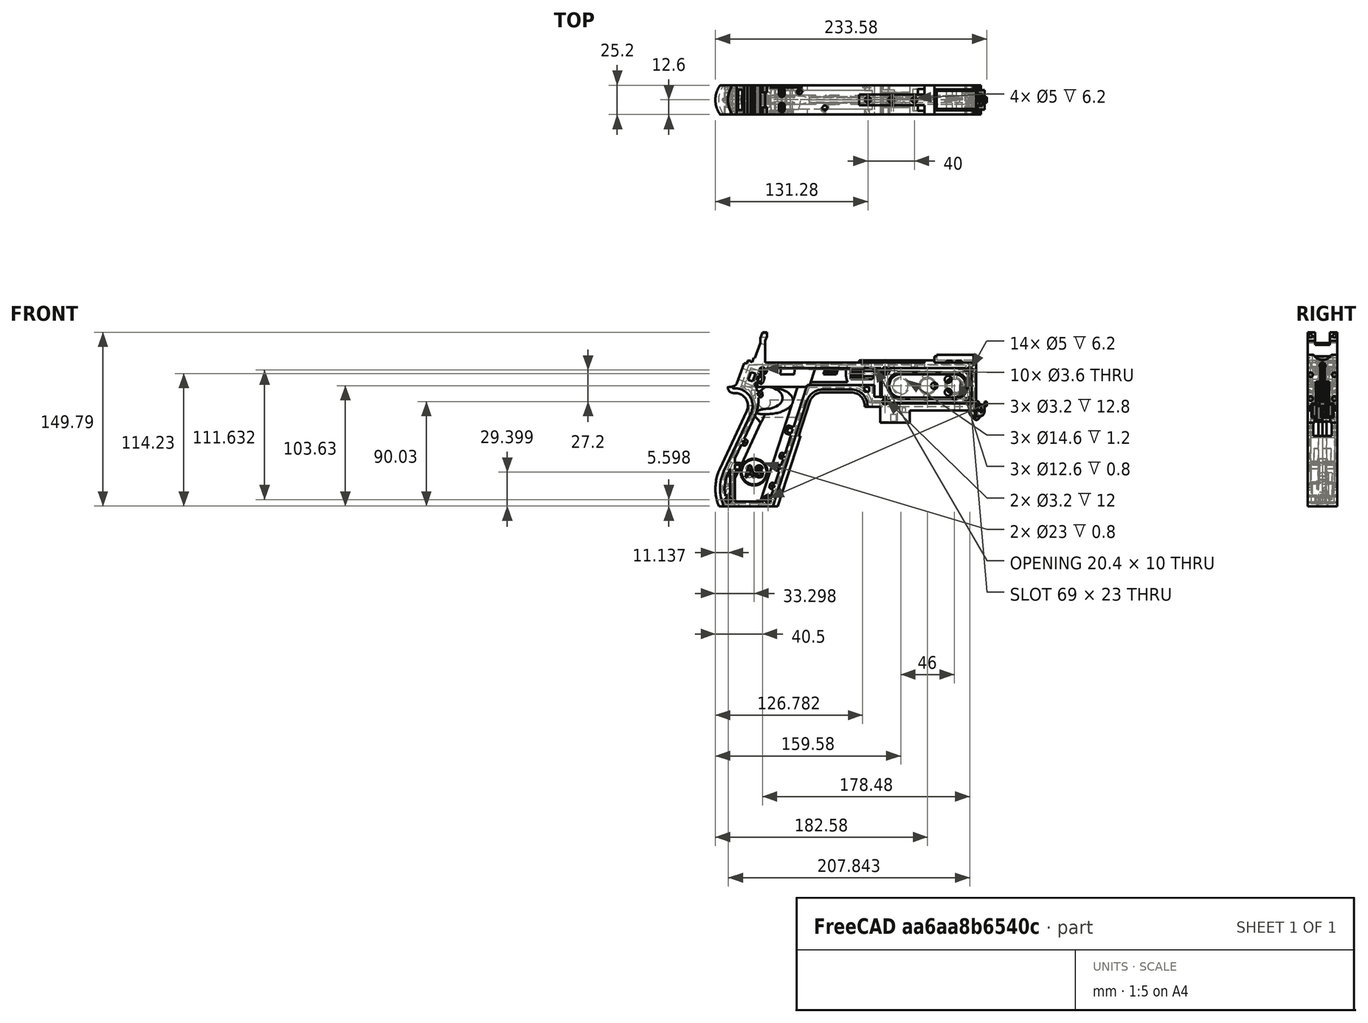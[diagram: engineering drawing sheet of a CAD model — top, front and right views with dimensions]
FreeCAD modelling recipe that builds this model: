
FCSTD DOCUMENT  (FreeCAD 1.0R39319 (Git))
Label: PICON-OF_ver_52
License: All rights reserved
LicenseURL: https://en.wikipedia.org/wiki/All_rights_reserved
objects: Sketcher::SketchObject×123, Part::Extrusion×63, Part::Cut×48, PartDesign::Pad×29, PartDesign::Pocket×20, PartDesign::Chamfer×15, PartDesign::Body×10, PartDesign::Fillet×6, Part::MultiFuse×5, Part::Part2DObjectPython×4, PartDesign::SubtractivePipe×4, PartDesign::SubtractiveLoft×4, PartDesign::Plane×3, PartDesign::SubShapeBinder×2, Part::Sweep×1, PartDesign::ShapeBinder×1, Mesh::Feature×1, PartDesign::Point×1, PartDesign::Groove×1
note: 621 computed .brp shape members not serialized (recipe doc carries the construction recipe); baked Part::Feature solids carry a one-line shape summary decoded from their .brp

FEATURE [Sketcher::SketchObject] Sketch  label="corpo principale"
  ArcFitTolerance = 1e-06
  AttacherType = Attacher::AttachEngine3D
  AttachmentSupport = -> [XZ_Plane]
  FullyConstrained = true
  MakeInternals = false
  MapMode = 5
  Placement = pos=(0,0,0) rot=(1,0,0;1.5708rad)
  sketch-geometry (65):
    g0: LineSegment StartX=0 StartY=0 StartZ=0 EndX=-57.2 EndY=0 EndZ=0
    g1: LineSegment StartX=-57.2 StartY=0 StartZ=0 EndX=-57.2 EndY=-10.4 EndZ=0
    g2: LineSegment StartX=-57.2 StartY=-10.4 StartZ=0 EndX=-82.8 EndY=-10.4 EndZ=0
    g3: LineSegment StartX=-82.8 StartY=-10.4 StartZ=0 EndX=-82.8 EndY=3.2 EndZ=0
    g4: LineSegment StartX=-82.8 StartY=3.2 StartZ=0 EndX=-93.6 EndY=3.2 EndZ=0
    g5: LineSegment StartX=-93.6 StartY=3.2 StartZ=0 EndX=-93.6 EndY=4 EndZ=0
    g6: LineSegment StartX=-107.6 StartY=18 StartZ=0 EndX=-132.428 EndY=18 EndZ=0
    g7: LineSegment StartX=-145.743 StartY=8.32624 StartZ=0 EndX=-175.232 EndY=-82.4316 EndZ=0
    g8: LineSegment StartX=-175.232 StartY=-82.4316 StartZ=0 EndX=-217.232 EndY=-82.4316 EndZ=0
    g9: LineSegment StartX=-217.232 StartY=-52.1862 StartZ=0 EndX=-193.988 EndY=-2.33927 EndZ=0
    g10: LineSegment StartX=-206.196 StartY=23.0857 StartZ=0 EndX=-199.861 EndY=40.4914 EndZ=0
    g11: LineSegment StartX=-199.861 StartY=40.4914 StartZ=0 EndX=-197.061 EndY=40.4914 EndZ=0
    g12: LineSegment StartX=-197.061 StartY=40.4914 StartZ=0 EndX=-197.061 EndY=42.8914 EndZ=0
    g13: LineSegment StartX=-197.061 StartY=42.8914 StartZ=0 EndX=-194.261 EndY=42.8914 EndZ=0
    g14: LineSegment StartX=-194.261 StartY=42.8914 StartZ=0 EndX=-194.535 EndY=42.1397 EndZ=0
    g15: LineSegment StartX=-194.535 StartY=42.1397 StartZ=0 EndX=-193.031 EndY=41.5924 EndZ=0
    g16: LineSegment StartX=-193.031 StartY=41.5924 StartZ=0 EndX=-191.663 EndY=45.3512 EndZ=0
    g17: LineSegment StartX=-191.663 StartY=45.3512 StartZ=0 EndX=-190.536 EndY=44.9408 EndZ=0
    g18: LineSegment StartX=-190.536 StartY=44.9408 StartZ=0 EndX=-185.747 EndY=58.0965 EndZ=0
    g19: LineSegment StartX=-185.747 StartY=58.0965 StartZ=0 EndX=-185.747 EndY=62.0965 EndZ=0
    g20: LineSegment StartX=-185.747 StartY=62.0965 StartZ=0 EndX=-183.832 EndY=67.3588 EndZ=0
    g21: LineSegment StartX=-183.832 StartY=67.3588 StartZ=0 EndX=-180.232 EndY=67.3588 EndZ=0
    g22: LineSegment StartX=-180.232 StartY=67.3588 StartZ=0 EndX=-180.232 EndY=63.7588 EndZ=0
    g23: LineSegment StartX=-180.232 StartY=63.7588 StartZ=0 EndX=-181.6 EndY=60 EndZ=0
    g24: LineSegment StartX=-181.6 StartY=60 StartZ=0 EndX=-181.6 EndY=41.2 EndZ=0
    g25: LineSegment StartX=-181.6 StartY=41.2 StartZ=0 EndX=-100.8 EndY=41.2 EndZ=0
    g26: LineSegment StartX=-36 StartY=43.2 StartZ=0 EndX=-36 EndY=41.2 EndZ=0
    g27: LineSegment StartX=0 StartY=48 StartZ=0 EndX=0 EndY=0 EndZ=0
    g28: LineSegment StartX=-209.901 StartY=19.85 StartZ=0 EndX=-209.901 EndY=20.1 EndZ=0
    g29: LineSegment StartX=-208.001 StartY=22 StartZ=0 EndX=-207.747 EndY=22 EndZ=0
    g30: LineSegment StartX=-207.583 StartY=19 StartZ=0 EndX=-209.051 EndY=19 EndZ=0
    g31: ArcOfCircle CenterX=-208.001 CenterY=20.1 CenterZ=0 NormalX=0 NormalY=0 NormalZ=1 AngleXU=0 Radius=1.9 StartAngle=1.5708 EndAngle=3.14159
    g32: GeomPoint [constr] X=-209.901 Y=22 Z=0
    g33: ArcOfCircle CenterX=-209.051 CenterY=19.85 CenterZ=0 NormalX=0 NormalY=0 NormalZ=1 AngleXU=0 Radius=0.85 StartAngle=3.14159 EndAngle=4.71239
    g34: GeomPoint [constr] X=-209.901 Y=19 Z=0
    g35: ArcOfCircle CenterX=-207.747 CenterY=23.65 CenterZ=0 NormalX=0 NormalY=0 NormalZ=1 AngleXU=0 Radius=1.65 StartAngle=4.71239 EndAngle=5.93412
    g36: GeomPoint [constr] X=-206.591 Y=22 Z=0
    g37: LineSegment StartX=-4 StartY=6 StartZ=0 EndX=-4 EndY=36.4 EndZ=0
    g38: LineSegment StartX=-4 StartY=36.4 StartZ=0 EndX=-185.2 EndY=36.4 EndZ=0
    g39: LineSegment StartX=-185.2 StartY=36.4 StartZ=0 EndX=-190.441 EndY=22 EndZ=0
    g40: LineSegment StartX=-214.575 StartY=-78.4316 StartZ=0 EndX=-178.142 EndY=-78.4316 EndZ=0
    g41: LineSegment StartX=-178.142 StartY=-78.4316 StartZ=0 EndX=-145.51 EndY=22 EndZ=0
    g42: LineSegment StartX=-145.51 StartY=22 StartZ=0 EndX=-87.91 EndY=22 EndZ=0
    g43: LineSegment StartX=-87.91 StartY=22 StartZ=0 EndX=-87.91 EndY=11.6 EndZ=0
    g44: LineSegment StartX=-87.91 StartY=11.6 StartZ=0 EndX=-80.11 EndY=11.6 EndZ=0
    g45: LineSegment StartX=-80.11 StartY=11.6 StartZ=0 EndX=-80.11 EndY=6 EndZ=0
    g46: LineSegment StartX=-80.11 StartY=6 StartZ=0 EndX=-4 EndY=6 EndZ=0
    g47: LineSegment StartX=-190.363 StartY=-4.02975 StartZ=0 EndX=-213.607 EndY=-53.8767 EndZ=0
    g48: ArcOfCircle CenterX=-132.428 CenterY=4 CenterZ=0 NormalX=0 NormalY=0 NormalZ=1 AngleXU=0 Radius=14 StartAngle=1.5708 EndAngle=2.82743
    g49: GeomPoint [constr] X=-142.6 Y=18 Z=0
    g50: ArcOfCircle CenterX=-107.6 CenterY=4 CenterZ=0 NormalX=0 NormalY=0 NormalZ=1 AngleXU=0 Radius=14 StartAngle=0 EndAngle=1.5708
    g51: GeomPoint [constr] X=-93.6 Y=18 Z=0
    g52: ArcOfCircle CenterX=-184.801 CenterY=-67.3089 CenterZ=0 NormalX=0 NormalY=0 NormalZ=1 AngleXU=0 Radius=35.7833 StartAngle=2.70526 EndAngle=3.57792
    g53: ArcOfCircle CenterX=-207.583 CenterY=4 CenterZ=0 NormalX=0 NormalY=0 NormalZ=1 AngleXU=0 Radius=15 StartAngle=5.84685 EndAngle=7.85398
    g54: LineSegment [constr] StartX=-213.607 StartY=-53.8767 StartZ=0 EndX=-217.232 EndY=-52.1862 EndZ=0
    g55: ArcOfCircle CenterX=-184.801 CenterY=-67.3089 CenterZ=0 NormalX=0 NormalY=0 NormalZ=1 AngleXU=0 Radius=31.7833 StartAngle=2.70526 EndAngle=3.49911
    g56: ArcOfCircle CenterX=-218.095 CenterY=8.90192 CenterZ=0 NormalX=0 NormalY=0 NormalZ=1 AngleXU=0 Radius=30.5989 StartAngle=5.84685 EndAngle=6.72553
    g57: LineSegment StartX=-44.6 StartY=43.2 StartZ=0 EndX=-36 EndY=43.2 EndZ=0
    g58: LineSegment StartX=-100.8 StartY=41.2 StartZ=0 EndX=-44.6 EndY=41.2 EndZ=0
    g59: LineSegment StartX=-44.6 StartY=41.2 StartZ=0 EndX=-44.6 EndY=43.2 EndZ=0
    g60: LineSegment StartX=-2.4 StartY=48 StartZ=0 EndX=0 EndY=48 EndZ=0
    g61: LineSegment StartX=-36 StartY=41.2 StartZ=0 EndX=-2.4 EndY=41.2 EndZ=0
    g62: LineSegment StartX=-2.4 StartY=41.2 StartZ=0 EndX=-2.4 EndY=48 EndZ=0
    g63: LineSegment [constr] StartX=-181.6 StartY=36.4 StartZ=0 EndX=-152.209 EndY=36.4 EndZ=0
    g64: LineSegment [constr] StartX=-181.6 StartY=36.4 StartZ=0 EndX=-130.41 EndY=36.4 EndZ=0
  constraints (183):
    c: Coincident(g-1,g0)
    c: PointOnObject(g0,g-1)
    c: Coincident(g0,g1)
    c: Vertical(g1)
    c: Coincident(g1,g2)
    c: Horizontal(g2)
    c: Coincident(g2,g3)
    c: Vertical(g3)
    c: Coincident(g3,g4)
    c: Coincident(g4,g5)
    c: Vertical(g5)
    c: Horizontal(g6)
    c: Coincident(g7,g8)
    c: Horizontal(g8)
    c: Coincident(g10,g11)
    c: Horizontal(g11)
    c: Coincident(g11,g12)
    c: Vertical(g12)
    c: Coincident(g12,g13)
    c: Horizontal(g13)
    c: Coincident(g13,g14)
    c: Coincident(g14,g15)
    c: Coincident(g15,g16)
    c: Coincident(g16,g17)
    c: Coincident(g17,g18)
    c: Coincident(g18,g19)
    c: Vertical(g19)
    c: Coincident(g19,g20)
    c: Coincident(g20,g21)
    c: Horizontal(g21)
    c: Coincident(g21,g22)
    c: Vertical(g22)
    c: Coincident(g22,g23)
    c: Coincident(g23,g24)
    c: Vertical(g24)
    c: Coincident(g24,g25)
    c: Horizontal(g25)
    c: Coincident(g57,g26)
    c: Vertical(g26)
    c: Coincident(g26,g61)
    c: PointOnObject(g60,g-2)
    c: Coincident(g60,g27)
    c: Coincident(g27,g0)
    c: DistanceY(g27,g27) = 48
    c: DistanceY(g1,g1) = 10.4
    c: DistanceX(g0,g0) = 57.2
    c: DistanceX(g2,g2) = 25.6
    c: Horizontal(g4)
    c: DistanceY(g3,g3) = 13.6
    c: DistanceX(g4,g4) = 10.8
    c: DistanceY(g5,g51) = 14.8
    c: DistanceX(g49,g51) = 49
    c: Distance(g7,g49) = 105.6
    c: DistanceX(g61,g60) = 36
    c: DistanceX(g25,g25) = 80.8
    c: DistanceY(g24,g24) = 18.8
    c: DistanceY(g22,g22) = 3.6
    c: Distance(g23) = 4
    c: Angle(g-1,g23) = 1.22173
    c: DistanceX(g21,g21) = 3.6
    c: Distance(g20) = 5.6
    c: Angle(g-1,g20) = 1.22173
    c: DistanceY(g19,g19) = 4
    c: Distance(g18) = 14
    c: Angle(g-1,g18) = 1.22173
    c: Distance(g17) = 1.2
    c: Distance(g16) = 4
    c: Angle(g16) = 1.22173
    c: Perpendicular(g18,g17)
    c: Distance(g15) = 1.6
    c: Perpendicular(g16,g15)
    c: Distance(g14) = 0.8
    c: DistanceX(g13,g13) = 2.8
    c: Perpendicular(g15,g14)
    c: DistanceY(g12,g12) = 2.4
    c: DistanceX(g11,g11) = 2.8
    c: Distance(g9) = 55
    c: Angle(g9,g-1) = 2.00713
    c: Horizontal(g29)
    c: Vertical(g28)
    c: Horizontal(g30)
    c: PointOnObject(g32,g29)
    c: PointOnObject(g32,g28)
    c: Tangent(g29,g31) = 1.5708
    c: Tangent(g28,g31) = 1.5708
    c: PointOnObject(g34,g28)
    c: PointOnObject(g34,g30)
    c: Tangent(g28,g33) = 1.5708
    c: Tangent(g30,g33) = 1.5708
    c: PointOnObject(g36,g29)
    c: PointOnObject(g36,g10)
    c: Tangent(g29,g35) = -1.5708
    c: Tangent(g10,g35) = -1.5708
    c: Angle(g-1,g10) = 1.22173
    c: Radius(g35) = 1.65
    c: Vertical(g37)
    c: Coincident(g37,g38)
    c: Horizontal(g38)
    c: Coincident(g38,g39)
    c: Horizontal(g40)
    c: Coincident(g40,g41)
    c: Coincident(g41,g42)
    c: Horizontal(g42)
    c: Coincident(g42,g43)
    c: Vertical(g43)
    c: Coincident(g43,g44)
    c: Horizontal(g44)
    c: Coincident(g44,g45)
    c: Vertical(g45)
    c: Coincident(g45,g46)
    c: Coincident(g46,g37)
    c: Horizontal(g46)
    c: DistanceY(g0,g37) = 6
    c: DistanceX(g37,g0) = 4
    c: DistanceY(g37,g25) = 4.8
    c: DistanceX(g38,g38) = 181.2
    c: DistanceX(g42,g42) = 57.6
    c: DistanceY(g49,g41) = 4
    c: DistanceX(g41,g49) = 2.91
    c: DistanceY(g43,g43) = 10.4
    c: DistanceX(g44,g44) = 7.8
    c: DistanceY(g7,g40) = 4
    c: Distance(g47) = 55
    c: Angle(g-1,g39) = 1.22173
    c: PointOnObject(g49,g7)
    c: PointOnObject(g49,g6)
    c: Tangent(g7,g48) = -1.5708
    c: Tangent(g6,g48) = -1.5708
    c: PointOnObject(g51,g5)
    c: PointOnObject(g51,g6)
    c: Tangent(g5,g50) = -1.5708
    c: Tangent(g6,g50) = -1.5708
    c: Radius(g50) = 14
    c: Radius(g48) = 14
    c: DistanceX(g8,g8) = 42
    c: Angle(g7,g-1) = 1.88496
    c: Parallel(g41,g7)
    c: Parallel(g47,g9)
    c: Coincident(g52,g8)
    c: Tangent(g52,g9) = 1.5708
    c: DistanceX(g9,g8) = 0
    c: Tangent(g53,g9) = -1.5708
    c: Tangent(g53,g30) = -1.5708
    c: Diameter(g53) = 30
    c: DistanceY(g53,g0) = -4
    c: Coincident(g54,g47)
    c: Distance(g54) = 4
    c: Coincident(g54,g9)
    c: Coincident(g55,g40)
    c: Tangent(g55,g47) = -1.5708
    c: Coincident(g52,g55)
    c: Coincident(g56,g39)
    c: Tangent(g56,g47) = 1.5708
    c: Horizontal(g57)
    c: DistanceX(g57,g57) = 8.6
    c: Coincident(g58,g25)
    c: Horizontal(g58)
    c: Coincident(g59,g58)
    c: Vertical(g59)
    c: DistanceY(g58,g57) = 2
    c: DistanceX(g58,g58) = 56.2
    c: Coincident(g59,g57)
    c: DistanceY(g41,g36) = 0
    c: DistanceY(g36,g39) = 0
    c: DistanceY(g28,g28) = 0.25
    c: DistanceX(g30,g36) = 2.46
    c: DistanceX(g28,g29) = 1.9
    c: Coincident(g62,g60)
    c: Horizontal(g60)
    c: DistanceX(g62,g27) = 2.4
    c: Coincident(g61,g62)
    c: DistanceY(g26,g26) = 2
    c: Vertical(g62)
    c: DistanceY(g61,g60) = 6.8
    c: Horizontal(g61)
    c: Distance(g63) = 29.391
    c: PointOnObject(g63,g38)
    c: PointOnObject(g63,g38)
    c: Distance(g64) = 51.19
    c: PointOnObject(g64,g38)
    c: PointOnObject(g64,g38)
    c: DistanceX(g24,g63) = 0
    c: DistanceX(g24,g64) = 0
FEATURE [Part::Extrusion] Extrude  label="Extrude corpo principale"
  Base = -> Sketch
  Dir = (0,-1,2e-16)
  DirMode = 2
  FaceMakerClass = Part::FaceMakerBullseye
  FaceMakerMode = 3
  LengthFwd = 25.2
  LengthRev = 12.6
  Solid = true
  Symmetric = true
FEATURE [Sketcher::SketchObject] Sketch002  label="scavo grilletto"
  ArcFitTolerance = 1e-06
  AttachmentSupport = -> [XZ_Plane]
  ExternalGeometry = -> [Sketch]
  FullyConstrained = true
  MakeInternals = false
  MapMode = 5
  Placement = pos=(0,0,0) rot=(1,0,0;1.5708rad)
  sketch-geometry (4):
    g0: LineSegment StartX=-89.51 StartY=22 StartZ=0 EndX=-152.71 EndY=22 EndZ=0
    g1: LineSegment StartX=-152.71 StartY=22 StartZ=0 EndX=-167.006 EndY=-22 EndZ=0
    g2: LineSegment StartX=-167.006 StartY=-22 StartZ=0 EndX=-89.51 EndY=-22 EndZ=0
    g3: LineSegment StartX=-89.51 StartY=-22 StartZ=0 EndX=-89.51 EndY=22 EndZ=0
  constraints (12):
    c: Horizontal(g0)
    c: Coincident(g0,g1)
    c: Coincident(g1,g2)
    c: Horizontal(g2)
    c: Coincident(g2,g3)
    c: Coincident(g3,g0)
    c: Vertical(g3)
    c: Angle(g1,g0) = 1.88496
    c: DistanceY(g3,g3) = 44
    c: DistanceX(g0,g0) = 63.2
    c: DistanceX(g0,g-3) = 1.6
    c: DistanceY(g-3,g0) = 0
FEATURE [Sketcher::SketchObject] Sketch004  label="traiettoria arrotondamento impugnatura anteriore"
  ArcFitTolerance = 1e-06
  AttachmentSupport = -> [XZ_Plane]
  ExternalGeometry = -> [Sketch]
  FullyConstrained = true
  MakeInternals = false
  MapMode = 5
  Placement = pos=(0,0,0) rot=(1,0,0;1.5708rad)
  sketch-geometry (13):
    g0: LineSegment StartX=-175.232 StartY=-82.4316 StartZ=0 EndX=-145.743 EndY=8.32624 EndZ=0
    g1: LineSegment StartX=-93.6 StartY=3.2 StartZ=0 EndX=-93.6 EndY=4 EndZ=0
    g2: LineSegment StartX=-132.428 StartY=18 StartZ=0 EndX=-107.6 EndY=18 EndZ=0
    g3: ArcOfCircle CenterX=-132.428 CenterY=4 CenterZ=0 NormalX=0 NormalY=0 NormalZ=1 AngleXU=0 Radius=14 StartAngle=1.5708 EndAngle=2.82743
    g4: ArcOfCircle CenterX=-107.6 CenterY=4 CenterZ=0 NormalX=0 NormalY=0 NormalZ=1 AngleXU=0 Radius=14 StartAngle=0 EndAngle=1.5708
    g5: LineSegment StartX=-175.232 StartY=-82.4316 StartZ=0 EndX=-217.232 EndY=-82.4316 EndZ=0
    g6: LineSegment StartX=-217.232 StartY=-52.1862 StartZ=0 EndX=-193.988 EndY=-2.33927 EndZ=0
    g7: LineSegment StartX=-209.051 StartY=19 StartZ=0 EndX=-207.583 EndY=19 EndZ=0
    g8: LineSegment StartX=-209.901 StartY=20.1 StartZ=0 EndX=-209.901 EndY=19.85 EndZ=0
    g9: ArcOfCircle CenterX=-184.801 CenterY=-67.3089 CenterZ=0 NormalX=0 NormalY=0 NormalZ=1 AngleXU=0 Radius=35.7833 StartAngle=2.70526 EndAngle=3.57792
    g10: ArcOfCircle CenterX=-207.583 CenterY=4 CenterZ=0 NormalX=0 NormalY=0 NormalZ=1 AngleXU=0 Radius=15 StartAngle=5.84685 EndAngle=7.85398
    g11: ArcOfCircle CenterX=-209.051 CenterY=19.85 CenterZ=0 NormalX=0 NormalY=0 NormalZ=1 AngleXU=0 Radius=0.85 StartAngle=3.14159 EndAngle=4.71239
    g12: ArcOfCircle CenterX=-208.001 CenterY=20.1 CenterZ=0 NormalX=0 NormalY=0 NormalZ=1 AngleXU=0 Radius=1.9 StartAngle=1.5708 EndAngle=3.14159
  constraints (26):
    c: Coincident(g0,g-3)
    c: Coincident(g0,g-6)
    c: Coincident(g1,g-8)
    c: Coincident(g1,g-7)
    c: Coincident(g2,g-5)
    c: Coincident(g2,g-4)
    c: Coincident(g3,g2)
    c: Tangent(g3,g0) = 1.5708
    c: Coincident(g4,g1)
    c: Tangent(g4,g2) = 1.5708
    c: Coincident(g5,g0)
    c: Coincident(g5,g-9)
    c: Coincident(g6,g-12)
    c: Coincident(g6,g-11)
    c: Coincident(g7,g-15)
    c: Coincident(g7,g-14)
    c: Coincident(g8,g-16)
    c: Coincident(g8,g-17)
    c: Tangent(g9,g6) = 1.5708
    c: Coincident(g9,g5)
    c: Coincident(g10,g7)
    c: Tangent(g10,g6) = -1.5708
    c: Tangent(g11,g7) = -1.5708
    c: Coincident(g11,g8)
    c: Tangent(g12,g8) = -1.5708
    c: Coincident(g12,g-17)
FEATURE [PartDesign::Plane] DatumPlane  label="Piano per disegno arrotondamento impugnatura"
  AttachmentSupport = -> [Sketch]
  Length = 73.6581
  MapMode = 7
  Placement = pos=(-145.743,1.8e-15,8.32624) rot=(0.154555,0.154555,0.97582;1.59527rad)
  ResizeMode = 0
  Width = 303.511
FEATURE [Sketcher::SketchObject] Sketch005  label="forma arrotondamento impugnatura anteriore"
  ArcFitTolerance = 1e-06
  AttachmentSupport = -> [DatumPlane]
  FullyConstrained = true
  MakeInternals = false
  MapMode = 5
  Placement = pos=(-145.743,1.8e-15,8.32624) rot=(0.154555,0.154555,0.97582;1.59527rad)
  sketch-geometry (5):
    g0: GeomPoint [constr] X=0 Y=-4 Z=0
    g1: GeomPoint [constr] X=-12.6 Y=7.1e-15 Z=0
    g2: GeomPoint [constr] X=12.6 Y=4.97e-14 Z=0
    g3: LineSegment StartX=-12.6 StartY=7.1e-15 StartZ=0 EndX=12.6 EndY=4.97e-14 EndZ=0
    g4: ArcOfCircle CenterX=-3.88e-14 CenterY=17.845 CenterZ=0 NormalX=0 NormalY=0 NormalZ=1 AngleXU=0 Radius=21.845 StartAngle=4.09759 EndAngle=5.32718
  constraints (11):
    c: DistanceY(g0,g-1) = 4
    c: DistanceX(g-1,g0) = 0
    c: DistanceX(g1,g-1) = 12.6
    c: DistanceX(g-1,g2) = 12.6
    c: DistanceY(g-1,g2) = 0
    c: DistanceY(g-1,g1) = 0
    c: Coincident(g3,g1)
    c: Coincident(g3,g2)
    c: Coincident(g4,g1)
    c: Coincident(g4,g2)
    c: PointOnObject(g0,g4)
FEATURE [Part::Sweep] Sweep  label="Sweep impugnatura"
  Frenet = true
  Sections = -> [Sketch005]
  Solid = true
  Spine = -> Sketch [Edge32,Edge33,Edge34,Edge35,Edge36,Edge37,Edge38,Edge39,Edge40,Edge41,Edge42,Edge43,Edge44]
  Transition = 1
FEATURE [Sketcher::SketchObject] Sketch008  label="buchi e pulizie varie"
  ArcFitTolerance = 1e-06
  AttachmentSupport = -> [XZ_Plane]
  ExternalGeometry = -> [Sketch]
  FullyConstrained = true
  MakeInternals = false
  MapMode = 5
  Placement = pos=(0,0,0) rot=(1,0,0;1.5708rad)
  sketch-geometry (26):
    g0: LineSegment StartX=-96.278 StartY=20.155 StartZ=0 EndX=-92.278 EndY=20.155 EndZ=0
    g1: LineSegment StartX=-92.278 StartY=20.155 StartZ=0 EndX=-92.278 EndY=16.155 EndZ=0
    g2: LineSegment StartX=-92.278 StartY=16.155 StartZ=0 EndX=-96.278 EndY=16.155 EndZ=0
    g3: LineSegment StartX=-96.278 StartY=16.155 StartZ=0 EndX=-96.278 EndY=20.155 EndZ=0
    g4: LineSegment StartX=-222.232 StartY=-82.4316 StartZ=0 EndX=-170.232 EndY=-82.4316 EndZ=0
    g5: LineSegment StartX=-170.232 StartY=-82.4316 StartZ=0 EndX=-170.232 EndY=-86.4316 EndZ=0
    g6: LineSegment StartX=-170.232 StartY=-86.4316 StartZ=0 EndX=-222.232 EndY=-86.4316 EndZ=0
    g7: LineSegment StartX=-222.232 StartY=-86.4316 StartZ=0 EndX=-222.232 EndY=-82.4316 EndZ=0
    g8: LineSegment StartX=-213.901 StartY=20.1 StartZ=0 EndX=-213.901 EndY=26 EndZ=0
    g9: LineSegment StartX=-213.901 StartY=26 StartZ=0 EndX=-206.196 EndY=26 EndZ=0
    g10: LineSegment StartX=-17.4 StartY=42.8 StartZ=0 EndX=-12.4 EndY=42.8 EndZ=0
    g11: LineSegment StartX=-12.4 StartY=42.8 StartZ=0 EndX=-12.4 EndY=41.2 EndZ=0
    g12: LineSegment StartX=-12.4 StartY=41.2 StartZ=0 EndX=-17.4 EndY=41.2 EndZ=0
    g13: LineSegment StartX=-17.4 StartY=41.2 StartZ=0 EndX=-17.4 EndY=42.8 EndZ=0
    g14: LineSegment StartX=-25.9 StartY=42.8 StartZ=0 EndX=-20.9 EndY=42.8 EndZ=0
    g15: LineSegment StartX=-20.9 StartY=42.8 StartZ=0 EndX=-20.9 EndY=41.2 EndZ=0
    g16: LineSegment StartX=-20.9 StartY=41.2 StartZ=0 EndX=-25.9 EndY=41.2 EndZ=0
    g17: LineSegment StartX=-25.9 StartY=41.2 StartZ=0 EndX=-25.9 EndY=42.8 EndZ=0
    g18: GeomPoint [constr] X=-206.196 Y=23.0857 Z=0
    g19: GeomPoint [constr] X=-213.901 Y=20.1 Z=0
    g20: BSplineCurve PolesCount=4 KnotsCount=2 Degree=3 IsPeriodic=0
    g21-g24: Circle [constr] x4 (B-spline internal-alignment scaffolding for g20; pole/knot coordinates omitted)
    g25: LineSegment StartX=-206.196 StartY=26 StartZ=0 EndX=-206.196 EndY=23.0857 EndZ=0
  constraints (73):
    c: Horizontal(g0)
    c: Coincident(g1,g0)
    c: Vertical(g1)
    c: Coincident(g2,g1)
    c: Horizontal(g2)
    c: Coincident(g3,g2)
    c: Coincident(g3,g0)
    c: Vertical(g3)
    c: DistanceX(g0,g-4) = 4.368
    c: DistanceY(g0,g-4) = 1.845
    c: DistanceY(g1,g1) = 4
    c: DistanceX(g2,g2) = 4
    c: Horizontal(g4)
    c: Coincident(g5,g4)
    c: Vertical(g5)
    c: Coincident(g6,g5)
    c: Horizontal(g6)
    c: Coincident(g7,g6)
    c: Coincident(g7,g4)
    c: Vertical(g7)
    c: DistanceY(g7,g7) = 4
    c: DistanceX(g4,g-5) = 5
    c: DistanceX(g-5,g4) = 5
    c: DistanceY(g4,g-5) = 0
    c: Coincident(g9,g8)
    c: Parallel(g9,g-6)
    c: DistanceX(g8,g-8) = 4
    c: Horizontal(g10)
    c: Coincident(g11,g10)
    c: Vertical(g11)
    c: Coincident(g12,g11)
    c: Horizontal(g12)
    c: Coincident(g13,g12)
    c: Coincident(g13,g10)
    c: Vertical(g13)
    c: Horizontal(g14)
    c: Coincident(g15,g14)
    c: Vertical(g15)
    c: Coincident(g16,g15)
    c: Horizontal(g16)
    c: Coincident(g17,g16)
    c: Coincident(g17,g14)
    c: Vertical(g17)
    c: DistanceY(g11,g10) = 1.6
    c: DistanceX(g10,g10) = 5
    c: DistanceY(g15,g14) = 1.6
    c: DistanceX(g14,g14) = 5
    c: DistanceX(g15,g12) = 3.5
    c: DistanceX(g11,g-9) = 10
    c: DistanceY(g-9,g11) = 0
    c: DistanceY(g-9,g15) = 0
    c: Perpendicular(g8,g9)
    c: DistanceY(g-7,g9) = 4
    c: DistanceY(g8,g-8) = 0
    c: InternalAlignment(g18,g20)
    c: InternalAlignment(g19,g20)
    c: InternalAlignment(g21,g20)
    c: Weight(g21) = 1
    c: InternalAlignment(g22,g20)
    c: Equal(g22,g21)
    c: InternalAlignment(g23,g20)
    c: Equal(g23,g21)
    c: InternalAlignment(g24,g20)
    c: Equal(g24,g21)
    c: Coincident(g18,g-12)
    c: Coincident(g19,g8)
    c: Coincident(g25,g9)
    c: Coincident(g25,g20)
    c: Vertical(g25)
    c: DistanceY(g20,g23) = 0
    c: DistanceY(g22,g18) = 2.26
    c: DistanceX(g22,g18) = 0.93
    c: DistanceX(g20,g23) = 2.9
FEATURE [Part::Extrusion] Extrude004  label="Extrude Buchi e pulizie varie"
  Base = -> Sketch008
  Dir = (0,-1,2e-16)
  DirMode = 2
  FaceMakerClass = Part::FaceMakerBullseye
  FaceMakerMode = 3
  LengthFwd = 25.2
  LengthRev = 0
  Solid = true
  Symmetric = true
FEATURE [Sketcher::SketchObject] Sketch009  label="rinforzi"
  ArcFitTolerance = 1e-06
  AttachmentSupport = -> [XZ_Plane]
  ExternalGeometry = -> [Sketch]
  FullyConstrained = true
  MakeInternals = false
  MapMode = 5
  Placement = pos=(0,0,0) rot=(1,0,0;1.5708rad)
  sketch-geometry (9):
    g0: LineSegment StartX=-87.91 StartY=22 StartZ=0 EndX=-87.91 EndY=36.4 EndZ=0
    g1: LineSegment StartX=-87.91 StartY=36.4 StartZ=0 EndX=-97.91 EndY=36.4 EndZ=0
    g2: LineSegment StartX=-97.91 StartY=36.4 StartZ=0 EndX=-97.91 EndY=22 EndZ=0
    g3: LineSegment StartX=-97.91 StartY=22 StartZ=0 EndX=-87.91 EndY=22 EndZ=0
    g4: LineSegment StartX=-149.713 StartY=9.06563 StartZ=0 EndX=-154.586 EndY=-5.93437 EndZ=0
    g5: LineSegment StartX=-154.586 StartY=-5.93437 StartZ=0 EndX=-191.863 EndY=-5.93437 EndZ=0
    g6: LineSegment StartX=-191.863 StartY=-5.93437 StartZ=0 EndX=-191.863 EndY=9.06563 EndZ=0
    g7: LineSegment StartX=-191.863 StartY=9.06563 StartZ=0 EndX=-149.713 EndY=9.06563 EndZ=0
    g8: LineSegment [constr] StartX=-145.51 StartY=22 StartZ=0 EndX=-149.713 EndY=9.06563 EndZ=0
  constraints (25):
    c: Vertical(g0)
    c: Coincident(g1,g0)
    c: Horizontal(g1)
    c: Coincident(g2,g1)
    c: Vertical(g2)
    c: Coincident(g3,g2)
    c: Coincident(g3,g0)
    c: Horizontal(g3)
    c: Coincident(g0,g-4)
    c: DistanceX(g3,g3) = 10
    c: DistanceY(g0,g-3) = 0
    c: Coincident(g5,g4)
    c: Horizontal(g5)
    c: Coincident(g6,g5)
    c: Vertical(g6)
    c: Coincident(g7,g6)
    c: Coincident(g7,g4)
    c: Horizontal(g7)
    c: Distance(g8) = 13.6
    c: Parallel(g-6,g8)
    c: Coincident(g-6,g8)
    c: Parallel(g4,g-6)
    c: DistanceY(g4,g4) = 15
    c: Coincident(g4,g8)
    c: DistanceX(g-5,g5) = -1.5
FEATURE [Part::Extrusion] Extrude001  label="Extrude scavo grilletto"
  Base = -> Sketch002
  Dir = (0,-1,2e-16)
  DirMode = 2
  FaceMakerClass = Part::FaceMakerBullseye
  FaceMakerMode = 3
  LengthFwd = 16
  LengthRev = 0
  Solid = true
  Symmetric = true
FEATURE [Part::Extrusion] Extrude005  label="Extrude Rinforzi"
  Base = -> Sketch009
  Dir = (0,-1,2e-16)
  DirMode = 2
  FaceMakerClass = Part::FaceMakerBullseye
  FaceMakerMode = 3
  LengthFwd = 2
  LengthRev = 0
  Placement = pos=(0,12.6,0) rot=(0,0,1;0rad)
  Solid = true
  Symmetric = false
FEATURE [PartDesign::ShapeBinder] CopyCut
  TraceSupport = false
FEATURE [PartDesign::Plane] DatumPlane001
  AttachmentSupport = -> [CopyCut]
  Length = 283.944
  MapMode = 5
  Placement = pos=(0,12.6,0) rot=(0,0.707107,0.707107;3.14159rad)
  ResizeMode = 0
  Width = 188.15
FEATURE [Sketcher::SketchObject] Sketch010  label="buco neopixel"
  ArcFitTolerance = 1e-06
  AttachmentSupport = -> [XZ_Plane]
  ExternalGeometry = -> [Sketch]
  FullyConstrained = true
  MakeInternals = false
  MapMode = 5
  Placement = pos=(0,0,0) rot=(1,0,0;1.5708rad)
  sketch-geometry (5):
    g0: LineSegment [constr] StartX=-199.861 StartY=40.4914 StartZ=0 EndX=-201.368 EndY=36.3521 EndZ=0
    g1: LineSegment StartX=-201.368 StartY=36.3521 StartZ=0 EndX=-204.932 EndY=26.5605 EndZ=0
    g2: LineSegment StartX=-201.368 StartY=36.3521 StartZ=0 EndX=-180.2 EndY=28.6477 EndZ=0
    g3: LineSegment StartX=-180.2 StartY=28.6477 StartZ=0 EndX=-183.764 EndY=18.8561 EndZ=0
    g4: LineSegment StartX=-183.764 StartY=18.8561 StartZ=0 EndX=-204.932 EndY=26.5605 EndZ=0
  constraints (14):
    c: Parallel(g0,g-3)
    c: Distance(g0) = 4.405
    c: Coincident(g0,g-3)
    c: Coincident(g2,g1)
    c: Coincident(g3,g2)
    c: Coincident(g4,g3)
    c: Coincident(g4,g1)
    c: Parallel(g1,g-3)
    c: Distance(g1) = 10.42
    c: Coincident(g1,g0)
    c: Parallel(g2,g4)
    c: Perpendicular(g1,g2)
    c: DistanceX(g-4,g2) = 5
    c: Parallel(g3,g1)
FEATURE [Part::Extrusion] Extrude006  label="Extrude buco neopixel"
  Base = -> Sketch010
  Dir = (0,-1,2e-16)
  DirMode = 2
  FaceMakerClass = Part::FaceMakerBullseye
  FaceMakerMode = 3
  LengthFwd = 17.2
  LengthRev = 0
  Solid = true
  Symmetric = true
FEATURE [Sketcher::SketchObject] Sketch011  label="fermo grilletto"
  ArcFitTolerance = 1e-06
  AttachmentSupport = -> [XZ_Plane]
  ExternalGeometry = -> [Sketch]
  FullyConstrained = true
  MakeInternals = false
  MapMode = 5
  Placement = pos=(0,0,0) rot=(1,0,0;1.5708rad)
  sketch-geometry (18):
    g0: LineSegment [constr] StartX=-145.51 StartY=22 StartZ=0 EndX=-157.347 EndY=-14.4293 EndZ=0
    g1: LineSegment [constr] StartX=-157.347 StartY=-14.4293 StartZ=0 EndX=-157.841 EndY=-15.951 EndZ=0
    g2: LineSegment StartX=-161.151 StartY=-13.1932 StartZ=0 EndX=-155.825 EndY=-14.9237 EndZ=0
    g3: LineSegment StartX=-163.167 StartY=-14.2205 StartZ=0 EndX=-164.403 EndY=-18.0247 EndZ=0
    g4: LineSegment StartX=-163.376 StartY=-20.0408 StartZ=0 EndX=-158.05 EndY=-21.7713 EndZ=0
    g5: LineSegment StartX=-158.05 StartY=-21.7713 StartZ=0 EndX=-155.825 EndY=-14.9237 EndZ=0
    g6: LineSegment StartX=-161.645 StartY=-14.7149 StartZ=0 EndX=-157.841 EndY=-15.951 EndZ=0
    g7: LineSegment StartX=-157.841 StartY=-15.951 StartZ=0 EndX=-159.077 EndY=-19.7552 EndZ=0
    g8: LineSegment StartX=-159.077 StartY=-19.7552 StartZ=0 EndX=-162.881 EndY=-18.5191 EndZ=0
    g9: LineSegment StartX=-162.881 StartY=-18.5191 StartZ=0 EndX=-161.645 EndY=-14.7149 EndZ=0
    g10: LineSegment [constr] StartX=-161.645 StartY=-14.7149 StartZ=0 EndX=-161.151 EndY=-13.1932 EndZ=0
    g11: LineSegment [constr] StartX=-159.077 StartY=-19.7552 StartZ=0 EndX=-157.555 EndY=-20.2496 EndZ=0
    g12: LineSegment [constr] StartX=-159.077 StartY=-19.7552 StartZ=0 EndX=-159.572 EndY=-21.2769 EndZ=0
    g13: LineSegment [constr] StartX=-161.645 StartY=-14.7149 StartZ=0 EndX=-163.167 EndY=-14.2205 EndZ=0
    g14: ArcOfCircle CenterX=-161.645 CenterY=-14.7149 CenterZ=0 NormalX=0 NormalY=0 NormalZ=1 AngleXU=0 Radius=1.6 StartAngle=1.25664 EndAngle=2.82743
    g15: GeomPoint [constr] X=-162.673 Y=-12.6988 Z=0
    g16: ArcOfCircle CenterX=-162.881 CenterY=-18.5191 CenterZ=0 NormalX=0 NormalY=0 NormalZ=1 AngleXU=0 Radius=1.6 StartAngle=2.82743 EndAngle=4.39823
    g17: GeomPoint [constr] X=-164.897 Y=-19.5464 Z=0
  constraints (48):
    c: Parallel(g0,g-3)
    c: Distance(g0) = 38.304
    c: Coincident(g0,g-3)
    c: Parallel(g1,g-3)
    c: Distance(g1) = 1.6
    c: Coincident(g1,g0)
    c: Coincident(g5,g4)
    c: Coincident(g5,g2)
    c: Coincident(g7,g6)
    c: Coincident(g8,g7)
    c: Coincident(g9,g8)
    c: Coincident(g9,g6)
    c: Parallel(g7,g-3)
    c: Parallel(g9,g7)
    c: Perpendicular(g6,g7)
    c: Parallel(g6,g8)
    c: Distance(g6) = 4
    c: Distance(g9) = 4
    c: Parallel(g5,g7)
    c: Parallel(g9,g3)
    c: Parallel(g2,g6)
    c: Parallel(g4,g8)
    c: Parallel(g13,g6)
    c: Parallel(g10,g9)
    c: Parallel(g11,g8)
    c: Parallel(g12,g7)
    c: Distance(g10) = 1.6
    c: Distance(g13) = 1.6
    c: Distance(g12) = 1.6
    c: Distance(g11) = 1.6
    c: Coincident(g10,g6)
    c: Coincident(g13,g6)
    c: Coincident(g12,g7)
    c: Coincident(g11,g7)
    c: Distance(g10,g15) = 1.6
    c: Distance(g15,g13) = 1.6
    c: Distance(g4,g12) = 1.6
    c: Distance(g4,g11) = 1.6
    c: PointOnObject(g15,g2)
    c: Tangent(g3,g14) = -1.5708
    c: Tangent(g2,g14) = 1.5708
    c: PointOnObject(g17,g4)
    c: PointOnObject(g17,g3)
    c: Tangent(g4,g16) = -1.5708
    c: Tangent(g3,g16) = -1.5708
    c: Equal(g16,g14)
    c: Coincident(g16,g8)
    c: Coincident(g6,g1)
FEATURE [Part::Extrusion] Extrude007  label="Extrude fermo grilletto"
  Base = -> Sketch011
  Dir = (0,-1,2e-16)
  DirMode = 2
  FaceMakerClass = Part::FaceMakerBullseye
  FaceMakerMode = 3
  LengthFwd = 25.2
  LengthRev = 0
  Solid = true
  Symmetric = true
FEATURE [Sketcher::SketchObject] Sketch012  label="buco oled"
  ArcFitTolerance = 1e-06
  AttachmentSupport = -> [XZ_Plane]
  ExternalGeometry = -> [Sketch]
  FullyConstrained = true
  MakeInternals = false
  MapMode = 5
  Placement = pos=(0,0,0) rot=(1,0,0;1.5708rad)
  sketch-geometry (4):
    g0: LineSegment StartX=-185.747 StartY=58.0965 StartZ=0 EndX=-180.232 EndY=56.0891 EndZ=0
    g1: LineSegment StartX=-185.747 StartY=58.0965 StartZ=0 EndX=-185.747 EndY=67.3588 EndZ=0
    g2: LineSegment StartX=-185.747 StartY=67.3588 StartZ=0 EndX=-180.232 EndY=67.3588 EndZ=0
    g3: LineSegment StartX=-180.232 StartY=67.3588 StartZ=0 EndX=-180.232 EndY=56.0891 EndZ=0
  constraints (10):
    c: Coincident(g1,g0)
    c: Coincident(g2,g1)
    c: Coincident(g3,g2)
    c: Coincident(g3,g0)
    c: Parallel(g1,g-5)
    c: Perpendicular(g-3,g0)
    c: Parallel(g2,g-6)
    c: Parallel(g3,g-4)
    c: Coincident(g0,g-5)
    c: Coincident(g2,g-6)
FEATURE [Part::Extrusion] Extrude008  label="Extrude buco oled"
  Base = -> Sketch012
  Dir = (0,-1,2e-16)
  DirMode = 2
  FaceMakerClass = Part::FaceMakerBullseye
  FaceMakerMode = 3
  LengthFwd = 12.8
  LengthRev = 0
  Solid = true
  Symmetric = true
FEATURE [Sketcher::SketchObject] Sketch013  label="buco pompa"
  ArcFitTolerance = 1e-06
  AttachmentSupport = -> [XZ_Plane]
  ExternalGeometry = -> [Sketch]
  FullyConstrained = true
  MakeInternals = false
  MapMode = 5
  Placement = pos=(0,0,0) rot=(1,0,0;1.5708rad)
  sketch-geometry (8):
    g0: LineSegment StartX=-82.8 StartY=-10.4 StartZ=0 EndX=-82.8 EndY=-9.6 EndZ=0
    g1: LineSegment StartX=-82.8 StartY=-9.6 StartZ=0 EndX=-67.9 EndY=-9.6 EndZ=0
    g2: LineSegment StartX=-67.9 StartY=-9.6 StartZ=0 EndX=-67.9 EndY=6 EndZ=0
    g3: LineSegment StartX=-67.9 StartY=6 StartZ=0 EndX=-65.9 EndY=6 EndZ=0
    g4: LineSegment StartX=-65.9 StartY=6 StartZ=0 EndX=-65.9 EndY=-1.7 EndZ=0
    g5: LineSegment StartX=-65.9 StartY=-1.7 StartZ=0 EndX=-57.2 EndY=-1.7 EndZ=0
    g6: LineSegment StartX=-57.2 StartY=-1.7 StartZ=0 EndX=-57.2 EndY=-10.4 EndZ=0
    g7: LineSegment StartX=-57.2 StartY=-10.4 StartZ=0 EndX=-82.8 EndY=-10.4 EndZ=0
  constraints (22):
    c: Vertical(g0)
    c: Coincident(g1,g0)
    c: Horizontal(g1)
    c: Coincident(g2,g1)
    c: Vertical(g2)
    c: Coincident(g3,g2)
    c: Horizontal(g3)
    c: Coincident(g4,g3)
    c: Vertical(g4)
    c: Coincident(g5,g4)
    c: Horizontal(g5)
    c: Coincident(g6,g5)
    c: Vertical(g6)
    c: Coincident(g7,g6)
    c: Coincident(g7,g0)
    c: DistanceY(g0,g0) = 0.8
    c: DistanceY(g6,g6) = 8.7
    c: DistanceX(g1,g1) = 14.9
    c: DistanceX(g3,g3) = 2
    c: Coincident(g0,g-4)
    c: DistanceY(g2,g-6) = 0
    c: Coincident(g6,g-5)
FEATURE [Part::Extrusion] Extrude009  label="Extrude buco pompa"
  Base = -> Sketch013
  Dir = (0,-1,2e-16)
  DirMode = 2
  FaceMakerClass = Part::FaceMakerBullseye
  FaceMakerMode = 3
  LengthFwd = 13.2
  LengthRev = 0
  Solid = true
  Symmetric = true
FEATURE [Sketcher::SketchObject] Sketch014  label="buco frontale"
  ArcFitTolerance = 1e-06
  AttachmentSupport = -> [XZ_Plane]
  ExternalGeometry = -> [Sketch]
  FullyConstrained = true
  MakeInternals = false
  MapMode = 5
  Placement = pos=(0,0,0) rot=(1,0,0;1.5708rad)
  sketch-geometry (10):
    g0: LineSegment StartX=0 StartY=0 StartZ=0 EndX=0 EndY=24.671 EndZ=0
    g1: LineSegment StartX=0 StartY=24.671 StartZ=0 EndX=-4 EndY=24.671 EndZ=0
    g2: LineSegment StartX=-4 StartY=24.671 StartZ=0 EndX=-4 EndY=16 EndZ=0
    g3: LineSegment StartX=-4 StartY=16 StartZ=0 EndX=-2.4 EndY=16 EndZ=0
    g4: LineSegment StartX=-2.4 StartY=16 StartZ=0 EndX=-2.4 EndY=10 EndZ=0
    g5: LineSegment StartX=-2.4 StartY=10 StartZ=0 EndX=-12 EndY=10 EndZ=0
    g6: LineSegment StartX=-12 StartY=10 StartZ=0 EndX=-12 EndY=6 EndZ=0
    g7: LineSegment StartX=-12 StartY=6 StartZ=0 EndX=-2.4 EndY=6 EndZ=0
    g8: LineSegment StartX=-2.4 StartY=6 StartZ=0 EndX=-2.4 EndY=0 EndZ=0
    g9: LineSegment StartX=-2.4 StartY=0 StartZ=0 EndX=0 EndY=0 EndZ=0
  constraints (29):
    c: Vertical(g0)
    c: Coincident(g1,g0)
    c: Horizontal(g1)
    c: Coincident(g2,g1)
    c: Vertical(g2)
    c: Coincident(g3,g2)
    c: Horizontal(g3)
    c: Coincident(g4,g3)
    c: Vertical(g4)
    c: Coincident(g5,g4)
    c: Horizontal(g5)
    c: Coincident(g6,g5)
    c: Vertical(g6)
    c: Coincident(g7,g6)
    c: Coincident(g8,g7)
    c: Vertical(g8)
    c: Coincident(g9,g8)
    c: Coincident(g9,g0)
    c: Horizontal(g9)
    c: DistanceY(g0,g0) = 24.671
    c: Horizontal(g7)
    c: DistanceY(g6,g6) = 4
    c: DistanceY(g4,g4) = 6
    c: DistanceX(g9,g9) = 2.4
    c: Coincident(g0,g-1)
    c: DistanceY(g-3,g7) = 0
    c: DistanceX(g8,g4) = 0
    c: DistanceX(g-3,g1) = 0
    c: DistanceX(g6,g-3) = 8
FEATURE [Part::Extrusion] Extrude010  label="Extrude buco frontale"
  Base = -> Sketch014
  Dir = (0,-1,2e-16)
  DirMode = 2
  FaceMakerClass = Part::FaceMakerBullseye
  FaceMakerMode = 3
  LengthFwd = 11.2
  LengthRev = 0
  Solid = true
  Symmetric = true
FEATURE [Sketcher::SketchObject] Sketch015  label="guida rail"
  ArcFitTolerance = 1e-06
  AttachmentSupport = -> [XZ_Plane]
  ExternalGeometry = -> [Sketch]
  FullyConstrained = true
  MakeInternals = false
  MapMode = 5
  Placement = pos=(0,0,0) rot=(1,0,0;1.5708rad)
  sketch-geometry (4):
    g0: LineSegment StartX=-100.8 StartY=43.2 StartZ=0 EndX=-44.6 EndY=43.2 EndZ=0
    g1: LineSegment StartX=-44.6 StartY=43.2 StartZ=0 EndX=-44.6 EndY=41.2 EndZ=0
    g2: LineSegment StartX=-44.6 StartY=41.2 StartZ=0 EndX=-100.8 EndY=41.2 EndZ=0
    g3: LineSegment StartX=-100.8 StartY=41.2 StartZ=0 EndX=-100.8 EndY=43.2 EndZ=0
  constraints (9):
    c: Horizontal(g0)
    c: Coincident(g1,g0)
    c: Coincident(g2,g1)
    c: Coincident(g3,g2)
    c: Coincident(g3,g0)
    c: Vertical(g3)
    c: Coincident(g2,g-3)
    c: Coincident(g1,g-3)
    c: Coincident(g0,g-4)
FEATURE [Part::Extrusion] Extrude011  label="Extrude guida rail"
  Base = -> Sketch015
  Dir = (0,-1,2e-16)
  DirMode = 2
  FaceMakerClass = Part::FaceMakerBullseye
  FaceMakerMode = 3
  LengthFwd = 9
  LengthRev = 0
  Solid = true
  Symmetric = true
FEATURE [Sketcher::SketchObject] Sketch016  label="guide per coperture laterali"
  ArcFitTolerance = 1e-06
  AttachmentSupport = -> [XZ_Plane]
  ExternalGeometry = -> [Sketch]
  FullyConstrained = true
  MakeInternals = false
  MapMode = 5
  Placement = pos=(0,0,0) rot=(1,0,0;1.5708rad)
  sketch-geometry (14):
    g0: Circle CenterX=-5.6 CenterY=7.6 CenterZ=0 NormalX=0 NormalY=0 NormalZ=1 AngleXU=0 Radius=1.6
    g1: Circle CenterX=-5.6 CenterY=7.6 CenterZ=0 NormalX=0 NormalY=0 NormalZ=1 AngleXU=0 Radius=4
    g2: Circle CenterX=-5.6 CenterY=34.8 CenterZ=0 NormalX=0 NormalY=0 NormalZ=1 AngleXU=0 Radius=1.6
    g3: Circle CenterX=-5.6 CenterY=34.8 CenterZ=0 NormalX=0 NormalY=0 NormalZ=1 AngleXU=0 Radius=4
    g4: Circle CenterX=-184.08 CenterY=34.8 CenterZ=0 NormalX=0 NormalY=0 NormalZ=1 AngleXU=0 Radius=1.6
    g5: Circle CenterX=-184.08 CenterY=34.8 CenterZ=0 NormalX=0 NormalY=0 NormalZ=1 AngleXU=0 Radius=4
    g6: Circle CenterX=-179.305 CenterY=-76.8316 CenterZ=0 NormalX=0 NormalY=0 NormalZ=1 AngleXU=0 Radius=1.6
    g7: Circle CenterX=-179.305 CenterY=-76.8316 CenterZ=0 NormalX=0 NormalY=0 NormalZ=1 AngleXU=0 Radius=4
    g8: Circle CenterX=-213.443 CenterY=-76.8316 CenterZ=0 NormalX=0 NormalY=0 NormalZ=1 AngleXU=0 Radius=1.6
    g9: Circle CenterX=-213.443 CenterY=-76.8316 CenterZ=0 NormalX=0 NormalY=0 NormalZ=1 AngleXU=0 Radius=4
    g10: Circle CenterX=-78.51 CenterY=7.6 CenterZ=0 NormalX=0 NormalY=0 NormalZ=1 AngleXU=0 Radius=1.6
    g11: Circle CenterX=-78.51 CenterY=7.6 CenterZ=0 NormalX=0 NormalY=0 NormalZ=1 AngleXU=0 Radius=4
    g12: Circle CenterX=-78.51 CenterY=34.8 CenterZ=0 NormalX=0 NormalY=0 NormalZ=1 AngleXU=0 Radius=1.6
    g13: Circle CenterX=-78.51 CenterY=34.8 CenterZ=0 NormalX=0 NormalY=0 NormalZ=1 AngleXU=0 Radius=4
  constraints (35):
    c: Diameter(g0) = 3.2
    c: Diameter(g1) = 8
    c: Coincident(g0,g1)
    c: Diameter(g2) = 3.2
    c: Diameter(g3) = 8
    c: Coincident(g3,g2)
    c: Tangent(g2,g-7)
    c: Diameter(g4) = 3.2
    c: Diameter(g5) = 8
    c: Coincident(g5,g4)
    c: Tangent(g4,g-7)
    c: Tangent(g4,g-8)
    c: Diameter(g6) = 3.2
    c: Diameter(g7) = 8
    c: Coincident(g7,g6)
    c: Tangent(g6,g-9)
    c: Tangent(g6,g-10)
    c: Diameter(g8) = 3.2
    c: Diameter(g9) = 8
    c: Coincident(g9,g8)
    c: Tangent(g8,g-10)
    c: Tangent(g8,g-11)
    c: Diameter(g10) = 3.2
    c: Diameter(g11) = 8
    c: Diameter(g12) = 3.2
    c: Diameter(g13) = 8
    c: Coincident(g12,g13)
    c: Coincident(g10,g11)
    c: Tangent(g12,g-7)
    c: DistanceX(g12,g10) = 0
    c: Tangent(g2,g-6)
    c: Tangent(g0,g-6)
    c: Tangent(g0,g-3)
    c: Tangent(g10,g-3)
    c: Tangent(g10,g-4)
FEATURE [Part::Extrusion] Extrude012  label="extrude guide per coperture laterali"
  Base = -> Sketch016
  Dir = (0,-1,2e-16)
  DirMode = 2
  FaceMakerClass = Part::FaceMakerBullseye
  FaceMakerMode = 3
  LengthFwd = 25.2
  LengthRev = 0
  Solid = true
  Symmetric = true
FEATURE [Sketcher::SketchObject] Sketch017  label="supporto CAM"
  ArcFitTolerance = 1e-06
  AttachmentSupport = -> [XZ_Plane]
  ExternalGeometry = -> [Sketch]
  FullyConstrained = true
  MakeInternals = false
  MapMode = 5
  Placement = pos=(0,0,0) rot=(1,0,0;1.5708rad)
  sketch-geometry (6):
    g0: LineSegment StartX=-2.4 StartY=48 StartZ=0 EndX=-2.4 EndY=41.2 EndZ=0
    g1: LineSegment StartX=-2.4 StartY=48 StartZ=0 EndX=-34 EndY=48 EndZ=0
    g2: LineSegment StartX=-34 StartY=48 StartZ=0 EndX=-34 EndY=46.72 EndZ=0
    g3: LineSegment StartX=-34 StartY=46.72 StartZ=0 EndX=-36 EndY=46.72 EndZ=0
    g4: LineSegment StartX=-36 StartY=46.72 StartZ=0 EndX=-36 EndY=41.2 EndZ=0
    g5: LineSegment StartX=-36 StartY=41.2 StartZ=0 EndX=-2.4 EndY=41.2 EndZ=0
  constraints (15):
    c: Coincident(g1,g0)
    c: Horizontal(g1)
    c: Coincident(g2,g1)
    c: Vertical(g2)
    c: Coincident(g3,g2)
    c: Horizontal(g3)
    c: Coincident(g4,g3)
    c: Coincident(g5,g4)
    c: DistanceX(g1,g0) = 31.6
    c: Coincident(g5,g0)
    c: Vertical(g4)
    c: DistanceY(g2,g1) = 1.28
    c: Coincident(g0,g-3)
    c: Coincident(g0,g-3)
    c: Coincident(g4,g-4)
FEATURE [Part::Extrusion] Extrude013  label="Extrude supporto CAM"
  Base = -> Sketch017
  Dir = (0,-1,2e-16)
  DirMode = 2
  FaceMakerClass = Part::FaceMakerBullseye
  FaceMakerMode = 3
  LengthFwd = 17.8
  LengthRev = 0
  Solid = true
  Symmetric = true
FEATURE [Sketcher::SketchObject] Sketch018  label="Scavo CAM"
  ArcFitTolerance = 1e-06
  AttachmentSupport = -> [YZ_Plane]
  ExternalGeometry = -> [Sketch]
  FullyConstrained = true
  MakeInternals = false
  MapMode = 5
  Placement = pos=(0,0,0) rot=(0.57735,0.57735,0.57735;2.0944rad)
  sketch-geometry (4):
    g0: LineSegment StartX=-7.73 StartY=48 StartZ=0 EndX=7.73 EndY=48 EndZ=0
    g1: LineSegment [constr] StartX=1.07e-14 StartY=48 StartZ=0 EndX=0 EndY=43.5155 EndZ=0
    g2: ArcOfCircle CenterX=9e-15 CenterY=52.42 CenterZ=0 NormalX=0 NormalY=0 NormalZ=1 AngleXU=0 Radius=8.90445 StartAngle=3.66102 EndAngle=5.76376
    g3: Circle [constr] CenterX=9e-15 CenterY=52.42 CenterZ=0 NormalX=0 NormalY=0 NormalZ=1 AngleXU=0 Radius=8.9
  constraints (13):
    c: Horizontal(g0)
    c: DistanceY(g-3,g0) = 0
    c: DistanceX(g0,g0) = 15.46
    c: DistanceX(g0,g-3) = 7.73
    c: DistanceX(g-3) = 0
    c: Coincident(g1,g-3)
    c: PointOnObject(g1,g-2)
    c: Coincident(g2,g0)
    c: Coincident(g2,g0)
    c: PointOnObject(g1,g2)
    c: Diameter(g3) = 17.8
    c: DistanceY(g1,g3) = 4.42
    c: Coincident(g2,g3)
FEATURE [Part::Extrusion] Extrude014  label="Extrude Scavo CAM"
  Base = -> Sketch018
  Dir = (1,0,0)
  DirMode = 2
  FaceMakerClass = Part::FaceMakerBullseye
  FaceMakerMode = 3
  LengthFwd = -34
  LengthRev = 0
  Solid = true
  Symmetric = false
FEATURE [Sketcher::SketchObject] Sketch019  label="scavo rumble"
  ArcFitTolerance = 1e-06
  AttachmentSupport = -> [XZ_Plane]
  ExternalGeometry = -> [Sketch]
  FullyConstrained = true
  MakeInternals = false
  MapMode = 5
  Placement = pos=(0,0,0) rot=(1,0,0;1.5708rad)
  sketch-geometry (6):
    g0: LineSegment StartX=-163.771 StartY=-21.9058 StartZ=0 EndX=-158.636 EndY=-23.5745 EndZ=0
    g1: LineSegment StartX=-158.636 StartY=-23.5745 StartZ=0 EndX=-165.743 EndY=-45.4488 EndZ=0
    g2: LineSegment StartX=-165.743 StartY=-45.4488 StartZ=0 EndX=-170.879 EndY=-43.7801 EndZ=0
    g3: LineSegment StartX=-170.879 StartY=-43.7801 StartZ=0 EndX=-163.771 EndY=-21.9058 EndZ=0
    g4: LineSegment [constr] StartX=-145.51 StartY=22 StartZ=0 EndX=-160.157 EndY=-23.0801 EndZ=0
    g5: LineSegment [constr] StartX=-158.636 StartY=-23.5745 StartZ=0 EndX=-160.157 EndY=-23.0801 EndZ=0
  constraints (17):
    c: Coincident(g1,g0)
    c: Coincident(g2,g1)
    c: Coincident(g3,g2)
    c: Coincident(g3,g0)
    c: Parallel(g3,g-3)
    c: Parallel(g3,g1)
    c: Perpendicular(g3,g0)
    c: Perpendicular(g2,g3)
    c: Distance(g2,g0) = 23
    c: Parallel(g4,g-3)
    c: Distance(g4) = 47.4
    c: Coincident(g4,g-3)
    c: Parallel(g5,g0)
    c: Distance(g5) = 1.6
    c: Coincident(g5,g0)
    c: Distance(g5,g0) = 3.8
    c: Coincident(g5,g4)
FEATURE [Part::Extrusion] Extrude015  label="scavo rumble001"
  Base = -> Sketch019
  Dir = (0,-1,2e-16)
  DirMode = 2
  FaceMakerClass = Part::FaceMakerBullseye
  FaceMakerMode = 3
  LengthFwd = 21
  LengthRev = 0
  Solid = true
  Symmetric = true
FEATURE [Sketcher::SketchObject] Sketch020  label="fermo rumble"
  ArcFitTolerance = 1e-06
  AttachmentSupport = -> [XZ_Plane]
  ExternalGeometry = -> [Sketch019,Sketch]
  FullyConstrained = true
  MakeInternals = false
  MapMode = 5
  Placement = pos=(0,0,0) rot=(1,0,0;1.5708rad)
  sketch-geometry (16):
    g0: LineSegment [constr] StartX=-165.905 StartY=-40.7697 StartZ=0 EndX=-167.265 EndY=-44.9544 EndZ=0
    g1: LineSegment [constr] StartX=-167.265 StartY=-44.9544 StartZ=0 EndX=-165.743 EndY=-45.4488 EndZ=0
    g2: LineSegment StartX=-167.318 StartY=-37.9976 StartZ=0 EndX=-165.225 EndY=-38.6774 EndZ=0
    g3: LineSegment StartX=-165.225 StartY=-38.6774 StartZ=0 EndX=-165.905 EndY=-40.7697 EndZ=0
    g4: LineSegment StartX=-165.905 StartY=-40.7697 StartZ=0 EndX=-167.997 EndY=-40.0899 EndZ=0
    g5: LineSegment StartX=-167.997 StartY=-40.0899 StartZ=0 EndX=-167.318 EndY=-37.9976 EndZ=0
    g6: LineSegment StartX=-166.823 StartY=-36.4759 StartZ=0 EndX=-163.399 EndY=-37.5883 EndZ=0
    g7: LineSegment StartX=-163.399 StartY=-37.5883 StartZ=0 EndX=-165.006 EndY=-42.5338 EndZ=0
    g8: LineSegment StartX=-165.006 StartY=-42.5338 StartZ=0 EndX=-168.43 EndY=-41.4214 EndZ=0
    g9: LineSegment StartX=-169.457 StartY=-39.4053 StartZ=0 EndX=-168.839 EndY=-37.5031 EndZ=0
    g10: LineSegment [constr] StartX=-168.839 StartY=-37.5031 StartZ=0 EndX=-168.345 EndY=-35.9815 EndZ=0
    g11: LineSegment [constr] StartX=-168.345 StartY=-35.9815 StartZ=0 EndX=-166.823 EndY=-36.4759 EndZ=0
    g12: ArcOfCircle CenterX=-167.936 CenterY=-39.8997 CenterZ=0 NormalX=0 NormalY=0 NormalZ=1 AngleXU=0 Radius=1.6 StartAngle=2.82743 EndAngle=4.39823
    g13: GeomPoint [constr] X=-169.952 Y=-40.9269 Z=0
    g14: ArcOfCircle CenterX=-167.318 CenterY=-37.9976 CenterZ=0 NormalX=0 NormalY=0 NormalZ=1 AngleXU=0 Radius=1.6 StartAngle=1.25664 EndAngle=2.82743
    g15: GeomPoint [constr] X=-168.345 Y=-35.9815 Z=0
  constraints (42):
    c: Parallel(g0,g-4)
    c: Distance(g0) = 4.4
    c: Coincident(g1,g0)
    c: Perpendicular(g0,g1)
    c: Distance(g1) = 1.6
    c: Coincident(g1,g-5)
    c: Coincident(g3,g2)
    c: Coincident(g4,g3)
    c: Coincident(g5,g4)
    c: Coincident(g5,g2)
    c: Parallel(g3,g-4)
    c: Parallel(g3,g5)
    c: Perpendicular(g2,g3)
    c: Parallel(g4,g2)
    c: Distance(g2) = 2.2
    c: Distance(g3) = 2.2
    c: Coincident(g7,g6)
    c: Coincident(g8,g7)
    c: Parallel(g7,g-4)
    c: Parallel(g7,g9)
    c: Perpendicular(g6,g7)
    c: Parallel(g6,g8)
    c: Distance(g6,g15) = 5.2
    c: Distance(g7) = 5.2
    c: Coincident(g11,g10)
    c: Parallel(g10,g9)
    c: Parallel(g11,g6)
    c: Distance(g10) = 1.6
    c: Distance(g11) = 1.6
    c: Coincident(g10,g15)
    c: Distance(g11,g2) = 1.6
    c: Distance(g2,g10) = 1.6
    c: PointOnObject(g13,g8)
    c: PointOnObject(g13,g9)
    c: Tangent(g8,g12) = 1.5708
    c: Tangent(g9,g12) = 1.5708
    c: PointOnObject(g15,g9)
    c: Tangent(g6,g14) = 1.5708
    c: Tangent(g9,g14) = 1.5708
    c: Equal(g12,g14)
    c: Coincident(g6,g11)
    c: Coincident(g3,g0)
FEATURE [Part::Extrusion] Extrude016  label="Extrude fermo rumble"
  Base = -> Sketch020
  Dir = (0,-1,2e-16)
  DirMode = 2
  FaceMakerClass = Part::FaceMakerBullseye
  FaceMakerMode = 3
  LengthFwd = 25.2
  LengthRev = 0
  Solid = true
  Symmetric = true
FEATURE [Sketcher::SketchObject] Sketch021  label="perno fermo rumble001"
  ArcFitTolerance = 1e-06
  AttachmentSupport = -> [XZ_Plane001]
  FullyConstrained = true
  MakeInternals = false
  MapMode = 5
  Placement = pos=(0,0,0) rot=(1,0,0;1.5708rad)
  sketch-geometry (16):
    g0: LineSegment StartX=0 StartY=0.45 StartZ=0 EndX=0 EndY=1.55 EndZ=0
    g1: LineSegment StartX=0.45 StartY=2 StartZ=0 EndX=1.55 EndY=2 EndZ=0
    g2: LineSegment StartX=2 StartY=1.55 StartZ=0 EndX=2 EndY=0.45 EndZ=0
    g3: LineSegment StartX=1.55 StartY=0 StartZ=0 EndX=0.45 EndY=0 EndZ=0
    g4: ArcOfCircle [constr] CenterX=0.45 CenterY=1.55 CenterZ=0 NormalX=0 NormalY=0 NormalZ=1 AngleXU=0 Radius=0.45 StartAngle=1.5708 EndAngle=3.14159
    g5: GeomPoint [constr] X=0 Y=2 Z=0
    g6: LineSegment StartX=0.45 StartY=2 StartZ=0 EndX=0 EndY=1.55 EndZ=0
    g7: ArcOfCircle [constr] CenterX=1.55 CenterY=1.55 CenterZ=0 NormalX=0 NormalY=0 NormalZ=1 AngleXU=0 Radius=0.45 StartAngle=0 EndAngle=1.5708
    g8: GeomPoint [constr] X=2 Y=2 Z=0
    g9: LineSegment StartX=2 StartY=1.55 StartZ=0 EndX=1.55 EndY=2 EndZ=0
    g10: ArcOfCircle [constr] CenterX=1.55 CenterY=0.45 CenterZ=0 NormalX=0 NormalY=0 NormalZ=1 AngleXU=0 Radius=0.45 StartAngle=4.71239 EndAngle=6.28319
    g11: GeomPoint [constr] X=2 Y=0 Z=0
    g12: LineSegment StartX=1.55 StartY=0 StartZ=0 EndX=2 EndY=0.45 EndZ=0
    g13: ArcOfCircle [constr] CenterX=0.45 CenterY=0.45 CenterZ=0 NormalX=0 NormalY=0 NormalZ=1 AngleXU=0 Radius=0.45 StartAngle=3.14159 EndAngle=4.71239
    g14: GeomPoint [constr] X=0 Y=0 Z=0
    g15: LineSegment StartX=0 StartY=0.45 StartZ=0 EndX=0.45 EndY=0 EndZ=0
  constraints (35):
    c: Coincident(g14,g-1)
    c: PointOnObject(g5,g-2)
    c: Horizontal(g1)
    c: Vertical(g2)
    c: Horizontal(g3)
    c: DistanceX(g5,g8) = 2
    c: DistanceY(g11,g8) = 2
    c: PointOnObject(g5,g0)
    c: PointOnObject(g5,g1)
    c: Tangent(g0,g4) = 1.5708
    c: Tangent(g1,g4) = 1.5708
    c: Coincident(g6,g0)
    c: Coincident(g6,g1)
    c: PointOnObject(g8,g2)
    c: PointOnObject(g8,g1)
    c: Tangent(g2,g7) = 1.5708
    c: Tangent(g1,g7) = 1.5708
    c: Coincident(g9,g2)
    c: Coincident(g9,g1)
    c: PointOnObject(g11,g2)
    c: PointOnObject(g11,g3)
    c: Tangent(g2,g10) = 1.5708
    c: Tangent(g3,g10) = 1.5708
    c: Coincident(g12,g2)
    c: Coincident(g12,g3)
    c: PointOnObject(g14,g0)
    c: PointOnObject(g14,g3)
    c: Tangent(g0,g13) = 1.5708
    c: Tangent(g3,g13) = 1.5708
    c: Coincident(g15,g0)
    c: Coincident(g15,g3)
    c: Equal(g6,g9)
    c: Equal(g9,g12)
    c: Equal(g12,g15)
    c: DistanceX(g14,g3) = 0.45
FEATURE [Sketcher::SketchObject] Sketch022  label="fori per M3x5(OD)x6(L)"
  ArcFitTolerance = 1e-06
  AttachmentSupport = -> [XZ_Plane]
  ExternalGeometry = -> [Sketch016]
  FullyConstrained = true
  MakeInternals = false
  MapMode = 5
  Placement = pos=(0,0,0) rot=(1,0,0;1.5708rad)
  sketch-geometry (7):
    g0: Circle CenterX=-5.6 CenterY=34.8 CenterZ=0 NormalX=0 NormalY=0 NormalZ=1 AngleXU=0 Radius=2.5
    g1: Circle CenterX=-5.6 CenterY=7.6 CenterZ=0 NormalX=0 NormalY=0 NormalZ=1 AngleXU=0 Radius=2.5
    g2: Circle CenterX=-78.51 CenterY=34.8 CenterZ=0 NormalX=0 NormalY=0 NormalZ=1 AngleXU=0 Radius=2.5
    g3: Circle CenterX=-78.51 CenterY=7.6 CenterZ=0 NormalX=0 NormalY=0 NormalZ=1 AngleXU=0 Radius=2.5
    g4: Circle CenterX=-184.08 CenterY=34.8 CenterZ=0 NormalX=0 NormalY=0 NormalZ=1 AngleXU=0 Radius=2.5
    g5: Circle CenterX=-179.305 CenterY=-76.8316 CenterZ=0 NormalX=0 NormalY=0 NormalZ=1 AngleXU=0 Radius=2.5
    g6: Circle CenterX=-213.443 CenterY=-76.8316 CenterZ=0 NormalX=0 NormalY=0 NormalZ=1 AngleXU=0 Radius=2.5
  constraints (14):
    c: Diameter(g0) = 5
    c: Diameter(g1) = 5
    c: Diameter(g2) = 5
    c: Diameter(g3) = 5
    c: Diameter(g4) = 5
    c: Diameter(g5) = 5
    c: Diameter(g6) = 5
    c: Coincident(g0,g-8)
    c: Coincident(g1,g-9)
    c: Coincident(g2,g-6)
    c: Coincident(g3,g-7)
    c: Coincident(g4,g-5)
    c: Coincident(g5,g-4)
    c: Coincident(g6,g-3)
FEATURE [Part::Extrusion] Extrude018  label="Extrude fori M3x5x6 - dx"
  Base = -> Sketch022
  Dir = (0,-1,2e-16)
  DirMode = 2
  FaceMakerClass = Part::FaceMakerBullseye
  FaceMakerMode = 3
  LengthFwd = 6.2
  LengthRev = 0
  Placement = pos=(0,-9.5,0) rot=(0,0,1;0rad)
  Solid = true
  Symmetric = true
FEATURE [Part::Extrusion] Extrude019  label="Extrude fori M3x5x6 - sx"
  Base = -> Sketch022
  Dir = (0,-1,2e-16)
  DirMode = 2
  FaceMakerClass = Part::FaceMakerBullseye
  FaceMakerMode = 3
  LengthFwd = 6.2
  LengthRev = 0
  Placement = pos=(0,9.5,0) rot=(0,0,1;0rad)
  Solid = true
  Symmetric = true
FEATURE [Sketcher::SketchObject] Sketch023  label="foro anteriore M3x5x6"
  ArcFitTolerance = 1e-06
  AttachmentSupport = -> [YZ_Plane]
  FullyConstrained = true
  MakeInternals = false
  MapMode = 5
  Placement = pos=(0,0,0) rot=(0.57735,0.57735,0.57735;2.0944rad)
  sketch-geometry (2):
    g0: LineSegment [constr] StartX=0 StartY=0 StartZ=0 EndX=0 EndY=38.6 EndZ=0
    g1: Circle CenterX=0 CenterY=38.6 CenterZ=0 NormalX=0 NormalY=0 NormalZ=1 AngleXU=0 Radius=2.5
  constraints (5):
    c: Coincident(g0,g-1)
    c: PointOnObject(g0,g-2)
    c: DistanceY(g0,g0) = 38.6
    c: Diameter(g1) = 5
    c: Coincident(g1,g0)
FEATURE [Part::Extrusion] Extrude020  label="Extrude foro anteriore M3x5x6"
  Base = -> Sketch023
  Dir = (1,0,0)
  DirMode = 2
  FaceMakerClass = Part::FaceMakerBullseye
  FaceMakerMode = 3
  LengthFwd = -6.2
  LengthRev = 0
  Solid = true
  Symmetric = false
FEATURE [Sketcher::SketchObject] Sketch024  label="fori per viti frontale"
  ArcFitTolerance = 1e-06
  AttachmentSupport = -> [YZ_Plane]
  FullyConstrained = true
  MakeInternals = false
  MapMode = 5
  Placement = pos=(0,0,0) rot=(0.57735,0.57735,0.57735;2.0944rad)
  sketch-geometry (9):
    g0: LineSegment [constr] StartX=-10.3 StartY=30.721 StartZ=0 EndX=10.3 EndY=30.721 EndZ=0
    g1: LineSegment [constr] StartX=10.3 StartY=30.721 StartZ=0 EndX=10.3 EndY=10.121 EndZ=0
    g2: LineSegment [constr] StartX=10.3 StartY=10.121 StartZ=0 EndX=-10.3 EndY=10.121 EndZ=0
    g3: LineSegment [constr] StartX=-10.3 StartY=10.121 StartZ=0 EndX=-10.3 EndY=30.721 EndZ=0
    g4: LineSegment [constr] StartX=0 StartY=0 StartZ=0 EndX=0 EndY=10.121 EndZ=0
    g5: Circle CenterX=-10.3 CenterY=30.721 CenterZ=0 NormalX=0 NormalY=0 NormalZ=1 AngleXU=0 Radius=2
    g6: Circle CenterX=10.3 CenterY=30.721 CenterZ=0 NormalX=0 NormalY=0 NormalZ=1 AngleXU=0 Radius=2
    g7: Circle CenterX=-10.3 CenterY=10.121 CenterZ=0 NormalX=0 NormalY=0 NormalZ=1 AngleXU=0 Radius=2
    g8: Circle CenterX=10.3 CenterY=10.121 CenterZ=0 NormalX=0 NormalY=0 NormalZ=1 AngleXU=0 Radius=2
  constraints (22):
    c: Horizontal(g0)
    c: Coincident(g1,g0)
    c: Vertical(g1)
    c: Coincident(g2,g1)
    c: Horizontal(g2)
    c: Coincident(g3,g2)
    c: Coincident(g3,g0)
    c: Vertical(g3)
    c: DistanceX(g0,g0) = 20.6
    c: DistanceY(g3,g3) = 20.6
    c: Coincident(g4,g-1)
    c: PointOnObject(g4,g-2)
    c: DistanceY(g4,g4) = 10.121
    c: Symmetric(g2,g2,g4)
    c: Diameter(g5) = 4
    c: Diameter(g6) = 4
    c: Diameter(g7) = 4
    c: Diameter(g8) = 4
    c: Coincident(g5,g0)
    c: Coincident(g6,g0)
    c: Coincident(g7,g2)
    c: Coincident(g8,g1)
FEATURE [Part::Extrusion] Extrude021  label="Extrude fori per viti frontale"
  Base = -> Sketch024
  Dir = (1,0,0)
  DirMode = 2
  FaceMakerClass = Part::FaceMakerBullseye
  FaceMakerMode = 3
  LengthFwd = -2.4
  LengthRev = 0
  Solid = true
  Symmetric = false
FEATURE [Sketcher::SketchObject] Sketch025  label="foro per filo CAM"
  ArcFitTolerance = 1e-06
  AttachmentSupport = -> [XZ_Plane]
  ExternalGeometry = -> [Sketch]
  FullyConstrained = true
  MakeInternals = false
  MapMode = 5
  Placement = pos=(0,0,0) rot=(1,0,0;1.5708rad)
  sketch-geometry (4):
    g0: LineSegment StartX=-44.6 StartY=41.2 StartZ=0 EndX=-44.6 EndY=36.4 EndZ=0
    g1: LineSegment StartX=-44.6 StartY=36.4 StartZ=0 EndX=-54.6 EndY=36.4 EndZ=0
    g2: LineSegment StartX=-54.6 StartY=36.4 StartZ=0 EndX=-50.4 EndY=41.2 EndZ=0
    g3: LineSegment StartX=-50.4 StartY=41.2 StartZ=0 EndX=-44.6 EndY=41.2 EndZ=0
  constraints (11):
    c: Vertical(g0)
    c: Coincident(g1,g0)
    c: Horizontal(g1)
    c: Coincident(g2,g1)
    c: Coincident(g3,g2)
    c: Coincident(g3,g0)
    c: Horizontal(g3)
    c: Coincident(g0,g-3)
    c: DistanceY(g0,g-4) = 0
    c: DistanceX(g3,g3) = 5.8
    c: DistanceX(g1,g1) = 10
FEATURE [Part::Extrusion] Extrude022  label="Extrude foro per filo CAM dx"
  Base = -> Sketch025
  Dir = (0,-1,2e-16)
  DirMode = 2
  FaceMakerClass = Part::FaceMakerBullseye
  FaceMakerMode = 3
  LengthFwd = 4.9
  LengthRev = 0
  Placement = pos=(0,6.95,0) rot=(0,0,1;0rad)
  Solid = true
  Symmetric = true
FEATURE [Part::Extrusion] Extrude023  label="Extrude foro per filo CAM sx"
  Base = -> Sketch025
  Dir = (0,-1,2e-16)
  DirMode = 2
  FaceMakerClass = Part::FaceMakerBullseye
  FaceMakerMode = 3
  LengthFwd = 4.9
  LengthRev = 0
  Placement = pos=(0,-6.95,0) rot=(0,0,1;0rad)
  Solid = true
  Symmetric = true
FEATURE [Sketcher::SketchObject] Sketch026  label="foro sotto anteriore M3x5x6"
  ArcFitTolerance = 1e-06
  AttachmentSupport = -> [XY_Plane]
  FullyConstrained = true
  MakeInternals = false
  MapMode = 5
  sketch-geometry (2):
    g0: LineSegment [constr] StartX=0 StartY=0 StartZ=0 EndX=-16.5 EndY=0 EndZ=0
    g1: Circle CenterX=-16.5 CenterY=0 CenterZ=0 NormalX=0 NormalY=0 NormalZ=1 AngleXU=0 Radius=2.5
  constraints (5):
    c: Distance(g0) = 16.5
    c: Coincident(g0,g-1)
    c: PointOnObject(g0,g-1)
    c: Diameter(g1) = 5
    c: Coincident(g0,g1)
FEATURE [Sketcher::SketchObject] Sketch027  label="foro sotto posteriore M3x5x6"
  ArcFitTolerance = 1e-06
  AttachmentSupport = -> [XY_Plane]
  ExternalGeometry = -> [Sketch]
  FullyConstrained = true
  MakeInternals = false
  MapMode = 5
  sketch-geometry (2):
    g0: LineSegment [constr] StartX=-82.8 StartY=2e-16 StartZ=0 EndX=-71.3 EndY=2e-16 EndZ=0
    g1: Circle CenterX=-71.3 CenterY=2e-16 CenterZ=0 NormalX=0 NormalY=0 NormalZ=1 AngleXU=0 Radius=2.5
  constraints (5):
    c: Distance(g0) = 11.5
    c: Coincident(g0,g-3)
    c: PointOnObject(g0,g-3)
    c: Diameter(g1) = 5
    c: Coincident(g1,g0)
FEATURE [Sketcher::SketchObject] Sketch029  label="fori sotto impugnatura"
  ArcFitTolerance = 1e-06
  AttachmentSupport = -> [XY_Plane]
  ExternalGeometry = -> [Sketch]
  FullyConstrained = true
  MakeInternals = false
  MapMode = 5
  sketch-geometry (15):
    g0: LineSegment [constr] StartX=-175.232 StartY=-1.83e-14 StartZ=0 EndX=-191.232 EndY=0 EndZ=0
    g1: Circle CenterX=-191.232 CenterY=0 CenterZ=0 NormalX=0 NormalY=0 NormalZ=1 AngleXU=0 Radius=3.95
    g2: LineSegment [constr] StartX=-175.232 StartY=-1.83e-14 StartZ=0 EndX=-204.275 EndY=0 EndZ=0
    g3: LineSegment StartX=-204.275 StartY=3.525 StartZ=0 EndX=-204.275 EndY=-3.525 EndZ=0
    g4: LineSegment StartX=-205.4 StartY=-4.65 StartZ=0 EndX=-206.65 EndY=-4.65 EndZ=0
    g5: LineSegment StartX=-207.775 StartY=-3.525 StartZ=0 EndX=-207.775 EndY=3.525 EndZ=0
    g6: LineSegment StartX=-206.65 StartY=4.65 StartZ=0 EndX=-205.4 EndY=4.65 EndZ=0
    g7: ArcOfCircle CenterX=-206.65 CenterY=3.525 CenterZ=0 NormalX=0 NormalY=0 NormalZ=1 AngleXU=0 Radius=1.125 StartAngle=1.5708 EndAngle=3.14159
    g8: GeomPoint [constr] X=-207.775 Y=4.65 Z=0
    g9: ArcOfCircle CenterX=-205.4 CenterY=3.525 CenterZ=0 NormalX=0 NormalY=0 NormalZ=1 AngleXU=0 Radius=1.125 StartAngle=0 EndAngle=1.5708
    g10: GeomPoint [constr] X=-204.275 Y=4.65 Z=0
    g11: ArcOfCircle CenterX=-205.4 CenterY=-3.525 CenterZ=0 NormalX=0 NormalY=0 NormalZ=1 AngleXU=0 Radius=1.125 StartAngle=4.71239 EndAngle=6.28319
    g12: GeomPoint [constr] X=-204.275 Y=-4.65 Z=0
    g13: ArcOfCircle CenterX=-206.65 CenterY=-3.525 CenterZ=0 NormalX=0 NormalY=0 NormalZ=1 AngleXU=0 Radius=1.125 StartAngle=3.14159 EndAngle=4.71239
    g14: GeomPoint [constr] X=-207.775 Y=-4.65 Z=0
  constraints (35):
    c: Distance(g0) = 16
    c: Coincident(g0,g-3)
    c: PointOnObject(g0,g-1)
    c: Diameter(g1) = 7.9
    c: Coincident(g1,g0)
    c: Coincident(g2,g0)
    c: PointOnObject(g2,g-1)
    c: Vertical(g3)
    c: Horizontal(g4)
    c: Vertical(g5)
    c: Horizontal(g6)
    c: DistanceY(g12,g10) = 9.3
    c: DistanceX(g8,g10) = 3.5
    c: Symmetric(g10,g12,g2)
    c: PointOnObject(g8,g5)
    c: PointOnObject(g8,g6)
    c: Tangent(g5,g7) = 1.5708
    c: Tangent(g6,g7) = 1.5708
    c: PointOnObject(g10,g3)
    c: PointOnObject(g10,g6)
    c: Tangent(g3,g9) = 1.5708
    c: Tangent(g6,g9) = 1.5708
    c: PointOnObject(g12,g3)
    c: PointOnObject(g12,g4)
    c: Tangent(g3,g11) = 1.5708
    c: Tangent(g4,g11) = 1.5708
    c: PointOnObject(g14,g4)
    c: PointOnObject(g14,g5)
    c: Tangent(g4,g13) = 1.5708
    c: Tangent(g5,g13) = 1.5708
    c: Equal(g7,g9)
    c: Equal(g9,g11)
    c: Equal(g11,g13)
    c: DistanceX(g6,g6) = 1.25
    c: DistanceX(g-5,g5) = 6.8
FEATURE [Sketcher::SketchObject] Sketch030  label="fori superiori per solenoide e oled"
  ArcFitTolerance = 1e-06
  AttachmentSupport = -> [XY_Plane]
  ExternalGeometry = -> [Sketch]
  FullyConstrained = true
  MakeInternals = false
  MapMode = 5
  sketch-geometry (33):
    g0: LineSegment [constr] StartX=-181.6 StartY=1.12e-14 StartZ=0 EndX=-169.91 EndY=0 EndZ=0
    g1: LineSegment [constr] StartX=-169.91 StartY=0 StartZ=0 EndX=-169.91 EndY=-2.6 EndZ=0
    g2: LineSegment [constr] StartX=-169.91 StartY=0 StartZ=0 EndX=-169.91 EndY=2.6 EndZ=0
    g3: LineSegment StartX=-169.91 StartY=4.975 StartZ=0 EndX=-169.91 EndY=8.225 EndZ=0
    g4: LineSegment StartX=-167.535 StartY=10.6 StartZ=0 EndX=-167.285 EndY=10.6 EndZ=0
    g5: LineSegment StartX=-164.91 StartY=8.225 StartZ=0 EndX=-164.91 EndY=4.975 EndZ=0
    g6: LineSegment StartX=-167.285 StartY=2.6 StartZ=0 EndX=-167.535 EndY=2.6 EndZ=0
    g7: LineSegment StartX=-169.91 StartY=-4.975 StartZ=0 EndX=-169.91 EndY=-8.225 EndZ=0
    g8: LineSegment StartX=-167.535 StartY=-10.6 StartZ=0 EndX=-167.285 EndY=-10.6 EndZ=0
    g9: LineSegment StartX=-164.91 StartY=-8.225 StartZ=0 EndX=-164.91 EndY=-4.975 EndZ=0
    g10: LineSegment StartX=-167.285 StartY=-2.6 StartZ=0 EndX=-167.535 EndY=-2.6 EndZ=0
    g11: ArcOfCircle CenterX=-167.535 CenterY=8.225 CenterZ=0 NormalX=0 NormalY=0 NormalZ=1 AngleXU=0 Radius=2.375 StartAngle=1.5708 EndAngle=3.14159
    g12: GeomPoint [constr] X=-169.91 Y=10.6 Z=0
    g13: ArcOfCircle CenterX=-167.285 CenterY=8.225 CenterZ=0 NormalX=0 NormalY=0 NormalZ=1 AngleXU=0 Radius=2.375 StartAngle=0 EndAngle=1.5708
    g14: GeomPoint [constr] X=-164.91 Y=10.6 Z=0
    g15: ArcOfCircle CenterX=-167.285 CenterY=4.975 CenterZ=0 NormalX=0 NormalY=0 NormalZ=1 AngleXU=0 Radius=2.375 StartAngle=4.71239 EndAngle=6.28319
    g16: GeomPoint [constr] X=-164.91 Y=2.6 Z=0
    g17: ArcOfCircle CenterX=-167.535 CenterY=4.975 CenterZ=0 NormalX=0 NormalY=0 NormalZ=1 AngleXU=0 Radius=2.375 StartAngle=3.14159 EndAngle=4.71239
    g18: GeomPoint [constr] X=-169.91 Y=2.6 Z=0
    g19: ArcOfCircle CenterX=-167.535 CenterY=-4.975 CenterZ=0 NormalX=0 NormalY=0 NormalZ=1 AngleXU=0 Radius=2.375 StartAngle=1.5708 EndAngle=3.14159
    g20: GeomPoint [constr] X=-169.91 Y=-2.6 Z=0
    g21: ArcOfCircle CenterX=-167.285 CenterY=-4.975 CenterZ=0 NormalX=0 NormalY=0 NormalZ=1 AngleXU=0 Radius=2.375 StartAngle=0 EndAngle=1.5708
    g22: GeomPoint [constr] X=-164.91 Y=-2.6 Z=0
    g23: ArcOfCircle CenterX=-167.285 CenterY=-8.225 CenterZ=0 NormalX=0 NormalY=0 NormalZ=1 AngleXU=0 Radius=2.375 StartAngle=4.71239 EndAngle=6.28319
    g24: GeomPoint [constr] X=-164.91 Y=-10.6 Z=0
    g25: ArcOfCircle CenterX=-167.535 CenterY=-8.225 CenterZ=0 NormalX=0 NormalY=0 NormalZ=1 AngleXU=0 Radius=2.375 StartAngle=3.14159 EndAngle=4.71239
    g26: GeomPoint [constr] X=-169.91 Y=-10.6 Z=0
    g27: LineSegment [constr] StartX=-181.6 StartY=1.12e-14 StartZ=0 EndX=-152.209 EndY=0 EndZ=0
    g28: LineSegment [constr] StartX=-181.6 StartY=1.12e-14 StartZ=0 EndX=-130.41 EndY=0 EndZ=0
    g29: LineSegment [constr] StartX=-152.209 StartY=0 StartZ=0 EndX=-152.209 EndY=6.95 EndZ=0
    g30: LineSegment [constr] StartX=-130.41 StartY=0 StartZ=0 EndX=-130.41 EndY=-6.95 EndZ=0
    g31: Circle CenterX=-152.209 CenterY=6.95 CenterZ=0 NormalX=0 NormalY=0 NormalZ=1 AngleXU=0 Radius=2.1
    g32: Circle CenterX=-130.41 CenterY=-6.95 CenterZ=0 NormalX=0 NormalY=0 NormalZ=1 AngleXU=0 Radius=2.1
  constraints (79):
    c: Distance(g0) = 11.69
    c: PointOnObject(g0,g-1)
    c: Coincident(g-4,g0)
    c: Distance(g1) = 2.6
    c: Coincident(g1,g0)
    c: Vertical(g1)
    c: Distance(g2) = 2.6
    c: Coincident(g2,g0)
    c: Vertical(g2)
    c: Distance(g18,g12) = 8
    c: Coincident(g18,g2)
    c: Vertical(g3)
    c: Distance(g14,g12) = 5
    c: Horizontal(g4)
    c: Distance(g16,g14) = 8
    c: Vertical(g5)
    c: Distance(g26,g20) = 8
    c: Coincident(g20,g1)
    c: Vertical(g7)
    c: Distance(g26,g24) = 5
    c: Horizontal(g8)
    c: Distance(g24,g22) = 8
    c: Vertical(g9)
    c: PointOnObject(g12,g3)
    c: PointOnObject(g12,g4)
    c: Tangent(g3,g11) = 1.5708
    c: Tangent(g4,g11) = 1.5708
    c: PointOnObject(g14,g5)
    c: PointOnObject(g14,g4)
    c: Tangent(g5,g13) = 1.5708
    c: Tangent(g4,g13) = 1.5708
    c: PointOnObject(g16,g5)
    c: PointOnObject(g16,g6)
    c: Tangent(g5,g15) = 1.5708
    c: Tangent(g6,g15) = 1.5708
    c: PointOnObject(g18,g3)
    c: PointOnObject(g18,g6)
    c: Tangent(g3,g17) = 1.5708
    c: Tangent(g6,g17) = 1.5708
    c: Equal(g11,g13)
    c: Equal(g13,g15)
    c: Equal(g15,g17)
    c: DistanceX(g4,g4) = 0.25
    c: PointOnObject(g20,g7)
    c: PointOnObject(g20,g10)
    c: Tangent(g7,g19) = -1.5708
    c: Tangent(g10,g19) = -1.5708
    c: PointOnObject(g22,g9)
    c: PointOnObject(g22,g10)
    c: Tangent(g9,g21) = -1.5708
    c: Tangent(g10,g21) = -1.5708
    c: PointOnObject(g24,g9)
    c: PointOnObject(g24,g8)
    c: Tangent(g9,g23) = -1.5708
    c: Tangent(g8,g23) = -1.5708
    c: PointOnObject(g26,g8)
    c: PointOnObject(g26,g7)
    c: Tangent(g8,g25) = -1.5708
    c: Tangent(g7,g25) = -1.5708
    c: Equal(g19,g21)
    c: Equal(g21,g23)
    c: Equal(g23,g25)
    c: DistanceX(g10,g10) = 0.25
    c: Distance(g27) = 29.391
    c: Coincident(g27,g0)
    c: PointOnObject(g27,g-1)
    c: Distance(g28) = 51.19
    c: Coincident(g28,g0)
    c: PointOnObject(g28,g-1)
    c: Distance(g29) = 6.95
    c: Coincident(g29,g27)
    c: Vertical(g29)
    c: Distance(g30) = 6.95
    c: Coincident(g30,g28)
    c: Vertical(g30)
    c: Diameter(g31) = 4.2
    c: Diameter(g32) = 4.2
    c: Coincident(g32,g30)
    c: Coincident(g31,g29)
FEATURE [Sketcher::SketchObject] Sketch031  label="fori inferiori switch pompa"
  ArcFitTolerance = 1e-06
  AttachmentSupport = -> [XY_Plane]
  ExternalGeometry = -> [Sketch]
  FullyConstrained = true
  MakeInternals = false
  MapMode = 5
  sketch-geometry (4):
    g0: LineSegment [constr] StartX=-57.2 StartY=1.9e-15 StartZ=0 EndX=-62.45 EndY=1.9e-15 EndZ=0
    g1: LineSegment [constr] StartX=-62.45 StartY=3.25 StartZ=0 EndX=-62.45 EndY=-3.25 EndZ=0
    g2: Circle CenterX=-62.45 CenterY=3.25 CenterZ=0 NormalX=0 NormalY=0 NormalZ=1 AngleXU=0 Radius=1.6
    g3: Circle CenterX=-62.45 CenterY=-3.25 CenterZ=0 NormalX=0 NormalY=0 NormalZ=1 AngleXU=0 Radius=1.6
  constraints (10):
    c: Distance(g0) = 5.25
    c: Coincident(g0,g-3)
    c: PointOnObject(g0,g-3)
    c: Vertical(g1)
    c: DistanceY(g1,g1) = 6.5
    c: Symmetric(g1,g1,g0)
    c: Diameter(g2) = 3.2
    c: Diameter(g3) = 3.2
    c: Coincident(g2,g1)
    c: Coincident(g3,g1)
FEATURE [Sketcher::SketchObject] Sketch032  label="spazio per PILA 18650"
  ArcFitTolerance = 1e-06
  AttachmentSupport = -> [XY_Plane]
  ExternalGeometry = -> [Sketch]
  FullyConstrained = true
  MakeInternals = false
  MapMode = 5
  sketch-geometry (2):
    g0: LineSegment [constr] StartX=-178.142 StartY=-1.74e-14 StartZ=0 EndX=-191.142 EndY=-1.83e-14 EndZ=0
    g1: Circle CenterX=-191.142 CenterY=-1.83e-14 CenterZ=0 NormalX=0 NormalY=0 NormalZ=1 AngleXU=0 Radius=10.5
  constraints (5):
    c: Distance(g0) = 13
    c: Coincident(g0,g-3)
    c: PointOnObject(g0,g-4)
    c: Diameter(g1) = 21
    c: Coincident(g1,g0)
FEATURE [Part::Extrusion] Extrude030  label="Extrude spazio per PILA 18650"
  Base = -> Sketch032
  Dir = (0,0,1)
  DirLink = -> Sketch [Edge45]
  DirMode = 2
  FaceMakerClass = Part::FaceMakerBullseye
  FaceMakerMode = 3
  LengthFwd = 76
  LengthRev = 0
  Placement = pos=(6,0,-72) rot=(0,0,1;0rad)
  Solid = true
  Symmetric = false
FEATURE [Sketcher::SketchObject] Sketch033  label="fermo per scheda micro"
  ArcFitTolerance = 1e-06
  AttachmentSupport = -> [XZ_Plane]
  ExternalGeometry = -> [Sketch]
  FullyConstrained = true
  MakeInternals = false
  MapMode = 5
  Placement = pos=(0,0,0) rot=(1,0,0;1.5708rad)
  sketch-geometry (12):
    g0: LineSegment StartX=-11.6 StartY=6 StartZ=0 EndX=-4 EndY=6 EndZ=0
    g1: LineSegment StartX=-4 StartY=6 StartZ=0 EndX=-4 EndY=36.4 EndZ=0
    g2: LineSegment StartX=-4 StartY=36.4 StartZ=0 EndX=-11.6 EndY=36.4 EndZ=0
    g3: LineSegment StartX=-11.6 StartY=36.4 StartZ=0 EndX=-11.6 EndY=6 EndZ=0
    g4: LineSegment StartX=-80.11 StartY=11.6 StartZ=0 EndX=-70.51 EndY=11.6 EndZ=0
    g5: LineSegment StartX=-70.51 StartY=11.6 StartZ=0 EndX=-70.51 EndY=6 EndZ=0
    g6: LineSegment StartX=-70.51 StartY=6 StartZ=0 EndX=-80.11 EndY=6 EndZ=0
    g7: LineSegment StartX=-80.11 StartY=6 StartZ=0 EndX=-80.11 EndY=11.6 EndZ=0
    g8: LineSegment StartX=-78.51 StartY=36.4 StartZ=0 EndX=-70.51 EndY=36.4 EndZ=0
    g9: LineSegment StartX=-70.51 StartY=36.4 StartZ=0 EndX=-70.51 EndY=30.8 EndZ=0
    g10: LineSegment StartX=-70.51 StartY=30.8 StartZ=0 EndX=-78.51 EndY=30.8 EndZ=0
    g11: LineSegment StartX=-78.51 StartY=30.8 StartZ=0 EndX=-78.51 EndY=36.4 EndZ=0
  constraints (33):
    c: Horizontal(g0)
    c: Coincident(g1,g0)
    c: Coincident(g2,g1)
    c: Horizontal(g2)
    c: Coincident(g3,g2)
    c: Coincident(g3,g0)
    c: Vertical(g3)
    c: DistanceX(g2,g2) = 7.6
    c: Coincident(g1,g-3)
    c: Coincident(g0,g-3)
    c: Horizontal(g4)
    c: Coincident(g5,g4)
    c: Vertical(g5)
    c: Coincident(g6,g5)
    c: Horizontal(g6)
    c: Coincident(g7,g6)
    c: Coincident(g7,g4)
    c: Vertical(g7)
    c: DistanceY(g5,g5) = 5.6
    c: DistanceX(g4,g4) = 9.6
    c: Coincident(g9,g8)
    c: Vertical(g9)
    c: Coincident(g10,g9)
    c: Horizontal(g10)
    c: Coincident(g11,g10)
    c: Coincident(g11,g8)
    c: Vertical(g11)
    c: DistanceY(g9,g9) = 5.6
    c: DistanceX(g10,g10) = 8
    c: Coincident(g4,g-4)
    c: DistanceX(g4,g10) = 1.6
    c: Horizontal(g8)
    c: DistanceY(g8,g1) = 0
FEATURE [Sketcher::SketchObject] Sketch034  label="buchi guida rail"
  ArcFitTolerance = 1e-06
  AttachmentSupport = -> [XY_Plane]
  ExternalGeometry = -> [Sketch]
  FullyConstrained = true
  MakeInternals = false
  MapMode = 5
  sketch-geometry (6):
    g0: LineSegment [constr] StartX=-100.8 StartY=9.1e-15 StartZ=0 EndX=-93.3 EndY=0 EndZ=0
    g1: LineSegment [constr] StartX=-93.3 StartY=0 StartZ=0 EndX=-73.3 EndY=0 EndZ=0
    g2: LineSegment [constr] StartX=-73.3 StartY=0 StartZ=0 EndX=-53.3 EndY=0 EndZ=0
    g3: Circle CenterX=-93.3 CenterY=0 CenterZ=0 NormalX=0 NormalY=0 NormalZ=1 AngleXU=0 Radius=2.5
    g4: Circle CenterX=-73.3 CenterY=0 CenterZ=0 NormalX=0 NormalY=0 NormalZ=1 AngleXU=0 Radius=2.5
    g5: Circle CenterX=-53.3 CenterY=0 CenterZ=0 NormalX=0 NormalY=0 NormalZ=1 AngleXU=0 Radius=2.5
  constraints (15):
    c: Distance(g0) = 7.5
    c: Coincident(g0,g-3)
    c: PointOnObject(g0,g-1)
    c: Distance(g1) = 20
    c: Coincident(g1,g0)
    c: PointOnObject(g1,g-1)
    c: Distance(g2) = 20
    c: Coincident(g2,g1)
    c: PointOnObject(g2,g-1)
    c: Diameter(g3) = 5
    c: Diameter(g4) = 5
    c: Diameter(g5) = 5
    c: Coincident(g3,g0)
    c: Coincident(g4,g1)
    c: Coincident(g5,g2)
FEATURE [Part::Extrusion] Extrude032  label="Extrude buchi guida rail"
  Base = -> Sketch034
  Dir = (0,0,1)
  DirMode = 2
  FaceMakerClass = Part::FaceMakerBullseye
  FaceMakerMode = 3
  LengthFwd = -6.2
  LengthRev = 0
  Placement = pos=(0,0,43.2) rot=(0,0,1;0rad)
  Solid = true
  Symmetric = false
FEATURE [Part::Extrusion] Extrude033  label="Extrude fori superiori per solenoide e oled001"
  Base = -> Sketch030
  Dir = (0,0,1)
  DirMode = 2
  FaceMakerClass = Part::FaceMakerBullseye
  FaceMakerMode = 3
  LengthFwd = -4.8
  LengthRev = 0
  Placement = pos=(0,0,41.2) rot=(0,0,1;0rad)
  Solid = true
  Symmetric = false
FEATURE [Part::Extrusion] Extrude034  label="Extrude fori sotto impugnatura001"
  Base = -> Sketch029
  Dir = (0,0,1)
  DirMode = 2
  FaceMakerClass = Part::FaceMakerBullseye
  FaceMakerMode = 3
  LengthFwd = 5
  LengthRev = 0
  Placement = pos=(0,0,-83) rot=(0,0,1;0rad)
  Solid = true
  Symmetric = false
FEATURE [Part::Extrusion] Extrude035  label="Extrude fori inferiori switch pompa001"
  Base = -> Sketch031
  Dir = (0,0,1)
  DirMode = 2
  FaceMakerClass = Part::FaceMakerBullseye
  FaceMakerMode = 3
  LengthFwd = 4
  LengthRev = 0
  Placement = pos=(0,0,-1.7) rot=(0,0,1;0rad)
  Solid = true
  Symmetric = false
FEATURE [Part::Extrusion] Extrude036  label="Extrude foro sotto posteriore M3x5x007"
  Base = -> Sketch027
  Dir = (0,0,1)
  DirMode = 2
  FaceMakerClass = Part::FaceMakerBullseye
  FaceMakerMode = 3
  LengthFwd = 6.2
  LengthRev = 0
  Placement = pos=(0,0,-9.6) rot=(0,0,1;0rad)
  Solid = true
  Symmetric = false
FEATURE [Part::Extrusion] Extrude037  label="Extrude foro sotto anteriore M3x5x007"
  Base = -> Sketch026
  Dir = (0,0,1)
  DirMode = 2
  FaceMakerClass = Part::FaceMakerBullseye
  FaceMakerMode = 3
  LengthFwd = 6.2
  LengthRev = 0
  Solid = true
  Symmetric = false
FEATURE [Sketcher::SketchObject] Sketch035  label="foro per fissaggio micro"
  ArcFitTolerance = 1e-06
  AttachmentSupport = -> [XZ_Plane]
  ExternalGeometry = -> [Sketch,Sketch033]
  FullyConstrained = true
  MakeInternals = false
  MapMode = 5
  Placement = pos=(0,0,0) rot=(1,0,0;1.5708rad)
  sketch-geometry (3):
    g0: Circle CenterX=-7.8 CenterY=21.2 CenterZ=0 NormalX=0 NormalY=0 NormalZ=1 AngleXU=0 Radius=1.6
    g1: GeomPoint [constr] X=-4 Y=21.2 Z=0
    g2: LineSegment [constr] StartX=-4 StartY=21.2 StartZ=0 EndX=-11.6 EndY=21.2 EndZ=0
  constraints (6):
    c: Diameter(g0) = 3.2
    c: Symmetric(g-3,g-3,g1)
    c: Coincident(g2,g1)
    c: Horizontal(g2)
    c: DistanceX(g-4,g2) = 0
    c: Symmetric(g2,g1,g0)
FEATURE [Part::Extrusion] Extrude038  label="Extrude foro per fissaggio micro"
  Base = -> Sketch035
  Dir = (0,-1,2e-16)
  DirMode = 2
  FaceMakerClass = Part::FaceMakerBullseye
  FaceMakerMode = 3
  LengthFwd = 3
  LengthRev = 0
  Placement = pos=(0,8.6,0) rot=(0,0,1;0rad)
  Solid = true
  Symmetric = false
FEATURE [Sketcher::SketchObject] Sketch036  label="supporto per alimentatore"
  ArcFitTolerance = 1e-06
  AttachmentSupport = -> [XZ_Plane]
  ExternalGeometry = -> [Sketch,Sketch016,Sketch022]
  FullyConstrained = true
  MakeInternals = false
  MapMode = 5
  Placement = pos=(0,0,0) rot=(1,0,0;1.5708rad)
  sketch-geometry (5):
    g0: LineSegment StartX=-211.843 StartY=-50.0944 StartZ=0 EndX=-211.843 EndY=-80.4316 EndZ=0
    g1: LineSegment StartX=-211.843 StartY=-50.0944 StartZ=0 EndX=-207.775 EndY=-41.3701 EndZ=0
    g2: LineSegment [constr] StartX=-209.443 StartY=-50.0944 StartZ=0 EndX=-209.443 EndY=-80.4316 EndZ=0
    g3: LineSegment StartX=-207.775 StartY=-41.3701 StartZ=0 EndX=-207.775 EndY=-80.4316 EndZ=0
    g4: LineSegment StartX=-211.843 StartY=-80.4316 StartZ=0 EndX=-207.775 EndY=-80.4316 EndZ=0
  constraints (15):
    c: Vertical(g0)
    c: Coincident(g1,g0)
    c: Vertical(g2)
    c: Tangent(g2,g-5)
    c: Coincident(g3,g1)
    c: Vertical(g3)
    c: DistanceY(g-3,g3) = -2
    c: Tangent(g1,g-8)
    c: DistanceY(g-3,g0) = -2
    c: Coincident(g4,g0)
    c: Coincident(g4,g3)
    c: Tangent(g0,g-6)
    c: DistanceY(g-3,g2) = -2
    c: DistanceY(g2,g0) = 0
    c: DistanceX(g-3,g3) = 6.8
FEATURE [Part::Extrusion] Extrude039  label="Extrude039 supporto alimentatore"
  Base = -> Sketch036
  Dir = (0,-1,2e-16)
  DirMode = 2
  FaceMakerClass = Part::FaceMakerBullseye
  FaceMakerMode = 3
  LengthFwd = 25.2
  LengthRev = 0
  Solid = true
  Symmetric = true
FEATURE [Sketcher::SketchObject] Sketch037  label="scavo per alimentatore"
  ArcFitTolerance = 1e-06
  AttachmentSupport = -> [XZ_Plane]
  ExternalGeometry = -> [Sketch036]
  FullyConstrained = true
  MakeInternals = false
  MapMode = 5
  Placement = pos=(0,0,0) rot=(1,0,0;1.5708rad)
  sketch-geometry (4):
    g0: LineSegment StartX=-209.575 StartY=-50.4316 StartZ=0 EndX=-209.575 EndY=-80.4316 EndZ=0
    g1: LineSegment StartX=-209.575 StartY=-50.4316 StartZ=0 EndX=-207.775 EndY=-50.4316 EndZ=0
    g2: LineSegment StartX=-207.775 StartY=-50.4316 StartZ=0 EndX=-207.775 EndY=-80.4316 EndZ=0
    g3: LineSegment StartX=-207.775 StartY=-80.4316 StartZ=0 EndX=-209.575 EndY=-80.4316 EndZ=0
  constraints (11):
    c: Vertical(g0)
    c: Coincident(g1,g0)
    c: Horizontal(g1)
    c: Coincident(g2,g1)
    c: Vertical(g2)
    c: Coincident(g3,g2)
    c: Coincident(g3,g0)
    c: Horizontal(g3)
    c: DistanceX(g1,g1) = 1.8
    c: Coincident(g2,g-3)
    c: DistanceY(g2,g2) = 30
FEATURE [Part::Extrusion] Extrude040  label="Extrude040 scavo alimentatore"
  Base = -> Sketch037
  Dir = (0,-1,2e-16)
  DirMode = 2
  FaceMakerClass = Part::FaceMakerBullseye
  FaceMakerMode = 3
  LengthFwd = 19.5
  LengthRev = 0
  Solid = true
  Symmetric = true
FEATURE [Part::Extrusion] Extrude031  label="Extrude fermo per scheda micro"
  Base = -> Sketch033
  Dir = (0,-1,2e-16)
  DirMode = 2
  FaceMakerClass = Part::FaceMakerBullseye
  FaceMakerMode = 3
  LengthFwd = 3
  LengthRev = 0
  Placement = pos=(0,8.6,0) rot=(0,0,1;0rad)
  Solid = true
  Symmetric = false
FEATURE [Sketcher::SketchObject] Sketch038  label="scavo driver solenoide"
  ArcFitTolerance = 1e-06
  AttachmentSupport = -> [XZ_Plane]
  ExternalGeometry = -> [Sketch,Sketch036]
  FullyConstrained = true
  MakeInternals = false
  MapMode = 5
  Placement = pos=(0,0,0) rot=(1,0,0;1.5708rad)
  sketch-geometry (7):
    g0: LineSegment StartX=-192.222 StartY=-8.0175 StartZ=0 EndX=-194.941 EndY=-6.74965 EndZ=0
    g1: LineSegment StartX=-194.941 StartY=-6.74965 StartZ=0 EndX=-212.269 EndY=-43.9083 EndZ=0
    g2: LineSegment StartX=-192.222 StartY=-8.0175 StartZ=0 EndX=-188.779 EndY=-9.62345 EndZ=0
    g3: LineSegment StartX=-188.779 StartY=-9.62345 StartZ=0 EndX=-205.357 EndY=-45.1761 EndZ=0
    g4: LineSegment StartX=-205.357 StartY=-45.1761 StartZ=0 EndX=-209.55 EndY=-45.1761 EndZ=0
    g5: LineSegment [constr] StartX=-212.269 StartY=-43.9083 StartZ=0 EndX=-209.55 EndY=-45.1761 EndZ=0
    g6: LineSegment StartX=-212.269 StartY=-43.9083 StartZ=0 EndX=-209.55 EndY=-45.1761 EndZ=0
  constraints (20):
    c: Coincident(g1,g0)
    c: Coincident(g3,g2)
    c: Coincident(g4,g3)
    c: Distance(g2) = 3.8
    c: Distance(g1) = 41
    c: Coincident(g5,g1)
    c: Distance(g5) = 3
    c: Perpendicular(g5,g-3)
    c: Parallel(g1,g-3)
    c: Perpendicular(g1,g0)
    c: Distance(g0) = 3
    c: Coincident(g6,g1)
    c: Parallel(g3,g-3)
    c: Perpendicular(g2,g3)
    c: Coincident(g2,g0)
    c: Perpendicular(g-4,g4)
    c: PointOnObject(g5,g-3)
    c: Distance(g-3,g5) = 9.6
    c: Coincident(g4,g5)
    c: Coincident(g6,g4)
FEATURE [Part::Extrusion] Extrude041  label="Extrude scavo driver solenoide"
  Base = -> Sketch038
  Dir = (0,-1,2e-16)
  DirMode = 2
  FaceMakerClass = Part::FaceMakerBullseye
  FaceMakerMode = 3
  LengthFwd = 20.6
  LengthRev = 0
  Solid = true
  Symmetric = true
FEATURE [Sketcher::SketchObject] Sketch039  label="scavo per cavo usb per micro"
  ArcFitTolerance = 1e-06
  AttachmentSupport = -> [XZ_Plane]
  ExternalGeometry = -> [Sketch,Sketch016]
  FullyConstrained = true
  MakeInternals = false
  MapMode = 5
  Placement = pos=(0,0,0) rot=(1,0,0;1.5708rad)
  sketch-geometry (4):
    g0: LineSegment StartX=-82.51 StartY=36.4 StartZ=0 EndX=-74.51 EndY=36.4 EndZ=0
    g1: LineSegment StartX=-74.51 StartY=36.4 StartZ=0 EndX=-74.51 EndY=30.8 EndZ=0
    g2: LineSegment StartX=-74.51 StartY=30.8 StartZ=0 EndX=-82.51 EndY=30.8 EndZ=0
    g3: LineSegment StartX=-82.51 StartY=30.8 StartZ=0 EndX=-82.51 EndY=36.4 EndZ=0
  constraints (11):
    c: Coincident(g1,g0)
    c: Vertical(g1)
    c: Coincident(g2,g1)
    c: Horizontal(g2)
    c: Coincident(g3,g2)
    c: Coincident(g3,g0)
    c: Vertical(g3)
    c: Tangent(g0,g-3)
    c: Tangent(g2,g-4)
    c: Tangent(g3,g-4)
    c: Tangent(g1,g-4)
FEATURE [Part::Extrusion] Extrude042  label="Extrude scavo per cavo usb per micro"
  Base = -> Sketch039
  Dir = (0,-1,2e-16)
  DirMode = 2
  FaceMakerClass = Part::FaceMakerBullseye
  FaceMakerMode = 3
  LengthFwd = 11.2
  LengthRev = 0
  Solid = true
  Symmetric = true
FEATURE [Sketcher::SketchObject] Sketch040  label="scavo saldature alimentatore connettore 5v"
  ArcFitTolerance = 1e-06
  AttachmentSupport = -> [XZ_Plane]
  ExternalGeometry = -> [Sketch037]
  FullyConstrained = true
  MakeInternals = false
  MapMode = 5
  Placement = pos=(0,0,0) rot=(1,0,0;1.5708rad)
  sketch-geometry (4):
    g0: LineSegment StartX=-211.175 StartY=-52.4316 StartZ=0 EndX=-211.175 EndY=-56.4316 EndZ=0
    g1: LineSegment StartX=-211.175 StartY=-52.4316 StartZ=0 EndX=-209.575 EndY=-52.4316 EndZ=0
    g2: LineSegment StartX=-209.575 StartY=-52.4316 StartZ=0 EndX=-209.575 EndY=-56.4316 EndZ=0
    g3: LineSegment StartX=-209.575 StartY=-56.4316 StartZ=0 EndX=-211.175 EndY=-56.4316 EndZ=0
  constraints (11):
    c: Vertical(g0)
    c: Coincident(g1,g0)
    c: Horizontal(g1)
    c: Coincident(g2,g1)
    c: Coincident(g3,g2)
    c: Coincident(g3,g0)
    c: Horizontal(g3)
    c: DistanceX(g1,g1) = 1.6
    c: DistanceY(g2,g2) = 4
    c: Tangent(g2,g-3)
    c: DistanceY(g1,g-3) = 2
FEATURE [Part::Extrusion] Extrude043  label="Extrude scavo saldature alimentatore connettore 5v"
  Base = -> Sketch040
  Dir = (0,-1,2e-16)
  DirMode = 2
  FaceMakerClass = Part::FaceMakerBullseye
  FaceMakerMode = 3
  LengthFwd = 8
  LengthRev = 0
  Solid = true
  Symmetric = true
FEATURE [Sketcher::SketchObject] Sketch041  label="scavo saldature alimentatore connettore 5v verticali"
  ArcFitTolerance = 1e-06
  AttachmentSupport = -> [XZ_Plane]
  ExternalGeometry = -> [Sketch037]
  FullyConstrained = true
  MakeInternals = false
  MapMode = 5
  Placement = pos=(0,0,0) rot=(1,0,0;1.5708rad)
  sketch-geometry (4):
    g0: LineSegment StartX=-211.175 StartY=-53.6316 StartZ=0 EndX=-209.575 EndY=-53.6316 EndZ=0
    g1: LineSegment StartX=-209.575 StartY=-53.6316 StartZ=0 EndX=-209.575 EndY=-76.6316 EndZ=0
    g2: LineSegment StartX=-209.575 StartY=-76.6316 StartZ=0 EndX=-211.175 EndY=-76.6316 EndZ=0
    g3: LineSegment StartX=-211.175 StartY=-76.6316 StartZ=0 EndX=-211.175 EndY=-53.6316 EndZ=0
  constraints (11):
    c: Horizontal(g0)
    c: Coincident(g1,g0)
    c: Coincident(g2,g1)
    c: Horizontal(g2)
    c: Coincident(g3,g2)
    c: Coincident(g3,g0)
    c: Vertical(g3)
    c: DistanceY(g3,g3) = 23
    c: DistanceX(g0,g0) = 1.6
    c: Tangent(g1,g-3)
    c: DistanceY(g0,g-3) = 3.2
FEATURE [Part::Extrusion] Extrude044  label="Extrude scavo saldature alimentatore connettore 5v verticali"
  Base = -> Sketch041
  Dir = (0,-1,2e-16)
  DirMode = 2
  FaceMakerClass = Part::FaceMakerBullseye
  FaceMakerMode = 3
  LengthFwd = 3.2
  LengthRev = 0
  Placement = pos=(0,8.3,0) rot=(0,0,1;0rad)
  Solid = true
  Symmetric = false
FEATURE [Sketcher::SketchObject] Sketch042  label="fermi per driver solenoide e alimentatore"
  ArcFitTolerance = 1e-06
  AttachmentSupport = -> [XZ_Plane]
  ExternalGeometry = -> [Sketch036,Sketch037,Sketch,Sketch038]
  FullyConstrained = true
  MakeInternals = false
  MapMode = 5
  Placement = pos=(0,0,0) rot=(1,0,0;1.5708rad)
  sketch-geometry (27):
    g0: LineSegment StartX=-200.506 StartY=-25.7811 StartZ=0 EndX=-201.436 EndY=-27.775 EndZ=0
    g1: LineSegment StartX=-201.436 StartY=-27.775 StartZ=0 EndX=-199.442 EndY=-28.7048 EndZ=0
    g2: LineSegment StartX=-199.442 StartY=-28.7048 StartZ=0 EndX=-198.512 EndY=-26.7109 EndZ=0
    g3: LineSegment StartX=-198.512 StartY=-26.7109 StartZ=0 EndX=-200.506 EndY=-25.7811 EndZ=0
    g4: LineSegment StartX=-201.28 StartY=-23.6549 StartZ=0 EndX=-203.562 EndY=-28.5489 EndZ=0
    g5: LineSegment StartX=-203.562 StartY=-28.5489 StartZ=0 EndX=-200.118 EndY=-30.1549 EndZ=0
    g6: LineSegment StartX=-197.992 StartY=-29.381 StartZ=0 EndX=-197.062 EndY=-27.3871 EndZ=0
    g7: LineSegment StartX=-197.836 StartY=-25.2608 StartZ=0 EndX=-201.28 EndY=-23.6549 EndZ=0
    g8: LineSegment [constr] StartX=-198.668 StartY=-30.8311 StartZ=0 EndX=-197.992 EndY=-29.381 EndZ=0
    g9: LineSegment [constr] StartX=-198.668 StartY=-30.8311 StartZ=0 EndX=-200.118 EndY=-30.1549 EndZ=0
    g10: ArcOfCircle CenterX=-198.512 CenterY=-26.7109 CenterZ=0 NormalX=0 NormalY=0 NormalZ=1 AngleXU=0 Radius=1.6 StartAngle=5.84685 EndAngle=7.41765
    g11: GeomPoint [constr] X=-196.386 Y=-25.937 Z=0
    g12: ArcOfCircle CenterX=-199.442 CenterY=-28.7048 CenterZ=0 NormalX=0 NormalY=0 NormalZ=1 AngleXU=0 Radius=1.6 StartAngle=4.27606 EndAngle=5.84685
    g13: GeomPoint [constr] X=-198.668 Y=-30.8311 Z=0
    g14: LineSegment StartX=-207.775 StartY=-46.8316 StartZ=0 EndX=-207.775 EndY=-50.8316 EndZ=0
    g15: LineSegment StartX=-207.775 StartY=-46.8316 StartZ=0 EndX=-203.775 EndY=-46.8316 EndZ=0
    g16: LineSegment StartX=-203.775 StartY=-46.8316 StartZ=0 EndX=-203.775 EndY=-50.8316 EndZ=0
    g17: LineSegment StartX=-207.775 StartY=-50.8316 StartZ=0 EndX=-203.775 EndY=-50.8316 EndZ=0
    g18: LineSegment StartX=-209.375 StartY=-52.4316 StartZ=0 EndX=-203.775 EndY=-52.4316 EndZ=0
    g19: LineSegment StartX=-202.175 StartY=-50.8316 StartZ=0 EndX=-202.175 EndY=-46.8316 EndZ=0
    g20: LineSegment StartX=-203.775 StartY=-45.2316 StartZ=0 EndX=-209.375 EndY=-45.2316 EndZ=0
    g21: LineSegment StartX=-209.375 StartY=-45.2316 StartZ=0 EndX=-209.375 EndY=-52.4316 EndZ=0
    g22: ArcOfCircle CenterX=-203.775 CenterY=-46.8316 CenterZ=0 NormalX=0 NormalY=0 NormalZ=1 AngleXU=0 Radius=1.6 StartAngle=1.8e-15 EndAngle=1.5708
    g23: GeomPoint [constr] X=-202.175 Y=-45.2316 Z=0
    g24: ArcOfCircle CenterX=-203.775 CenterY=-50.8316 CenterZ=0 NormalX=0 NormalY=0 NormalZ=1 AngleXU=0 Radius=1.6 StartAngle=4.71239 EndAngle=6.28319
    g25: GeomPoint [constr] X=-202.175 Y=-52.4316 Z=0
    g26: LineSegment [constr] StartX=-207.775 StartY=-50.4316 StartZ=0 EndX=-207.775 EndY=-50.8316 EndZ=0
  constraints (69):
    c: Coincident(g1,g0)
    c: Coincident(g2,g1)
    c: Coincident(g3,g2)
    c: Coincident(g3,g0)
    c: Parallel(g0,g2)
    c: Perpendicular(g3,g0)
    c: Perpendicular(g1,g0)
    c: Coincident(g5,g4)
    c: Coincident(g7,g4)
    c: Distance(g3) = 2.2
    c: Distance(g2) = 2.2
    c: Parallel(g6,g2)
    c: Parallel(g6,g4)
    c: Perpendicular(g5,g6)
    c: Perpendicular(g7,g6)
    c: Distance(g13,g11) = 5.4
    c: Distance(g5,g13) = 5.4
    c: Coincident(g9,g8)
    c: Distance(g8) = 1.6
    c: Distance(g9) = 1.6
    c: Perpendicular(g9,g8)
    c: Parallel(g8,g6)
    c: Coincident(g8,g13)
    c: Distance(g8,g1) = 1.6
    c: Distance(g9,g1) = 1.6
    c: Tangent(g0,g-5)
    c: Distance(g0,g-6) = 19.2
    c: PointOnObject(g11,g7)
    c: PointOnObject(g11,g6)
    c: Tangent(g7,g10) = -1.5708
    c: Tangent(g6,g10) = -1.5708
    c: PointOnObject(g13,g5)
    c: Tangent(g5,g12) = -1.5708
    c: Tangent(g6,g12) = -1.5708
    c: Equal(g10,g12)
    c: Coincident(g10,g2)
    c: Vertical(g14)
    c: Coincident(g15,g14)
    c: Horizontal(g15)
    c: Coincident(g16,g15)
    c: Vertical(g16)
    c: Coincident(g17,g14)
    c: Coincident(g17,g16)
    c: Horizontal(g17)
    c: Distance(g16) = 4
    c: Distance(g15) = 4
    c: Horizontal(g18)
    c: Vertical(g19)
    c: Horizontal(g20)
    c: Coincident(g21,g20)
    c: Coincident(g21,g18)
    c: Vertical(g21)
    c: Distance(g20,g23) = 7.2
    c: Distance(g25,g23) = 7.2
    c: DistanceY(g18,g14) = 1.6
    c: DistanceX(g18,g14) = 1.6
    c: PointOnObject(g23,g20)
    c: PointOnObject(g23,g19)
    c: Tangent(g20,g22) = -1.5708
    c: Tangent(g19,g22) = -1.5708
    c: PointOnObject(g25,g19)
    c: Tangent(g18,g24) = -1.5708
    c: Tangent(g19,g24) = -1.5708
    c: Equal(g22,g24)
    c: Coincident(g22,g15)
    c: Vertical(g26)
    c: Distance(g26) = 0.4
    c: Coincident(g26,g-4)
    c: Coincident(g14,g26)
FEATURE [Part::Extrusion] Extrude045  label="Extrude fermi per driver solenoide e alimentatore"
  Base = -> Sketch042
  Dir = (0,-1,2e-16)
  DirMode = 2
  FaceMakerClass = Part::FaceMakerBullseye
  FaceMakerMode = 3
  LengthFwd = 25.2
  LengthRev = 0
  Solid = true
  Symmetric = true
FEATURE [Sketcher::SketchObject] Sketch043  label="scavo pulizia fermo alimentatore"
  ArcFitTolerance = 1e-06
  AttachmentSupport = -> [XZ_Plane]
  ExternalGeometry = -> [Sketch042,Sketch036,Sketch037]
  FullyConstrained = true
  MakeInternals = false
  MapMode = 5
  Placement = pos=(0,0,0) rot=(1,0,0;1.5708rad)
  sketch-geometry (6):
    g0: LineSegment StartX=-209.375 StartY=-52.4316 StartZ=0 EndX=-209.375 EndY=-50.4316 EndZ=0
    g1: LineSegment StartX=-209.375 StartY=-50.4316 StartZ=0 EndX=-207.775 EndY=-50.4316 EndZ=0
    g2: LineSegment StartX=-207.775 StartY=-50.4316 StartZ=0 EndX=-207.775 EndY=-45.2316 EndZ=0
    g3: LineSegment StartX=-207.775 StartY=-45.2316 StartZ=0 EndX=-202.175 EndY=-45.2316 EndZ=0
    g4: LineSegment StartX=-202.175 StartY=-45.2316 StartZ=0 EndX=-202.175 EndY=-52.4316 EndZ=0
    g5: LineSegment StartX=-202.175 StartY=-52.4316 StartZ=0 EndX=-209.375 EndY=-52.4316 EndZ=0
  constraints (13):
    c: Vertical(g0)
    c: Coincident(g1,g0)
    c: Coincident(g2,g1)
    c: Coincident(g3,g2)
    c: Coincident(g4,g3)
    c: Coincident(g5,g4)
    c: Coincident(g5,g0)
    c: Horizontal(g5)
    c: Coincident(g0,g-6)
    c: Tangent(g1,g-8)
    c: Tangent(g2,g-4)
    c: Tangent(g3,g-7)
    c: Tangent(g4,g-3)
FEATURE [Part::Extrusion] Extrude046  label="Extrude scavo pulizia fermo alimentatore"
  Base = -> Sketch043
  Dir = (0,-1,2e-16)
  DirMode = 2
  FaceMakerClass = Part::FaceMakerBullseye
  FaceMakerMode = 3
  LengthFwd = 19.5
  LengthRev = 0
  Solid = true
  Symmetric = true
FEATURE [Sketcher::SketchObject] Sketch044  label="buchini per fissaggio oled"
  ArcFitTolerance = 1e-06
  AttachmentSupport = -> [YZ_Plane]
  ExternalGeometry = -> [Sketch]
  FullyConstrained = true
  MakeInternals = false
  MapMode = 5
  Placement = pos=(0,0,0) rot=(0.57735,0.57735,0.57735;2.0944rad)
  sketch-geometry (5):
    g0: LineSegment [constr] StartX=1.5e-14 StartY=67.3588 StartZ=0 EndX=0 EndY=64.3588 EndZ=0
    g1: LineSegment [constr] StartX=0 StartY=64.3588 StartZ=0 EndX=10.4 EndY=64.3588 EndZ=0
    g2: LineSegment [constr] StartX=0 StartY=64.3588 StartZ=0 EndX=-10.4 EndY=64.3588 EndZ=0
    g3: Circle CenterX=10.4 CenterY=64.3588 CenterZ=0 NormalX=0 NormalY=0 NormalZ=1 AngleXU=0 Radius=1.5
    g4: Circle CenterX=-10.4 CenterY=64.3588 CenterZ=0 NormalX=0 NormalY=0 NormalZ=1 AngleXU=0 Radius=1.5
  constraints (13):
    c: Distance(g0) = 3
    c: PointOnObject(g0,g-2)
    c: Coincident(g1,g0)
    c: Horizontal(g1)
    c: Coincident(g2,g0)
    c: Horizontal(g2)
    c: DistanceX(g1,g1) = 10.4
    c: Coincident(g3,g1)
    c: Diameter(g4) = 3
    c: Coincident(g4,g2)
    c: Coincident(g0,g-7)
    c: Equal(g1,g2)
    c: Equal(g4,g3)
FEATURE [Part::Extrusion] Extrude047  label="Extrude buchini per fissaggio oled"
  Base = -> Sketch044
  Dir = (1,0,0)
  DirMode = 2
  FaceMakerClass = Part::FaceMakerBullseye
  FaceMakerMode = 3
  LengthFwd = 10
  LengthRev = 0
  Placement = pos=(-186,0,0) rot=(0,0,1;0rad)
  Solid = true
  Symmetric = false
FEATURE [Sketcher::SketchObject] Sketch046  label="scavo 5x5 neopixel"
  ArcFitTolerance = 1e-06
  AttachmentSupport = -> [YZ_Plane002]
  FullyConstrained = true
  MakeInternals = false
  MapMode = 5
  Placement = pos=(0,0,0) rot=(0.57735,0.57735,0.57735;2.0944rad)
  sketch-geometry (4):
    g0: LineSegment StartX=-2.7 StartY=2.7 StartZ=0 EndX=2.7 EndY=2.7 EndZ=0
    g1: LineSegment StartX=2.7 StartY=2.7 StartZ=0 EndX=2.7 EndY=-2.7 EndZ=0
    g2: LineSegment StartX=2.7 StartY=-2.7 StartZ=0 EndX=-2.7 EndY=-2.7 EndZ=0
    g3: LineSegment StartX=-2.7 StartY=-2.7 StartZ=0 EndX=-2.7 EndY=2.7 EndZ=0
  constraints (11):
    c: Horizontal(g0)
    c: Coincident(g1,g0)
    c: Vertical(g1)
    c: Coincident(g2,g1)
    c: Horizontal(g2)
    c: Coincident(g3,g2)
    c: Coincident(g3,g0)
    c: Vertical(g3)
    c: DistanceX(g0,g0) = 5.4
    c: DistanceY(g1,g1) = 5.4
    c: Symmetric(g0,g1,g-1)
FEATURE [Sketcher::SketchObject] Sketch047  label="scavo 10x10 neopixel corpo"
  ArcFitTolerance = 1e-06
  AttachmentOffset = pos=(0,0,1) rot=(0,0,1;0rad)
  AttachmentSupport = -> [YZ_Plane002]
  FullyConstrained = true
  MakeInternals = false
  MapMode = 5
  Placement = pos=(1,0,0) rot=(0.57735,0.57735,0.57735;2.0944rad)
  sketch-geometry (4):
    g0: LineSegment StartX=-5 StartY=5.1 StartZ=0 EndX=5 EndY=5.1 EndZ=0
    g1: LineSegment StartX=5 StartY=5.1 StartZ=0 EndX=5 EndY=-5.1 EndZ=0
    g2: LineSegment StartX=5 StartY=-5.1 StartZ=0 EndX=-5 EndY=-5.1 EndZ=0
    g3: LineSegment StartX=-5 StartY=-5.1 StartZ=0 EndX=-5 EndY=5.1 EndZ=0
  constraints (11):
    c: Horizontal(g0)
    c: Coincident(g1,g0)
    c: Vertical(g1)
    c: Coincident(g2,g1)
    c: Horizontal(g2)
    c: Coincident(g3,g2)
    c: Coincident(g3,g0)
    c: Vertical(g3)
    c: DistanceX(g0,g0) = 10
    c: DistanceY(g1,g1) = 10.2
    c: Symmetric(g0,g2,g-1)
FEATURE [Sketcher::SketchObject] Sketch048  label="buco per perno blocco neopixel"
  ArcFitTolerance = 1e-06
  AttachmentSupport = -> [XZ_Plane002]
  FullyConstrained = true
  MakeInternals = false
  MapMode = 5
  Placement = pos=(0,0,0) rot=(1,0,0;1.5708rad)
  sketch-geometry (4):
    g0: LineSegment StartX=3 StartY=1.2 StartZ=0 EndX=3 EndY=-1.2 EndZ=0
    g1: LineSegment StartX=3 StartY=-1.2 StartZ=0 EndX=5.4 EndY=-1.2 EndZ=0
    g2: LineSegment StartX=5.4 StartY=-1.2 StartZ=0 EndX=5.4 EndY=1.2 EndZ=0
    g3: LineSegment StartX=5.4 StartY=1.2 StartZ=0 EndX=3 EndY=1.2 EndZ=0
  constraints (11):
    c: Coincident(g1,g0)
    c: Horizontal(g1)
    c: Coincident(g2,g1)
    c: Vertical(g2)
    c: Coincident(g3,g2)
    c: Coincident(g3,g0)
    c: Horizontal(g3)
    c: DistanceX(g1,g1) = 2.4
    c: DistanceY(g2,g2) = 2.4
    c: Symmetric(g0,g0,g-1)
    c: DistanceX(g-1,g0) = 3
FEATURE [Sketcher::SketchObject] Sketch045  label="blocco principale per neopixel"
  ArcFitTolerance = 1e-06
  AttachmentSupport = -> [XZ_Plane002]
  ExternalGeometry = -> [Sketch048]
  FullyConstrained = true
  MakeInternals = false
  MapMode = 5
  Placement = pos=(0,0,0) rot=(1,0,0;1.5708rad)
  sketch-geometry (6):
    g0: LineSegment StartX=0 StartY=5.1 StartZ=0 EndX=0 EndY=-5.1 EndZ=0
    g1: LineSegment StartX=0 StartY=-5.1 StartZ=0 EndX=3 EndY=-5.1 EndZ=0
    g2: LineSegment StartX=7 StartY=-1.1 StartZ=0 EndX=7 EndY=5.1 EndZ=0
    g3: LineSegment StartX=7 StartY=5.1 StartZ=0 EndX=0 EndY=5.1 EndZ=0
    g4: ArcOfCircle CenterX=3 CenterY=-1.1 CenterZ=0 NormalX=0 NormalY=0 NormalZ=1 AngleXU=0 Radius=4 StartAngle=4.71239 EndAngle=6.28319
    g5: GeomPoint [constr] X=7 Y=-5.1 Z=0
  constraints (15):
    c: Vertical(g0)
    c: Coincident(g1,g0)
    c: Horizontal(g1)
    c: Vertical(g2)
    c: Coincident(g3,g2)
    c: Coincident(g3,g0)
    c: Horizontal(g3)
    c: DistanceY(g0,g0) = 10.2
    c: Symmetric(g0,g0,g-1)
    c: DistanceX(g3,g3) = 7
    c: PointOnObject(g5,g2)
    c: PointOnObject(g5,g1)
    c: Tangent(g2,g4) = -1.5708
    c: Tangent(g1,g4) = -1.5708
    c: DistanceX(g-3,g1) = 0
FEATURE [Sketcher::SketchObject] Sketch049  label="rinforzi esterni per corpo neopoixel"
  ArcFitTolerance = 1e-06
  AttachmentSupport = -> [XZ_Plane002]
  ExternalGeometry = -> [Sketch045]
  FullyConstrained = true
  MakeInternals = false
  MapMode = 5
  Placement = pos=(0,0,0) rot=(1,0,0;1.5708rad)
  sketch-geometry (8):
    g0: LineSegment StartX=1 StartY=-4.1 StartZ=0 EndX=2 EndY=-4.1 EndZ=0
    g1: LineSegment StartX=2 StartY=-4.1 StartZ=0 EndX=2 EndY=-5.1 EndZ=0
    g2: LineSegment StartX=2 StartY=-5.1 StartZ=0 EndX=1 EndY=-5.1 EndZ=0
    g3: LineSegment StartX=1 StartY=-5.1 StartZ=0 EndX=1 EndY=-4.1 EndZ=0
    g4: LineSegment StartX=1 StartY=5.1 StartZ=0 EndX=2 EndY=5.1 EndZ=0
    g5: LineSegment StartX=2 StartY=5.1 StartZ=0 EndX=2 EndY=4.1 EndZ=0
    g6: LineSegment StartX=2 StartY=4.1 StartZ=0 EndX=1 EndY=4.1 EndZ=0
    g7: LineSegment StartX=1 StartY=4.1 StartZ=0 EndX=1 EndY=5.1 EndZ=0
  constraints (24):
    c: Horizontal(g0)
    c: Coincident(g1,g0)
    c: Vertical(g1)
    c: Coincident(g2,g1)
    c: Horizontal(g2)
    c: Coincident(g3,g2)
    c: Coincident(g3,g0)
    c: Vertical(g3)
    c: Horizontal(g4)
    c: Coincident(g5,g4)
    c: Vertical(g5)
    c: Coincident(g6,g5)
    c: Horizontal(g6)
    c: Coincident(g7,g6)
    c: Coincident(g7,g4)
    c: Vertical(g7)
    c: DistanceX(g4,g4) = 1
    c: DistanceY(g5,g5) = 1
    c: DistanceX(g0,g0) = 1
    c: DistanceY(g1,g1) = 1
    c: DistanceX(g-3,g4) = 1
    c: DistanceY(g-3,g4) = 0
    c: DistanceX(g-4,g2) = 1
    c: DistanceY(g2,g-4) = 0
FEATURE [Sketcher::SketchObject] Sketch052  label="scavo saldature driver solenoide"
  ArcFitTolerance = 1e-06
  AttachmentSupport = -> [XZ_Plane]
  ExternalGeometry = -> [Sketch038]
  FullyConstrained = true
  MakeInternals = false
  MapMode = 5
  Placement = pos=(0,0,0) rot=(1,0,0;1.5708rad)
  sketch-geometry (4):
    g0: LineSegment StartX=-195.304 StartY=-6.5806 StartZ=0 EndX=-196.994 EndY=-10.2058 EndZ=0
    g1: LineSegment StartX=-196.994 StartY=-10.2058 StartZ=0 EndX=-196.632 EndY=-10.3749 EndZ=0
    g2: LineSegment StartX=-196.632 StartY=-10.3749 StartZ=0 EndX=-194.941 EndY=-6.74965 EndZ=0
    g3: LineSegment StartX=-194.941 StartY=-6.74965 StartZ=0 EndX=-195.304 EndY=-6.5806 EndZ=0
  constraints (11):
    c: Coincident(g1,g0)
    c: Coincident(g2,g1)
    c: Coincident(g3,g2)
    c: Coincident(g3,g0)
    c: Parallel(g2,g0)
    c: Perpendicular(g2,g3)
    c: Perpendicular(g1,g2,g1) = 1.5708
    c: Parallel(g2,g-3)
    c: Distance(g2) = 4
    c: Distance(g3) = 0.4
    c: Coincident(g2,g-3)
FEATURE [Part::Extrusion] Extrude055  label="Extrude scavo saldature driver solenoide"
  Base = -> Sketch052
  Dir = (0,-1,2e-16)
  DirMode = 2
  FaceMakerClass = Part::FaceMakerBullseye
  FaceMakerMode = 3
  LengthFwd = 6
  LengthRev = 0
  Solid = true
  Symmetric = true
FEATURE [Sketcher::SketchObject] Sketch053  label="scavo saldature rumble"
  ArcFitTolerance = 1e-06
  AttachmentSupport = -> [XZ_Plane]
  ExternalGeometry = -> [Sketch019]
  FullyConstrained = true
  MakeInternals = false
  MapMode = 5
  Placement = pos=(0,0,0) rot=(1,0,0;1.5708rad)
  sketch-geometry (4):
    g0: LineSegment StartX=-164.507 StartY=-41.6446 StartZ=0 EndX=-165.743 EndY=-45.4488 EndZ=0
    g1: LineSegment StartX=-165.743 StartY=-45.4488 StartZ=0 EndX=-164.602 EndY=-45.8196 EndZ=0
    g2: LineSegment StartX=-164.602 StartY=-45.8196 StartZ=0 EndX=-163.366 EndY=-42.0154 EndZ=0
    g3: LineSegment StartX=-163.366 StartY=-42.0154 StartZ=0 EndX=-164.507 EndY=-41.6446 EndZ=0
  constraints (11):
    c: Coincident(g1,g0)
    c: Coincident(g2,g1)
    c: Coincident(g3,g2)
    c: Coincident(g3,g0)
    c: Parallel(g0,g2)
    c: Perpendicular(g3,g0)
    c: Perpendicular(g1,g0)
    c: Parallel(g0,g-3)
    c: Distance(g0) = 4
    c: Distance(g1) = 1.2
    c: Coincident(g0,g-3)
FEATURE [Part::Extrusion] Extrude056  label="Extrude scavo saldature rumble"
  Base = -> Sketch053
  Dir = (0,-1,2e-16)
  DirMode = 2
  FaceMakerClass = Part::FaceMakerBullseye
  FaceMakerMode = 3
  LengthFwd = 8.4
  LengthRev = 0
  Solid = true
  Symmetric = true
FEATURE [Sketcher::SketchObject] Sketch054  label="scavo saldature alimentatore connettore USB"
  ArcFitTolerance = 1e-06
  AttachmentSupport = -> [XZ_Plane]
  ExternalGeometry = -> [Sketch037]
  FullyConstrained = true
  MakeInternals = false
  MapMode = 5
  Placement = pos=(0,0,0) rot=(1,0,0;1.5708rad)
  sketch-geometry (4):
    g0: LineSegment StartX=-209.575 StartY=-80.4316 StartZ=0 EndX=-210.375 EndY=-80.4316 EndZ=0
    g1: LineSegment StartX=-210.375 StartY=-80.4316 StartZ=0 EndX=-210.375 EndY=-72.4316 EndZ=0
    g2: LineSegment StartX=-210.375 StartY=-72.4316 StartZ=0 EndX=-209.575 EndY=-72.4316 EndZ=0
    g3: LineSegment StartX=-209.575 StartY=-72.4316 StartZ=0 EndX=-209.575 EndY=-80.4316 EndZ=0
  constraints (11):
    c: Horizontal(g0)
    c: Coincident(g1,g0)
    c: Vertical(g1)
    c: Coincident(g2,g1)
    c: Horizontal(g2)
    c: Coincident(g3,g2)
    c: Coincident(g3,g0)
    c: Vertical(g3)
    c: DistanceX(g0,g0) = 0.8
    c: DistanceY(g3,g3) = 8
    c: Coincident(g0,g-4)
FEATURE [Part::Extrusion] Extrude057  label="Extrude scavo saldature alimentatore connettore USB"
  Base = -> Sketch054
  Dir = (0,-1,2e-16)
  DirMode = 2
  FaceMakerClass = Part::FaceMakerBullseye
  FaceMakerMode = 3
  LengthFwd = 11
  LengthRev = 0
  Solid = true
  Symmetric = true
FEATURE [Sketcher::SketchObject] Sketch055  label="buco interno per micro switch"
  ArcFitTolerance = 1e-06
  AttachmentSupport = -> [XZ_Plane]
  ExternalGeometry = -> [Sketch]
  FullyConstrained = true
  MakeInternals = false
  MapMode = 5
  Placement = pos=(0,0,0) rot=(1,0,0;1.5708rad)
  sketch-geometry (11):
    g0: LineSegment [constr] StartX=-194.483 StartY=34.2854 StartZ=0 EndX=-196.022 EndY=30.0568 EndZ=0
    g1: LineSegment [constr] StartX=-196.022 StartY=30.0568 StartZ=0 EndX=-197.561 EndY=25.8282 EndZ=0
    g2: LineSegment [constr] StartX=-196.022 StartY=30.0568 StartZ=0 EndX=-194.143 EndY=29.3727 EndZ=0
    g3: LineSegment [constr] StartX=-196.022 StartY=30.0568 StartZ=0 EndX=-197.902 EndY=30.7408 EndZ=0
    g4: LineSegment StartX=-196.362 StartY=34.9694 StartZ=0 EndX=-192.604 EndY=33.6014 EndZ=0
    g5: LineSegment StartX=-199.441 StartY=26.5122 StartZ=0 EndX=-195.682 EndY=25.1441 EndZ=0
    g6: LineSegment StartX=-192.604 StartY=33.6014 StartZ=0 EndX=-195.682 EndY=25.1441 EndZ=0
    g7: LineSegment StartX=-196.362 StartY=34.9694 StartZ=0 EndX=-199.441 EndY=26.5122 EndZ=0
    g8: GeomPoint [constr] X=-187.821 Y=29.2 Z=0
    g9: LineSegment [constr] StartX=-188.505 StartY=27.3206 StartZ=0 EndX=-196.022 EndY=30.0568 EndZ=0
    g10: LineSegment [constr] StartX=-187.821 StartY=29.2 StartZ=0 EndX=-188.505 EndY=27.3206 EndZ=0
  constraints (27):
    c: Coincident(g2,g0)
    c: Parallel(g0,g-3)
    c: Tangent(g1,g0) = -1.5708
    c: Perpendicular(g0,g2)
    c: Tangent(g2,g3)
    c: Distance(g0,g1) = 9
    c: Equal(g0,g1)
    c: Distance(g3,g2) = 4
    c: Equal(g2,g3)
    c: Parallel(g3,g4)
    c: Symmetric(g4,g4,g0)
    c: Parallel(g6,g1)
    c: Parallel(g7,g1)
    c: Symmetric(g6,g6,g2)
    c: Symmetric(g5,g5,g1)
    c: Symmetric(g7,g7,g3)
    c: Coincident(g7,g4)
    c: Coincident(g6,g4)
    c: Coincident(g5,g6)
    c: Symmetric(g-3,g-3,g8)
    c: Perpendicular(g-3,g9)
    c: Distance(g9) = 8
    c: Coincident(g3,g9)
    c: Coincident(g10,g8)
    c: Parallel(g10,g-3)
    c: Distance(g10) = 2
    c: Coincident(g10,g9)
FEATURE [Sketcher::SketchObject] Sketch056  label="buco esterno per micro switch"
  ArcFitTolerance = 1e-06
  AttachmentSupport = -> [XZ_Plane]
  ExternalGeometry = -> [Sketch055]
  FullyConstrained = true
  MakeInternals = false
  MapMode = 5
  Placement = pos=(0,0,0) rot=(1,0,0;1.5708rad)
  sketch-geometry (17):
    g0: GeomPoint [constr] X=-194.143 Y=29.3727 Z=0
    g1: GeomPoint [constr] X=-194.483 Y=34.2854 Z=0
    g2: GeomPoint [constr] X=-197.902 Y=30.7408 Z=0
    g3: GeomPoint [constr] X=-197.561 Y=25.8282 Z=0
    g4: GeomPoint [constr] X=-196.022 Y=30.0568 Z=0
    g5: LineSegment [constr] StartX=-194.483 StartY=34.2854 StartZ=0 EndX=-196.022 EndY=30.0568 EndZ=0
    g6: LineSegment [constr] StartX=-196.022 StartY=30.0568 StartZ=0 EndX=-197.561 EndY=25.8282 EndZ=0
    g7: LineSegment [constr] StartX=-197.902 StartY=30.7408 StartZ=0 EndX=-196.022 EndY=30.0568 EndZ=0
    g8: LineSegment [constr] StartX=-196.022 StartY=30.0568 StartZ=0 EndX=-194.143 EndY=29.3727 EndZ=0
    g9: LineSegment [constr] StartX=-195.338 StartY=31.9362 StartZ=0 EndX=-196.022 EndY=30.0568 EndZ=0
    g10: LineSegment [constr] StartX=-196.022 StartY=30.0568 StartZ=0 EndX=-196.706 EndY=28.1774 EndZ=0
    g11: LineSegment [constr] StartX=-196.022 StartY=30.0568 StartZ=0 EndX=-196.821 EndY=30.3475 EndZ=0
    g12: LineSegment [constr] StartX=-196.022 StartY=30.0568 StartZ=0 EndX=-195.223 EndY=29.7661 EndZ=0
    g13: LineSegment StartX=-194.539 StartY=31.6454 StartZ=0 EndX=-195.907 EndY=27.8867 EndZ=0
    g14: LineSegment StartX=-196.137 StartY=32.2269 StartZ=0 EndX=-197.505 EndY=28.4681 EndZ=0
    g15: LineSegment StartX=-196.137 StartY=32.2269 StartZ=0 EndX=-194.539 EndY=31.6454 EndZ=0
    g16: LineSegment StartX=-197.505 StartY=28.4681 StartZ=0 EndX=-195.907 EndY=27.8867 EndZ=0
  constraints (34):
    c: Symmetric(g-5,g-5,g1)
    c: Symmetric(g-5,g-6,g0)
    c: Symmetric(g-6,g-6,g3)
    c: Symmetric(g-5,g-6,g2)
    c: Coincident(g5,g1)
    c: Coincident(g5,g4)
    c: Coincident(g6,g4)
    c: Coincident(g6,g3)
    c: Equal(g5,g6)
    c: Coincident(g7,g2)
    c: Coincident(g7,g4)
    c: Coincident(g8,g4)
    c: Coincident(g8,g0)
    c: Equal(g7,g8)
    c: Coincident(g11,g9)
    c: Coincident(g12,g9)
    c: Tangent(g10,g9) = -1.5708
    c: Perpendicular(g11,g9)
    c: Parallel(g9,g-4)
    c: Equal(g9,g10)
    c: Parallel(g12,g11)
    c: Equal(g11,g12)
    c: Distance(g11,g12) = 1.7
    c: Distance(g9,g10) = 4
    c: Symmetric(g13,g13,g12)
    c: Parallel(g13,g9)
    c: Symmetric(g14,g14,g11)
    c: Symmetric(g15,g15,g9)
    c: Parallel(g15,g11)
    c: Symmetric(g16,g16,g10)
    c: Coincident(g16,g14)
    c: Coincident(g15,g14)
    c: Coincident(g13,g15)
    c: Coincident(g9,g4)
FEATURE [Sketcher::SketchObject] Sketch057  label="buco interno per SWITCH"
  ArcFitTolerance = 1e-06
  AttachmentSupport = -> [XZ_Plane]
  ExternalGeometry = -> [Sketch]
  FullyConstrained = true
  MakeInternals = false
  MapMode = 5
  Placement = pos=(0,0,0) rot=(1,0,0;1.5708rad)
  sketch-geometry (10):
    g0: GeomPoint [constr] X=-187.821 Y=29.2 Z=0
    g1: LineSegment [constr] StartX=-188.505 StartY=27.3206 StartZ=0 EndX=-193.203 EndY=29.0307 EndZ=0
    g2: LineSegment [constr] StartX=-190.809 StartY=35.6086 StartZ=0 EndX=-195.597 EndY=22.4529 EndZ=0
    g3: GeomPoint [constr] X=-193.203 Y=29.0307 Z=0
    g4: LineSegment [constr] StartX=-196.492 StartY=30.2278 StartZ=0 EndX=-189.914 EndY=27.8336 EndZ=0
    g5: LineSegment StartX=-194.098 StartY=36.8056 StartZ=0 EndX=-187.52 EndY=34.4115 EndZ=0
    g6: LineSegment StartX=-194.098 StartY=36.8056 StartZ=0 EndX=-198.886 EndY=23.6499 EndZ=0
    g7: LineSegment StartX=-187.52 StartY=34.4115 StartZ=0 EndX=-192.308 EndY=21.2558 EndZ=0
    g8: LineSegment StartX=-198.886 StartY=23.6499 StartZ=0 EndX=-192.308 EndY=21.2558 EndZ=0
    g9: LineSegment [constr] StartX=-187.821 StartY=29.2 StartZ=0 EndX=-188.505 EndY=27.3206 EndZ=0
  constraints (23):
    c: Symmetric(g-3,g-3,g0)
    c: Perpendicular(g1,g-3)
    c: Parallel(g2,g-3)
    c: Symmetric(g2,g2,g3)
    c: Perpendicular(g2,g4)
    c: Symmetric(g4,g4,g3)
    c: Distance(g2) = 14
    c: Distance(g4) = 7
    c: Distance(g1) = 5
    c: Parallel(g5,g4)
    c: Parallel(g7,g2)
    c: Symmetric(g5,g5,g2)
    c: Symmetric(g6,g6,g4)
    c: Symmetric(g7,g7,g4)
    c: Symmetric(g8,g8,g2)
    c: Coincident(g6,g5)
    c: Coincident(g7,g5)
    c: Coincident(g8,g7)
    c: Coincident(g3,g1)
    c: Coincident(g9,g0)
    c: Parallel(g9,g-3)
    c: Distance(g9) = 2
    c: Coincident(g1,g9)
FEATURE [Sketcher::SketchObject] Sketch058  label="buco esterno per SWITCH"
  ArcFitTolerance = 1e-06
  AttachmentSupport = -> [XZ_Plane]
  ExternalGeometry = -> [Sketch057]
  FullyConstrained = true
  MakeInternals = false
  MapMode = 5
  Placement = pos=(0,0,0) rot=(1,0,0;1.5708rad)
  sketch-geometry (12):
    g0: GeomPoint [constr] X=-190.809 Y=35.6086 Z=0
    g1: GeomPoint [constr] X=-196.492 Y=30.2278 Z=0
    g2: GeomPoint [constr] X=-189.914 Y=27.8336 Z=0
    g3: GeomPoint [constr] X=-195.597 Y=22.4529 Z=0
    g4: GeomPoint [constr] X=-193.203 Y=29.0307 Z=0
    g5: LineSegment [constr] StartX=-192.006 StartY=32.3196 StartZ=0 EndX=-194.4 EndY=25.7418 EndZ=0
    g6: GeomPoint [constr] X=-193.203 Y=29.0307 Z=0
    g7: LineSegment [constr] StartX=-195.082 StartY=29.7148 StartZ=0 EndX=-191.324 EndY=28.3467 EndZ=0
    g8: LineSegment StartX=-193.885 StartY=33.0037 StartZ=0 EndX=-190.127 EndY=31.6356 EndZ=0
    g9: LineSegment StartX=-190.127 StartY=31.6356 StartZ=0 EndX=-192.521 EndY=25.0578 EndZ=0
    g10: LineSegment StartX=-196.28 StartY=26.4258 StartZ=0 EndX=-192.521 EndY=25.0578 EndZ=0
    g11: LineSegment StartX=-193.885 StartY=33.0037 StartZ=0 EndX=-196.28 EndY=26.4258 EndZ=0
  constraints (21):
    c: Symmetric(g-6,g-6,g3)
    c: Symmetric(g-4,g-6,g2)
    c: Symmetric(g-5,g-4,g0)
    c: Symmetric(g-5,g-6,g1)
    c: Symmetric(g1,g2,g4)
    c: Parallel(g5,g-4)
    c: Symmetric(g5,g5,g6)
    c: Perpendicular(g7,g5)
    c: Symmetric(g7,g7,g6)
    c: Distance(g5) = 7
    c: Distance(g7) = 4
    c: Parallel(g8,g7)
    c: Parallel(g11,g5)
    c: Symmetric(g8,g8,g5)
    c: Symmetric(g9,g9,g7)
    c: Symmetric(g10,g10,g5)
    c: Symmetric(g11,g11,g7)
    c: Coincident(g11,g8)
    c: Coincident(g9,g8)
    c: Coincident(g9,g10)
    c: Coincident(g6,g4)
FEATURE [Part::Extrusion] Extrude060  label="Extrude buco interno per SWITCH destro"
  Base = -> Sketch057
  Dir = (0,-1,2e-16)
  DirMode = 2
  FaceMakerClass = Part::FaceMakerBullseye
  FaceMakerMode = 3
  LengthFwd = 13.2
  LengthRev = 0
  Placement = pos=(0,2.6,0) rot=(0,0,1;0rad)
  Solid = true
  Symmetric = false
FEATURE [Part::Extrusion] Extrude061  label="Extrude buco esterno per SWITCH destro"
  Base = -> Sketch058
  Dir = (0,-1,2e-16)
  DirMode = 2
  FaceMakerClass = Part::FaceMakerBullseye
  FaceMakerMode = 3
  LengthFwd = 2
  LengthRev = 0
  Placement = pos=(0,-10.6,0) rot=(0,0,1;0rad)
  Solid = true
  Symmetric = false
FEATURE [Sketcher::SketchObject] Sketch059  label="buco per spazio introduzione SWITCH"
  ArcFitTolerance = 1e-06
  AttachmentSupport = -> [XZ_Plane]
  ExternalGeometry = -> [Sketch057,Sketch010]
  FullyConstrained = true
  MakeInternals = false
  MapMode = 5
  Placement = pos=(0,0,0) rot=(1,0,0;1.5708rad)
  sketch-geometry (8):
    g0: LineSegment [constr] StartX=-201.368 StartY=36.3521 StartZ=0 EndX=-195.094 EndY=34.0687 EndZ=0
    g1: LineSegment [constr] StartX=-194.098 StartY=36.8056 StartZ=0 EndX=-195.094 EndY=34.0687 EndZ=0
    g2: LineSegment StartX=-198.658 StartY=24.2771 StartZ=0 EndX=-199.654 EndY=21.5401 EndZ=0
    g3: LineSegment StartX=-199.654 StartY=21.5401 StartZ=0 EndX=-181.196 EndY=14.822 EndZ=0
    g4: LineSegment StartX=-181.196 StartY=14.822 StartZ=0 EndX=-180.2 EndY=17.559 EndZ=0
    g5: LineSegment StartX=-180.2 StartY=17.559 StartZ=0 EndX=-198.658 EndY=24.2771 EndZ=0
    g6: LineSegment [constr] StartX=-204.932 StartY=26.5605 StartZ=0 EndX=-198.658 EndY=24.2771 EndZ=0
    g7: LineSegment [constr] StartX=-198.658 StartY=24.2771 StartZ=0 EndX=-199.654 EndY=21.5401 EndZ=0
  constraints (20):
    c: Parallel(g1,g-3)
    c: Parallel(g0,g-4)
    c: Coincident(g0,g-4)
    c: Coincident(g1,g-3)
    c: Coincident(g0,g1)
    c: Coincident(g3,g2)
    c: Coincident(g4,g3)
    c: Coincident(g5,g4)
    c: Coincident(g5,g2)
    c: Parallel(g5,g-5)
    c: Parallel(g3,g-5)
    c: Parallel(g4,g-6)
    c: DistanceX(g-6,g4) = 0
    c: Coincident(g6,g-5)
    c: Equal(g6,g0)
    c: Coincident(g7,g6)
    c: Equal(g7,g1)
    c: Tangent(g7,g-3)
    c: Coincident(g2,g6)
    c: Coincident(g2,g7)
FEATURE [Part::Extrusion] Extrude062  label="Extrude buco per spazio introduzione SWITCH"
  Base = -> Sketch059
  Dir = (0,-1,2e-16)
  DirMode = 2
  FaceMakerClass = Part::FaceMakerBullseye
  FaceMakerMode = 3
  LengthFwd = 13.2
  LengthRev = 0
  Solid = true
  Symmetric = true
FEATURE [Part::Extrusion] Extrude063  label="Extrude buco interno per SWITCH sinistro"
  Base = -> Sketch057
  Dir = (0,-1,2e-16)
  DirMode = 2
  FaceMakerClass = Part::FaceMakerBullseye
  FaceMakerMode = 3
  LengthFwd = 13.2
  LengthRev = 0
  Placement = pos=(0,10.6,0) rot=(0,0,1;0rad)
  Solid = true
  Symmetric = false
FEATURE [Part::Extrusion] Extrude064  label="Extrude buco esterno per SWITCH sinistro"
  Base = -> Sketch058
  Dir = (0,-1,2e-16)
  DirMode = 2
  FaceMakerClass = Part::FaceMakerBullseye
  FaceMakerMode = 3
  LengthFwd = 2
  LengthRev = 0
  Placement = pos=(0,12.6,0) rot=(0,0,1;0rad)
  Solid = true
  Symmetric = false
FEATURE [Sketcher::SketchObject] Sketch061  label="struttura esterna blocco switch"
  ArcFitTolerance = 1e-06
  AttachmentSupport = -> [XZ_Plane003]
  FullyConstrained = true
  MakeInternals = false
  MapMode = 5
  Placement = pos=(0,0,0) rot=(1,0,0;1.5708rad)
  sketch-geometry (5):
    g0: LineSegment StartX=-1 StartY=-5.1 StartZ=0 EndX=1 EndY=-5.1 EndZ=0
    g1: LineSegment StartX=1 StartY=-5.1 StartZ=0 EndX=1 EndY=5.1 EndZ=0
    g2: LineSegment StartX=1 StartY=5.1 StartZ=0 EndX=-1 EndY=5.1 EndZ=0
    g3: LineSegment StartX=-1 StartY=5.1 StartZ=0 EndX=-1 EndY=-5.1 EndZ=0
    g4: GeomPoint [constr] X=0 Y=0 Z=0
  constraints (12):
    c: Coincident(g0,g1)
    c: Coincident(g1,g2)
    c: Coincident(g2,g3)
    c: Coincident(g3,g0)
    c: Horizontal(g0)
    c: Horizontal(g2)
    c: Vertical(g1)
    c: Vertical(g3)
    c: Symmetric(g2,g0,g4)
    c: Distance(g1,g3) = 2
    c: Distance(g0,g2) = 10.2
    c: Coincident(g4,g-1)
FEATURE [Sketcher::SketchObject] Sketch062  label="struttura interna blocco switch"
  ArcFitTolerance = 1e-06
  AttachmentSupport = -> [XZ_Plane003]
  ExternalGeometry = -> [Sketch061]
  FullyConstrained = true
  MakeInternals = false
  MapMode = 5
  Placement = pos=(0,0,0) rot=(1,0,0;1.5708rad)
  sketch-geometry (5):
    g0: LineSegment StartX=-1 StartY=3.1 StartZ=0 EndX=-1 EndY=-3.1 EndZ=0
    g1: LineSegment StartX=-1 StartY=-3.1 StartZ=0 EndX=1 EndY=-3.1 EndZ=0
    g2: LineSegment StartX=1 StartY=-3.1 StartZ=0 EndX=1 EndY=3.1 EndZ=0
    g3: LineSegment StartX=1 StartY=3.1 StartZ=0 EndX=-1 EndY=3.1 EndZ=0
    g4: GeomPoint [constr] X=0 Y=0 Z=0
  constraints (12):
    c: Coincident(g0,g1)
    c: Coincident(g1,g2)
    c: Coincident(g2,g3)
    c: Coincident(g3,g0)
    c: Vertical(g0)
    c: Vertical(g2)
    c: Horizontal(g1)
    c: Horizontal(g3)
    c: Symmetric(g2,g0,g4)
    c: Coincident(g4,g-1)
    c: Distance(g0) = 6.2
    c: Equal(g3,g-3)
FEATURE [Sketcher::SketchObject] Sketch063  label="blocchi tra switch"
  ArcFitTolerance = 1e-06
  AttachmentSupport = -> [XZ_Plane003]
  ExternalGeometry = -> [Sketch061,Sketch062]
  FullyConstrained = true
  MakeInternals = false
  MapMode = 5
  Placement = pos=(0,0,0) rot=(1,0,0;1.5708rad)
  sketch-geometry (8):
    g0: LineSegment StartX=-3 StartY=5.1 StartZ=0 EndX=-1 EndY=5.1 EndZ=0
    g1: LineSegment StartX=-1 StartY=5.1 StartZ=0 EndX=-1 EndY=3.1 EndZ=0
    g2: LineSegment StartX=-1 StartY=3.1 StartZ=0 EndX=-3 EndY=3.1 EndZ=0
    g3: LineSegment StartX=-3 StartY=3.1 StartZ=0 EndX=-3 EndY=5.1 EndZ=0
    g4: LineSegment StartX=-3 StartY=-3.1 StartZ=0 EndX=-1 EndY=-3.1 EndZ=0
    g5: LineSegment StartX=-1 StartY=-3.1 StartZ=0 EndX=-1 EndY=-5.1 EndZ=0
    g6: LineSegment StartX=-1 StartY=-5.1 StartZ=0 EndX=-3 EndY=-5.1 EndZ=0
    g7: LineSegment StartX=-3 StartY=-5.1 StartZ=0 EndX=-3 EndY=-3.1 EndZ=0
  constraints (20):
    c: Horizontal(g0)
    c: Coincident(g1,g0)
    c: Coincident(g2,g1)
    c: Horizontal(g2)
    c: Coincident(g3,g2)
    c: Coincident(g3,g0)
    c: Vertical(g3)
    c: Horizontal(g4)
    c: Coincident(g5,g4)
    c: Coincident(g6,g5)
    c: Horizontal(g6)
    c: Coincident(g7,g6)
    c: Coincident(g7,g4)
    c: Vertical(g7)
    c: Coincident(g0,g-4)
    c: Coincident(g1,g-5)
    c: Coincident(g4,g-6)
    c: Coincident(g5,g-7)
    c: Distance(g0) = 2
    c: Distance(g4) = 2
FEATURE [Sketcher::SketchObject] Sketch066  label="piano per rampino"
  ArcFitTolerance = 1e-06
  AttachmentSupport = -> [XZ_Plane002]
  ExternalGeometry = -> [Sketch045]
  FullyConstrained = true
  MakeInternals = false
  MapMode = 5
  Placement = pos=(0,0,0) rot=(1,0,0;1.5708rad)
  sketch-geometry (4):
    g0: LineSegment StartX=5.4 StartY=5.1 StartZ=0 EndX=5.4 EndY=3.9 EndZ=0
    g1: LineSegment StartX=5.4 StartY=3.9 StartZ=0 EndX=7 EndY=3.9 EndZ=0
    g2: LineSegment StartX=7 StartY=3.9 StartZ=0 EndX=7 EndY=5.1 EndZ=0
    g3: LineSegment StartX=7 StartY=5.1 StartZ=0 EndX=5.4 EndY=5.1 EndZ=0
  constraints (11):
    c: Coincident(g0,g1)
    c: Coincident(g1,g2)
    c: Coincident(g2,g3)
    c: Coincident(g3,g0)
    c: Vertical(g0)
    c: Vertical(g2)
    c: Horizontal(g1)
    c: Horizontal(g3)
    c: Distance(g0,g2) = 1.6
    c: Distance(g1,g3) = 1.2
    c: Coincident(g2,g-3)
FEATURE [Sketcher::SketchObject] Sketch064  label="rampini_per_serraggio_struttura"
  ArcFitTolerance = 1e-06
  AttachmentSupport = -> [XZ_Plane002]
  ExternalGeometry = -> [Sketch066,Sketch045]
  FullyConstrained = true
  MakeInternals = false
  MapMode = 5
  Placement = pos=(0,0,0) rot=(1,0,0;1.5708rad)
  sketch-geometry (7):
    g0: LineSegment StartX=7 StartY=5.1 StartZ=0 EndX=7 EndY=3.9 EndZ=0
    g1: LineSegment StartX=7 StartY=3.9 StartZ=0 EndX=9 EndY=3.9 EndZ=0
    g2: LineSegment StartX=7 StartY=5.1 StartZ=0 EndX=7 EndY=5.1 EndZ=0
    g3: LineSegment StartX=7 StartY=5.1 StartZ=0 EndX=7 EndY=7.5 EndZ=0
    g4: LineSegment StartX=9 StartY=5.1 StartZ=0 EndX=9 EndY=3.9 EndZ=0
    g5: LineSegment StartX=7 StartY=7.5 StartZ=0 EndX=9 EndY=7.5 EndZ=0
    g6: LineSegment StartX=9 StartY=7.5 StartZ=0 EndX=9 EndY=5.1 EndZ=0
  constraints (20):
    c: Vertical(g0)
    c: Coincident(g1,g0)
    c: Horizontal(g1)
    c: Coincident(g2,g0)
    c: Horizontal(g2)
    c: Coincident(g3,g2)
    c: Vertical(g3)
    c: Coincident(g5,g3)
    c: Coincident(g4,g6)
    c: Coincident(g4,g1)
    c: Vertical(g4)
    c: Coincident(g0,g-3)
    c: DistanceY(g-4,g3) = 2.4
    c: DistanceX(g1,g1) = 2
    c: DistanceY(g2,g6) = 0
    c: DistanceX(g2,g2) = 0
    c: DistanceY(g0,g0) = 1.2
    c: Coincident(g5,g6)
    c: Horizontal(g5)
    c: Vertical(g6)
FEATURE [Sketcher::SketchObject] Sketch067  label="perno per blocco switch"
  ArcFitTolerance = 1e-06
  AttachmentSupport = -> [XZ_Plane]
  ExternalGeometry = -> [Sketch,Sketch010]
  FullyConstrained = true
  MakeInternals = false
  MapMode = 5
  Placement = pos=(0,0,0) rot=(1,0,0;1.5708rad)
  sketch-geometry (14):
    g0: LineSegment StartX=-191.073 StartY=24.9429 StartZ=0 EndX=-185.81 EndY=23.0276 EndZ=0
    g1: LineSegment StartX=-183.76 StartY=23.9839 StartZ=0 EndX=-182.392 EndY=27.7427 EndZ=0
    g2: LineSegment StartX=-183.348 StartY=29.7934 StartZ=0 EndX=-188.61 EndY=31.7087 EndZ=0
    g3: LineSegment StartX=-188.61 StartY=31.7087 StartZ=0 EndX=-191.073 EndY=24.9429 EndZ=0
    g4: GeomPoint [constr] X=-186.459 Y=27.0946 Z=0
    g5: LineSegment StartX=-189.022 StartY=25.8992 StartZ=0 EndX=-185.263 EndY=24.5311 EndZ=0
    g6: LineSegment StartX=-185.263 StartY=24.5311 StartZ=0 EndX=-183.895 EndY=28.2899 EndZ=0
    g7: LineSegment StartX=-183.895 StartY=28.2899 StartZ=0 EndX=-187.654 EndY=29.658 EndZ=0
    g8: LineSegment StartX=-187.654 StartY=29.658 StartZ=0 EndX=-189.022 EndY=25.8992 EndZ=0
    g9: GeomPoint [constr] X=-186.459 Y=27.0946 Z=0
    g10: ArcOfCircle CenterX=-185.263 CenterY=24.5311 CenterZ=0 NormalX=0 NormalY=0 NormalZ=1 AngleXU=0 Radius=1.6 StartAngle=4.36332 EndAngle=5.93412
    g11: GeomPoint [constr] X=-184.307 Y=22.4804 Z=0
    g12: ArcOfCircle CenterX=-183.895 CenterY=28.2899 CenterZ=0 NormalX=0 NormalY=0 NormalZ=1 AngleXU=0 Radius=1.6 StartAngle=5.93412 EndAngle=7.50492
    g13: GeomPoint [constr] X=-181.844 Y=29.2462 Z=0
  constraints (30):
    c: Coincident(g2,g3)
    c: Coincident(g3,g0)
    c: Symmetric(g13,g0,g4)
    c: Distance(g11,g3) = 7.2
    c: Distance(g0,g2) = 7.2
    c: Parallel(g3,g1)
    c: Parallel(g2,g0)
    c: Perpendicular(g2,g3)
    c: Coincident(g5,g6)
    c: Coincident(g6,g7)
    c: Coincident(g7,g8)
    c: Coincident(g8,g5)
    c: Symmetric(g7,g5,g9)
    c: Distance(g6,g8) = 4
    c: Distance(g5,g7) = 4
    c: Coincident(g9,g4)
    c: Parallel(g8,g6)
    c: Parallel(g7,g5)
    c: Perpendicular(g7,g8)
    c: Tangent(g8,g-3)
    c: Tangent(g2,g-4)
    c: PointOnObject(g11,g1)
    c: PointOnObject(g11,g0)
    c: Tangent(g1,g10) = -1.5708
    c: Tangent(g0,g10) = -1.5708
    c: PointOnObject(g13,g1)
    c: Tangent(g1,g12) = -1.5708
    c: Tangent(g2,g12) = -1.5708
    c: Equal(g10,g12)
    c: Coincident(g10,g5)
FEATURE [Part::Extrusion] Extrude072  label="Extrude perno per blocco switch"
  Base = -> Sketch067
  Dir = (0,-1,2e-16)
  DirMode = 2
  FaceMakerClass = Part::FaceMakerBullseye
  FaceMakerMode = 3
  LengthFwd = 25.2
  LengthRev = 0
  Solid = true
  Symmetric = true
FEATURE [Part::MultiFuse] Fusion
  Refine = true
  Shapes = -> [Extrude,Sweep,Extrude007,Extrude011,Extrude005,Extrude012,Extrude013,Extrude016,Extrude031,Extrude039,Extrude045,Extrude072]
FEATURE [Part::Cut] Cut
  Base = -> Fusion
  Refine = true
  Tool = -> Extrude001
FEATURE [Part::Cut] Cut001
  Base = -> Cut
  Refine = true
  Tool = -> Extrude004
FEATURE [Part::Cut] Cut002
  Base = -> Cut001
  Refine = true
  Tool = -> Extrude006
FEATURE [Part::Cut] Cut003
  Base = -> Cut002
  Refine = true
  Tool = -> Extrude008
FEATURE [Part::Cut] Cut004
  Base = -> Cut003
  Refine = true
  Tool = -> Extrude009
FEATURE [Part::Cut] Cut005
  Base = -> Cut004
  Refine = true
  Tool = -> Extrude010
FEATURE [Part::Cut] Cut006
  Base = -> Cut005
  Refine = true
  Tool = -> Extrude014
FEATURE [Part::Cut] Cut007
  Base = -> Cut006
  Refine = true
  Tool = -> Extrude015
FEATURE [Part::Cut] Cut008
  Base = -> Cut007
  Refine = true
  Tool = -> Extrude018
FEATURE [Part::Cut] Cut009
  Base = -> Cut008
  Refine = true
  Tool = -> Extrude019
FEATURE [Part::Cut] Cut010
  Base = -> Cut009
  Refine = true
  Tool = -> Extrude020
FEATURE [Part::Cut] Cut011
  Base = -> Cut010
  Refine = true
  Tool = -> Extrude021
FEATURE [Part::Cut] Cut012
  Base = -> Cut011
  Refine = true
  Tool = -> Extrude022
FEATURE [Part::Cut] Cut013
  Base = -> Cut012
  Refine = true
  Tool = -> Extrude023
FEATURE [Part::Cut] Cut014
  Base = -> Cut013
  Refine = true
  Tool = -> Extrude032
FEATURE [Part::Cut] Cut015
  Base = -> Cut014
  Refine = true
  Tool = -> Extrude033
FEATURE [Part::Cut] Cut016
  Base = -> Cut015
  Refine = true
  Tool = -> Extrude034
FEATURE [Part::Cut] Cut017
  Base = -> Cut016
  Refine = true
  Tool = -> Extrude035
FEATURE [Part::Cut] Cut018
  Base = -> Cut017
  Refine = true
  Tool = -> Extrude036
FEATURE [Part::Cut] Cut019
  Base = -> Cut018
  Refine = true
  Tool = -> Extrude037
FEATURE [Part::Cut] Cut020
  Base = -> Cut019
  Refine = true
  Tool = -> Extrude030
FEATURE [Part::Cut] Cut022
  Base = -> Cut020
  Refine = true
  Tool = -> Extrude038
FEATURE [Part::Cut] Cut023
  Base = -> Cut022
  Refine = true
  Tool = -> Extrude041
FEATURE [Part::Cut] Cut024
  Base = -> Cut023
  Refine = true
  Tool = -> Extrude040
FEATURE [Part::Cut] Cut025
  Base = -> Cut024
  Refine = true
  Tool = -> Extrude042
FEATURE [Part::Cut] Cut026
  Base = -> Cut025
  Refine = true
  Tool = -> Extrude043
FEATURE [Part::Cut] Cut027
  Base = -> Cut026
  Refine = true
  Tool = -> Extrude044
FEATURE [Part::Cut] Cut028
  Base = -> Cut027
  Refine = true
  Tool = -> Extrude046
FEATURE [Part::Cut] Cut029
  Base = -> Cut028
  Refine = true
  Tool = -> Extrude047
FEATURE [Part::Cut] Cut033
  Base = -> Cut029
  Refine = true
  Tool = -> Extrude055
FEATURE [Part::Cut] Cut034
  Base = -> Cut033
  Refine = true
  Tool = -> Extrude056
FEATURE [Part::Cut] Cut035
  Base = -> Cut034
  Refine = true
  Tool = -> Extrude057
FEATURE [Part::Cut] Cut037
  Base = -> Cut035
  Refine = true
  Tool = -> Extrude060
FEATURE [Part::Cut] Cut038
  Base = -> Cut037
  Refine = true
  Tool = -> Extrude061
FEATURE [Part::Cut] Cut039
  Base = -> Cut038
  Refine = true
  Tool = -> Extrude063
FEATURE [Part::Cut] Cut040
  Base = -> Cut039
  Refine = true
  Tool = -> Extrude064
FEATURE [Part::Cut] Cut041
  Base = -> Cut040
  Refine = true
  Tool = -> Extrude062
FEATURE [Sketcher::SketchObject] Sketch068  label="base con smusso sopra neopixel"
  ArcFitTolerance = 1e-06
  AttachmentSupport = -> [YZ_Plane002]
  FullyConstrained = true
  MakeInternals = false
  MapMode = 5
  Placement = pos=(0,0,0) rot=(0.57735,0.57735,0.57735;2.0944rad)
  sketch-geometry (5):
    g0: LineSegment StartX=-9.5 StartY=-6.1 StartZ=0 EndX=9.5 EndY=-6.1 EndZ=0
    g1: LineSegment StartX=9.5 StartY=-6.1 StartZ=0 EndX=9.5 EndY=6.1 EndZ=0
    g2: LineSegment StartX=9.5 StartY=6.1 StartZ=0 EndX=-9.5 EndY=6.1 EndZ=0
    g3: LineSegment StartX=-9.5 StartY=6.1 StartZ=0 EndX=-9.5 EndY=-6.1 EndZ=0
    g4: GeomPoint [constr] X=0 Y=0 Z=0
  constraints (12):
    c: Coincident(g0,g1)
    c: Coincident(g1,g2)
    c: Coincident(g2,g3)
    c: Coincident(g3,g0)
    c: Horizontal(g0)
    c: Horizontal(g2)
    c: Vertical(g1)
    c: Vertical(g3)
    c: Symmetric(g2,g0,g4)
    c: Distance(g1,g3) = 19
    c: Distance(g0,g2) = 12.2
    c: Coincident(g4,g-1)
FEATURE [Sketcher::SketchObject] Sketch069  label="cilindro minore"
  ArcFitTolerance = 1e-06
  AttachmentSupport = -> [XZ_Plane004]
  FullyConstrained = true
  MakeInternals = false
  MapMode = 5
  Placement = pos=(0,0,0) rot=(1,0,0;1.5708rad)
  sketch-geometry (1):
    g0: Circle CenterX=0 CenterY=0 CenterZ=0 NormalX=0 NormalY=0 NormalZ=1 AngleXU=0 Radius=5.8
  constraints (2):
    c: Diameter(g0) = 11.6
    c: Coincident(g0,g-1)
FEATURE [Sketcher::SketchObject] Sketch070  label="cilindro maggiore"
  ArcFitTolerance = 1e-06
  AttachmentSupport = -> [XZ_Plane004]
  ExternalGeometry = -> [Sketch069]
  FullyConstrained = true
  MakeInternals = false
  MapMode = 5
  Placement = pos=(0,0,0) rot=(1,0,0;1.5708rad)
  sketch-geometry (1):
    g0: Circle CenterX=0 CenterY=0 CenterZ=0 NormalX=0 NormalY=0 NormalZ=1 AngleXU=0 Radius=6.5
  constraints (2):
    c: Coincident(g0,g-1)
    c: Diameter(g0) = 13
FEATURE [Sketcher::SketchObject] Sketch071  label="buco interno"
  ArcFitTolerance = 1e-06
  AttachmentSupport = -> [XZ_Plane004]
  ExternalGeometry = -> [Sketch069]
  FullyConstrained = true
  MakeInternals = false
  MapMode = 5
  Placement = pos=(0,0,0) rot=(1,0,0;1.5708rad)
  sketch-geometry (1):
    g0: Circle CenterX=0 CenterY=0 CenterZ=0 NormalX=0 NormalY=0 NormalZ=1 AngleXU=0 Radius=5
  constraints (2):
    c: Coincident(g0,g-1)
    c: Diameter(g0) = 10
FEATURE [PartDesign::Pad] Pad
  Direction = (0,-1,2e-16)
  Length = 1.2
  Length2 = 10
  Placement = pos=(0,0,0) rot=(1,0,0;1.5708rad)
  Profile = -> Sketch070
  ReferenceAxis = -> Sketch070 [N_Axis]
  Refine = true
  Suppressed = false
  Type = 0
FEATURE [PartDesign::Pad] Pad001
  BaseFeature = -> Pad
  Direction = (0,-1,2e-16)
  Length = 5.6
  Length2 = 10
  Placement = pos=(0,0,0) rot=(1,0,0;1.5708rad)
  Profile = -> Sketch069
  ReferenceAxis = -> Sketch069 [N_Axis]
  Refine = true
  Suppressed = false
  Type = 0
FEATURE [PartDesign::Pocket] Pocket
  BaseFeature = -> Pad001
  Direction = (0,1,-2e-16)
  Length = 7
  Length2 = 5
  Midplane = true
  Placement = pos=(0,0,0) rot=(1,0,0;1.5708rad)
  Profile = -> Sketch071
  ReferenceAxis = -> Sketch071 [N_Axis]
  Refine = true
  Suppressed = false
  Type = 0
FEATURE [PartDesign::Fillet] Fillet
  Base = -> Pocket [Face7]
  BaseFeature = -> Pocket
  Placement = pos=(0,0,0) rot=(1,0,0;1.5708rad)
  Radius = 1
  Refine = true
  SupportTransform = false
  Suppressed = false
  UseAllEdges = false
FEATURE [PartDesign::Body] Body004  label="pulsanti lato sinistro"
  AllowCompound = false
  Group = -> [Sketch069,Sketch070,Sketch071,Pad,Pad001,Pocket,Fillet]
  Origin = -> Origin004
  Tip = -> Fillet
FEATURE [Sketcher::SketchObject] Sketch072  label="buco per saldature e diodo driver solenoide"
  ArcFitTolerance = 1e-06
  AttachmentSupport = -> [XZ_Plane]
  ExternalGeometry = -> [Sketch038]
  FullyConstrained = true
  MakeInternals = false
  MapMode = 5
  Placement = pos=(0,0,0) rot=(1,0,0;1.5708rad)
  sketch-geometry (4):
    g0: LineSegment StartX=-212.269 StartY=-43.9083 StartZ=0 EndX=-207.197 EndY=-33.0326 EndZ=0
    g1: LineSegment StartX=-207.197 StartY=-33.0326 StartZ=0 EndX=-207.56 EndY=-32.8635 EndZ=0
    g2: LineSegment StartX=-207.56 StartY=-32.8635 StartZ=0 EndX=-212.631 EndY=-43.7392 EndZ=0
    g3: LineSegment StartX=-212.631 StartY=-43.7392 StartZ=0 EndX=-212.269 EndY=-43.9083 EndZ=0
  constraints (11):
    c: Coincident(g1,g0)
    c: Coincident(g2,g1)
    c: Coincident(g3,g2)
    c: Coincident(g3,g0)
    c: Parallel(g-3,g0)
    c: Parallel(g0,g2)
    c: Perpendicular(g0,g3)
    c: Perpendicular(g1,g0)
    c: Distance(g3) = 0.4
    c: Distance(g2) = 12
    c: Coincident(g0,g-3)
FEATURE [Part::Extrusion] Extrude074  label="Extrude buco per saldature e diodo driver solenoide"
  Base = -> Sketch072
  Dir = (0,-1,2e-16)
  DirMode = 2
  FaceMakerClass = Part::FaceMakerBullseye
  FaceMakerMode = 3
  LengthFwd = 14.6
  LengthRev = 0
  Solid = true
  Symmetric = true
FEATURE [Part::Cut] Cut042
  Base = -> Cut041
  Refine = true
  Tool = -> Extrude074
FEATURE [Sketcher::SketchObject] Sketch073  label="fori slargati blocco solenoide"
  ArcFitTolerance = 1e-06
  AttachmentSupport = -> [XY_Plane]
  ExternalGeometry = -> [Sketch030]
  FullyConstrained = true
  MakeInternals = false
  MapMode = 5
  sketch-geometry (2):
    g0: Circle CenterX=-152.209 CenterY=6.95 CenterZ=0 NormalX=0 NormalY=0 NormalZ=1 AngleXU=0 Radius=3.7
    g1: Circle CenterX=-130.41 CenterY=-6.95 CenterZ=0 NormalX=0 NormalY=0 NormalZ=1 AngleXU=0 Radius=3.7
  constraints (4):
    c: Diameter(g0) = 7.4
    c: Coincident(g0,g-3)
    c: Diameter(g1) = 7.4
    c: Coincident(g1,g-4)
FEATURE [Part::Extrusion] Extrude075  label="Extrude fori slargati blocco solenoide"
  Base = -> Sketch073
  Dir = (0,0,1)
  DirMode = 2
  FaceMakerClass = Part::FaceMakerBullseye
  FaceMakerMode = 3
  LengthFwd = 1.5
  LengthRev = 0
  Placement = pos=(0,0,36.4) rot=(0,0,1;0rad)
  Solid = true
  Symmetric = false
FEATURE [Part::Cut] Cut043
  Base = -> Cut042
  Refine = true
  Tool = -> Extrude075
FEATURE [Sketcher::SketchObject] Sketch074  label="lato sx pistola"
  ArcFitTolerance = 1e-06
  AttachmentSupport = -> [XZ_Plane]
  ExternalGeometry = -> [Sketch016,Sketch,Sketch058]
  FullyConstrained = true
  MakeInternals = false
  MapMode = 5
  Placement = pos=(0,0,0) rot=(1,0,0;1.5708rad)
  sketch-geometry (37):
    g0: LineSegment StartX=-82.8 StartY=3.2 StartZ=0 EndX=0 EndY=3.2 EndZ=0
    g1: LineSegment StartX=-82.8 StartY=3.2 StartZ=0 EndX=-82.8 EndY=6.2 EndZ=0
    g2: LineSegment [constr] StartX=-107.6 StartY=18 StartZ=0 EndX=-107.6 EndY=20 EndZ=0
    g3: LineSegment [constr] StartX=-132.428 StartY=18 StartZ=0 EndX=-132.428 EndY=20 EndZ=0
    g4: LineSegment StartX=-132.428 StartY=20 StartZ=0 EndX=-107.6 EndY=20 EndZ=0
    g5: ArcOfCircle CenterX=-107.6 CenterY=4 CenterZ=0 NormalX=0 NormalY=0 NormalZ=1 AngleXU=0 Radius=16 StartAngle=0.137937 EndAngle=1.5708
    g6: LineSegment StartX=-82.8 StartY=6.2 StartZ=0 EndX=-91.752 EndY=6.2 EndZ=0
    g7: LineSegment [constr] StartX=-145.743 StartY=8.32624 StartZ=0 EndX=-147.645 EndY=8.94427 EndZ=0
    g8: ArcOfCircle CenterX=-132.428 CenterY=4 CenterZ=0 NormalX=0 NormalY=0 NormalZ=1 AngleXU=0 Radius=16 StartAngle=1.5708 EndAngle=2.82743
    g9: LineSegment StartX=-215.932 StartY=-80.4316 StartZ=0 EndX=-176.685 EndY=-80.4316 EndZ=0
    g10: LineSegment StartX=-147.645 StartY=8.94427 StartZ=0 EndX=-176.685 EndY=-80.4316 EndZ=0
    g11: LineSegment [constr] StartX=-193.988 StartY=-2.33927 StartZ=0 EndX=-192.176 EndY=-3.18451 EndZ=0
    g12: LineSegment [constr] StartX=-217.232 StartY=-52.1862 StartZ=0 EndX=-215.42 EndY=-53.0314 EndZ=0
    g13: LineSegment StartX=-192.176 StartY=-3.18451 StartZ=0 EndX=-215.42 EndY=-53.0314 EndZ=0
    g14: ArcOfCircle CenterX=-184.801 CenterY=-67.3089 CenterZ=0 NormalX=0 NormalY=0 NormalZ=1 AngleXU=0 Radius=33.7833 StartAngle=2.70526 EndAngle=3.54053
    g15: ArcOfCircle CenterX=-207.583 CenterY=4 CenterZ=0 NormalX=0 NormalY=0 NormalZ=1 AngleXU=0 Radius=17 StartAngle=5.84685 EndAngle=7.56663
    g16: LineSegment StartX=-202.765 StartY=20.303 StartZ=0 EndX=-195.887 EndY=39.2 EndZ=0
    g17: LineSegment [constr] StartX=-193.885 StartY=33.0037 StartZ=0 EndX=-197.644 EndY=34.3718 EndZ=0
    g18: LineSegment StartX=-195.887 StartY=39.2 StartZ=0 EndX=0 EndY=39.2 EndZ=0
    g19: LineSegment StartX=0 StartY=3.2 StartZ=0 EndX=0 EndY=39.2 EndZ=0
    g20: LineSegment StartX=-189.939 StartY=31.5672 StartZ=0 EndX=-192.333 EndY=24.9893 EndZ=0
    g21: LineSegment StartX=-196.467 StartY=26.4942 StartZ=0 EndX=-194.073 EndY=33.0721 EndZ=0
    g22: Circle CenterX=-213.443 CenterY=-76.8316 CenterZ=0 NormalX=0 NormalY=0 NormalZ=1 AngleXU=0 Radius=1.8
    g23: Circle CenterX=-179.305 CenterY=-76.8316 CenterZ=0 NormalX=0 NormalY=0 NormalZ=1 AngleXU=0 Radius=1.8
    g24: Circle CenterX=-184.08 CenterY=34.8 CenterZ=0 NormalX=0 NormalY=0 NormalZ=1 AngleXU=0 Radius=1.8
    g25: Circle CenterX=-78.51 CenterY=34.8 CenterZ=0 NormalX=0 NormalY=0 NormalZ=1 AngleXU=0 Radius=1.8
    g26: Circle CenterX=-78.51 CenterY=7.6 CenterZ=0 NormalX=0 NormalY=0 NormalZ=1 AngleXU=0 Radius=1.8
    g27: Circle CenterX=-5.6 CenterY=34.8 CenterZ=0 NormalX=0 NormalY=0 NormalZ=1 AngleXU=0 Radius=1.8
    g28: Circle CenterX=-5.6 CenterY=7.6 CenterZ=0 NormalX=0 NormalY=0 NormalZ=1 AngleXU=0 Radius=1.8
    g29: LineSegment StartX=-190.127 StartY=31.6356 StartZ=0 EndX=-189.939 EndY=31.5672 EndZ=0
    g30: LineSegment StartX=-194.073 StartY=33.0721 StartZ=0 EndX=-193.885 EndY=33.0037 EndZ=0
    g31: LineSegment StartX=-193.885 StartY=33.0037 StartZ=0 EndX=-190.127 EndY=31.6356 EndZ=0
    g32: LineSegment StartX=-196.467 StartY=26.4942 StartZ=0 EndX=-192.333 EndY=24.9893 EndZ=0
    g33: Circle CenterX=-19 CenterY=21.2 CenterZ=0 NormalX=0 NormalY=0 NormalZ=1 AngleXU=0 Radius=6.3
    g34: Circle CenterX=-42 CenterY=21.2 CenterZ=0 NormalX=0 NormalY=0 NormalZ=1 AngleXU=0 Radius=6.3
    g35: Circle CenterX=-65 CenterY=21.2 CenterZ=0 NormalX=0 NormalY=0 NormalZ=1 AngleXU=0 Radius=6.3
    g36: LineSegment [constr] StartX=-4 StartY=21.2 StartZ=0 EndX=-65 EndY=21.2 EndZ=0
  constraints (96):
    c: Coincident(g0,g-41)
    c: Horizontal(g0)
    c: PointOnObject(g0,g-39)
    c: Coincident(g1,g0)
    c: Vertical(g1)
    c: DistanceY(g1,g1) = 3
    c: Coincident(g2,g-17)
    c: Vertical(g2)
    c: Coincident(g3,g-16)
    c: Vertical(g3)
    c: DistanceY(g2,g2) = 2
    c: DistanceY(g3,g3) = 2
    c: Coincident(g4,g3)
    c: Coincident(g4,g2)
    c: Coincident(g5,g-17)
    c: Coincident(g5,g2)
    c: Coincident(g6,g1)
    c: Horizontal(g6)
    c: Coincident(g6,g5)
    c: Coincident(g7,g-15)
    c: Coincident(g8,g7)
    c: Coincident(g8,g3)
    c: Coincident(g8,g-15)
    c: Horizontal(g9)
    c: DistanceY(g-13,g9) = 2
    c: Coincident(g10,g7)
    c: Parallel(g10,g-14)
    c: Coincident(g9,g10)
    c: Distance(g11) = 2
    c: Coincident(g11,g-11)
    c: Perpendicular(g-11,g11)
    c: Distance(g12) = 2
    c: Coincident(g12,g-12)
    c: Perpendicular(g-11,g12)
    c: Coincident(g13,g11)
    c: Coincident(g13,g12)
    c: Coincident(g14,g-32)
    c: Coincident(g14,g12)
    c: Coincident(g14,g9)
    c: Coincident(g15,g-10)
    c: Coincident(g15,g11)
    c: Parallel(g16,g-22)
    c: Distance(g17) = 4
    c: PointOnObject(g17,g16)
    c: Coincident(g15,g16)
    c: Horizontal(g18)
    c: Coincident(g18,g16)
    c: Coincident(g19,g0)
    c: PointOnObject(g19,g-39)
    c: DistanceY(g19,g-36) = 2
    c: Coincident(g18,g19)
    c: Diameter(g22) = 3.6
    c: Coincident(g22,g-9)
    c: Diameter(g23) = 3.6
    c: Coincident(g23,g-8)
    c: Diameter(g24) = 3.6
    c: Diameter(g25) = 3.6
    c: Diameter(g26) = 3.6
    c: Diameter(g27) = 3.6
    c: Diameter(g28) = 3.6
    c: Coincident(g27,g-4)
    c: Coincident(g28,g-3)
    c: Coincident(g25,g-6)
    c: Coincident(g26,g-5)
    c: Coincident(g24,g-7)
    c: Parallel(g20,g-21)
    c: Equal(g20,g-21)
    c: Parallel(g21,g-19)
    c: Equal(g21,g-19)
    c: Distance(g29) = 0.2
    c: Distance(g30) = 0.2
    c: Parallel(g29,g-20)
    c: Parallel(g31,g-20)
    c: Equal(g31,g-20)
    c: Coincident(g30,g31)
    c: Coincident(g31,g29)
    c: Coincident(g29,g-21)
    c: Parallel(g30,g31)
    c: Coincident(g17,g30)
    c: Coincident(g20,g29)
    c: Coincident(g21,g30)
    c: Perpendicular(g16,g17)
    c: Coincident(g32,g21)
    c: Coincident(g32,g20)
    c: Perpendicular(g10,g7)
    c: Diameter(g33) = 12.6
    c: Diameter(g34) = 12.6
    c: Diameter(g35) = 12.6
    c: Horizontal(g36)
    c: PointOnObject(g33,g36)
    c: PointOnObject(g34,g36)
    c: DistanceX(g34,g33) = 23
    c: DistanceX(g35,g34) = 23
    c: DistanceX(g33,g36) = 15
    c: Symmetric(g-24,g-24,g36)
    c: Coincident(g36,g35)
FEATURE [Sketcher::SketchObject] Sketch075  label="lato dx pistola"
  ArcFitTolerance = 1e-06
  AttachmentSupport = -> [XZ_Plane]
  ExternalGeometry = -> [Sketch016,Sketch,Sketch058,Sketch074]
  FullyConstrained = true
  MakeInternals = false
  MapMode = 5
  Placement = pos=(0,0,0) rot=(1,0,0;1.5708rad)
  sketch-geometry (61):
    g0: LineSegment StartX=-82.8 StartY=3.2 StartZ=0 EndX=0 EndY=3.2 EndZ=0
    g1: LineSegment StartX=-82.8 StartY=3.2 StartZ=0 EndX=-82.8 EndY=6.2 EndZ=0
    g2: LineSegment [constr] StartX=-107.6 StartY=18 StartZ=0 EndX=-107.6 EndY=20 EndZ=0
    g3: LineSegment [constr] StartX=-132.428 StartY=18 StartZ=0 EndX=-132.428 EndY=20 EndZ=0
    g4: LineSegment StartX=-132.428 StartY=20 StartZ=0 EndX=-107.6 EndY=20 EndZ=0
    g5: ArcOfCircle CenterX=-107.6 CenterY=4 CenterZ=0 NormalX=0 NormalY=0 NormalZ=1 AngleXU=0 Radius=16 StartAngle=0.137937 EndAngle=1.5708
    g6: LineSegment StartX=-82.8 StartY=6.2 StartZ=0 EndX=-91.752 EndY=6.2 EndZ=0
    g7: LineSegment [constr] StartX=-145.743 StartY=8.32624 StartZ=0 EndX=-147.645 EndY=8.94427 EndZ=0
    g8: ArcOfCircle CenterX=-132.428 CenterY=4 CenterZ=0 NormalX=0 NormalY=0 NormalZ=1 AngleXU=0 Radius=16 StartAngle=1.5708 EndAngle=2.82743
    g9: LineSegment StartX=-215.932 StartY=-80.4316 StartZ=0 EndX=-176.685 EndY=-80.4316 EndZ=0
    g10: LineSegment StartX=-147.645 StartY=8.94427 StartZ=0 EndX=-176.685 EndY=-80.4316 EndZ=0
    g11: LineSegment [constr] StartX=-193.988 StartY=-2.33927 StartZ=0 EndX=-192.176 EndY=-3.18451 EndZ=0
    g12: LineSegment [constr] StartX=-217.232 StartY=-52.1862 StartZ=0 EndX=-215.42 EndY=-53.0314 EndZ=0
    g13: LineSegment StartX=-192.176 StartY=-3.18451 StartZ=0 EndX=-215.42 EndY=-53.0314 EndZ=0
    g14: ArcOfCircle CenterX=-184.801 CenterY=-67.3089 CenterZ=0 NormalX=0 NormalY=0 NormalZ=1 AngleXU=0 Radius=33.7833 StartAngle=2.70526 EndAngle=3.54053
    g15: ArcOfCircle CenterX=-207.583 CenterY=4 CenterZ=0 NormalX=0 NormalY=0 NormalZ=1 AngleXU=0 Radius=17 StartAngle=5.84685 EndAngle=7.56663
    g16: LineSegment StartX=-202.765 StartY=20.303 StartZ=0 EndX=-195.887 EndY=39.2 EndZ=0
    g17: LineSegment [constr] StartX=-193.885 StartY=33.0037 StartZ=0 EndX=-197.644 EndY=34.3718 EndZ=0
    g18: LineSegment StartX=-195.887 StartY=39.2 StartZ=0 EndX=0 EndY=39.2 EndZ=0
    g19: LineSegment StartX=0 StartY=3.2 StartZ=0 EndX=0 EndY=39.2 EndZ=0
    g20: LineSegment StartX=-189.939 StartY=31.5672 StartZ=0 EndX=-192.333 EndY=24.9893 EndZ=0
    g21: LineSegment StartX=-196.467 StartY=26.4942 StartZ=0 EndX=-194.073 EndY=33.0721 EndZ=0
    g22: Circle CenterX=-213.443 CenterY=-76.8316 CenterZ=0 NormalX=0 NormalY=0 NormalZ=1 AngleXU=0 Radius=1.8
    g23: Circle CenterX=-179.305 CenterY=-76.8316 CenterZ=0 NormalX=0 NormalY=0 NormalZ=1 AngleXU=0 Radius=1.8
    g24: Circle CenterX=-184.08 CenterY=34.8 CenterZ=0 NormalX=0 NormalY=0 NormalZ=1 AngleXU=0 Radius=1.8
    g25: Circle CenterX=-78.51 CenterY=34.8 CenterZ=0 NormalX=0 NormalY=0 NormalZ=1 AngleXU=0 Radius=1.8
    g26: Circle CenterX=-78.51 CenterY=7.6 CenterZ=0 NormalX=0 NormalY=0 NormalZ=1 AngleXU=0 Radius=1.8
    g27: Circle CenterX=-5.6 CenterY=34.8 CenterZ=0 NormalX=0 NormalY=0 NormalZ=1 AngleXU=0 Radius=1.8
    g28: Circle CenterX=-5.6 CenterY=7.6 CenterZ=0 NormalX=0 NormalY=0 NormalZ=1 AngleXU=0 Radius=1.8
    g29: LineSegment StartX=-190.127 StartY=31.6356 StartZ=0 EndX=-189.939 EndY=31.5672 EndZ=0
    g30: LineSegment StartX=-194.073 StartY=33.0721 StartZ=0 EndX=-193.885 EndY=33.0037 EndZ=0
    g31: LineSegment StartX=-193.885 StartY=33.0037 StartZ=0 EndX=-190.127 EndY=31.6356 EndZ=0
    g32: LineSegment StartX=-196.467 StartY=26.4942 StartZ=0 EndX=-192.333 EndY=24.9893 EndZ=0
    g33: LineSegment [constr] StartX=-4 StartY=21.2 StartZ=0 EndX=-87.91 EndY=21.2 EndZ=0
    g34: GeomPoint [constr] X=-4 Y=21.2 Z=0
    g35: LineSegment [constr] StartX=-15.2 StartY=33.7 StartZ=0 EndX=-15.2 EndY=8.7 EndZ=0
    g36: LineSegment [constr] StartX=-15.2 StartY=33.7 StartZ=0 EndX=-56.2 EndY=33.7 EndZ=0
    g37: LineSegment [constr] StartX=-15.2 StartY=8.7 StartZ=0 EndX=-56.2 EndY=8.7 EndZ=0
    g38: LineSegment [constr] StartX=-56.2 StartY=33.7 StartZ=0 EndX=-56.2 EndY=8.7 EndZ=0
    g39: Circle CenterX=-18.6 CenterY=30.3 CenterZ=0 NormalX=0 NormalY=0 NormalZ=1 AngleXU=0 Radius=3.4
    g40: Circle CenterX=-18.6 CenterY=12.1 CenterZ=0 NormalX=0 NormalY=0 NormalZ=1 AngleXU=0 Radius=3.4
    g41: Circle CenterX=-43.2 CenterY=30.3 CenterZ=0 NormalX=0 NormalY=0 NormalZ=1 AngleXU=0 Radius=3.4
    g42: Circle CenterX=-43.2 CenterY=12.1 CenterZ=0 NormalX=0 NormalY=0 NormalZ=1 AngleXU=0 Radius=3.4
    g43: LineSegment [constr] StartX=-4 StartY=21.2 StartZ=0 EndX=-15.2 EndY=21.2 EndZ=0
    g44: LineSegment [constr] StartX=-15.2 StartY=21.2 StartZ=0 EndX=-36.2 EndY=21.2 EndZ=0
    g45: LineSegment [constr] StartX=-41.5 StartY=16.2 StartZ=0 EndX=-30.9 EndY=16.2 EndZ=0
    g46: LineSegment [constr] StartX=-30.9 StartY=16.2 StartZ=0 EndX=-30.9 EndY=26.2 EndZ=0
    g47: LineSegment [constr] StartX=-30.9 StartY=26.2 StartZ=0 EndX=-41.5 EndY=26.2 EndZ=0
    g48: LineSegment [constr] StartX=-41.5 StartY=26.2 StartZ=0 EndX=-41.5 EndY=16.2 EndZ=0
    g49: GeomPoint [constr] X=-36.2 Y=21.2 Z=0
    g50: Circle CenterX=-36.2 CenterY=21.2 CenterZ=0 NormalX=0 NormalY=0 NormalZ=1 AngleXU=0 Radius=2.8
    g51: LineSegment [constr] StartX=-24.2 StartY=26.7 StartZ=0 EndX=-24.2 EndY=15.7 EndZ=0
    g52: Circle CenterX=-24.2 CenterY=26.7 CenterZ=0 NormalX=0 NormalY=0 NormalZ=1 AngleXU=0 Radius=3
    g53: Circle CenterX=-24.2 CenterY=15.7 CenterZ=0 NormalX=0 NormalY=0 NormalZ=1 AngleXU=0 Radius=3
    g54: GeomPoint X=-18.6 Y=30.3 Z=0
    g55: GeomPoint X=-18.6 Y=12.1 Z=0
    g56: GeomPoint X=-43.2 Y=12.1 Z=0
    g57: GeomPoint X=-43.2 Y=30.3 Z=0
    g58: Circle CenterX=-65 CenterY=21.2 CenterZ=0 NormalX=0 NormalY=0 NormalZ=1 AngleXU=0 Radius=1.5
    g59: Circle CenterX=-42 CenterY=21.2 CenterZ=0 NormalX=0 NormalY=0 NormalZ=1 AngleXU=0 Radius=1.5
    g60: Circle CenterX=-19 CenterY=21.2 CenterZ=0 NormalX=0 NormalY=0 NormalZ=1 AngleXU=0 Radius=1.5
  constraints (149):
    c: Coincident(g0,g-41)
    c: Horizontal(g0)
    c: PointOnObject(g0,g-39)
    c: Coincident(g1,g0)
    c: Vertical(g1)
    c: DistanceY(g1,g1) = 3
    c: Coincident(g2,g-17)
    c: Vertical(g2)
    c: Coincident(g3,g-16)
    c: Vertical(g3)
    c: DistanceY(g2,g2) = 2
    c: DistanceY(g3,g3) = 2
    c: Coincident(g4,g3)
    c: Coincident(g4,g2)
    c: Coincident(g5,g-17)
    c: Coincident(g5,g2)
    c: Coincident(g6,g1)
    c: Horizontal(g6)
    c: Coincident(g6,g5)
    c: Coincident(g7,g-15)
    c: Coincident(g8,g7)
    c: Coincident(g8,g3)
    c: Coincident(g8,g-15)
    c: Horizontal(g9)
    c: DistanceY(g-13,g9) = 2
    c: Coincident(g10,g7)
    c: Parallel(g10,g-14)
    c: Coincident(g9,g10)
    c: Distance(g11) = 2
    c: Coincident(g11,g-11)
    c: Perpendicular(g-11,g11)
    c: Distance(g12) = 2
    c: Coincident(g12,g-12)
    c: Perpendicular(g-11,g12)
    c: Coincident(g13,g11)
    c: Coincident(g13,g12)
    c: Coincident(g14,g-32)
    c: Coincident(g14,g12)
    c: Coincident(g14,g9)
    c: Coincident(g15,g-10)
    c: Coincident(g15,g11)
    c: Parallel(g16,g-22)
    c: Distance(g17) = 4
    c: PointOnObject(g17,g16)
    c: Coincident(g15,g16)
    c: Horizontal(g18)
    c: Coincident(g18,g16)
    c: Coincident(g19,g0)
    c: PointOnObject(g19,g-39)
    c: DistanceY(g19,g-36) = 2
    c: Coincident(g18,g19)
    c: Diameter(g22) = 3.6
    c: Coincident(g22,g-9)
    c: Diameter(g23) = 3.6
    c: Coincident(g23,g-8)
    c: Diameter(g24) = 3.6
    c: Diameter(g25) = 3.6
    c: Diameter(g26) = 3.6
    c: Diameter(g27) = 3.6
    c: Diameter(g28) = 3.6
    c: Coincident(g27,g-4)
    c: Coincident(g28,g-3)
    c: Coincident(g25,g-6)
    c: Coincident(g26,g-5)
    c: Coincident(g24,g-7)
    c: Parallel(g20,g-21)
    c: Equal(g20,g-21)
    c: Parallel(g21,g-19)
    c: Equal(g21,g-19)
    c: Distance(g29) = 0.2
    c: Distance(g30) = 0.2
    c: Parallel(g29,g-20)
    c: Parallel(g31,g-20)
    c: Equal(g31,g-20)
    c: Coincident(g30,g31)
    c: Coincident(g31,g29)
    c: Coincident(g29,g-21)
    c: Parallel(g30,g31)
    c: Coincident(g17,g30)
    c: Coincident(g20,g29)
    c: Coincident(g21,g30)
    c: Perpendicular(g16,g17)
    c: Coincident(g32,g21)
    c: Coincident(g32,g20)
    c: Perpendicular(g10,g7)
    c: Horizontal(g33)
    c: Symmetric(g-24,g-24,g33)
    c: PointOnObject(g33,g-28)
    c: Symmetric(g-24,g-24,g34)
    c: DistanceY(g35,g35) = 25
    c: Symmetric(g35,g35,g33)
    c: Distance(g36) = 41
    c: Coincident(g36,g35)
    c: Horizontal(g36)
    c: Coincident(g37,g35)
    c: Horizontal(g37)
    c: Coincident(g38,g36)
    c: Vertical(g38)
    c: Coincident(g37,g38)
    c: Diameter(g39) = 6.8
    c: Diameter(g40) = 6.8
    c: Tangent(g39,g36)
    c: Tangent(g40,g37)
    c: Tangent(g39,g35)
    c: Tangent(g40,g35)
    c: Diameter(g41) = 6.8
    c: Diameter(g42) = 6.8
    c: Tangent(g41,g36)
    c: Tangent(g42,g37)
    c: DistanceX(g41,g39) = 24.6
    c: DistanceX(g42,g40) = 24.6
    c: Distance(g43) = 11.2
    c: Coincident(g43,g33)
    c: PointOnObject(g43,g33)
    c: PointOnObject(g43,g35)
    c: Distance(g44) = 21
    c: Coincident(g44,g43)
    c: PointOnObject(g44,g33)
    c: Coincident(g45,g46)
    c: Coincident(g46,g47)
    c: Coincident(g47,g48)
    c: Coincident(g48,g45)
    c: Horizontal(g45)
    c: Horizontal(g47)
    c: Vertical(g46)
    c: Vertical(g48)
    c: Symmetric(g47,g45,g49)
    c: Distance(g46,g48) = 10.6
    c: Distance(g45,g47) = 10
    c: Coincident(g49,g44)
    c: Diameter(g50) = 5.6
    c: Coincident(g50,g44)
    c: Distance(g51) = 11
    c: Symmetric(g51,g51,g33)
    c: DistanceX(g51,g43) = 9
    c: Diameter(g52) = 6
    c: Coincident(g52,g51)
    c: Diameter(g53) = 6
    c: Coincident(g53,g51)
    c: Coincident(g40,g55)
    c: Coincident(g39,g54)
    c: Coincident(g41,g57)
    c: Coincident(g42,g56)
    c: Diameter(g58) = 3
    c: Diameter(g59) = 3
    c: Diameter(g60) = 3
    c: Coincident(g58,g-44)
    c: Coincident(g59,g-46)
    c: Coincident(g60,g-45)
FEATURE [Sketcher::SketchObject] Sketch078
  ArcFitTolerance = 1e-06
  AttachmentSupport = -> [XZ_Plane005]
  FullyConstrained = true
  MakeInternals = false
  MapMode = 5
  Placement = pos=(0,0,0) rot=(1,0,0;1.5708rad)
  sketch-geometry (5):
    g0: LineSegment [constr] StartX=0 StartY=5.5 StartZ=0 EndX=0 EndY=-5.5 EndZ=0
    g1: ArcOfCircle CenterX=0 CenterY=5.5 CenterZ=0 NormalX=0 NormalY=0 NormalZ=1 AngleXU=0 Radius=2.7 StartAngle=0 EndAngle=3.14159
    g2: ArcOfCircle CenterX=0 CenterY=-5.5 CenterZ=0 NormalX=0 NormalY=0 NormalZ=1 AngleXU=0 Radius=2.7 StartAngle=3.1416 EndAngle=6.28318
    g3: LineSegment StartX=-2.7 StartY=5.5 StartZ=0 EndX=-2.7 EndY=-5.50001 EndZ=0
    g4: LineSegment StartX=2.7 StartY=5.5 StartZ=0 EndX=2.7 EndY=-5.50001 EndZ=0
  constraints (13):
    c: Distance(g0) = 11
    c: Vertical(g0)
    c: Symmetric(g0,g0,g-1)
    c: Radius(g1) = 2.7
    c: Coincident(g1,g0)
    c: Radius(g2) = 2.7
    c: Coincident(g2,g0)
    c: Vertical(g3)
    c: Vertical(g4)
    c: Coincident(g2,g4)
    c: Coincident(g2,g3)
    c: Tangent(g3,g1) = -1.5708
    c: Tangent(g4,g1) = 1.5708
FEATURE [PartDesign::Pad] Pad002
  Direction = (0,-1,2e-16)
  Length = 0.8
  Length2 = 10
  Placement = pos=(0,0,0) rot=(1,0,0;1.5708rad)
  Profile = -> Sketch078
  ReferenceAxis = -> Sketch078 [N_Axis]
  Refine = true
  Suppressed = false
  Type = 0
FEATURE [Sketcher::SketchObject] Sketch079
  ArcFitTolerance = 1e-06
  AttachmentSupport = -> [XZ_Plane005]
  ExternalGeometry = -> [Sketch078]
  FullyConstrained = true
  MakeInternals = false
  MapMode = 5
  Placement = pos=(0,0,0) rot=(1,0,0;1.5708rad)
  sketch-geometry (2):
    g0: Circle CenterX=-1e-16 CenterY=5.5 CenterZ=0 NormalX=0 NormalY=0 NormalZ=1 AngleXU=0 Radius=2.7
    g1: Circle CenterX=0 CenterY=-5.5 CenterZ=0 NormalX=0 NormalY=0 NormalZ=1 AngleXU=0 Radius=2.7
  constraints (4):
    c: Coincident(g0,g-3)
    c: PointOnObject(g-3,g0)
    c: Coincident(g1,g-4)
    c: Equal(g1,g-4)
FEATURE [PartDesign::Pad] Pad003
  BaseFeature = -> Pad002
  Direction = (0,-1,2e-16)
  Length = 5
  Length2 = 10
  Placement = pos=(0,0,0) rot=(1,0,0;1.5708rad)
  Profile = -> Sketch079
  ReferenceAxis = -> Sketch079 [N_Axis]
  Refine = true
  Suppressed = false
  Type = 0
FEATURE [PartDesign::Fillet] Fillet001
  Base = -> Pad003 [Edge16,Edge14]
  BaseFeature = -> Pad003
  Placement = pos=(0,0,0) rot=(1,0,0;1.5708rad)
  Radius = 0.4
  Refine = true
  SupportTransform = false
  Suppressed = false
  UseAllEdges = false
FEATURE [PartDesign::Body] Body005  label="pulsanti lato destro"
  AllowCompound = false
  Group = -> [Sketch078,Pad002,Sketch079,Pad003,Fillet001]
  Origin = -> Origin005
  Tip = -> Fillet001
FEATURE [PartDesign::SubShapeBinder] Binder
  BindCopyOnChange = 0
  BindMode = 0
  ClaimChildren = false
  Context = -> Body006 [Binder.]
  Fuse = false
  MakeFace = true
  OffsetFill = false
  OffsetIntersection = false
  OffsetJoinType = 0
  OffsetOpenResult = false
  PartialLoad = false
  Refine = true
  Relative = true
  Support = -> [Body[Sketch074.]]
  _Version = 2
FEATURE [PartDesign::SubShapeBinder] Binder001
  BindCopyOnChange = 0
  BindMode = 0
  ClaimChildren = false
  Context = -> Body007 [Binder001.]
  Fuse = false
  MakeFace = true
  OffsetFill = false
  OffsetIntersection = false
  OffsetJoinType = 0
  OffsetOpenResult = false
  PartialLoad = false
  Refine = true
  Relative = true
  Support = -> [Body[Sketch075.]]
  _Version = 2
FEATURE [Mesh::Feature] logo_per_PCB_definitivo_positivo
  Placement = pos=(-191,17,-66) rot=(0,1,1;0rad)
FEATURE [Sketcher::SketchObject] Sketch114  label="Sketch114 - base lato DX"
  ArcFitTolerance = 1e-06
  AttachmentSupport = -> [Binder001]
  ExternalGeometry = -> [Binder001]
  FullyConstrained = true
  MakeInternals = false
  MapMode = 5
  Placement = pos=(0,1e-15,0) rot=(0,0.707107,0.707107;3.14159rad)
  sketch-geometry (30):
    g0: Circle CenterX=5.6 CenterY=34.8 CenterZ=0 NormalX=0 NormalY=0 NormalZ=1 AngleXU=0 Radius=1.8
    g1: Circle CenterX=5.6 CenterY=7.6 CenterZ=0 NormalX=0 NormalY=0 NormalZ=1 AngleXU=0 Radius=1.8
    g2: Circle CenterX=24.2 CenterY=26.7 CenterZ=0 NormalX=0 NormalY=0 NormalZ=1 AngleXU=0 Radius=3
    g3: Circle CenterX=24.2 CenterY=15.7 CenterZ=0 NormalX=0 NormalY=0 NormalZ=1 AngleXU=0 Radius=3
    g4: Circle CenterX=36.2 CenterY=21.2 CenterZ=0 NormalX=0 NormalY=0 NormalZ=1 AngleXU=0 Radius=2.8
    g5: Circle CenterX=78.51 CenterY=34.8 CenterZ=0 NormalX=0 NormalY=0 NormalZ=1 AngleXU=0 Radius=1.8
    g6: Circle CenterX=78.51 CenterY=7.6 CenterZ=0 NormalX=0 NormalY=0 NormalZ=1 AngleXU=0 Radius=1.8
    g7: Circle CenterX=184.08 CenterY=34.8 CenterZ=0 NormalX=0 NormalY=0 NormalZ=1 AngleXU=0 Radius=1.8
    g8: Circle CenterX=213.443 CenterY=-76.8316 CenterZ=0 NormalX=0 NormalY=0 NormalZ=1 AngleXU=0 Radius=1.8
    g9: Circle CenterX=179.305 CenterY=-76.8316 CenterZ=0 NormalX=0 NormalY=0 NormalZ=1 AngleXU=0 Radius=1.8
    g10: ArcOfCircle [constr] CenterX=132.428 CenterY=4 CenterZ=0 NormalX=0 NormalY=0 NormalZ=1 AngleXU=0 Radius=16 StartAngle=0.314159 EndAngle=1.5708
    g11: ArcOfCircle CenterX=107.6 CenterY=4 CenterZ=0 NormalX=0 NormalY=0 NormalZ=1 AngleXU=0 Radius=16 StartAngle=1.5708 EndAngle=3.00366
    g12: ArcOfCircle CenterX=207.583 CenterY=4 CenterZ=0 NormalX=0 NormalY=0 NormalZ=1 AngleXU=0 Radius=17 StartAngle=1.85815 EndAngle=3.57792
    g13: ArcOfCircle CenterX=184.801 CenterY=-67.3089 CenterZ=0 NormalX=0 NormalY=0 NormalZ=1 AngleXU=0 Radius=33.7833 StartAngle=5.88425 EndAngle=6.71952
    g14: LineSegment StartX=0 StartY=39.2 StartZ=0 EndX=0 EndY=3.2 EndZ=0
    g15: LineSegment StartX=0 StartY=3.2 StartZ=0 EndX=82.8 EndY=3.2 EndZ=0
    g16: LineSegment StartX=82.8 StartY=3.2 StartZ=0 EndX=82.8 EndY=6.2 EndZ=0
    g17: LineSegment StartX=82.8 StartY=6.2 StartZ=0 EndX=91.752 EndY=6.2 EndZ=0
    g18: LineSegment StartX=107.6 StartY=20 StartZ=0 EndX=132.428 EndY=20 EndZ=0
    g19: LineSegment StartX=147.645 StartY=8.94427 StartZ=0 EndX=176.685 EndY=-80.4316 EndZ=0
    g20: LineSegment StartX=176.685 StartY=-80.4316 StartZ=0 EndX=215.932 EndY=-80.4316 EndZ=0
    g21: LineSegment StartX=215.42 StartY=-53.0314 StartZ=0 EndX=192.176 EndY=-3.18451 EndZ=0
    g22: LineSegment StartX=202.765 StartY=20.303 StartZ=0 EndX=195.887 EndY=39.2 EndZ=0
    g23: LineSegment StartX=195.887 StartY=39.2 StartZ=0 EndX=0 EndY=39.2 EndZ=0
    g24: LineSegment StartX=196.467 StartY=26.4942 StartZ=0 EndX=194.073 EndY=33.0721 EndZ=0
    g25: LineSegment StartX=194.073 StartY=33.0721 StartZ=0 EndX=189.939 EndY=31.5672 EndZ=0
    g26: LineSegment StartX=189.939 StartY=31.5672 StartZ=0 EndX=192.333 EndY=24.9893 EndZ=0
    g27: LineSegment StartX=192.333 StartY=24.9893 StartZ=0 EndX=196.467 EndY=26.4942 EndZ=0
    g28: LineSegment StartX=132.428 StartY=20 StartZ=0 EndX=144.053 EndY=20 EndZ=0
    g29: LineSegment StartX=144.053 StartY=20 StartZ=0 EndX=147.645 EndY=8.94427 EndZ=0
  constraints (65):
    c: Equal(g0,g-25)
    c: Equal(g2,g-29)
    c: Equal(g3,g-30)
    c: Equal(g4,g-28)
    c: Equal(g1,g-26)
    c: Coincident(g0,g-25)
    c: Coincident(g1,g-26)
    c: Coincident(g2,g-29)
    c: Coincident(g3,g-30)
    c: Coincident(g4,g-28)
    c: Equal(g5,g-23)
    c: Equal(g6,g-24)
    c: Coincident(g5,g-23)
    c: Coincident(g6,g-24)
    c: Equal(g7,g-20)
    c: Coincident(g7,g-20)
    c: Equal(g9,g-22)
    c: Coincident(g9,g-22)
    c: Equal(g8,g-21)
    c: Coincident(g8,g-21)
    c: Equal(g13,g-12)
    c: Equal(g12,g-14)
    c: Equal(g10,g-9)
    c: Equal(g11,g-7)
    c: Coincident(g14,g-27)
    c: Coincident(g14,g-27)
    c: Coincident(g15,g14)
    c: Coincident(g15,g-5)
    c: Coincident(g16,g15)
    c: Coincident(g16,g-6)
    c: Coincident(g17,g16)
    c: Coincident(g17,g-7)
    c: Coincident(g11,g17)
    c: Coincident(g11,g-8)
    c: Coincident(g18,g11)
    c: Coincident(g18,g-9)
    c: Coincident(g10,g18)
    c: Coincident(g10,g-10)
    c: Coincident(g19,g10)
    c: Coincident(g19,g-11)
    c: Coincident(g20,g19)
    c: Coincident(g20,g-12)
    c: Coincident(g13,g20)
    c: Coincident(g13,g-13)
    c: Coincident(g21,g13)
    c: Coincident(g21,g-14)
    c: Coincident(g12,g21)
    c: Coincident(g12,g-15)
    c: Coincident(g22,g12)
    c: Coincident(g22,g-15)
    c: Coincident(g23,g22)
    c: Coincident(g23,g14)
    c: Coincident(g24,g-18)
    c: Coincident(g24,g-16)
    c: Coincident(g25,g24)
    c: Coincident(g25,g-19)
    c: Coincident(g26,g25)
    c: Coincident(g26,g-19)
    c: Coincident(g27,g26)
    c: Coincident(g27,g24)
    c: Coincident(g29,g10)
    c: Coincident(g28,g10)
    c: Coincident(g29,g28)
    c: Parallel(g28,g18)
    c: Parallel(g29,g19)
FEATURE [PartDesign::Pad] Pad011
  Direction = (0,1,-2e-16)
  Length = 2
  Length2 = 10
  Profile = -> Sketch114
  ReferenceAxis = -> Sketch114 [N_Axis]
  Refine = true
  Reversed = true
  Suppressed = false
  Type = 0
FEATURE [Sketcher::SketchObject] Sketch115
  ArcFitTolerance = 1e-06
  AttachmentSupport = -> [Pad011]
  ExternalGeometry = -> [Binder001]
  FullyConstrained = true
  MakeInternals = false
  MapMode = 5
  Placement = pos=(0,1.7e-15,0) rot=(0,0.707107,0.707107;3.14159rad)
  sketch-geometry (4):
    g0: ArcOfCircle CenterX=24.2 CenterY=26.7 CenterZ=0 NormalX=0 NormalY=0 NormalZ=1 AngleXU=0 Radius=3 StartAngle=4.48384e-08 EndAngle=3.14159
    g1: ArcOfCircle CenterX=24.2 CenterY=15.7 CenterZ=0 NormalX=0 NormalY=0 NormalZ=1 AngleXU=0 Radius=3 StartAngle=3.14159 EndAngle=6.28318
    g2: LineSegment StartX=21.2 StartY=26.7 StartZ=0 EndX=21.2 EndY=15.7 EndZ=0
    g3: LineSegment StartX=27.2 StartY=26.7 StartZ=0 EndX=27.2 EndY=15.7 EndZ=0
  constraints (12):
    c: Equal(g1,g-4)
    c: Equal(g0,g-3)
    c: Coincident(g0,g-3)
    c: Coincident(g1,g-4)
    c: Vertical(g2)
    c: Vertical(g3)
    c: Tangent(g3,g-3)
    c: Tangent(g2,g-3)
    c: Coincident(g0,g2)
    c: Coincident(g0,g3)
    c: Coincident(g1,g2)
    c: Coincident(g3,g1)
FEATURE [Sketcher::SketchObject] Sketch117  label="Sketch117 - fori per inserto M3 x 3 x 4.5"
  ArcFitTolerance = 1e-06
  AttachmentSupport = -> [Pad011]
  ExternalGeometry = -> [Binder001]
  FullyConstrained = true
  MakeInternals = false
  MapMode = 5
  Placement = pos=(0,1.7e-15,0) rot=(0,0.707107,0.707107;3.14159rad)
  sketch-geometry (4):
    g0: Circle CenterX=43.2 CenterY=30.3 CenterZ=0 NormalX=0 NormalY=0 NormalZ=1 AngleXU=0 Radius=2.25
    g1: Circle CenterX=43.2 CenterY=12.1 CenterZ=0 NormalX=0 NormalY=0 NormalZ=1 AngleXU=0 Radius=2.25
    g2: Circle CenterX=18.6 CenterY=30.3 CenterZ=0 NormalX=0 NormalY=0 NormalZ=1 AngleXU=0 Radius=2.25
    g3: Circle CenterX=18.6 CenterY=12.1 CenterZ=0 NormalX=0 NormalY=0 NormalZ=1 AngleXU=0 Radius=2.25
  constraints (8):
    c: Diameter(g0) = 4.5
    c: Diameter(g1) = 4.5
    c: Diameter(g2) = 4.5
    c: Diameter(g3) = 4.5
    c: Coincident(g2,g-3)
    c: Coincident(g3,g-6)
    c: Coincident(g0,g-4)
    c: Coincident(g1,g-5)
FEATURE [Sketcher::SketchObject] Sketch118
  ArcFitTolerance = 1e-06
  AttachmentSupport = -> [Pad011]
  ExternalGeometry = -> [Binder001]
  FullyConstrained = true
  MakeInternals = false
  MapMode = 5
  Placement = pos=(0,-2,0) rot=(1,0,0;1.5708rad)
  sketch-geometry (12):
    g0: Circle CenterX=-78.51 CenterY=34.8 CenterZ=0 NormalX=0 NormalY=0 NormalZ=1 AngleXU=0 Radius=1.8
    g1: Circle CenterX=-78.51 CenterY=7.6 CenterZ=0 NormalX=0 NormalY=0 NormalZ=1 AngleXU=0 Radius=1.8
    g2: Circle CenterX=-5.6 CenterY=34.8 CenterZ=0 NormalX=0 NormalY=0 NormalZ=1 AngleXU=0 Radius=1.8
    g3: Circle CenterX=-5.6 CenterY=7.6 CenterZ=0 NormalX=0 NormalY=0 NormalZ=1 AngleXU=0 Radius=1.8
    g4: LineSegment StartX=0 StartY=39.2 StartZ=0 EndX=0 EndY=3.2 EndZ=0
    g5: LineSegment StartX=0 StartY=3.2 StartZ=0 EndX=-82.8 EndY=3.2 EndZ=0
    g6: LineSegment StartX=-82.8 StartY=3.2 StartZ=0 EndX=-82.8 EndY=39.2 EndZ=0
    g7: LineSegment StartX=-82.8 StartY=39.2 StartZ=0 EndX=0 EndY=39.2 EndZ=0
    g8: ArcOfCircle CenterX=-65 CenterY=21.2 CenterZ=0 NormalX=0 NormalY=0 NormalZ=1 AngleXU=0 Radius=10 StartAngle=1.5708 EndAngle=4.71239
    g9: ArcOfCircle CenterX=-19 CenterY=21.2 CenterZ=0 NormalX=0 NormalY=0 NormalZ=1 AngleXU=0 Radius=10 StartAngle=4.71239 EndAngle=7.85398
    g10: LineSegment StartX=-65 StartY=31.2 StartZ=0 EndX=-19 EndY=31.2 EndZ=0
    g11: LineSegment StartX=-65 StartY=11.2 StartZ=0 EndX=-19 EndY=11.2 EndZ=0
  constraints (25):
    c: Equal(g2,g-5)
    c: Equal(g3,g-7)
    c: Equal(g1,g-6)
    c: Equal(g0,g-4)
    c: Coincident(g0,g-4)
    c: Coincident(g1,g-6)
    c: Coincident(g3,g-7)
    c: Coincident(g2,g-5)
    c: Coincident(g4,g-8)
    c: Coincident(g4,g-9)
    c: Coincident(g5,g4)
    c: Coincident(g5,g-10)
    c: Coincident(g6,g5)
    c: PointOnObject(g6,g-3)
    c: Vertical(g6)
    c: Coincident(g7,g6)
    c: Coincident(g7,g4)
    c: Tangent(g8,g10) = 1.5708
    c: Tangent(g8,g11) = -1.5708
    c: Tangent(g9,g10) = 1.5708
    c: Tangent(g9,g11) = -1.5708
    c: Equal(g8,g9)
    c: Radius(g8) = 10
    c: Coincident(g8,g-11)
    c: Coincident(g9,g-12)
FEATURE [Sketcher::SketchObject] Sketch120
  ArcFitTolerance = 1e-06
  AttachmentSupport = -> [Pad011]
  ExternalGeometry = -> [Binder001]
  FullyConstrained = true
  MakeInternals = false
  MapMode = 5
  Placement = pos=(0,-2,0) rot=(1,0,0;1.5708rad)
  sketch-geometry (4):
    g0: LineSegment StartX=-137.815 StartY=39.2 StartZ=0 EndX=-142.655 EndY=24.303 EndZ=0
    g1: LineSegment StartX=-137.815 StartY=39.2 StartZ=0 EndX=-110.815 EndY=39.2 EndZ=0
    g2: LineSegment StartX=-142.655 StartY=24.303 StartZ=0 EndX=-110.815 EndY=24.303 EndZ=0
    g3: ArcOfCircle CenterX=-92.2534 CenterY=31.7515 CenterZ=0 NormalX=0 NormalY=0 NormalZ=1 AngleXU=0 Radius=20 StartAngle=2.75997 EndAngle=3.52321
  constraints (12):
    c: PointOnObject(g0,g-3)
    c: Coincident(g1,g0)
    c: PointOnObject(g1,g-3)
    c: Coincident(g2,g0)
    c: Horizontal(g2)
    c: Tangent(g0,g-4)
    c: Vertical(g2,g1)
    c: DistanceX(g1,g1) = 27
    c: DistanceY(g-6,g0) = 4
    c: Radius(g3) = 20
    c: Coincident(g3,g1)
    c: Coincident(g3,g2)
FEATURE [Sketcher::SketchObject] Sketch121
  ArcFitTolerance = 1e-06
  AttachmentSupport = -> [Pad011]
  ExternalGeometry = -> [Binder001]
  FullyConstrained = true
  MakeInternals = false
  MapMode = 5
  Placement = pos=(0,-2,0) rot=(1,0,0;1.5708rad)
  sketch-geometry (15):
    g0: LineSegment StartX=-137.815 StartY=39.2 StartZ=0 EndX=-143.955 EndY=20.303 EndZ=0
    g1: LineSegment StartX=-143.955 StartY=20.303 StartZ=0 EndX=-190.141 EndY=20.303 EndZ=0
    g2: LineSegment StartX=-190.141 StartY=20.303 StartZ=0 EndX=-186.139 EndY=31.3 EndZ=0
    g3: LineSegment StartX=-178.754 StartY=39.2 StartZ=0 EndX=-180.791 EndY=33.6029 EndZ=0
    g4: ArcOfCircle CenterX=-184.08 CenterY=34.8 CenterZ=0 NormalX=0 NormalY=0 NormalZ=1 AngleXU=0 Radius=3.5 StartAngle=4.71239 EndAngle=5.93412
    g5: LineSegment StartX=-184.08 StartY=31.3 StartZ=0 EndX=-186.139 EndY=31.3 EndZ=0
    g6: LineSegment StartX=-137.815 StartY=39.2 StartZ=0 EndX=-156.815 EndY=39.2 EndZ=0
    g7: LineSegment StartX=-168.815 StartY=39.2 StartZ=0 EndX=-178.754 EndY=39.2 EndZ=0
    g8: LineSegment StartX=-157.815 StartY=39.2 StartZ=0 EndX=-167.815 EndY=39.2 EndZ=0
    g9: LineSegment StartX=-168.815 StartY=31.2 StartZ=0 EndX=-156.815 EndY=31.2 EndZ=0
    g10: LineSegment StartX=-167.436 StartY=36.2 StartZ=0 EndX=-157.436 EndY=36.2 EndZ=0
    g11: ArcOfCircle CenterX=-176.411 CenterY=35.2 CenterZ=0 NormalX=0 NormalY=0 NormalZ=1 AngleXU=0 Radius=20 StartAngle=6.08183 EndAngle=6.48454
    g12: ArcOfCircle CenterX=-188.411 CenterY=35.2 CenterZ=0 NormalX=0 NormalY=0 NormalZ=1 AngleXU=0 Radius=20 StartAngle=6.08183 EndAngle=6.48454
    g13: ArcOfCircle CenterX=-177.411 CenterY=35.2 CenterZ=0 NormalX=0 NormalY=0 NormalZ=1 AngleXU=0 Radius=20 StartAngle=0.0500209 EndAngle=0.201358
    g14: ArcOfCircle CenterX=-187.411 CenterY=35.2 CenterZ=0 NormalX=0 NormalY=0 NormalZ=1 AngleXU=0 Radius=20 StartAngle=0.0500209 EndAngle=0.201358
  constraints (46):
    c: PointOnObject(g0,g-3)
    c: Tangent(g0,g-5)
    c: Coincident(g1,g0)
    c: Horizontal(g1)
    c: Coincident(g2,g1)
    c: PointOnObject(g3,g-3)
    c: Parallel(g3,g-6)
    c: Parallel(g2,g-6)
    c: Radius(g4) = 3.5
    c: Coincident(g4,g-7)
    c: Tangent(g3,g4) = 1.5708
    c: Horizontal(g5)
    c: Tangent(g5,g4) = 1.5708
    c: DistanceX(g-8,g5) = 3.8
    c: Coincident(g2,g5)
    c: Coincident(g6,g0)
    c: PointOnObject(g6,g-3)
    c: DistanceX(g6,g6) = 19
    c: PointOnObject(g7,g-3)
    c: DistanceX(g7,g6) = 12
    c: Coincident(g7,g3)
    c: PointOnObject(g8,g-3)
    c: PointOnObject(g8,g-3)
    c: DistanceX(g8,g8) = 10
    c: DistanceX(g8,g6) = 1
    c: Horizontal(g9)
    c: Vertical(g7,g9)
    c: Vertical(g6,g9)
    c: DistanceY(g9,g7) = 8
    c: Horizontal(g10)
    c: Equal(g8,g10)
    c: DistanceY(g10,g8) = 3
    c: Radius(g11) = 20
    c: Coincident(g11,g6)
    c: Coincident(g11,g9)
    c: Radius(g12) = 20
    c: Coincident(g12,g7)
    c: Coincident(g12,g9)
    c: Equal(g13,g11)
    c: Coincident(g13,g8)
    c: Coincident(g13,g10)
    c: Horizontal(g13,g11)
    c: Equal(g14,g12)
    c: Coincident(g14,g8)
    c: Coincident(g14,g10)
    c: Horizontal(g1,g-6)
FEATURE [Sketcher::SketchObject] Sketch122
  ArcFitTolerance = 1e-06
  AttachmentSupport = -> [Pad011]
  ExternalGeometry = -> [Binder001]
  FullyConstrained = true
  MakeInternals = false
  MapMode = 5
  Placement = pos=(0,-2,0) rot=(1,0,0;1.5708rad)
  sketch-geometry (8):
    g0: LineSegment StartX=-202.765 StartY=20.303 StartZ=0 EndX=-143.955 EndY=20.303 EndZ=0
    g1: ArcOfCircle CenterX=-184.801 CenterY=-67.3089 CenterZ=0 NormalX=0 NormalY=0 NormalZ=1 AngleXU=0 Radius=33.7833 StartAngle=2.70526 EndAngle=3.54053
    g2: LineSegment StartX=-176.685 StartY=-80.4316 StartZ=0 EndX=-215.932 EndY=-80.4316 EndZ=0
    g3: LineSegment StartX=-215.42 StartY=-53.0315 StartZ=0 EndX=-192.176 EndY=-3.18454 EndZ=0
    g4: ArcOfCircle CenterX=-207.583 CenterY=4 CenterZ=0 NormalX=0 NormalY=0 NormalZ=1 AngleXU=0 Radius=17 StartAngle=5.84685 EndAngle=7.56663
    g5: Circle CenterX=-213.443 CenterY=-76.8316 CenterZ=0 NormalX=0 NormalY=0 NormalZ=1 AngleXU=0 Radius=3
    g6: Circle CenterX=-179.305 CenterY=-76.8316 CenterZ=0 NormalX=0 NormalY=0 NormalZ=1 AngleXU=0 Radius=3
    g7: LineSegment StartX=-143.955 StartY=20.303 StartZ=0 EndX=-176.685 EndY=-80.4316 EndZ=0
  constraints (18):
    c: Coincident(g0,g-6)
    c: Coincident(g1,g-7)
    c: Coincident(g1,g-8)
    c: Coincident(g2,g1)
    c: Tangent(g3,g-5)
    c: Coincident(g4,g-6)
    c: Coincident(g4,g0)
    c: Coincident(g3,g4)
    c: Coincident(g1,g3)
    c: Diameter(g5) = 6
    c: Diameter(g6) = 6
    c: Coincident(g5,g-9)
    c: Coincident(g6,g-10)
    c: Horizontal(g0)
    c: Horizontal(g2)
    c: Coincident(g7,g0)
    c: Coincident(g7,g2)
    c: Tangent(g7,g-4)
FEATURE [Sketcher::SketchObject] Sketch123
  ArcFitTolerance = 1e-06
  AttachmentSupport = -> [Pad011]
  ExternalGeometry = -> [Binder001]
  FullyConstrained = true
  MakeInternals = false
  MapMode = 5
  Placement = pos=(0,-2,0) rot=(1,0,0;1.5708rad)
  sketch-geometry (4):
    g0: LineSegment StartX=-108 StartY=36.8 StartZ=0 EndX=-90 EndY=36.8 EndZ=0
    g1: LineSegment StartX=-108 StartY=36.8 StartZ=0 EndX=-108 EndY=26.8 EndZ=0
    g2: LineSegment StartX=-108 StartY=26.8 StartZ=0 EndX=-90 EndY=26.8 EndZ=0
    g3: ArcOfCircle CenterX=-94 CenterY=31.8 CenterZ=0 NormalX=0 NormalY=0 NormalZ=1 AngleXU=0 Radius=6.40312 StartAngle=5.38713 EndAngle=7.17924
  constraints (13):
    c: Horizontal(g0)
    c: Coincident(g1,g0)
    c: Vertical(g1)
    c: Coincident(g2,g1)
    c: Horizontal(g2)
    c: DistanceX(g0,g0) = 18
    c: DistanceY(g1,g1) = 10
    c: Equal(g0,g2)
    c: DistanceX(g0,g-3) = 90
    c: DistanceY(g0,g-3) = 2.4
    c: Coincident(g3,g0)
    c: Coincident(g3,g2)
    c: DistanceX(g3,g0) = 4
FEATURE [PartDesign::Chamfer] Chamfer014
  Angle = 45
  Base = -> Pad011 [Edge80,Edge4,Edge7]
  BaseFeature = -> Pad011
  ChamferType = 0
  FlipDirection = false
  Refine = true
  Size = 1.9
  Size2 = 1
  SupportTransform = false
  Suppressed = false
  UseAllEdges = false
FEATURE [PartDesign::Pocket] Pocket006
  BaseFeature = -> Chamfer014
  Direction = (0,-1,2e-16)
  Length = 1.2
  Length2 = 5
  Profile = -> Sketch115
  ReferenceAxis = -> Sketch115 [N_Axis]
  Refine = true
  Suppressed = false
  Type = 0
FEATURE [Sketcher::SketchObject] Sketch116  label="Sketch116 - pieno per inserto M3 x 3 x 4,5"
  ArcFitTolerance = 1e-06
  AttachmentSupport = -> [Pocket006]
  ExternalGeometry = -> [Binder001]
  FullyConstrained = true
  MakeInternals = false
  MapMode = 5
  Placement = pos=(0,1.7e-15,0) rot=(0,0.707107,0.707107;3.14159rad)
  sketch-geometry (4):
    g0: Circle CenterX=43.2 CenterY=30.3 CenterZ=0 NormalX=0 NormalY=0 NormalZ=1 AngleXU=0 Radius=3.4
    g1: Circle CenterX=43.2 CenterY=12.1 CenterZ=0 NormalX=0 NormalY=0 NormalZ=1 AngleXU=0 Radius=3.4
    g2: Circle CenterX=18.6 CenterY=30.3 CenterZ=0 NormalX=0 NormalY=0 NormalZ=1 AngleXU=0 Radius=3.4
    g3: Circle CenterX=18.6 CenterY=12.1 CenterZ=0 NormalX=0 NormalY=0 NormalZ=1 AngleXU=0 Radius=3.4
  constraints (8):
    c: Diameter(g0) = 6.8
    c: Diameter(g1) = 6.8
    c: Diameter(g2) = 6.8
    c: Diameter(g3) = 6.8
    c: Coincident(g2,g-3)
    c: Coincident(g0,g-4)
    c: Coincident(g3,g-6)
    c: Coincident(g1,g-5)
FEATURE [PartDesign::Pad] Pad012
  BaseFeature = -> Pocket006
  Direction = (0,1,-2e-16)
  Length = 2.4
  Length2 = 10
  Profile = -> Sketch116
  ReferenceAxis = -> Sketch116 [N_Axis]
  Refine = true
  Suppressed = false
  Type = 0
FEATURE [PartDesign::Pocket] Pocket007
  BaseFeature = -> Pad012
  Direction = (0,-1,2e-16)
  Length = 0.6
  Length2 = 2.4
  Profile = -> Sketch117
  ReferenceAxis = -> Sketch117 [N_Axis]
  Refine = true
  Suppressed = false
  Type = 4
FEATURE [PartDesign::Pad] Pad013
  BaseFeature = -> Pocket007
  Direction = (0,-1,2e-16)
  Length = 1.6
  Length2 = 10
  Profile = -> Sketch118
  ReferenceAxis = -> Sketch118 [N_Axis]
  Refine = true
  Suppressed = false
  Type = 0
FEATURE [Sketcher::SketchObject] Sketch119
  ArcFitTolerance = 1e-06
  AttachmentSupport = -> [Pad013]
  ExternalGeometry = -> [Binder001]
  FullyConstrained = true
  MakeInternals = false
  MapMode = 5
  Placement = pos=(0,-3.6,0) rot=(1,0,0;1.5708rad)
  sketch-geometry (21):
    g0: LineSegment [constr] StartX=-82.8 StartY=3.2 StartZ=0 EndX=-82.8 EndY=39.2 EndZ=0
    g1: ArcOfCircle CenterX=-78.51 CenterY=34.8 CenterZ=0 NormalX=0 NormalY=0 NormalZ=1 AngleXU=0 Radius=3.5 StartAngle=4.71239 EndAngle=6.28319
    g2: ArcOfCircle CenterX=-78.51 CenterY=7.6 CenterZ=0 NormalX=0 NormalY=0 NormalZ=1 AngleXU=0 Radius=3.5 StartAngle=0 EndAngle=1.5708
    g3: ArcOfCircle CenterX=-5.6 CenterY=34.8 CenterZ=0 NormalX=0 NormalY=0 NormalZ=1 AngleXU=0 Radius=3.5 StartAngle=3.14159 EndAngle=4.71239
    g4: ArcOfCircle CenterX=-5.6 CenterY=7.6 CenterZ=0 NormalX=0 NormalY=0 NormalZ=1 AngleXU=0 Radius=3.5 StartAngle=1.5708 EndAngle=3.14159
    g5: LineSegment StartX=0 StartY=39.2 StartZ=0 EndX=0 EndY=31.3 EndZ=0
    g6: LineSegment StartX=0 StartY=39.2 StartZ=0 EndX=-9.1 EndY=39.2 EndZ=0
    g7: LineSegment StartX=0 StartY=3.2 StartZ=0 EndX=0 EndY=11.1 EndZ=0
    g8: LineSegment StartX=0 StartY=3.2 StartZ=0 EndX=-9.1 EndY=3.2 EndZ=0
    g9: LineSegment StartX=-82.8 StartY=3.2 StartZ=0 EndX=-75.01 EndY=3.2 EndZ=0
    g10: LineSegment StartX=-82.8 StartY=3.2 StartZ=0 EndX=-82.8 EndY=11.1 EndZ=0
    g11: LineSegment StartX=-82.8 StartY=39.2 StartZ=0 EndX=-82.8 EndY=31.3 EndZ=0
    g12: LineSegment StartX=-82.8 StartY=39.2 StartZ=0 EndX=-75.01 EndY=39.2 EndZ=0
    g13: LineSegment StartX=-82.8 StartY=31.3 StartZ=0 EndX=-78.51 EndY=31.3 EndZ=0
    g14: LineSegment StartX=-75.01 StartY=39.2 StartZ=0 EndX=-75.01 EndY=34.8 EndZ=0
    g15: LineSegment StartX=-82.8 StartY=11.1 StartZ=0 EndX=-78.51 EndY=11.1 EndZ=0
    g16: LineSegment StartX=-75.01 StartY=3.2 StartZ=0 EndX=-75.01 EndY=7.6 EndZ=0
    g17: LineSegment StartX=-9.1 StartY=39.2 StartZ=0 EndX=-9.1 EndY=34.8 EndZ=0
    g18: LineSegment StartX=0 StartY=31.3 StartZ=0 EndX=-5.6 EndY=31.3 EndZ=0
    g19: LineSegment StartX=0 StartY=11.1 StartZ=0 EndX=-5.6 EndY=11.1 EndZ=0
    g20: LineSegment StartX=-9.1 StartY=3.2 StartZ=0 EndX=-9.1 EndY=7.6 EndZ=0
  constraints (51):
    c: Coincident(g0,g-10)
    c: PointOnObject(g0,g-8)
    c: Vertical(g0)
    c: Coincident(g1,g-3)
    c: Coincident(g2,g-4)
    c: Coincident(g3,g-5)
    c: Coincident(g4,g-6)
    c: Radius(g4) = 3.5
    c: Radius(g3) = 3.5
    c: Radius(g1) = 3.5
    c: Radius(g2) = 3.5
    c: Coincident(g5,g-9)
    c: PointOnObject(g5,g-9)
    c: Coincident(g6,g5)
    c: PointOnObject(g6,g-8)
    c: Coincident(g7,g-9)
    c: PointOnObject(g7,g-9)
    c: Coincident(g8,g7)
    c: PointOnObject(g8,g-7)
    c: Coincident(g9,g0)
    c: PointOnObject(g9,g-7)
    c: Coincident(g10,g0)
    c: PointOnObject(g10,g0)
    c: Coincident(g11,g0)
    c: PointOnObject(g11,g0)
    c: Coincident(g12,g0)
    c: PointOnObject(g12,g-8)
    c: Coincident(g13,g11)
    c: Horizontal(g13)
    c: Coincident(g14,g12)
    c: Vertical(g14)
    c: Coincident(g15,g10)
    c: Horizontal(g15)
    c: Coincident(g16,g9)
    c: Vertical(g16)
    c: Coincident(g17,g6)
    c: Vertical(g17)
    c: Coincident(g18,g5)
    c: Horizontal(g18)
    c: Coincident(g19,g7)
    c: Horizontal(g19)
    c: Coincident(g20,g8)
    c: Vertical(g20)
    c: Tangent(g20,g4) = 1.5708
    c: Tangent(g4,g19) = -1.5708
    c: Tangent(g18,g3) = 1.5708
    c: Tangent(g3,g17) = -1.5708
    c: Tangent(g13,g1) = -1.5708
    c: Tangent(g1,g14) = 1.5708
    c: Tangent(g16,g2) = -1.5708
    c: Tangent(g2,g15) = 1.5708
FEATURE [PartDesign::Pocket] Pocket008
  BaseFeature = -> Pad013
  Direction = (0,1,-2e-16)
  Length = 1.6
  Length2 = 5
  Profile = -> Sketch119
  ReferenceAxis = -> Sketch119 [N_Axis]
  Refine = true
  Suppressed = false
  Type = 0
FEATURE [PartDesign::Pad] Pad017
  BaseFeature = -> Pocket008
  Direction = (0,-1,2e-16)
  Length = 1.6
  Length2 = 10
  Profile = -> Sketch123
  ReferenceAxis = -> Sketch123 [N_Axis]
  Refine = true
  Suppressed = false
  Type = 0
FEATURE [Sketcher::SketchObject] Sketch125
  ArcFitTolerance = 1e-06
  AttachmentSupport = -> [Pad017]
  ExternalGeometry = -> [Pad017]
  FullyConstrained = true
  MakeInternals = false
  MapMode = 5
  Placement = pos=(0,-3.6,8e-16) rot=(1,0,0;1.5708rad)
  sketch-geometry (20):
    g0: LineSegment StartX=-108 StartY=35.8 StartZ=0 EndX=-108 EndY=35 EndZ=0
    g1: LineSegment StartX=-108 StartY=35 StartZ=0 EndX=-97 EndY=35 EndZ=0
    g2: LineSegment StartX=-97 StartY=35 StartZ=0 EndX=-97 EndY=35.8 EndZ=0
    g3: LineSegment StartX=-97 StartY=35.8 StartZ=0 EndX=-108 EndY=35.8 EndZ=0
    g4: LineSegment StartX=-108 StartY=28.6 StartZ=0 EndX=-108 EndY=27.8 EndZ=0
    g5: LineSegment StartX=-108 StartY=27.8 StartZ=0 EndX=-97 EndY=27.8 EndZ=0
    g6: LineSegment StartX=-97 StartY=27.8 StartZ=0 EndX=-97 EndY=28.6 EndZ=0
    g7: LineSegment StartX=-97 StartY=28.6 StartZ=0 EndX=-108 EndY=28.6 EndZ=0
    g8: LineSegment StartX=-108 StartY=30.4 StartZ=0 EndX=-108 EndY=29.6 EndZ=0
    g9: LineSegment StartX=-108 StartY=29.6 StartZ=0 EndX=-97 EndY=29.6 EndZ=0
    g10: LineSegment StartX=-97 StartY=29.6 StartZ=0 EndX=-97 EndY=30.4 EndZ=0
    g11: LineSegment StartX=-97 StartY=30.4 StartZ=0 EndX=-108 EndY=30.4 EndZ=0
    g12: LineSegment StartX=-108 StartY=32.2 StartZ=0 EndX=-108 EndY=31.4 EndZ=0
    g13: LineSegment StartX=-108 StartY=31.4 StartZ=0 EndX=-97 EndY=31.4 EndZ=0
    g14: LineSegment StartX=-97 StartY=31.4 StartZ=0 EndX=-97 EndY=32.2 EndZ=0
    g15: LineSegment StartX=-97 StartY=32.2 StartZ=0 EndX=-108 EndY=32.2 EndZ=0
    g16: LineSegment StartX=-108 StartY=34 StartZ=0 EndX=-108 EndY=33.2 EndZ=0
    g17: LineSegment StartX=-108 StartY=33.2 StartZ=0 EndX=-97 EndY=33.2 EndZ=0
    g18: LineSegment StartX=-97 StartY=33.2 StartZ=0 EndX=-97 EndY=34 EndZ=0
    g19: LineSegment StartX=-97 StartY=34 StartZ=0 EndX=-108 EndY=34 EndZ=0
  constraints (55):
    c: Coincident(g1,g0)
    c: Horizontal(g1)
    c: Coincident(g2,g1)
    c: Vertical(g2)
    c: Coincident(g3,g2)
    c: Horizontal(g3)
    c: Coincident(g3,g0)
    c: DistanceX(g1,g1) = 11
    c: DistanceY(g2,g2) = 0.8
    c: Coincident(g5,g4)
    c: Horizontal(g5)
    c: Coincident(g6,g5)
    c: Vertical(g6)
    c: Coincident(g7,g6)
    c: Horizontal(g7)
    c: Coincident(g7,g4)
    c: Coincident(g9,g8)
    c: Horizontal(g9)
    c: Coincident(g10,g9)
    c: Vertical(g10)
    c: Coincident(g11,g10)
    c: Horizontal(g11)
    c: Coincident(g11,g8)
    c: Coincident(g13,g12)
    c: Horizontal(g13)
    c: Coincident(g14,g13)
    c: Vertical(g14)
    c: Coincident(g15,g14)
    c: Horizontal(g15)
    c: Coincident(g15,g12)
    c: Coincident(g17,g16)
    c: Horizontal(g17)
    c: Coincident(g18,g17)
    c: Vertical(g18)
    c: Coincident(g19,g18)
    c: Horizontal(g19)
    c: Coincident(g19,g16)
    c: Equal(g3,g19)
    c: Equal(g3,g15)
    c: Equal(g3,g11)
    c: Equal(g3,g7)
    c: Equal(g2,g18)
    c: Equal(g2,g14)
    c: Equal(g2,g10)
    c: Equal(g2,g6)
    c: DistanceY(g-4,g4) = 1
    c: DistanceY(g4,g8) = 1
    c: DistanceY(g8,g12) = 1
    c: DistanceY(g12,g16) = 1
    c: DistanceY(g16,g0) = 1
    c: Tangent(g0,g-5)
    c: Tangent(g16,g-5)
    c: Tangent(g12,g-5)
    c: Tangent(g8,g-5)
    c: Tangent(g4,g-5)
FEATURE [PartDesign::Chamfer] Chamfer009
  Angle = 45
  Base = -> Pad017 [Edge151,Edge154]
  BaseFeature = -> Pad017
  ChamferType = 1
  FlipDirection = false
  Refine = true
  Size = 1.5
  Size2 = 2.8
  SupportTransform = false
  Suppressed = false
  UseAllEdges = false
FEATURE [PartDesign::Pocket] Pocket009
  BaseFeature = -> Chamfer009
  Direction = (0,1,-2e-16)
  Length = 1
  Length2 = 5
  Profile = -> Sketch125
  ReferenceAxis = -> Sketch125 [N_Axis]
  Refine = true
  Suppressed = false
  Type = 0
FEATURE [PartDesign::Pad] Pad014
  BaseFeature = -> Pocket009
  Direction = (0,-1,2e-16)
  Length = 0.8
  Length2 = 10
  Profile = -> Sketch120
  ReferenceAxis = -> Sketch120 [N_Axis]
  Refine = true
  Suppressed = false
  Type = 0
FEATURE [Sketcher::SketchObject] Sketch124
  ArcFitTolerance = 1e-06
  AttachmentSupport = -> [Pad014]
  ExternalGeometry = -> [Binder001]
  FullyConstrained = true
  MakeInternals = false
  MapMode = 5
  Placement = pos=(0,-2.8,6e-16) rot=(1,0,0;1.5708rad)
  sketch-geometry (4):
    g0: LineSegment StartX=-129 StartY=39.2 StartZ=0 EndX=-131.599 EndY=31.2 EndZ=0
    g1: LineSegment StartX=-118 StartY=39.2 StartZ=0 EndX=-120.599 EndY=31.2 EndZ=0
    g2: LineSegment StartX=-129 StartY=39.2 StartZ=0 EndX=-118 EndY=39.2 EndZ=0
    g3: LineSegment StartX=-120.599 StartY=31.2 StartZ=0 EndX=-131.599 EndY=31.2 EndZ=0
  constraints (12):
    c: PointOnObject(g0,g-3)
    c: PointOnObject(g1,g-3)
    c: Parallel(g-4,g0)
    c: Parallel(g-4,g1)
    c: Coincident(g2,g0)
    c: Coincident(g2,g1)
    c: DistanceX(g2,g2) = 11
    c: DistanceY(g1,g1) = 8
    c: Coincident(g3,g1)
    c: Horizontal(g3)
    c: Coincident(g3,g0)
    c: DistanceX(g1,g-3) = 118
FEATURE [PartDesign::Pad] Pad018
  BaseFeature = -> Pad014
  Direction = (0,-1,2e-16)
  Length = 1.2
  Length2 = 10
  Profile = -> Sketch124
  ReferenceAxis = -> Sketch124 [N_Axis]
  Refine = true
  Suppressed = false
  Type = 0
FEATURE [Sketcher::SketchObject] Sketch126
  ArcFitTolerance = 1e-06
  AttachmentSupport = -> [Pad018]
  ExternalGeometry = -> [Pad018]
  FullyConstrained = true
  MakeInternals = false
  MapMode = 5
  Placement = pos=(0,-4,0) rot=(1,0,0;1.5708rad)
  sketch-geometry (8):
    g0: LineSegment StartX=-129.877 StartY=36.5 StartZ=0 EndX=-130.137 EndY=35.7 EndZ=0
    g1: LineSegment StartX=-130.69 StartY=34 StartZ=0 EndX=-130.95 EndY=33.2 EndZ=0
    g2: LineSegment StartX=-129.877 StartY=36.5 StartZ=0 EndX=-118.877 EndY=36.5 EndZ=0
    g3: LineSegment StartX=-130.137 StartY=35.7 StartZ=0 EndX=-119.137 EndY=35.7 EndZ=0
    g4: LineSegment StartX=-130.69 StartY=34 StartZ=0 EndX=-119.69 EndY=34 EndZ=0
    g5: LineSegment StartX=-130.95 StartY=33.2 StartZ=0 EndX=-119.95 EndY=33.2 EndZ=0
    g6: LineSegment StartX=-118.877 StartY=36.5 StartZ=0 EndX=-119.137 EndY=35.7 EndZ=0
    g7: LineSegment StartX=-119.69 StartY=34 StartZ=0 EndX=-119.95 EndY=33.2 EndZ=0
  constraints (20):
    c: Coincident(g2,g0)
    c: Horizontal(g2)
    c: Coincident(g3,g0)
    c: Horizontal(g3)
    c: Coincident(g4,g1)
    c: Horizontal(g4)
    c: Coincident(g5,g1)
    c: Horizontal(g5)
    c: Coincident(g6,g2)
    c: Coincident(g6,g3)
    c: Coincident(g7,g4)
    c: Coincident(g7,g5)
    c: Tangent(g0,g-4)
    c: Tangent(g6,g-5)
    c: Tangent(g1,g-4)
    c: Tangent(g7,g-5)
    c: DistanceY(g3,g2) = 0.8
    c: DistanceY(g5,g4) = 0.8
    c: DistanceY(g-6,g1) = 2
    c: DistanceY(g-6,g0) = 4.5
FEATURE [PartDesign::Chamfer] Chamfer008
  Angle = 45
  Base = -> Pad018 [Edge257]
  BaseFeature = -> Pad018
  ChamferType = 1
  FlipDirection = false
  Refine = true
  Size = 1
  Size2 = 6
  SupportTransform = false
  Suppressed = false
  UseAllEdges = false
FEATURE [PartDesign::Pocket] Pocket010
  BaseFeature = -> Chamfer008
  Direction = (0,1,-2e-16)
  Length = 1
  Length2 = 5
  Profile = -> Sketch126
  ReferenceAxis = -> Sketch126 [N_Axis]
  Refine = true
  Suppressed = false
  Type = 0
FEATURE [PartDesign::Pad] Pad015
  BaseFeature = -> Pocket010
  Direction = (0,-1,2e-16)
  Length = 2
  Length2 = 10
  Profile = -> Sketch121
  ReferenceAxis = -> Sketch121 [N_Axis]
  Refine = true
  Suppressed = false
  Type = 0
FEATURE [PartDesign::Pad] Pad016
  BaseFeature = -> Pad015
  Direction = (0,-1,2e-16)
  Length = 1.6
  Length2 = 10
  Profile = -> Sketch122
  ReferenceAxis = -> Sketch122 [N_Axis]
  Refine = true
  Suppressed = false
  Type = 0
FEATURE [Sketcher::SketchObject] Sketch129
  ArcFitTolerance = 1e-06
  AttachmentSupport = -> [Pad016]
  ExternalGeometry = -> [Binder001]
  FullyConstrained = true
  MakeInternals = false
  MapMode = 5
  Placement = pos=(0,-3.6,0) rot=(1,0,0;1.5708rad)
  sketch-geometry (12):
    g0: LineSegment [constr] StartX=-192.176 StartY=-3.18451 StartZ=0 EndX=-181.223 EndY=20.303 EndZ=0
    g1: LineSegment [constr] StartX=-202.765 StartY=20.303 StartZ=0 EndX=-181.223 EndY=20.303 EndZ=0
    g2: LineSegment StartX=-202.765 StartY=20.303 StartZ=0 EndX=-181.223 EndY=20.303 EndZ=0
    g3: LineSegment StartX=-192.176 StartY=-3.18451 StartZ=0 EndX=-196.804 EndY=-13.1107 EndZ=0
    g4: ArcOfCircle CenterX=-207.583 CenterY=4 CenterZ=0 NormalX=0 NormalY=0 NormalZ=1 AngleXU=0 Radius=17 StartAngle=5.84685 EndAngle=7.56663
    g5: ArcOfEllipse CenterX=-181.223 CenterY=8.55923 CenterZ=0 NormalX=0 NormalY=0 NormalZ=1 MajorRadius=23.4779 MinorRadius=11.7437 AngleXU=2e-16 StartAngle=4.71239 EndAngle=7.85398
    g6: LineSegment [constr] StartX=-157.745 StartY=8.55923 StartZ=0 EndX=-204.701 EndY=8.55923 EndZ=0
    g7: LineSegment [constr] StartX=-181.223 StartY=20.303 StartZ=0 EndX=-181.223 EndY=-3.18451 EndZ=0
    g8: GeomPoint [constr] X=-160.894 Y=8.55923 Z=0
    g9: GeomPoint [constr] X=-201.553 Y=8.55923 Z=0
    g10: ArcOfCircle CenterX=-181.223 CenterY=-20.3763 CenterZ=0 NormalX=0 NormalY=0 NormalZ=1 AngleXU=0 Radius=17.1918 StartAngle=1.57079 EndAngle=2.70526
    g11: GeomPoint [constr] X=-181.223 Y=-3.18451 Z=0
  constraints (23):
    c: Coincident(g0,g-5)
    c: Coincident(g1,g-6)
    c: Horizontal(g1)
    c: Coincident(g1,g0)
    c: Parallel(g0,g-4)
    c: Coincident(g2,g1)
    c: Coincident(g2,g0)
    c: Coincident(g3,g0)
    c: Equal(g4,g-5)
    c: Coincident(g4,g1)
    c: Coincident(g4,g0)
    c: InternalAlignment(g6-g9 -> g5) x4
    c: Vertical(g5,g0)
    c: Horizontal(g6)
    c: Coincident(g5,g0)
    c: DistanceX(g6,g-3) = 10.1
    c: Tangent(g10,g3) = -1.5708
    c: PointOnObject(g11,g10)
    c: Tangent(g5,g10,g11) = 1.5708
    c: Coincident(g10,g5)
    c: Coincident(g11,g7)
    c: Parallel(g3,g-4)
    c: Horizontal(g5,g0)
FEATURE [Sketcher::SketchObject] Sketch130
  ArcFitTolerance = 1e-06
  AttachmentOffset = pos=(0,0,-1.6) rot=(0,0,1;0rad)
  AttachmentSupport = -> [Pad016]
  ExternalGeometry = -> [Binder001]
  FullyConstrained = true
  MakeInternals = false
  MapMode = 5
  Placement = pos=(0,-2,-4e-16) rot=(1,0,0;1.5708rad)
  sketch-geometry (12):
    g0: LineSegment [constr] StartX=-192.176 StartY=-3.18451 StartZ=0 EndX=-181.223 EndY=20.303 EndZ=0
    g1: LineSegment [constr] StartX=-202.765 StartY=20.303 StartZ=0 EndX=-181.223 EndY=20.303 EndZ=0
    g2: LineSegment StartX=-202.765 StartY=20.303 StartZ=0 EndX=-181.223 EndY=20.303 EndZ=0
    g3: LineSegment StartX=-192.176 StartY=-3.18451 StartZ=0 EndX=-193.827 EndY=-6.72678 EndZ=0
    g4: ArcOfCircle CenterX=-207.583 CenterY=4 CenterZ=0 NormalX=0 NormalY=0 NormalZ=1 AngleXU=0 Radius=17 StartAngle=5.84685 EndAngle=7.56663
    g5: ArcOfEllipse CenterX=-181.223 CenterY=10.803 CenterZ=0 NormalX=0 NormalY=0 NormalZ=1 MajorRadius=14.4779 MinorRadius=9.5 AngleXU=0 StartAngle=4.71239 EndAngle=7.85398
    g6: LineSegment [constr] StartX=-166.745 StartY=10.803 StartZ=0 EndX=-195.701 EndY=10.803 EndZ=0
    g7: LineSegment [constr] StartX=-181.223 StartY=20.303 StartZ=0 EndX=-181.223 EndY=1.30297 EndZ=0
    g8: GeomPoint [constr] X=-170.298 Y=10.803 Z=0
    g9: GeomPoint [constr] X=-192.148 Y=10.803 Z=0
    g10: ArcOfCircle CenterX=-181.223 CenterY=-12.6042 CenterZ=0 NormalX=0 NormalY=0 NormalZ=1 AngleXU=0 Radius=13.9072 StartAngle=1.5708 EndAngle=2.70526
    g11: GeomPoint [constr] X=-181.223 Y=1.30297 Z=0
  constraints (23):
    c: Coincident(g0,g-5)
    c: Coincident(g1,g-6)
    c: Horizontal(g1)
    c: Coincident(g1,g0)
    c: Parallel(g0,g-4)
    c: Coincident(g2,g1)
    c: Coincident(g2,g0)
    c: Coincident(g3,g0)
    c: Equal(g4,g-5)
    c: Coincident(g4,g1)
    c: Coincident(g4,g0)
    c: InternalAlignment(g6-g9 -> g5) x4
    c: Vertical(g5,g0)
    c: Horizontal(g6)
    c: Coincident(g5,g0)
    c: DistanceX(g6,g-3) = 19.1
    c: Tangent(g10,g3) = -1.5708
    c: PointOnObject(g11,g10)
    c: Tangent(g5,g10,g11) = 1.5708
    c: Coincident(g10,g5)
    c: Coincident(g11,g7)
    c: Parallel(g3,g-4)
    c: DistanceY(g5,g0) = 19
FEATURE [Part::Part2DObjectPython] Clone2D001  label="Sketch130 (2D)"  # Draft 2D object (typed FeaturePython)
  Fuse = false
  Objects = -> [Sketch130]
  Placement = pos=(0,-2,-4e-16) rot=(1,0,0;1.5708rad)
  Scale = (1,1,1)
FEATURE [Sketcher::SketchObject] Sketch131
  ArcFitTolerance = 1e-06
  AttachmentOffset = pos=(0,0,-3.5) rot=(0,0,1;0rad)
  AttachmentSupport = -> [Pad016]
  ExternalGeometry = -> [Binder001]
  FullyConstrained = true
  MakeInternals = false
  MapMode = 5
  Placement = pos=(0,-0.1,-8e-16) rot=(1,0,0;1.5708rad)
  sketch-geometry (1):
    g0: GeomPoint X=-197.47 Y=8.55923 Z=0
  constraints (1):
    c: Symmetric(g-6,g-4,g0)
FEATURE [Sketcher::SketchObject] Sketch132
  ArcFitTolerance = 1e-06
  AttachmentSupport = -> [Pad016]
  ExternalGeometry = -> [Binder001]
  FullyConstrained = true
  MakeInternals = false
  MapMode = 5
  Placement = pos=(0,-3.6,0) rot=(1,0,0;1.5708rad)
  sketch-geometry (3):
    g0: LineSegment [constr] StartX=-215.42 StartY=-53.0314 StartZ=0 EndX=-167.782 EndY=-53.0314 EndZ=0
    g1: Circle CenterX=-191.282 CenterY=-53.0314 CenterZ=0 NormalX=0 NormalY=0 NormalZ=1 AngleXU=0 Radius=11.5
    g2: Circle CenterX=-191.282 CenterY=-53.0314 CenterZ=0 NormalX=0 NormalY=0 NormalZ=1 AngleXU=0 Radius=10.7
  constraints (8):
    c: Coincident(g0,g-3)
    c: PointOnObject(g0,g-4)
    c: Horizontal(g0)
    c: Diameter(g1) = 23
    c: PointOnObject(g1,g0)
    c: DistanceX(g1,g0) = 23.5
    c: Diameter(g2) = 21.4
    c: Coincident(g2,g1)
FEATURE [Part::Part2DObjectPython] ShapeString  # Draft 2D object (typed FeaturePython)
  FontFile = <path>
  Fuse = false
  Justification = 6
  JustificationReference = 0
  KeepLeftMargin = false
  MakeFace = true
  ObliqueAngle = 0
  Placement = pos=(-199,-3.6,-57.5) rot=(1,0,0;1.5708rad)
  ScaleToSize = true
  Size = 10
  String = AS
  Tracking = 0
FEATURE [Sketcher::SketchObject] Sketch133
  ArcFitTolerance = 1e-06
  AttachmentSupport = -> [Binder]
  ExternalGeometry = -> [Binder]
  FullyConstrained = true
  MakeInternals = false
  MapMode = 5
  Placement = pos=(0,9e-16,0) rot=(0,0.707107,0.707107;3.14159rad)
  sketch-geometry (30):
    g0: LineSegment StartX=0 StartY=39.2 StartZ=0 EndX=0 EndY=3.2 EndZ=0
    g1: LineSegment StartX=0 StartY=3.2 StartZ=0 EndX=82.8 EndY=3.2 EndZ=0
    g2: LineSegment StartX=82.8 StartY=3.2 StartZ=0 EndX=82.8 EndY=6.2 EndZ=0
    g3: LineSegment StartX=82.8 StartY=6.2 StartZ=0 EndX=91.752 EndY=6.2 EndZ=0
    g4: LineSegment StartX=0 StartY=39.2 StartZ=0 EndX=195.887 EndY=39.2 EndZ=0
    g5: LineSegment StartX=195.887 StartY=39.2 StartZ=0 EndX=202.765 EndY=20.303 EndZ=0
    g6: LineSegment StartX=192.333 StartY=24.9893 StartZ=0 EndX=196.467 EndY=26.4942 EndZ=0
    g7: LineSegment StartX=196.467 StartY=26.4942 StartZ=0 EndX=194.073 EndY=33.0721 EndZ=0
    g8: LineSegment StartX=194.073 StartY=33.0721 StartZ=0 EndX=189.939 EndY=31.5672 EndZ=0
    g9: LineSegment StartX=189.939 StartY=31.5672 StartZ=0 EndX=192.333 EndY=24.9893 EndZ=0
    g10: ArcOfCircle CenterX=107.6 CenterY=4 CenterZ=0 NormalX=0 NormalY=0 NormalZ=1 AngleXU=0 Radius=16 StartAngle=1.5708 EndAngle=3.00366
    g11: LineSegment StartX=107.6 StartY=20 StartZ=0 EndX=132.428 EndY=20 EndZ=0
    g12: ArcOfCircle [constr] CenterX=132.428 CenterY=4 CenterZ=0 NormalX=0 NormalY=0 NormalZ=1 AngleXU=0 Radius=16 StartAngle=0.314159 EndAngle=1.5708
    g13: LineSegment StartX=147.645 StartY=8.94427 StartZ=0 EndX=176.685 EndY=-80.4316 EndZ=0
    g14: LineSegment StartX=176.685 StartY=-80.4316 StartZ=0 EndX=215.932 EndY=-80.4316 EndZ=0
    g15: ArcOfCircle CenterX=207.583 CenterY=4 CenterZ=0 NormalX=0 NormalY=0 NormalZ=1 AngleXU=0 Radius=17 StartAngle=1.85815 EndAngle=3.57792
    g16: ArcOfCircle CenterX=184.801 CenterY=-67.3089 CenterZ=0 NormalX=0 NormalY=0 NormalZ=1 AngleXU=0 Radius=33.7833 StartAngle=5.88425 EndAngle=6.71952
    g17: LineSegment StartX=192.176 StartY=-3.18451 StartZ=0 EndX=215.42 EndY=-53.0314 EndZ=0
    g18: Circle CenterX=5.6 CenterY=34.8 CenterZ=0 NormalX=0 NormalY=0 NormalZ=1 AngleXU=0 Radius=1.8
    g19: Circle CenterX=5.6 CenterY=7.6 CenterZ=0 NormalX=0 NormalY=0 NormalZ=1 AngleXU=0 Radius=1.8
    g20: Circle CenterX=78.51 CenterY=34.8 CenterZ=0 NormalX=0 NormalY=0 NormalZ=1 AngleXU=0 Radius=1.8
    g21: Circle CenterX=78.51 CenterY=7.6 CenterZ=0 NormalX=0 NormalY=0 NormalZ=1 AngleXU=0 Radius=1.8
    g22: Circle CenterX=184.08 CenterY=34.8 CenterZ=0 NormalX=0 NormalY=0 NormalZ=1 AngleXU=0 Radius=1.8
    g23: Circle CenterX=179.305 CenterY=-76.8316 CenterZ=0 NormalX=0 NormalY=0 NormalZ=1 AngleXU=0 Radius=1.8
    g24: Circle CenterX=213.443 CenterY=-76.8316 CenterZ=0 NormalX=0 NormalY=0 NormalZ=1 AngleXU=0 Radius=1.8
    g25: Circle CenterX=19 CenterY=21.2 CenterZ=0 NormalX=0 NormalY=0 NormalZ=1 AngleXU=0 Radius=6.3
    g26: Circle CenterX=42 CenterY=21.2 CenterZ=0 NormalX=0 NormalY=0 NormalZ=1 AngleXU=0 Radius=6.3
    g27: Circle CenterX=65 CenterY=21.2 CenterZ=0 NormalX=0 NormalY=0 NormalZ=1 AngleXU=0 Radius=6.3
    g28: LineSegment StartX=132.428 StartY=20 StartZ=0 EndX=144.053 EndY=20 EndZ=0
    g29: LineSegment StartX=147.645 StartY=8.94427 StartZ=0 EndX=144.053 EndY=20 EndZ=0
  constraints (65):
    c: Coincident(g0,g-4)
    c: Coincident(g0,g-5)
    c: Coincident(g1,g0)
    c: Coincident(g1,g-6)
    c: Coincident(g2,g1)
    c: Coincident(g2,g-7)
    c: Coincident(g3,g2)
    c: Coincident(g3,g-8)
    c: Coincident(g4,g0)
    c: Coincident(g4,g-16)
    c: Coincident(g5,g4)
    c: Coincident(g5,g-16)
    c: Coincident(g6,g-20)
    c: Coincident(g6,g-21)
    c: Coincident(g7,g6)
    c: Coincident(g7,g-23)
    c: Coincident(g8,g7)
    c: Coincident(g8,g-22)
    c: Coincident(g9,g8)
    c: Coincident(g9,g6)
    c: Equal(g10,g-8)
    c: Coincident(g10,g3)
    c: Coincident(g10,g-9)
    c: Coincident(g11,g10)
    c: Coincident(g11,g-10)
    c: Equal(g12,g-10)
    c: Coincident(g12,g11)
    c: Coincident(g12,g-11)
    c: Coincident(g13,g12)
    c: Coincident(g13,g-12)
    c: Coincident(g14,g13)
    c: Coincident(g14,g-13)
    c: Equal(g15,g-15)
    c: Coincident(g15,g5)
    c: Coincident(g15,g-15)
    c: Equal(g16,g-13)
    c: Coincident(g16,g14)
    c: Coincident(g16,g-14)
    c: Coincident(g17,g15)
    c: Coincident(g17,g16)
    c: Equal(g18,g-28)
    c: Equal(g19,g-29)
    c: Equal(g20,g-26)
    c: Equal(g21,g-27)
    c: Equal(g22,g-17)
    c: Equal(g24,g-25)
    c: Equal(g23,g-24)
    c: Coincident(g23,g-24)
    c: Coincident(g24,g-25)
    c: Coincident(g22,g-17)
    c: Coincident(g20,g-26)
    c: Coincident(g21,g-27)
    c: Coincident(g18,g-28)
    c: Coincident(g19,g-29)
    c: Equal(g25,g-30)
    c: Equal(g26,g-31)
    c: Equal(g27,g-32)
    c: Coincident(g25,g-30)
    c: Coincident(g26,g-31)
    c: Coincident(g27,g-32)
    c: Parallel(g28,g11)
    c: Parallel(g29,g13)
    c: Coincident(g28,g11)
    c: Coincident(g29,g12)
    c: Coincident(g29,g28)
FEATURE [PartDesign::Pad] Pad019
  Direction = (0,1,-2e-16)
  Length = 2
  Length2 = 10
  Profile = -> Sketch133
  ReferenceAxis = -> Sketch133 [N_Axis]
  Refine = true
  Suppressed = false
  Type = 0
FEATURE [Sketcher::SketchObject] Sketch091  label="Sketch091 - forma anteriore"
  ArcFitTolerance = 1e-06
  AttachmentSupport = -> [Pad019]
  ExternalGeometry = -> [Binder]
  FullyConstrained = true
  MakeInternals = false
  MapMode = 5
  Placement = pos=(0,2,0) rot=(0,0.707107,0.707107;3.14159rad)
  sketch-geometry (12):
    g0: Circle CenterX=5.6 CenterY=34.8 CenterZ=0 NormalX=0 NormalY=0 NormalZ=1 AngleXU=0 Radius=1.8
    g1: Circle CenterX=5.6 CenterY=7.6 CenterZ=0 NormalX=0 NormalY=0 NormalZ=1 AngleXU=0 Radius=1.8
    g2: Circle CenterX=78.51 CenterY=34.8 CenterZ=0 NormalX=0 NormalY=0 NormalZ=1 AngleXU=0 Radius=1.8
    g3: Circle CenterX=78.51 CenterY=7.6 CenterZ=0 NormalX=0 NormalY=0 NormalZ=1 AngleXU=0 Radius=1.8
    g4: LineSegment StartX=0 StartY=39.2 StartZ=0 EndX=0 EndY=3.2 EndZ=0
    g5: LineSegment StartX=0 StartY=3.2 StartZ=0 EndX=82.8 EndY=3.2 EndZ=0
    g6: LineSegment StartX=82.8 StartY=3.2 StartZ=0 EndX=82.8 EndY=39.2 EndZ=0
    g7: LineSegment StartX=82.8 StartY=39.2 StartZ=0 EndX=0 EndY=39.2 EndZ=0
    g8: ArcOfCircle CenterX=19 CenterY=21.2 CenterZ=0 NormalX=0 NormalY=0 NormalZ=1 AngleXU=0 Radius=10 StartAngle=1.5708 EndAngle=4.71239
    g9: ArcOfCircle CenterX=65 CenterY=21.2 CenterZ=0 NormalX=0 NormalY=0 NormalZ=1 AngleXU=0 Radius=10 StartAngle=4.71239 EndAngle=7.85398
    g10: LineSegment StartX=19 StartY=31.2 StartZ=0 EndX=65 EndY=31.2 EndZ=0
    g11: LineSegment StartX=19 StartY=11.2 StartZ=0 EndX=65 EndY=11.2 EndZ=0
  constraints (25):
    c: Equal(g2,g-7)
    c: Equal(g3,g-8)
    c: Equal(g1,g-13)
    c: Equal(g0,g-12)
    c: Coincident(g0,g-12)
    c: Coincident(g1,g-13)
    c: Coincident(g3,g-8)
    c: Coincident(g2,g-7)
    c: Coincident(g4,g-4)
    c: Coincident(g4,g-5)
    c: Coincident(g5,g4)
    c: Coincident(g5,g-6)
    c: Coincident(g6,g5)
    c: PointOnObject(g6,g-3)
    c: Vertical(g6)
    c: Coincident(g7,g6)
    c: Coincident(g7,g4)
    c: Tangent(g8,g10) = 1.5708
    c: Tangent(g8,g11) = -1.5708
    c: Tangent(g9,g10) = 1.5708
    c: Tangent(g9,g11) = -1.5708
    c: Equal(g8,g9)
    c: Radius(g8) = 10
    c: Coincident(g8,g-11)
    c: Coincident(g9,g-9)
FEATURE [Sketcher::SketchObject] Sketch093  label="Sketch093 - scavi interni pulsanti"
  ArcFitTolerance = 1e-06
  AttachmentSupport = -> [Pad019]
  ExternalGeometry = -> [Binder]
  FullyConstrained = true
  MakeInternals = false
  MapMode = 5
  Placement = pos=(0,1.8e-15,0) rot=(1,0,0;1.5708rad)
  sketch-geometry (3):
    g0: Circle CenterX=-65 CenterY=21.2 CenterZ=0 NormalX=0 NormalY=0 NormalZ=1 AngleXU=0 Radius=7.3
    g1: Circle CenterX=-42 CenterY=21.2 CenterZ=0 NormalX=0 NormalY=0 NormalZ=1 AngleXU=0 Radius=7.3
    g2: Circle CenterX=-19 CenterY=21.2 CenterZ=0 NormalX=0 NormalY=0 NormalZ=1 AngleXU=0 Radius=7.3
  constraints (6):
    c: Coincident(g0,g-3)
    c: Coincident(g1,g-4)
    c: Coincident(g2,g-5)
    c: Diameter(g0) = 14.6
    c: Diameter(g1) = 14.6
    c: Diameter(g2) = 14.6
FEATURE [Sketcher::SketchObject] Sketch094  label="Sketch094 - forma centrale"
  ArcFitTolerance = 1e-06
  AttachmentSupport = -> [Pad019]
  ExternalGeometry = -> [Binder]
  FullyConstrained = true
  MakeInternals = false
  MapMode = 5
  Placement = pos=(0,2,0) rot=(0,0.707107,0.707107;3.14159rad)
  sketch-geometry (4):
    g0: LineSegment StartX=137.815 StartY=39.2 StartZ=0 EndX=142.655 EndY=24.303 EndZ=0
    g1: LineSegment StartX=110.815 StartY=24.303 StartZ=0 EndX=142.655 EndY=24.303 EndZ=0
    g2: LineSegment StartX=137.815 StartY=39.2 StartZ=0 EndX=110.815 EndY=39.2 EndZ=0
    g3: ArcOfCircle CenterX=92.2534 CenterY=31.7515 CenterZ=0 NormalX=0 NormalY=0 NormalZ=1 AngleXU=0 Radius=20 StartAngle=5.90156 EndAngle=6.66481
  constraints (12):
    c: PointOnObject(g0,g-3)
    c: Tangent(g0,g-5)
    c: Horizontal(g1)
    c: Coincident(g1,g0)
    c: Coincident(g2,g0)
    c: PointOnObject(g2,g-3)
    c: DistanceX(g2,g2) = 27
    c: Vertical(g1,g2)
    c: Coincident(g3,g2)
    c: Radius(g3) = 20
    c: Coincident(g3,g1)
    c: DistanceY(g-6,g0) = 4
FEATURE [Sketcher::SketchObject] Sketch095  label="Sketch095 - forma posteriore"
  ArcFitTolerance = 1e-06
  AttachmentSupport = -> [Pad019]
  ExternalGeometry = -> [Binder]
  FullyConstrained = true
  MakeInternals = false
  MapMode = 5
  Placement = pos=(0,2,0) rot=(0,0.707107,0.707107;3.14159rad)
  sketch-geometry (15):
    g0: LineSegment StartX=137.815 StartY=39.2 StartZ=0 EndX=143.955 EndY=20.303 EndZ=0
    g1: LineSegment StartX=143.955 StartY=20.303 StartZ=0 EndX=190.141 EndY=20.303 EndZ=0
    g2: ArcOfCircle CenterX=184.08 CenterY=34.8 CenterZ=0 NormalX=0 NormalY=0 NormalZ=1 AngleXU=0 Radius=3.5 StartAngle=3.49066 EndAngle=4.71239
    g3: LineSegment StartX=180.791 StartY=33.6029 StartZ=0 EndX=178.754 EndY=39.2 EndZ=0
    g4: LineSegment StartX=184.08 StartY=31.3 StartZ=0 EndX=186.139 EndY=31.3 EndZ=0
    g5: LineSegment StartX=190.141 StartY=20.303 StartZ=0 EndX=186.139 EndY=31.3 EndZ=0
    g6: LineSegment StartX=137.815 StartY=39.2 StartZ=0 EndX=156.815 EndY=39.2 EndZ=0
    g7: LineSegment StartX=178.754 StartY=39.2 StartZ=0 EndX=168.815 EndY=39.2 EndZ=0
    g8: LineSegment StartX=156.815 StartY=31.2 StartZ=0 EndX=168.815 EndY=31.2 EndZ=0
    g9: ArcOfCircle CenterX=176.411 CenterY=35.2 CenterZ=0 NormalX=0 NormalY=0 NormalZ=1 AngleXU=0 Radius=20 StartAngle=2.94023 EndAngle=3.34295
    g10: ArcOfCircle CenterX=188.411 CenterY=35.2 CenterZ=0 NormalX=0 NormalY=0 NormalZ=1 AngleXU=0 Radius=20 StartAngle=2.94023 EndAngle=3.34295
    g11: LineSegment StartX=157.815 StartY=39.2 StartZ=0 EndX=167.815 EndY=39.2 EndZ=0
    g12: LineSegment StartX=157.436 StartY=36.2 StartZ=0 EndX=167.436 EndY=36.2 EndZ=0
    g13: ArcOfCircle CenterX=177.411 CenterY=35.2 CenterZ=0 NormalX=0 NormalY=0 NormalZ=1 AngleXU=0 Radius=20 StartAngle=2.94023 EndAngle=3.09157
    g14: ArcOfCircle CenterX=187.411 CenterY=35.2 CenterZ=0 NormalX=0 NormalY=0 NormalZ=1 AngleXU=0 Radius=20 StartAngle=2.94023 EndAngle=3.09157
  constraints (46):
    c: PointOnObject(g0,g-3)
    c: Tangent(g0,g-6)
    c: Coincident(g1,g0)
    c: Horizontal(g1)
    c: Radius(g2) = 3.5
    c: Coincident(g2,g-5)
    c: PointOnObject(g3,g-3)
    c: Parallel(g3,g-4)
    c: Tangent(g3,g2) = 1.5708
    c: Horizontal(g4)
    c: Tangent(g4,g2) = -1.5708
    c: Coincident(g5,g1)
    c: Parallel(g5,g-4)
    c: Coincident(g5,g4)
    c: DistanceX(g4,g-8) = 3.8
    c: Coincident(g6,g0)
    c: PointOnObject(g6,g-3)
    c: Coincident(g7,g3)
    c: PointOnObject(g7,g-3)
    c: Horizontal(g8)
    c: DistanceX(g6,g7) = 12
    c: Vertical(g8,g6)
    c: Vertical(g7,g8)
    c: DistanceY(g8,g6) = 8
    c: Coincident(g9,g8)
    c: Coincident(g9,g6)
    c: Coincident(g10,g7)
    c: Coincident(g10,g8)
    c: Radius(g9) = 20
    c: Radius(g10) = 20
    c: PointOnObject(g11,g-3)
    c: PointOnObject(g11,g-3)
    c: DistanceX(g11,g11) = 10
    c: DistanceX(g6,g11) = 1
    c: Horizontal(g12)
    c: Equal(g12,g11)
    c: DistanceY(g12,g11) = 3
    c: Coincident(g13,g11)
    c: Coincident(g13,g12)
    c: Radius(g13) = 20
    c: Coincident(g14,g11)
    c: Coincident(g14,g12)
    c: Radius(g14) = 20
    c: DistanceX(g0,g6) = 19
    c: Horizontal(g9,g13)
    c: Horizontal(g0,g-4)
FEATURE [Sketcher::SketchObject] Sketch096  label="Sketch096 - forma impugnatura"
  ArcFitTolerance = 1e-06
  AttachmentSupport = -> [Pad019]
  ExternalGeometry = -> [Binder]
  FullyConstrained = true
  MakeInternals = false
  MapMode = 5
  Placement = pos=(0,2,0) rot=(0,0.707107,0.707107;3.14159rad)
  sketch-geometry (8):
    g0: LineSegment StartX=176.685 StartY=-80.4316 StartZ=0 EndX=143.955 EndY=20.303 EndZ=0
    g1: LineSegment StartX=176.685 StartY=-80.4316 StartZ=0 EndX=215.932 EndY=-80.4316 EndZ=0
    g2: Circle CenterX=179.305 CenterY=-76.8316 CenterZ=0 NormalX=0 NormalY=0 NormalZ=1 AngleXU=0 Radius=3
    g3: Circle CenterX=213.443 CenterY=-76.8316 CenterZ=0 NormalX=0 NormalY=0 NormalZ=1 AngleXU=0 Radius=3
    g4: LineSegment StartX=143.955 StartY=20.303 StartZ=0 EndX=202.765 EndY=20.303 EndZ=0
    g5: LineSegment StartX=215.42 StartY=-53.0314 StartZ=0 EndX=192.176 EndY=-3.18451 EndZ=0
    g6: ArcOfCircle CenterX=184.801 CenterY=-67.3089 CenterZ=0 NormalX=0 NormalY=0 NormalZ=1 AngleXU=0 Radius=33.7833 StartAngle=5.88425 EndAngle=6.71952
    g7: ArcOfCircle CenterX=207.583 CenterY=4 CenterZ=0 NormalX=0 NormalY=0 NormalZ=1 AngleXU=0 Radius=17 StartAngle=1.85815 EndAngle=3.57792
  constraints (19):
    c: Coincident(g0,g-4)
    c: PointOnObject(g0,g-3)
    c: Horizontal(g0,g-7)
    c: Coincident(g1,g0)
    c: Coincident(g1,g-5)
    c: Diameter(g2) = 6
    c: Diameter(g3) = 6
    c: Coincident(g2,g-9)
    c: Coincident(g3,g-10)
    c: Coincident(g4,g0)
    c: Coincident(g5,g-6)
    c: Coincident(g6,g1)
    c: Coincident(g6,g5)
    c: Equal(g-5,g6)
    c: Coincident(g5,g-7)
    c: Coincident(g4,g-7)
    c: Tangent(g7,g-7)
    c: Coincident(g7,g4)
    c: Coincident(g7,g5)
FEATURE [Sketcher::SketchObject] Sketch097
  ArcFitTolerance = 1e-06
  AttachmentSupport = -> [Pad019]
  ExternalGeometry = -> [Binder]
  FullyConstrained = true
  MakeInternals = false
  MapMode = 5
  Placement = pos=(0,2,0) rot=(0,0.707107,0.707107;3.14159rad)
  sketch-geometry (4):
    g0: LineSegment StartX=90 StartY=36.8 StartZ=0 EndX=108 EndY=36.8 EndZ=0
    g1: LineSegment StartX=108 StartY=36.8 StartZ=0 EndX=108 EndY=26.8 EndZ=0
    g2: LineSegment StartX=108 StartY=26.8 StartZ=0 EndX=90 EndY=26.8 EndZ=0
    g3: ArcOfCircle CenterX=94 CenterY=31.8 CenterZ=0 NormalX=0 NormalY=0 NormalZ=1 AngleXU=0 Radius=6.40312 StartAngle=2.24554 EndAngle=4.03765
  constraints (13):
    c: Horizontal(g0)
    c: Coincident(g1,g0)
    c: Vertical(g1)
    c: DistanceX(g0,g0) = 18
    c: DistanceY(g1,g1) = 10
    c: Coincident(g2,g1)
    c: Horizontal(g2)
    c: Equal(g2,g0)
    c: DistanceY(g0,g-3) = 2.4
    c: Coincident(g3,g0)
    c: Coincident(g3,g2)
    c: DistanceX(g2,g3) = 4
    c: DistanceX(g-3,g0) = 90
FEATURE [PartDesign::Chamfer] Chamfer015
  Angle = 45
  Base = -> Pad019 [Edge19,Edge22,Edge79]
  BaseFeature = -> Pad019
  ChamferType = 0
  FlipDirection = false
  Refine = true
  Size = 1.9
  Size2 = 1
  SupportTransform = false
  Suppressed = false
  UseAllEdges = false
FEATURE [PartDesign::Pocket] Pocket002
  BaseFeature = -> Chamfer015
  Direction = (0,1,-2e-16)
  Length = 1.2
  Length2 = 5
  Profile = -> Sketch093
  ReferenceAxis = -> Sketch093 [N_Axis]
  Refine = true
  Suppressed = false
  Type = 0
FEATURE [PartDesign::Pad] Pad005
  BaseFeature = -> Pocket002
  Direction = (0,1,-2e-16)
  Length = 1.6
  Length2 = 10
  Profile = -> Sketch091
  ReferenceAxis = -> Sketch091 [N_Axis]
  Refine = true
  Suppressed = false
  Type = 0
FEATURE [Sketcher::SketchObject] Sketch092  label="Sketch092 - scavi per viti anteriori"
  ArcFitTolerance = 1e-06
  AttachmentSupport = -> [Pad005]
  ExternalGeometry = -> [Binder]
  FullyConstrained = true
  MakeInternals = false
  MapMode = 5
  Placement = pos=(0,3.6,0) rot=(0,0.707107,0.707107;3.14159rad)
  sketch-geometry (20):
    g0: ArcOfCircle CenterX=5.6 CenterY=7.6 CenterZ=0 NormalX=0 NormalY=0 NormalZ=1 AngleXU=0 Radius=3.5 StartAngle=0 EndAngle=1.5708
    g1: ArcOfCircle CenterX=5.6 CenterY=34.8 CenterZ=0 NormalX=0 NormalY=0 NormalZ=1 AngleXU=0 Radius=3.5 StartAngle=4.71239 EndAngle=6.28319
    g2: ArcOfCircle CenterX=78.51 CenterY=34.8 CenterZ=0 NormalX=0 NormalY=0 NormalZ=1 AngleXU=0 Radius=3.5 StartAngle=3.14159 EndAngle=4.71239
    g3: ArcOfCircle CenterX=78.51 CenterY=7.6 CenterZ=0 NormalX=0 NormalY=0 NormalZ=1 AngleXU=0 Radius=3.5 StartAngle=1.5708 EndAngle=3.14159
    g4: LineSegment StartX=0 StartY=3.2 StartZ=0 EndX=0 EndY=11.1 EndZ=0
    g5: LineSegment StartX=0 StartY=11.1 StartZ=0 EndX=5.6 EndY=11.1 EndZ=0
    g6: LineSegment StartX=0 StartY=3.2 StartZ=0 EndX=9.1 EndY=3.2 EndZ=0
    g7: LineSegment StartX=9.1 StartY=3.2 StartZ=0 EndX=9.1 EndY=7.6 EndZ=0
    g8: LineSegment StartX=0 StartY=39.2 StartZ=0 EndX=0 EndY=31.3 EndZ=0
    g9: LineSegment StartX=0 StartY=31.3 StartZ=0 EndX=5.6 EndY=31.3 EndZ=0
    g10: LineSegment StartX=0 StartY=39.2 StartZ=0 EndX=9.1 EndY=39.2 EndZ=0
    g11: LineSegment StartX=9.1 StartY=39.2 StartZ=0 EndX=9.1 EndY=34.8 EndZ=0
    g12: LineSegment StartX=82.8 StartY=39.2 StartZ=0 EndX=75.01 EndY=39.2 EndZ=0
    g13: LineSegment StartX=82.8 StartY=39.2 StartZ=0 EndX=82.8 EndY=31.3 EndZ=0
    g14: LineSegment StartX=82.8 StartY=31.3 StartZ=0 EndX=78.51 EndY=31.3 EndZ=0
    g15: LineSegment StartX=82.8 StartY=3.2 StartZ=0 EndX=75.01 EndY=3.2 EndZ=0
    g16: LineSegment StartX=75.01 StartY=3.2 StartZ=0 EndX=75.01 EndY=7.6 EndZ=0
    g17: LineSegment StartX=82.8 StartY=3.2 StartZ=0 EndX=82.8 EndY=11.1 EndZ=0
    g18: LineSegment StartX=82.8 StartY=11.1 StartZ=0 EndX=78.51 EndY=11.1 EndZ=0
    g19: LineSegment StartX=75.01 StartY=39.2 StartZ=0 EndX=75.01 EndY=34.8 EndZ=0
  constraints (48):
    c: Radius(g0) = 3.5
    c: Coincident(g0,g-10)
    c: Radius(g1) = 3.5
    c: Coincident(g1,g-9)
    c: Radius(g2) = 3.5
    c: Coincident(g2,g-8)
    c: Radius(g3) = 3.5
    c: Coincident(g3,g-7)
    c: Coincident(g4,g-5)
    c: PointOnObject(g4,g-4)
    c: Coincident(g5,g4)
    c: Horizontal(g5)
    c: Coincident(g6,g4)
    c: PointOnObject(g6,g-5)
    c: Coincident(g7,g6)
    c: Vertical(g7)
    c: Coincident(g8,g-4)
    c: PointOnObject(g8,g-4)
    c: Coincident(g9,g8)
    c: Horizontal(g9)
    c: Coincident(g10,g8)
    c: PointOnObject(g10,g-3)
    c: Coincident(g11,g10)
    c: Vertical(g11)
    c: PointOnObject(g12,g-3)
    c: PointOnObject(g12,g-3)
    c: Coincident(g13,g12)
    c: Vertical(g13)
    c: Coincident(g14,g13)
    c: Horizontal(g14)
    c: Coincident(g15,g-6)
    c: PointOnObject(g15,g-5)
    c: Coincident(g16,g15)
    c: Vertical(g16)
    c: Coincident(g17,g15)
    c: Coincident(g18,g17)
    c: Horizontal(g18)
    c: Tangent(g3,g18) = -1.5708
    c: Tangent(g16,g3) = 1.5708
    c: Coincident(g19,g12)
    c: Vertical(g19)
    c: Tangent(g2,g19) = -1.5708
    c: Tangent(g2,g14) = 1.5708
    c: Tangent(g0,g7) = -1.5708
    c: Tangent(g0,g5) = 1.5708
    c: Tangent(g9,g1) = -1.5708
    c: Tangent(g1,g11) = 1.5708
    c: Tangent(g17,g13)
FEATURE [PartDesign::Pocket] Pocket001
  BaseFeature = -> Pad005
  Direction = (0,-1,2e-16)
  Length = 1.6
  Length2 = 5
  Profile = -> Sketch092
  ReferenceAxis = -> Sketch092 [N_Axis]
  Refine = true
  Suppressed = false
  Type = 0
FEATURE [PartDesign::Pad] Pad006
  BaseFeature = -> Pocket001
  Direction = (0,1,-2e-16)
  Length = 0.8
  Length2 = 10
  Profile = -> Sketch094
  ReferenceAxis = -> Sketch094 [N_Axis]
  Refine = true
  Suppressed = false
  Type = 0
FEATURE [PartDesign::Pad] Pad007
  BaseFeature = -> Pad006
  Direction = (0,1,-2e-16)
  Length = 2
  Length2 = 10
  Profile = -> Sketch095
  ReferenceAxis = -> Sketch095 [N_Axis]
  Refine = true
  Suppressed = false
  Type = 0
FEATURE [PartDesign::Pad] Pad008  label="Pad008 - forma impugnatura"
  BaseFeature = -> Pad007
  Direction = (0,1,-2e-16)
  Length = 1.6
  Length2 = 10
  Profile = -> Sketch096
  ReferenceAxis = -> Sketch096 [N_Axis]
  Refine = true
  Suppressed = false
  Type = 0
FEATURE [PartDesign::Pad] Pad009
  BaseFeature = -> Pad008
  Direction = (0,1,-2e-16)
  Length = 1.6
  Length2 = 10
  Profile = -> Sketch097
  ReferenceAxis = -> Sketch097 [N_Axis]
  Refine = true
  Suppressed = false
  Type = 0
FEATURE [Sketcher::SketchObject] Sketch098
  ArcFitTolerance = 1e-06
  AttachmentSupport = -> [Pad006]
  ExternalGeometry = -> [Binder]
  FullyConstrained = true
  MakeInternals = false
  MapMode = 5
  Placement = pos=(0,2.8,-7e-16) rot=(0,0.707107,0.707107;3.14159rad)
  sketch-geometry (4):
    g0: LineSegment StartX=118 StartY=39.2 StartZ=0 EndX=129 EndY=39.2 EndZ=0
    g1: LineSegment StartX=120.599 StartY=31.2 StartZ=0 EndX=131.599 EndY=31.2 EndZ=0
    g2: LineSegment StartX=129 StartY=39.2 StartZ=0 EndX=131.599 EndY=31.2 EndZ=0
    g3: LineSegment StartX=118 StartY=39.2 StartZ=0 EndX=120.599 EndY=31.2 EndZ=0
  constraints (12):
    c: PointOnObject(g0,g-3)
    c: PointOnObject(g0,g-3)
    c: DistanceX(g0,g0) = 11
    c: Horizontal(g1)
    c: Equal(g1,g0)
    c: Coincident(g2,g0)
    c: Coincident(g3,g0)
    c: Parallel(g-4,g2)
    c: Coincident(g1,g2)
    c: Coincident(g1,g3)
    c: DistanceY(g1,g0) = 8
    c: DistanceX(g-3,g0) = 118
FEATURE [Sketcher::SketchObject] Sketch099
  ArcFitTolerance = 1e-06
  AttachmentSupport = -> [Pad008]
  ExternalGeometry = -> [Binder]
  FullyConstrained = true
  MakeInternals = false
  MapMode = 5
  Placement = pos=(0,3.6,0) rot=(0,0.707107,0.707107;3.14159rad)
  sketch-geometry (13):
    g0: LineSegment StartX=192.176 StartY=-3.18451 StartZ=0 EndX=196.804 EndY=-13.1108 EndZ=0
    g1: LineSegment [constr] StartX=202.765 StartY=20.303 StartZ=0 EndX=181.223 EndY=20.303 EndZ=0
    g2: LineSegment [constr] StartX=181.223 StartY=20.303 StartZ=0 EndX=181.223 EndY=-3.18451 EndZ=0
    g3: ArcOfCircle CenterX=181.223 CenterY=-20.3764 CenterZ=0 NormalX=0 NormalY=0 NormalZ=1 AngleXU=0 Radius=17.1918 StartAngle=0.436332 EndAngle=1.57079
    g4: ArcOfEllipse CenterX=181.223 CenterY=8.55923 CenterZ=0 NormalX=0 NormalY=0 NormalZ=1 MajorRadius=23.4779 MinorRadius=11.7437 AngleXU=0 StartAngle=1.5708 EndAngle=4.71239
    g5: LineSegment [constr] StartX=204.701 StartY=8.55923 StartZ=0 EndX=157.745 EndY=8.55923 EndZ=0
    g6: LineSegment [constr] StartX=181.223 StartY=20.303 StartZ=0 EndX=181.223 EndY=-3.18451 EndZ=0
    g7: GeomPoint [constr] X=201.553 Y=8.55923 Z=0
    g8: GeomPoint [constr] X=160.894 Y=8.55923 Z=0
    g9: GeomPoint [constr] X=181.223 Y=-3.18451 Z=0
    g10: LineSegment StartX=181.223 StartY=20.303 StartZ=0 EndX=202.765 EndY=20.303 EndZ=0
    g11: ArcOfCircle CenterX=207.583 CenterY=4 CenterZ=0 NormalX=0 NormalY=0 NormalZ=1 AngleXU=0 Radius=17 StartAngle=1.85815 EndAngle=3.57792
    g12: LineSegment [constr] StartX=172.411 StartY=39.2 StartZ=0 EndX=192.176 EndY=-3.18451 EndZ=0
  constraints (27):
    c: Coincident(g1,g-7)
    c: Horizontal(g1)
    c: Coincident(g2,g1)
    c: Vertical(g2)
    c: Horizontal(g2,g0)
    c: Coincident(g3,g0)
    c: Coincident(g3,g2)
    c: InternalAlignment(g5-g8 -> g4) x4
    c: Horizontal(g5)
    c: PointOnObject(g4,g2)
    c: Coincident(g4,g1)
    c: DistanceX(g-3,g5) = 10.1
    c: Coincident(g4,g2)
    c: Tangent(g3,g-5)
    c: PointOnObject(g9,g4)
    c: PointOnObject(g9,g3)
    c: Tangent(g4,g3,g9) = 1.5708
    c: Coincident(g10,g1)
    c: Coincident(g10,g1)
    c: Equal(g11,g-4)
    c: Coincident(g11,g1)
    c: Coincident(g11,g0)
    c: PointOnObject(g12,g-6)
    c: PointOnObject(g1,g12)
    c: Tangent(g12,g-5) = -1.5708
    c: Tangent(g0,g-5) = -1.5708
    c: Horizontal(g9,g12)
FEATURE [Sketcher::SketchObject] Sketch106  label="Sketch106 - smusso impuniatura interno"
  ArcFitTolerance = 1e-06
  AttachmentSupport = -> [Pad008]
  ExternalGeometry = -> [Pad008]
  FullyConstrained = true
  MakeInternals = false
  MapMode = 5
  Placement = pos=(0,-1.586e-13,-80.4316) rot=(1,0,0;3.14159rad)
  sketch-geometry (9):
    g0: LineSegment StartX=-176.685 StartY=-3.6 StartZ=0 EndX=-176.685 EndY=3.277e-13 EndZ=0
    g1: LineSegment [constr] StartX=-176.685 StartY=-7.37e-14 StartZ=0 EndX=-176.685 EndY=3.279e-13 EndZ=0
    g2: LineSegment [constr] StartX=-186.685 StartY=-3.6 StartZ=0 EndX=-186.685 EndY=3.277e-13 EndZ=0
    g3: ArcOfEllipse CenterX=-186.685 CenterY=3.279e-13 CenterZ=0 NormalX=0 NormalY=0 NormalZ=1 MajorRadius=10 MinorRadius=3.6 AngleXU=-3.14159 StartAngle=1.5708 EndAngle=3.14159
    g4: LineSegment [constr] StartX=-196.685 StartY=-5.9e-15 StartZ=0 EndX=-176.685 EndY=-5.9e-15 EndZ=0
    g5: LineSegment [constr] StartX=-186.685 StartY=-3.6 StartZ=0 EndX=-186.685 EndY=3.6 EndZ=0
    g6: GeomPoint [constr] X=-196.015 Y=-1.19e-14 Z=0
    g7: GeomPoint [constr] X=-177.356 Y=-4.9e-15 Z=0
    g8: LineSegment StartX=-176.685 StartY=-3.6 StartZ=0 EndX=-186.685 EndY=-3.6 EndZ=0
  constraints (15):
    c: PointOnObject(g2,g-3)
    c: Coincident(g1,g-5)
    c: DistanceY(g1,g1) = 0
    c: Coincident(g0,g1)
    c: DistanceX(g2,g-5) = 10
    c: Vertical(g2)
    c: Horizontal(g2,g0)
    c: InternalAlignment(g4-g7 -> g3) x4
    c: Coincident(g3,g2)
    c: Horizontal(g4)
    c: Coincident(g3,g0)
    c: Tangent(g0,g-5) = 1.5708
    c: Coincident(g3,g2)
    c: Coincident(g8,g0)
    c: Coincident(g8,g2)
FEATURE [Sketcher::SketchObject] Sketch107  label="Sketch107 - smusso impugnatura esterno"
  ArcFitTolerance = 1e-06
  AttachmentSupport = -> [Pad008]
  ExternalGeometry = -> [Pad008]
  FullyConstrained = true
  MakeInternals = false
  MapMode = 5
  Placement = pos=(0,-1.586e-13,-80.4316) rot=(1,0,0;3.14159rad)
  sketch-geometry (9):
    g0: LineSegment [constr] StartX=-215.932 StartY=-1.416e-13 StartZ=0 EndX=-215.932 EndY=-4.13e-14 EndZ=0
    g1: LineSegment StartX=-215.932 StartY=-3.6 StartZ=0 EndX=-215.932 EndY=-4.13e-14 EndZ=0
    g2: LineSegment StartX=-215.932 StartY=-3.6 StartZ=0 EndX=-205.932 EndY=-3.6 EndZ=0
    g3: LineSegment [constr] StartX=-205.932 StartY=-3.6 StartZ=0 EndX=-205.932 EndY=-4.13e-14 EndZ=0
    g4: ArcOfEllipse CenterX=-205.932 CenterY=-4.13e-14 CenterZ=0 NormalX=0 NormalY=0 NormalZ=1 MajorRadius=10 MinorRadius=3.6 AngleXU=-3.14159 StartAngle=-2.66e-14 EndAngle=1.5708
    g5: LineSegment [constr] StartX=-215.932 StartY=-1.416e-13 StartZ=0 EndX=-195.932 EndY=-1.416e-13 EndZ=0
    g6: LineSegment [constr] StartX=-205.932 StartY=-3.6 StartZ=0 EndX=-205.932 EndY=3.6 EndZ=0
    g7: GeomPoint [constr] X=-215.262 Y=-1.309e-13 Z=0
    g8: GeomPoint [constr] X=-196.602 Y=-1.551e-13 Z=0
  constraints (16):
    c: Coincident(g0,g-6)
    c: PointOnObject(g0,g-6)
    c: DistanceY(g0,g0) = 0
    c: Coincident(g1,g-6)
    c: Coincident(g1,g0)
    c: Tangent(g2,g-3)
    c: DistanceX(g2,g2) = 10
    c: Coincident(g3,g2)
    c: Vertical(g3)
    c: Horizontal(g3,g0)
    c: InternalAlignment(g5-g8 -> g4) x4
    c: Coincident(g4,g3)
    c: Horizontal(g5)
    c: Coincident(g4,g0)
    c: Coincident(g4,g2)
    c: PointOnObject(g2,g1)
FEATURE [Sketcher::SketchObject] Sketch108
  ArcFitTolerance = 1e-06
  AttachmentOffset = pos=(0,0,-1.6) rot=(0,0,1;0rad)
  AttachmentSupport = -> [Pad008]
  ExternalGeometry = -> [Binder]
  FullyConstrained = true
  MakeInternals = false
  MapMode = 5
  Placement = pos=(0,2,4e-16) rot=(0,0.707107,0.707107;3.14159rad)
  sketch-geometry (14):
    g0: LineSegment StartX=192.176 StartY=-3.18451 StartZ=0 EndX=193.827 EndY=-6.72678 EndZ=0
    g1: LineSegment [constr] StartX=202.765 StartY=20.303 StartZ=0 EndX=181.223 EndY=20.303 EndZ=0
    g2: LineSegment [constr] StartX=181.223 StartY=20.303 StartZ=0 EndX=181.223 EndY=1.30297 EndZ=0
    g3: ArcOfCircle CenterX=181.223 CenterY=-12.6042 CenterZ=0 NormalX=0 NormalY=0 NormalZ=1 AngleXU=0 Radius=13.9072 StartAngle=0.436332 EndAngle=1.5708
    g4: ArcOfEllipse CenterX=181.223 CenterY=10.803 CenterZ=0 NormalX=0 NormalY=0 NormalZ=1 MajorRadius=14.4779 MinorRadius=9.5 AngleXU=0 StartAngle=1.5708 EndAngle=4.71239
    g5: LineSegment [constr] StartX=195.701 StartY=10.803 StartZ=0 EndX=166.745 EndY=10.803 EndZ=0
    g6: LineSegment [constr] StartX=181.223 StartY=20.303 StartZ=0 EndX=181.223 EndY=1.30297 EndZ=0
    g7: GeomPoint [constr] X=192.148 Y=10.803 Z=0
    g8: GeomPoint [constr] X=170.298 Y=10.803 Z=0
    g9: LineSegment StartX=181.223 StartY=20.303 StartZ=0 EndX=202.765 EndY=20.303 EndZ=0
    g10: ArcOfCircle CenterX=207.583 CenterY=4 CenterZ=0 NormalX=0 NormalY=0 NormalZ=1 AngleXU=0 Radius=17 StartAngle=1.85815 EndAngle=3.57792
    g11: LineSegment [constr] StartX=172.411 StartY=39.2 StartZ=0 EndX=192.176 EndY=-3.18451 EndZ=0
    g12: GeomPoint [constr] X=181.223 Y=1.30297 Z=0
    g13: GeomPoint [constr] X=181.223 Y=1.30297 Z=0
  constraints (28):
    c: Coincident(g1,g-7)
    c: Horizontal(g1)
    c: Coincident(g2,g1)
    c: Vertical(g2)
    c: Coincident(g3,g2)
    c: InternalAlignment(g5-g8 -> g4) x4
    c: Horizontal(g5)
    c: PointOnObject(g4,g2)
    c: Coincident(g4,g1)
    c: DistanceX(g-3,g5) = 19.1
    c: Coincident(g4,g2)
    c: Coincident(g9,g1)
    c: Coincident(g9,g1)
    c: Coincident(g10,g1)
    c: Coincident(g10,g0)
    c: PointOnObject(g11,g-6)
    c: PointOnObject(g1,g11)
    c: DistanceY(g2,g1) = 19
    c: Coincident(g10,g-4)
    c: PointOnObject(g12,g4)
    c: PointOnObject(g12,g3)
    c: Tangent(g11,g-5) = -1.5708
    c: Tangent(g0,g-5) = -1.5708
    c: Tangent(g3,g0) = 1.5708
    c: PointOnObject(g13,g4)
    c: PointOnObject(g13,g3)
    c: Tangent(g4,g3,g13) = 1.5708
    c: Horizontal(g11,g0)
FEATURE [Part::Part2DObjectPython] Clone2D  label="Sketch108 (2D)"  # Draft 2D object (typed FeaturePython)
  Fuse = false
  Objects = -> [Sketch108]
  Placement = pos=(0,2,4e-16) rot=(0,0.707107,0.707107;3.14159rad)
  Scale = (1,1,1)
FEATURE [Sketcher::SketchObject] Sketch109
  ArcFitTolerance = 1e-06
  AttachmentOffset = pos=(0,0,-3.5) rot=(0,0,1;0rad)
  AttachmentSupport = -> [Pad008]
  ExternalGeometry = -> [Binder]
  FullyConstrained = true
  MakeInternals = false
  MapMode = 5
  Placement = pos=(0,0.1,8e-16) rot=(0,0.707107,0.707107;3.14159rad)
  sketch-geometry (1):
    g0: GeomPoint X=197.47 Y=8.55923 Z=0
  constraints (1):
    c: Symmetric(g-7,g-5,g0)
FEATURE [PartDesign::Chamfer] Chamfer005
  Angle = 45
  Base = -> Pad009 [Edge215,Edge212]
  BaseFeature = -> Pad009
  ChamferType = 1
  FlipDirection = false
  Refine = true
  Size = 1.5
  Size2 = 2.8
  SupportTransform = false
  Suppressed = false
  UseAllEdges = false
FEATURE [Sketcher::SketchObject] Sketch111
  ArcFitTolerance = 1e-06
  AttachmentSupport = -> [Pad009]
  ExternalGeometry = -> [Pad009]
  FullyConstrained = true
  MakeInternals = false
  MapMode = 5
  Placement = pos=(0,3.6,-8e-16) rot=(0,0.707107,0.707107;3.14159rad)
  sketch-geometry (21):
    g0: LineSegment [constr] StartX=97 StartY=36.8 StartZ=0 EndX=97 EndY=26.8 EndZ=0
    g1: LineSegment StartX=97 StartY=28.6 StartZ=0 EndX=97 EndY=27.8 EndZ=0
    g2: LineSegment StartX=97 StartY=27.8 StartZ=0 EndX=108 EndY=27.8 EndZ=0
    g3: LineSegment StartX=108 StartY=27.8 StartZ=0 EndX=108 EndY=28.6 EndZ=0
    g4: LineSegment StartX=108 StartY=28.6 StartZ=0 EndX=97 EndY=28.6 EndZ=0
    g5: LineSegment StartX=97 StartY=35.8 StartZ=0 EndX=97 EndY=35 EndZ=0
    g6: LineSegment StartX=97 StartY=35 StartZ=0 EndX=108 EndY=35 EndZ=0
    g7: LineSegment StartX=108 StartY=35 StartZ=0 EndX=108 EndY=35.8 EndZ=0
    g8: LineSegment StartX=108 StartY=35.8 StartZ=0 EndX=97 EndY=35.8 EndZ=0
    g9: LineSegment StartX=97 StartY=30.4 StartZ=0 EndX=97 EndY=29.6 EndZ=0
    g10: LineSegment StartX=97 StartY=29.6 StartZ=0 EndX=108 EndY=29.6 EndZ=0
    g11: LineSegment StartX=108 StartY=29.6 StartZ=0 EndX=108 EndY=30.4 EndZ=0
    g12: LineSegment StartX=108 StartY=30.4 StartZ=0 EndX=97 EndY=30.4 EndZ=0
    g13: LineSegment StartX=97 StartY=34 StartZ=0 EndX=97 EndY=33.2 EndZ=0
    g14: LineSegment StartX=97 StartY=33.2 StartZ=0 EndX=108 EndY=33.2 EndZ=0
    g15: LineSegment StartX=108 StartY=33.2 StartZ=0 EndX=108 EndY=34 EndZ=0
    g16: LineSegment StartX=108 StartY=34 StartZ=0 EndX=97 EndY=34 EndZ=0
    g17: LineSegment StartX=97 StartY=32.2 StartZ=0 EndX=97 EndY=31.4 EndZ=0
    g18: LineSegment StartX=97 StartY=31.4 StartZ=0 EndX=108 EndY=31.4 EndZ=0
    g19: LineSegment StartX=108 StartY=31.4 StartZ=0 EndX=108 EndY=32.2 EndZ=0
    g20: LineSegment StartX=108 StartY=32.2 StartZ=0 EndX=97 EndY=32.2 EndZ=0
  constraints (54):
    c: Vertical(g0)
    c: PointOnObject(g0,g-3)
    c: PointOnObject(g0,g-4)
    c: DistanceX(g0,g-5) = 11
    c: Coincident(g1,g2)
    c: Coincident(g2,g3)
    c: Coincident(g3,g4)
    c: Coincident(g4,g1)
    c: Horizontal(g2)
    c: Horizontal(g4)
    c: Tangent(g1,g0)
    c: Tangent(g3,g-5)
    c: DistanceY(g2,g3) = 0.8
    c: Coincident(g5,g6)
    c: Coincident(g6,g7)
    c: Coincident(g7,g8)
    c: Coincident(g8,g5)
    c: Horizontal(g6)
    c: Horizontal(g8)
    c: DistanceY(g6,g7) = 0.8
    c: Coincident(g9,g10)
    c: Coincident(g10,g11)
    c: Coincident(g11,g12)
    c: Coincident(g12,g9)
    c: Horizontal(g10)
    c: Horizontal(g12)
    c: DistanceY(g10,g11) = 0.8
    c: Tangent(g5,g0)
    c: Tangent(g7,g-5)
    c: Tangent(g9,g0)
    c: Tangent(g11,g-5)
    c: Coincident(g13,g14)
    c: Coincident(g14,g15)
    c: Coincident(g15,g16)
    c: Coincident(g16,g13)
    c: Horizontal(g14)
    c: Horizontal(g16)
    c: DistanceY(g14,g15) = 0.8
    c: Tangent(g13,g0)
    c: Tangent(g15,g-5)
    c: Coincident(g17,g18)
    c: Coincident(g18,g19)
    c: Coincident(g19,g20)
    c: Coincident(g20,g17)
    c: Horizontal(g18)
    c: Horizontal(g20)
    c: DistanceY(g18,g19) = 0.8
    c: Tangent(g17,g0)
    c: Tangent(g19,g-5)
    c: DistanceY(g1,g9) = 1
    c: DistanceY(g9,g17) = 1
    c: DistanceY(g17,g13) = 1
    c: DistanceY(g13,g5) = 1
    c: DistanceY(g0,g1) = 1
FEATURE [PartDesign::Pocket] Pocket004
  BaseFeature = -> Chamfer005
  Direction = (0,-1,2e-16)
  Length = 1
  Length2 = 5
  Profile = -> Sketch111
  ReferenceAxis = -> Sketch111 [N_Axis]
  Refine = true
  Suppressed = false
  Type = 0
FEATURE [PartDesign::Pad] Pad010
  BaseFeature = -> Pocket004
  Direction = (0,1,-2e-16)
  Length = 1.2
  Length2 = 10
  Profile = -> Sketch098
  ReferenceAxis = -> Sketch098 [N_Axis]
  Refine = true
  Suppressed = false
  Type = 0
FEATURE [PartDesign::Chamfer] Chamfer006
  Angle = 45
  Base = -> Pad010 [Edge291]
  BaseFeature = -> Pad010
  ChamferType = 1
  FlipDirection = false
  Refine = true
  Size = 1
  Size2 = 6
  SupportTransform = false
  Suppressed = false
  UseAllEdges = false
FEATURE [Sketcher::SketchObject] Sketch110
  ArcFitTolerance = 1e-06
  AttachmentSupport = -> [Pad010]
  ExternalGeometry = -> [Sketch098]
  FullyConstrained = true
  MakeInternals = false
  MapMode = 5
  Placement = pos=(0,4,-9e-16) rot=(0,0.707107,0.707107;3.14159rad)
  sketch-geometry (8):
    g0: LineSegment StartX=119.69 StartY=34 StartZ=0 EndX=130.69 EndY=34 EndZ=0
    g1: LineSegment StartX=119.95 StartY=33.2 StartZ=0 EndX=130.95 EndY=33.2 EndZ=0
    g2: LineSegment StartX=119.137 StartY=35.7 StartZ=0 EndX=130.137 EndY=35.7 EndZ=0
    g3: LineSegment StartX=118.877 StartY=36.5 StartZ=0 EndX=129.877 EndY=36.5 EndZ=0
    g4: LineSegment StartX=118.877 StartY=36.5 StartZ=0 EndX=119.137 EndY=35.7 EndZ=0
    g5: LineSegment StartX=129.877 StartY=36.5 StartZ=0 EndX=130.137 EndY=35.7 EndZ=0
    g6: LineSegment StartX=119.69 StartY=34 StartZ=0 EndX=119.95 EndY=33.2 EndZ=0
    g7: LineSegment StartX=130.69 StartY=34 StartZ=0 EndX=130.95 EndY=33.2 EndZ=0
  constraints (24):
    c: Horizontal(g0)
    c: Horizontal(g1)
    c: Horizontal(g2)
    c: Horizontal(g3)
    c: Equal(g1,g-5)
    c: Equal(g0,g-5)
    c: Equal(g2,g-5)
    c: Equal(g3,g-5)
    c: PointOnObject(g0,g-3)
    c: PointOnObject(g1,g-3)
    c: PointOnObject(g2,g-3)
    c: PointOnObject(g3,g-3)
    c: Coincident(g4,g3)
    c: Coincident(g4,g2)
    c: Coincident(g5,g3)
    c: Coincident(g5,g2)
    c: Coincident(g6,g0)
    c: Coincident(g6,g1)
    c: Coincident(g7,g0)
    c: Coincident(g7,g1)
    c: DistanceY(g1,g0) = 0.8
    c: DistanceY(g2,g3) = 0.8
    c: DistanceY(g-5,g1) = 2
    c: DistanceY(g-5,g2) = 4.5
FEATURE [PartDesign::Pocket] Pocket003
  BaseFeature = -> Chamfer006
  Direction = (0,-1,2e-16)
  Length = 1
  Length2 = 5
  Profile = -> Sketch110
  ReferenceAxis = -> Sketch110 [N_Axis]
  Refine = true
  Suppressed = false
  Type = 0
FEATURE [PartDesign::SubtractivePipe] SubtractivePipe
  AuxilleryCurvelinear = true
  AuxillerySpineTangent = false
  BaseFeature = -> Pocket003
  Binormal = (0,0,0)
  Mode = 0
  Profile = -> Sketch106
  Refine = true
  Spine = -> Pad008 [Edge215]
  SpineTangent = false
  Suppressed = false
  Transformation = 0
  Transition = 0
FEATURE [PartDesign::SubtractivePipe] SubtractivePipe001
  AuxilleryCurvelinear = true
  AuxillerySpineTangent = false
  BaseFeature = -> SubtractivePipe
  Binormal = (0,0,0)
  Mode = 0
  Profile = -> Sketch107
  Refine = true
  Spine = -> Pad008 [Edge213,Edge216,Edge210]
  SpineTangent = false
  Suppressed = false
  Transformation = 0
  Transition = 0
FEATURE [PartDesign::SubtractiveLoft] SubtractiveLoft
  BaseFeature = -> SubtractivePipe001
  Closed = false
  Profile = -> Sketch099
  Refine = true
  Ruled = false
  Sections = -> [Sketch108]
  Suppressed = false
FEATURE [PartDesign::SubtractiveLoft] SubtractiveLoft001
  BaseFeature = -> SubtractiveLoft
  Closed = false
  Profile = -> Clone2D
  Refine = true
  Ruled = false
  Sections = -> [Sketch109]
  Suppressed = false
FEATURE [Sketcher::SketchObject] Sketch112
  ArcFitTolerance = 1e-06
  AttachmentSupport = -> [Pad008]
  ExternalGeometry = -> [Binder]
  FullyConstrained = true
  MakeInternals = false
  MapMode = 5
  Placement = pos=(0,3.6,0) rot=(0,0.707107,0.707107;3.14159rad)
  sketch-geometry (4):
    g0: LineSegment [constr] StartX=167.782 StartY=-53.0314 StartZ=0 EndX=215.42 EndY=-53.0314 EndZ=0
    g1: GeomPoint [constr] X=191.282 Y=-53.0314 Z=0
    g2: Circle CenterX=191.282 CenterY=-53.0314 CenterZ=0 NormalX=0 NormalY=0 NormalZ=1 AngleXU=0 Radius=11.5
    g3: Circle CenterX=191.282 CenterY=-53.0314 CenterZ=0 NormalX=0 NormalY=0 NormalZ=1 AngleXU=0 Radius=10.7
  constraints (9):
    c: Horizontal(g0)
    c: PointOnObject(g0,g-3)
    c: Diameter(g2) = 23
    c: Coincident(g2,g1)
    c: Diameter(g3) = 21.4
    c: Coincident(g3,g1)
    c: DistanceX(g0,g1) = 23.5
    c: PointOnObject(g1,g0)
    c: Coincident(g0,g-4)
FEATURE [PartDesign::Chamfer] Chamfer016
  Angle = 45
  Base = -> SubtractiveLoft001 [Edge118,Edge117,Edge119,Edge120,Edge109]
  BaseFeature = -> SubtractiveLoft001
  ChamferType = 0
  FlipDirection = false
  Refine = true
  Size = 1.5
  Size2 = 1
  SupportTransform = false
  Suppressed = false
  UseAllEdges = false
FEATURE [PartDesign::Chamfer] Chamfer017
  Angle = 45
  Base = -> Chamfer016 [Edge15]
  BaseFeature = -> Chamfer016
  ChamferType = 0
  FlipDirection = false
  Refine = true
  Size = 1.6
  Size2 = 1
  SupportTransform = false
  Suppressed = false
  UseAllEdges = false
FEATURE [PartDesign::Chamfer] Chamfer018
  Angle = 45
  Base = -> Chamfer017 [Edge10]
  BaseFeature = -> Chamfer017
  ChamferType = 0
  FlipDirection = false
  Refine = true
  Size = 3.5
  Size2 = 1
  SupportTransform = false
  Suppressed = false
  UseAllEdges = false
FEATURE [PartDesign::Chamfer] Chamfer019
  Angle = 45
  Base = -> Chamfer018 [Edge94]
  BaseFeature = -> Chamfer018
  ChamferType = 0
  FlipDirection = false
  Refine = true
  Size = 1.9
  Size2 = 1
  SupportTransform = false
  Suppressed = false
  UseAllEdges = false
FEATURE [PartDesign::Fillet] Fillet009
  Base = -> Chamfer019 [Edge83]
  BaseFeature = -> Chamfer019
  Radius = 1.1
  Refine = true
  SupportTransform = false
  Suppressed = false
  UseAllEdges = false
FEATURE [PartDesign::Fillet] Fillet010
  Base = -> Fillet009 [Edge76]
  BaseFeature = -> Fillet009
  Radius = 1.9
  Refine = true
  SupportTransform = false
  Suppressed = false
  UseAllEdges = false
FEATURE [PartDesign::Pocket] Pocket005
  BaseFeature = -> Fillet010
  Direction = (0,-1,2e-16)
  Length = 0.8
  Length2 = 5
  Profile = -> Sketch112
  ReferenceAxis = -> Sketch112 [N_Axis]
  Refine = true
  Suppressed = false
  Type = 0
FEATURE [Part::Part2DObjectPython] ShapeString001  # Draft 2D object (typed FeaturePython)
  FontFile = <path>
  Fuse = false
  Justification = 6
  JustificationReference = 0
  KeepLeftMargin = false
  MakeFace = true
  ObliqueAngle = 0
  Placement = pos=(-183.5,3.6,-57.5) rot=(0,0.707107,0.707107;3.14159rad)
  ScaleToSize = true
  Size = 10
  String = AS
  Tracking = 0
FEATURE [PartDesign::Pocket] Pocket013
  BaseFeature = -> Pocket005
  Direction = (-1e-16,-1,2e-16)
  Length = 1
  Length2 = 5
  Profile = -> ShapeString001
  ReferenceAxis = -> ShapeString001 [N_Axis]
  Refine = true
  Suppressed = false
  Type = 0
FEATURE [PartDesign::Pad] Pad020
  Direction = (0,-1,2e-16)
  Length = 25.2
  Length2 = 10
  Midplane = true
  Placement = pos=(0,0,0) rot=(1,0,0;1.5708rad)
  Profile = -> Sketch021
  ReferenceAxis = -> Sketch021 [N_Axis]
  Refine = true
  Suppressed = false
  Type = 0
FEATURE [PartDesign::Body] Body001  label="perno fermo rumble e driver solenoide"
  AllowCompound = false
  Group = -> [Sketch021,Pad020]
  Origin = -> Origin001
  Tip = -> Pad020
FEATURE [PartDesign::Pad] Pad021
  Direction = (0,-1,2e-16)
  Length = 16.8
  Length2 = 10
  Midplane = true
  Placement = pos=(0,0,0) rot=(1,0,0;1.5708rad)
  Profile = -> Sketch061
  ReferenceAxis = -> Sketch061 [N_Axis]
  Refine = true
  Suppressed = false
  Type = 0
FEATURE [PartDesign::Pocket] Pocket014
  BaseFeature = -> Pad021
  Direction = (0,1,-2e-16)
  Length = 12.8
  Length2 = 5
  Midplane = true
  Placement = pos=(0,0,0) rot=(1,0,0;1.5708rad)
  Profile = -> Sketch062
  ReferenceAxis = -> Sketch062 [N_Axis]
  Refine = true
  Suppressed = false
  Type = 0
FEATURE [PartDesign::Pad] Pad022
  BaseFeature = -> Pocket014
  Direction = (0,-1,2e-16)
  Length = 7.6
  Length2 = 10
  Midplane = true
  Placement = pos=(0,0,0) rot=(1,0,0;1.5708rad)
  Profile = -> Sketch063
  ReferenceAxis = -> Sketch063 [N_Axis]
  Refine = true
  Suppressed = false
  Type = 0
FEATURE [PartDesign::Body] Body003  label="blocco switch"
  AllowCompound = false
  Group = -> [Sketch061,Sketch062,Sketch063,Pad021,Pocket014,Pad022]
  Origin = -> Origin003
  Tip = -> Pad022
FEATURE [PartDesign::Pad] Pad024
  Direction = (0,-1,2e-16)
  Length = 17
  Length2 = 10
  Midplane = true
  Placement = pos=(0,0,0) rot=(1,0,0;1.5708rad)
  Profile = -> Sketch045
  ReferenceAxis = -> Sketch045 [N_Axis]
  Refine = true
  Suppressed = false
  Type = 0
FEATURE [PartDesign::Pocket] Pocket015
  BaseFeature = -> Pad024
  Direction = (-1,0,0)
  Length = 8
  Length2 = 5
  Placement = pos=(0,0,0) rot=(1,0,0;1.5708rad)
  Profile = -> Sketch047
  ReferenceAxis = -> Sketch047 [N_Axis]
  Refine = true
  Reversed = true
  Suppressed = false
  Type = 0
FEATURE [PartDesign::Pocket] Pocket016
  BaseFeature = -> Pocket015
  Direction = (-1,0,0)
  Length = 1
  Length2 = 5
  Placement = pos=(0,0,0) rot=(1,0,0;1.5708rad)
  Profile = -> Sketch046
  ReferenceAxis = -> Sketch046 [N_Axis]
  Refine = true
  Reversed = true
  Suppressed = false
  Type = 0
FEATURE [PartDesign::Pocket] Pocket017
  BaseFeature = -> Pocket016
  Direction = (0,1,-2e-16)
  Length = 17
  Length2 = 5
  Midplane = true
  Placement = pos=(0,0,0) rot=(1,0,0;1.5708rad)
  Profile = -> Sketch048
  ReferenceAxis = -> Sketch048 [N_Axis]
  Refine = true
  Suppressed = false
  Type = 0
FEATURE [PartDesign::Pad] Pad025
  BaseFeature = -> Pocket017
  Direction = (0,-1,2e-16)
  Length = 17
  Length2 = 10
  Midplane = true
  Placement = pos=(0,0,0) rot=(1,0,0;1.5708rad)
  Profile = -> Sketch049
  ReferenceAxis = -> Sketch049 [N_Axis]
  Refine = true
  Suppressed = false
  Type = 0
FEATURE [PartDesign::Pad] Pad026
  BaseFeature = -> Pad025
  Direction = (0,-1,2e-16)
  Length = 17
  Length2 = 10
  Midplane = true
  Placement = pos=(0,0,0) rot=(1,0,0;1.5708rad)
  Profile = -> Sketch066
  ReferenceAxis = -> Sketch066 [N_Axis]
  Refine = true
  Suppressed = false
  Type = 0
FEATURE [PartDesign::Pad] Pad027
  BaseFeature = -> Pad026
  Direction = (0,-1,2e-16)
  Length = 5
  Length2 = 10
  Midplane = true
  Placement = pos=(0,0,0) rot=(1,0,0;1.5708rad)
  Profile = -> Sketch064
  ReferenceAxis = -> Sketch064 [N_Axis]
  Refine = true
  Suppressed = false
  Type = 0
FEATURE [PartDesign::Pad] Pad028
  BaseFeature = -> Pad027
  Direction = (1,0,0)
  Length = 1
  Length2 = 10
  Placement = pos=(0,0,0) rot=(1,0,0;1.5708rad)
  Profile = -> Sketch068
  ReferenceAxis = -> Sketch068 [N_Axis]
  Refine = true
  Reversed = true
  Suppressed = false
  Type = 0
FEATURE [PartDesign::Chamfer] Chamfer020
  Angle = 45
  Base = -> Pad028 [Edge73,Edge75,Edge78,Edge77]
  BaseFeature = -> Pad028
  ChamferType = 0
  FlipDirection = false
  Placement = pos=(0,0,0) rot=(1,0,0;1.5708rad)
  Refine = true
  Size = 0.5
  Size2 = 1
  SupportTransform = false
  Suppressed = false
  UseAllEdges = false
FEATURE [PartDesign::Body] Body002  label="supporto per neopixel"
  AllowCompound = false
  Group = -> [Sketch045,Sketch047,Sketch046,Sketch048,Sketch049,Sketch066,Sketch064,Sketch068,Pad024,Pocket015,Pocket016,Pocket017,Pad025,Pad026,Pad027,Pad028,Chamfer020]
  Origin = -> Origin002
  Tip = -> Chamfer020
FEATURE [Sketcher::SketchObject] Sketch134  label="perno fermo rumble002"
  ArcFitTolerance = 1e-06
  AttachmentSupport = -> [XZ_Plane008]
  FullyConstrained = true
  MakeInternals = false
  MapMode = 5
  Placement = pos=(0,0,0) rot=(1,0,0;1.5708rad)
  sketch-geometry (16):
    g0: LineSegment StartX=0 StartY=0.45 StartZ=0 EndX=0 EndY=1.55 EndZ=0
    g1: LineSegment StartX=0.45 StartY=2 StartZ=0 EndX=1.55 EndY=2 EndZ=0
    g2: LineSegment StartX=2 StartY=1.55 StartZ=0 EndX=2 EndY=0.45 EndZ=0
    g3: LineSegment StartX=1.55 StartY=0 StartZ=0 EndX=0.45 EndY=0 EndZ=0
    g4: ArcOfCircle [constr] CenterX=0.45 CenterY=1.55 CenterZ=0 NormalX=0 NormalY=0 NormalZ=1 AngleXU=0 Radius=0.45 StartAngle=1.5708 EndAngle=3.14159
    g5: GeomPoint [constr] X=0 Y=2 Z=0
    g6: LineSegment StartX=0.45 StartY=2 StartZ=0 EndX=0 EndY=1.55 EndZ=0
    g7: ArcOfCircle [constr] CenterX=1.55 CenterY=1.55 CenterZ=0 NormalX=0 NormalY=0 NormalZ=1 AngleXU=0 Radius=0.45 StartAngle=0 EndAngle=1.5708
    g8: GeomPoint [constr] X=2 Y=2 Z=0
    g9: LineSegment StartX=2 StartY=1.55 StartZ=0 EndX=1.55 EndY=2 EndZ=0
    g10: ArcOfCircle [constr] CenterX=1.55 CenterY=0.45 CenterZ=0 NormalX=0 NormalY=0 NormalZ=1 AngleXU=0 Radius=0.45 StartAngle=4.71239 EndAngle=6.28319
    g11: GeomPoint [constr] X=2 Y=0 Z=0
    g12: LineSegment StartX=1.55 StartY=0 StartZ=0 EndX=2 EndY=0.45 EndZ=0
    g13: ArcOfCircle [constr] CenterX=0.45 CenterY=0.45 CenterZ=0 NormalX=0 NormalY=0 NormalZ=1 AngleXU=0 Radius=0.45 StartAngle=3.14159 EndAngle=4.71239
    g14: GeomPoint [constr] X=0 Y=0 Z=0
    g15: LineSegment StartX=0 StartY=0.45 StartZ=0 EndX=0.45 EndY=0 EndZ=0
  constraints (35):
    c: Coincident(g14,g-1)
    c: PointOnObject(g5,g-2)
    c: Horizontal(g1)
    c: Vertical(g2)
    c: Horizontal(g3)
    c: DistanceX(g5,g8) = 2
    c: DistanceY(g11,g8) = 2
    c: PointOnObject(g5,g0)
    c: PointOnObject(g5,g1)
    c: Tangent(g0,g4) = 1.5708
    c: Tangent(g1,g4) = 1.5708
    c: Coincident(g6,g0)
    c: Coincident(g6,g1)
    c: PointOnObject(g8,g2)
    c: PointOnObject(g8,g1)
    c: Tangent(g2,g7) = 1.5708
    c: Tangent(g1,g7) = 1.5708
    c: Coincident(g9,g2)
    c: Coincident(g9,g1)
    c: PointOnObject(g11,g2)
    c: PointOnObject(g11,g3)
    c: Tangent(g2,g10) = 1.5708
    c: Tangent(g3,g10) = 1.5708
    c: Coincident(g12,g2)
    c: Coincident(g12,g3)
    c: PointOnObject(g14,g0)
    c: PointOnObject(g14,g3)
    c: Tangent(g0,g13) = 1.5708
    c: Tangent(g3,g13) = 1.5708
    c: Coincident(g15,g0)
    c: Coincident(g15,g3)
    c: Equal(g6,g9)
    c: Equal(g9,g12)
    c: Equal(g12,g15)
    c: DistanceX(g14,g3) = 0.45
FEATURE [PartDesign::Pad] Pad029
  Direction = (0,-1,2e-16)
  Length = 17
  Length2 = 10
  Midplane = true
  Placement = pos=(0,0,0) rot=(1,0,0;1.5708rad)
  Profile = -> Sketch134
  ReferenceAxis = -> Sketch134 [N_Axis]
  Refine = true
  Suppressed = false
  Type = 0
FEATURE [PartDesign::Body] Body008  label="perno fermo neopixel"
  AllowCompound = false
  Group = -> [Sketch134,Pad029]
  Origin = -> Origin008
  Tip = -> Pad029
FEATURE [Sketcher::SketchObject] Sketch135  label="perno fermo rumble003"
  ArcFitTolerance = 1e-06
  AttachmentSupport = -> [XZ_Plane009]
  FullyConstrained = true
  MakeInternals = false
  MapMode = 5
  Placement = pos=(0,0,0) rot=(1,0,0;1.5708rad)
  sketch-geometry (16):
    g0: LineSegment StartX=4.69e-14 StartY=0.8 StartZ=0 EndX=-3.04e-14 EndY=3.1 EndZ=0
    g1: LineSegment StartX=0.8 StartY=3.9 StartZ=0 EndX=3.1 EndY=3.9 EndZ=0
    g2: LineSegment StartX=3.9 StartY=3.1 StartZ=0 EndX=3.9 EndY=0.8 EndZ=0
    g3: LineSegment StartX=3.1 StartY=0 StartZ=0 EndX=0.8 EndY=0 EndZ=0
    g4: ArcOfCircle [constr] CenterX=0.8 CenterY=3.1 CenterZ=0 NormalX=0 NormalY=0 NormalZ=1 AngleXU=0 Radius=0.8 StartAngle=1.5708 EndAngle=3.14159
    g5: GeomPoint [constr] X=0 Y=3.9 Z=0
    g6: LineSegment StartX=0.8 StartY=3.9 StartZ=0 EndX=-3.04e-14 EndY=3.1 EndZ=0
    g7: ArcOfCircle [constr] CenterX=3.1 CenterY=3.1 CenterZ=0 NormalX=0 NormalY=0 NormalZ=1 AngleXU=0 Radius=0.8 StartAngle=-2.4e-14 EndAngle=1.5708
    g8: GeomPoint [constr] X=3.9 Y=3.9 Z=0
    g9: LineSegment StartX=3.9 StartY=3.1 StartZ=0 EndX=3.1 EndY=3.9 EndZ=0
    g10: ArcOfCircle [constr] CenterX=3.1 CenterY=0.8 CenterZ=0 NormalX=0 NormalY=0 NormalZ=1 AngleXU=0 Radius=0.8 StartAngle=4.71239 EndAngle=6.28319
    g11: GeomPoint [constr] X=3.9 Y=0 Z=0
    g12: LineSegment StartX=3.1 StartY=0 StartZ=0 EndX=3.9 EndY=0.8 EndZ=0
    g13: ArcOfCircle [constr] CenterX=0.8 CenterY=0.8 CenterZ=0 NormalX=0 NormalY=0 NormalZ=1 AngleXU=0 Radius=0.8 StartAngle=3.14159 EndAngle=4.71239
    g14: GeomPoint [constr] X=0 Y=0 Z=0
    g15: LineSegment StartX=4.69e-14 StartY=0.8 StartZ=0 EndX=0.8 EndY=0 EndZ=0
  constraints (35):
    c: Coincident(g14,g-1)
    c: PointOnObject(g5,g-2)
    c: Horizontal(g1)
    c: Vertical(g2)
    c: Horizontal(g3)
    c: DistanceX(g5,g8) = 3.9
    c: DistanceY(g11,g8) = 3.9
    c: PointOnObject(g5,g0)
    c: PointOnObject(g5,g1)
    c: Tangent(g0,g4) = 1.5708
    c: Tangent(g1,g4) = 1.5708
    c: Coincident(g6,g0)
    c: Coincident(g6,g1)
    c: PointOnObject(g8,g2)
    c: PointOnObject(g8,g1)
    c: Tangent(g2,g7) = 1.5708
    c: Tangent(g1,g7) = 1.5708
    c: Coincident(g9,g2)
    c: Coincident(g9,g1)
    c: PointOnObject(g11,g2)
    c: PointOnObject(g11,g3)
    c: Tangent(g2,g10) = 1.5708
    c: Tangent(g3,g10) = 1.5708
    c: Coincident(g12,g2)
    c: Coincident(g12,g3)
    c: PointOnObject(g14,g0)
    c: PointOnObject(g14,g3)
    c: Tangent(g0,g13) = 1.5708
    c: Tangent(g3,g13) = 1.5708
    c: Coincident(g15,g0)
    c: Coincident(g15,g3)
    c: Equal(g6,g9)
    c: Equal(g9,g12)
    c: Equal(g12,g15)
    c: DistanceX(g14,g3) = 0.8
FEATURE [PartDesign::Pad] Pad030
  Direction = (0,-1,2e-16)
  Length = 25.2
  Length2 = 10
  Midplane = true
  Placement = pos=(0,0,0) rot=(1,0,0;1.5708rad)
  Profile = -> Sketch135
  ReferenceAxis = -> Sketch135 [N_Axis]
  Refine = true
  Suppressed = false
  Type = 0
FEATURE [PartDesign::Body] Body009  label="perno fermo switch - caricabatterie - grilletto"
  AllowCompound = false
  Group = -> [Sketch135,Pad030]
  Origin = -> Origin009
  Tip = -> Pad030
FEATURE [Sketcher::SketchObject] Sketch136  label="scavo_rele"
  ArcFitTolerance = 1e-06
  AttachmentSupport = -> [XZ_Plane]
  ExternalGeometry = -> [Sketch]
  FullyConstrained = true
  MakeInternals = false
  MapMode = 5
  Placement = pos=(0,0,0) rot=(1,0,0;1.5708rad)
  sketch-geometry (7):
    g0: LineSegment [constr] StartX=-173.013 StartY=-62.644 StartZ=0 EndX=-176.535 EndY=-73.4861 EndZ=0
    g1: LineSegment [constr] StartX=-173.013 StartY=-62.644 StartZ=0 EndX=-170.35 EndY=-63.5093 EndZ=0
    g2: LineSegment [constr] StartX=-173.013 StartY=-62.644 StartZ=0 EndX=-176.627 EndY=-61.4698 EndZ=0
    g3: LineSegment StartX=-176.627 StartY=-61.4698 StartZ=0 EndX=-170.35 EndY=-63.5093 EndZ=0
    g4: LineSegment StartX=-176.627 StartY=-61.4698 StartZ=0 EndX=-180.149 EndY=-72.3118 EndZ=0
    g5: LineSegment StartX=-170.35 StartY=-63.5093 StartZ=0 EndX=-173.872 EndY=-74.3513 EndZ=0
    g6: LineSegment StartX=-180.149 StartY=-72.3118 StartZ=0 EndX=-173.872 EndY=-74.3513 EndZ=0
  constraints (19):
    c: Tangent(g0,g-3)
    c: Distance(g0,g-3) = 89
    c: Distance(g0,g0) = 11.4
    c: Coincident(g1,g0)
    c: Coincident(g2,g0)
    c: Distance(g2) = 3.8
    c: Distance(g1) = 2.8
    c: Perpendicular(g0,g1)
    c: Perpendicular(g0,g2)
    c: Coincident(g3,g2)
    c: Coincident(g3,g1)
    c: Equal(g4,g0)
    c: Equal(g5,g0)
    c: Parallel(g4,g0)
    c: Parallel(g5,g0)
    c: Coincident(g4,g2)
    c: Coincident(g5,g1)
    c: Coincident(g6,g4)
    c: Coincident(g6,g5)
FEATURE [Part::Extrusion] Extrude076  label="Extrude076 - scavo_rele"
  Base = -> Sketch136
  Dir = (0,-1,2e-16)
  DirMode = 2
  FaceMakerClass = Part::FaceMakerBullseye
  FaceMakerMode = 3
  LengthFwd = 17.8
  LengthRev = 0
  Solid = true
  Symmetric = true
FEATURE [Sketcher::SketchObject] Sketch137  label="scavo_nuovo_driver"
  ArcFitTolerance = 1e-06
  AttachmentSupport = -> [XZ_Plane]
  ExternalGeometry = -> [Sketch]
  FullyConstrained = true
  MakeInternals = false
  MapMode = 5
  Placement = pos=(0,0,0) rot=(1,0,0;1.5708rad)
  sketch-geometry (7):
    g0: LineSegment [constr] StartX=-167.759 StartY=-46.4761 StartZ=0 EndX=-172.58 EndY=-61.3126 EndZ=0
    g1: LineSegment [constr] StartX=-167.759 StartY=-46.4761 StartZ=0 EndX=-165.477 EndY=-47.2177 EndZ=0
    g2: LineSegment [constr] StartX=-167.759 StartY=-46.4761 StartZ=0 EndX=-171.373 EndY=-45.3018 EndZ=0
    g3: LineSegment StartX=-171.373 StartY=-45.3018 StartZ=0 EndX=-165.477 EndY=-47.2177 EndZ=0
    g4: LineSegment StartX=-171.373 StartY=-45.3018 StartZ=0 EndX=-176.194 EndY=-60.1383 EndZ=0
    g5: LineSegment StartX=-165.477 StartY=-47.2177 StartZ=0 EndX=-170.297 EndY=-62.0542 EndZ=0
    g6: LineSegment StartX=-176.194 StartY=-60.1383 StartZ=0 EndX=-170.297 EndY=-62.0542 EndZ=0
  constraints (19):
    c: Distance(g0,g-3) = 72
    c: Distance(g0) = 15.6
    c: Tangent(g0,g-3)
    c: Coincident(g1,g0)
    c: Coincident(g2,g0)
    c: Distance(g1) = 2.4
    c: Distance(g2) = 3.8
    c: Perpendicular(g0,g1)
    c: Perpendicular(g0,g2)
    c: Coincident(g3,g2)
    c: Coincident(g3,g1)
    c: Equal(g4,g0)
    c: Equal(g5,g0)
    c: Parallel(g4,g0)
    c: Parallel(g5,g0)
    c: Coincident(g4,g2)
    c: Coincident(g5,g1)
    c: Coincident(g6,g4)
    c: Coincident(g6,g5)
FEATURE [Part::Extrusion] Extrude077  label="Extrude077 - scavo_nuovo_driver"
  Base = -> Sketch137
  Dir = (0,-1,2e-16)
  DirMode = 2
  FaceMakerClass = Part::FaceMakerBullseye
  FaceMakerMode = 3
  LengthFwd = 20.8
  LengthRev = 0
  Solid = true
  Symmetric = true
FEATURE [Sketcher::SketchObject] Sketch138  label="scavo_nuovo_driver_alto"
  ArcFitTolerance = 1e-06
  AttachmentSupport = -> [XZ_Plane]
  ExternalGeometry = -> [Sketch]
  FullyConstrained = true
  MakeInternals = false
  MapMode = 5
  Placement = pos=(0,0,0) rot=(1,0,0;1.5708rad)
  sketch-geometry (7):
    g0: LineSegment [constr] StartX=-188.796 StartY=17.7274 StartZ=0 EndX=-187.75 EndY=4.97025 EndZ=0
    g1: LineSegment StartX=-187.75 StartY=4.97025 StartZ=0 EndX=-189.743 EndY=4.8067 EndZ=0
    g2: LineSegment StartX=-187.75 StartY=4.97025 StartZ=0 EndX=-182.766 EndY=5.37913 EndZ=0
    g3: LineSegment StartX=-190.79 StartY=17.5638 StartZ=0 EndX=-189.743 EndY=4.8067 EndZ=0
    g4: LineSegment StartX=-183.813 StartY=18.1363 StartZ=0 EndX=-182.766 EndY=5.37913 EndZ=0
    g5: LineSegment StartX=-190.79 StartY=17.5638 StartZ=0 EndX=-188.796 EndY=17.7274 EndZ=0
    g6: LineSegment StartX=-188.796 StartY=17.7274 StartZ=0 EndX=-183.813 EndY=18.1363 EndZ=0
  constraints (20):
    c: Distance(g0) = 12.8
    c: DistanceY(g-3,g0) = 9
    c: PointOnObject(g0,g-4)
    c: PointOnObject(g0,g-4)
    c: Coincident(g1,g0)
    c: Coincident(g2,g0)
    c: Distance(g1) = 2
    c: Distance(g2) = 5
    c: Perpendicular(g0,g1)
    c: Perpendicular(g0,g2)
    c: Equal(g3,g0)
    c: Parallel(g3,g0)
    c: Coincident(g3,g1)
    c: Equal(g4,g0)
    c: Parallel(g4,g0)
    c: Coincident(g4,g2)
    c: Coincident(g5,g3)
    c: Coincident(g5,g0)
    c: Coincident(g6,g0)
    c: Coincident(g6,g4)
FEATURE [Part::Extrusion] Extrude078  label="Extrude078 - scavo_nuovo_driver_alto"
  Base = -> Sketch138
  Dir = (0,-1,2e-16)
  DirMode = 2
  FaceMakerClass = Part::FaceMakerBullseye
  FaceMakerMode = 3
  LengthFwd = 16.6
  LengthRev = 0
  Solid = true
  Symmetric = true
FEATURE [Sketcher::SketchObject] Sketch139  label="fermi_nuovo_driver_alto"
  ArcFitTolerance = 1e-06
  AttachmentSupport = -> [XZ_Plane]
  ExternalGeometry = -> [Sketch138,Sketch]
  FullyConstrained = true
  MakeInternals = false
  MapMode = 5
  Placement = pos=(0,0,0) rot=(1,0,0;1.5708rad)
  sketch-geometry (17):
    g0: LineSegment [constr] StartX=-188.314 StartY=16.4295 StartZ=0 EndX=-187.885 EndY=13.7638 EndZ=0
    g1: LineSegment [constr] StartX=-187.885 StartY=13.7638 StartZ=0 EndX=-187.456 EndY=11.0981 EndZ=0
    g2: LineSegment StartX=-187.885 StartY=13.7638 StartZ=0 EndX=-187.71 EndY=12.6778 EndZ=0
    g3: LineSegment StartX=-187.885 StartY=13.7638 StartZ=0 EndX=-188.06 EndY=14.8499 EndZ=0
    g4: LineSegment StartX=-187.71 StartY=12.6778 StartZ=0 EndX=-185.538 EndY=13.0274 EndZ=0
    g5: LineSegment StartX=-188.06 StartY=14.8499 StartZ=0 EndX=-185.888 EndY=15.1994 EndZ=0
    g6: LineSegment StartX=-185.888 StartY=15.1994 StartZ=0 EndX=-185.538 EndY=13.0274 EndZ=0
    g7: LineSegment StartX=-187.456 StartY=11.0981 StartZ=0 EndX=-189.035 EndY=10.8439 EndZ=0
    g8: LineSegment StartX=-188.314 StartY=16.4295 StartZ=0 EndX=-189.893 EndY=16.1753 EndZ=0
    g9: LineSegment StartX=-189.893 StartY=16.1753 StartZ=0 EndX=-189.035 EndY=10.8439 EndZ=0
    g10: LineSegment StartX=-187.456 StartY=11.0981 StartZ=0 EndX=-185.284 EndY=11.4477 EndZ=0
    g11: LineSegment StartX=-188.314 StartY=16.4295 StartZ=0 EndX=-186.142 EndY=16.7791 EndZ=0
    g12: LineSegment StartX=-184.308 StartY=15.4537 StartZ=0 EndX=-183.958 EndY=13.2816 EndZ=0
    g13: ArcOfCircle CenterX=-185.888 CenterY=15.1994 CenterZ=0 NormalX=0 NormalY=0 NormalZ=1 AngleXU=0 Radius=1.6 StartAngle=0.15957 EndAngle=1.73037
    g14: GeomPoint [constr] X=-184.562 Y=17.0333 Z=0
    g15: ArcOfCircle CenterX=-185.538 CenterY=13.0274 CenterZ=0 NormalX=0 NormalY=0 NormalZ=1 AngleXU=0 Radius=1.6 StartAngle=4.87196 EndAngle=6.44276
    g16: GeomPoint [constr] X=-183.704 Y=11.7019 Z=0
  constraints (43):
    c: Tangent(g1,g0) = -1.5708
    c: Distance(g0) = 2.7
    c: Equal(g1,g0)
    c: Tangent(g1,g-5)
    c: Coincident(g2,g0)
    c: Coincident(g3,g0)
    c: Distance(g2) = 1.1
    c: Equal(g3,g2)
    c: PointOnObject(g3,g2)
    c: Coincident(g4,g2)
    c: Coincident(g5,g3)
    c: Distance(g4) = 2.2
    c: Equal(g4,g5)
    c: Perpendicular(g1,g4)
    c: Perpendicular(g0,g5)
    c: Coincident(g6,g5)
    c: Coincident(g6,g4)
    c: Coincident(g7,g1)
    c: Coincident(g8,g0)
    c: Distance(g7) = 1.6
    c: Equal(g7,g8)
    c: Perpendicular(g1,g7)
    c: Perpendicular(g8,g0)
    c: Coincident(g9,g8)
    c: Coincident(g9,g7)
    c: Coincident(g10,g1)
    c: Coincident(g11,g0)
    c: Distance(g10,g16) = 3.8
    c: Perpendicular(g1,g10)
    c: Perpendicular(g1,g11)
    c: DistanceY(g0,g-4) = 3.8
    c: PointOnObject(g14,g12)
    c: PointOnObject(g14,g11)
    c: Tangent(g12,g13) = 1.5708
    c: Tangent(g11,g13) = 1.5708
    c: PointOnObject(g16,g12)
    c: PointOnObject(g16,g10)
    c: Tangent(g12,g15) = 1.5708
    c: Tangent(g10,g15) = -1.5708
    c: Equal(g13,g15)
    c: Coincident(g13,g5)
    c: Parallel(g2,g0)
    c: PointOnObject(g0,g-5)
FEATURE [Part::Extrusion] Extrude079  label="Extrude079 - fermi_nuovo_driver_alto"
  Base = -> Sketch139
  Dir = (0,-1,2e-16)
  DirMode = 2
  FaceMakerClass = Part::FaceMakerBullseye
  FaceMakerMode = 3
  LengthFwd = 25.2
  LengthRev = 0
  Solid = true
  Symmetric = true
FEATURE [Sketcher::SketchObject] Sketch140  label="scavo_diodo_nuovo_driver_alto"
  ArcFitTolerance = 1e-06
  AttachmentSupport = -> [XZ_Plane]
  ExternalGeometry = -> [Sketch138]
  FullyConstrained = true
  MakeInternals = false
  MapMode = 5
  Placement = pos=(0,0,0) rot=(1,0,0;1.5708rad)
  sketch-geometry (4):
    g0: LineSegment StartX=-190.79 StartY=17.5638 StartZ=0 EndX=-189.743 EndY=4.8067 EndZ=0
    g1: LineSegment StartX=-193.78 StartY=17.3185 StartZ=0 EndX=-192.733 EndY=4.56137 EndZ=0
    g2: LineSegment StartX=-190.79 StartY=17.5638 StartZ=0 EndX=-193.78 EndY=17.3185 EndZ=0
    g3: LineSegment StartX=-192.733 StartY=4.56137 StartZ=0 EndX=-189.743 EndY=4.8067 EndZ=0
  constraints (11):
    c: Equal(g0,g-3)
    c: Parallel(g0,g-3)
    c: Equal(g1,g-3)
    c: Parallel(g1,g-3)
    c: Coincident(g2,g0)
    c: Distance(g2) = 3
    c: Perpendicular(g0,g2)
    c: Coincident(g1,g2)
    c: Coincident(g3,g1)
    c: Coincident(g3,g0)
    c: Coincident(g0,g-3)
FEATURE [Part::Extrusion] Extrude080  label="Extrude080 - scavo_diodo_nuovo_driver_alto"
  Base = -> Sketch140
  Dir = (0,-1,2e-16)
  DirMode = 2
  FaceMakerClass = Part::FaceMakerBullseye
  FaceMakerMode = 3
  LengthFwd = 4
  LengthRev = 0
  Placement = pos=(0,7.8,0) rot=(0,0,1;0rad)
  Solid = true
  Symmetric = false
FEATURE [Part::MultiFuse] Fusion001
  Refine = true
  Shapes = -> [Cut043,Extrude079]
FEATURE [Part::Cut] Cut044
  Base = -> Fusion001
  Refine = true
  Tool = -> Extrude078
FEATURE [Part::Cut] Cut045
  Base = -> Cut044
  Refine = true
  Tool = -> Extrude080
FEATURE [Sketcher::SketchObject] Sketch141  label="fermi_nuovo_driver"
  ArcFitTolerance = 1e-06
  AttachmentSupport = -> [XZ_Plane]
  ExternalGeometry = -> [Sketch,Sketch137]
  FullyConstrained = true
  MakeInternals = false
  MapMode = 5
  Placement = pos=(0,0,0) rot=(1,0,0;1.5708rad)
  sketch-geometry (16):
    g0: LineSegment [constr] StartX=-165.477 StartY=-47.2177 StartZ=0 EndX=-167.759 EndY=-46.4761 EndZ=0
    g1: LineSegment [constr] StartX=-167.759 StartY=-46.4761 StartZ=0 EndX=-168.006 EndY=-47.2369 EndZ=0
    g2: LineSegment [constr] StartX=-168.006 StartY=-47.2369 StartZ=0 EndX=-169.675 EndY=-52.3726 EndZ=0
    g3: LineSegment StartX=-169.675 StartY=-52.3726 StartZ=0 EndX=-171.767 EndY=-51.6928 EndZ=0
    g4: LineSegment StartX=-172.795 StartY=-49.6767 StartZ=0 EndX=-172.115 EndY=-47.5843 EndZ=0
    g5: LineSegment StartX=-170.099 StartY=-46.5571 StartZ=0 EndX=-166.485 EndY=-47.7313 EndZ=0
    g6: LineSegment StartX=-166.485 StartY=-47.7313 StartZ=0 EndX=-168.153 EndY=-52.867 EndZ=0
    g7: LineSegment StartX=-169.675 StartY=-52.3726 StartZ=0 EndX=-168.153 EndY=-52.867 EndZ=0
    g8: LineSegment StartX=-170.593 StartY=-48.0788 StartZ=0 EndX=-171.273 EndY=-50.1711 EndZ=0
    g9: LineSegment StartX=-171.273 StartY=-50.1711 StartZ=0 EndX=-169.181 EndY=-50.8509 EndZ=0
    g10: LineSegment StartX=-169.181 StartY=-50.8509 StartZ=0 EndX=-168.501 EndY=-48.7586 EndZ=0
    g11: LineSegment StartX=-168.501 StartY=-48.7586 StartZ=0 EndX=-170.593 EndY=-48.0788 EndZ=0
    g12: ArcOfCircle CenterX=-170.593 CenterY=-48.0788 CenterZ=0 NormalX=0 NormalY=0 NormalZ=1 AngleXU=0 Radius=1.6 StartAngle=1.25664 EndAngle=2.82743
    g13: GeomPoint [constr] X=-171.62 Y=-46.0626 Z=0
    g14: ArcOfCircle CenterX=-171.273 CenterY=-50.1711 CenterZ=0 NormalX=0 NormalY=0 NormalZ=1 AngleXU=0 Radius=1.6 StartAngle=2.82743 EndAngle=4.39823
    g15: GeomPoint [constr] X=-173.289 Y=-51.1984 Z=0
  constraints (41):
    c: Coincident(g0,g-4)
    c: PointOnObject(g0,g-3)
    c: Parallel(g0,g-4)
    c: Coincident(g1,g0)
    c: Parallel(g1,g-3)
    c: Distance(g1) = 0.8
    c: Coincident(g2,g1)
    c: Distance(g2) = 5.4
    c: Coincident(g3,g2)
    c: Parallel(g2,g-3)
    c: Distance(g15,g13) = 5.4
    c: Perpendicular(g3,g2)
    c: Parallel(g4,g2)
    c: Distance(g5,g13) = 5.4
    c: Distance(g3,g15) = 3.8
    c: Perpendicular(g4,g5)
    c: Coincident(g6,g5)
    c: Distance(g6) = 5.4
    c: Parallel(g6,g4)
    c: Coincident(g7,g2)
    c: Coincident(g7,g6)
    c: Coincident(g8,g9)
    c: Coincident(g9,g10)
    c: Coincident(g10,g11)
    c: Coincident(g11,g8)
    c: Distance(g8,g10) = 2.2
    c: Distance(g9,g11) = 2.2
    c: Perpendicular(g11,g8)
    c: Equal(g8,g10)
    c: Equal(g11,g9)
    c: Tangent(g10,g2)
    c: Distance(g10,g1) = 1.6
    c: PointOnObject(g13,g4)
    c: PointOnObject(g13,g5)
    c: Tangent(g4,g12) = 1.5708
    c: Tangent(g5,g12) = 1.5708
    c: PointOnObject(g15,g4)
    c: Tangent(g4,g14) = 1.5708
    c: Tangent(g3,g14) = 1.5708
    c: Equal(g14,g12)
    c: Coincident(g12,g8)
FEATURE [Part::Extrusion] Extrude081  label="Extrude081 - fermi_nuovo_driver"
  Base = -> Sketch141
  Dir = (0,-1,2e-16)
  DirMode = 2
  FaceMakerClass = Part::FaceMakerBullseye
  FaceMakerMode = 3
  LengthFwd = 25.2
  LengthRev = 0
  Solid = true
  Symmetric = true
FEATURE [Part::MultiFuse] Fusion002
  Refine = true
  Shapes = -> [Cut045,Extrude081]
FEATURE [Part::Cut] Cut046
  Base = -> Fusion002
  Refine = true
  Tool = -> Extrude077
FEATURE [Sketcher::SketchObject] Sketch142  label="fermi_rele"
  ArcFitTolerance = 1e-06
  AttachmentSupport = -> [XZ_Plane]
  ExternalGeometry = -> [Sketch,Sketch136]
  FullyConstrained = true
  MakeInternals = false
  MapMode = 5
  Placement = pos=(0,0,0) rot=(1,0,0;1.5708rad)
  sketch-geometry (15):
    g0: LineSegment StartX=-177.245 StartY=-63.3719 StartZ=0 EndX=-177.924 EndY=-65.4642 EndZ=0
    g1: LineSegment StartX=-175.228 StartY=-62.3446 StartZ=0 EndX=-171.614 EndY=-63.5189 EndZ=0
    g2: LineSegment StartX=-171.614 StartY=-63.5189 StartZ=0 EndX=-173.283 EndY=-68.6546 EndZ=0
    g3: LineSegment StartX=-176.897 StartY=-67.4803 StartZ=0 EndX=-173.283 EndY=-68.6546 EndZ=0
    g4: LineSegment StartX=-175.723 StartY=-63.8663 StartZ=0 EndX=-173.631 EndY=-64.5461 EndZ=0
    g5: LineSegment StartX=-175.723 StartY=-63.8663 StartZ=0 EndX=-176.403 EndY=-65.9586 EndZ=0
    g6: LineSegment StartX=-173.631 StartY=-64.5461 StartZ=0 EndX=-174.31 EndY=-66.6385 EndZ=0
    g7: LineSegment StartX=-176.403 StartY=-65.9586 StartZ=0 EndX=-174.31 EndY=-66.6385 EndZ=0
    g8: LineSegment [constr] StartX=-173.631 StartY=-64.5461 StartZ=0 EndX=-173.136 EndY=-63.0245 EndZ=0
    g9: LineSegment [constr] StartX=-173.631 StartY=-64.5461 StartZ=0 EndX=-172.109 EndY=-65.0406 EndZ=0
    g10: LineSegment [constr] StartX=-170.35 StartY=-63.5093 StartZ=0 EndX=-173.013 EndY=-62.644 EndZ=0
    g11: ArcOfCircle CenterX=-175.723 CenterY=-63.8663 CenterZ=0 NormalX=0 NormalY=0 NormalZ=1 AngleXU=0 Radius=1.6 StartAngle=1.25664 EndAngle=2.82743
    g12: GeomPoint [constr] X=-176.75 Y=-61.8502 Z=0
    g13: ArcOfCircle CenterX=-176.403 CenterY=-65.9586 CenterZ=0 NormalX=0 NormalY=0 NormalZ=1 AngleXU=0 Radius=1.6 StartAngle=2.82743 EndAngle=4.39823
    g14: GeomPoint [constr] X=-178.419 Y=-66.9859 Z=0
  constraints (39):
    c: Distance(g14,g12) = 5.4
    c: Distance(g1,g12) = 5.4
    c: Perpendicular(g1,g0)
    c: Coincident(g2,g1)
    c: Parallel(g2,g0)
    c: Coincident(g3,g2)
    c: Parallel(g2,g-3)
    c: Coincident(g5,g4)
    c: Distance(g5) = 2.2
    c: Distance(g4) = 2.2
    c: Perpendicular(g4,g5)
    c: Coincident(g6,g4)
    c: Equal(g6,g5)
    c: Parallel(g6,g5)
    c: Coincident(g7,g5)
    c: Coincident(g7,g6)
    c: Coincident(g8,g4)
    c: Coincident(g9,g4)
    c: Distance(g8) = 1.6
    c: Distance(g9) = 1.6
    c: Parallel(g8,g6)
    c: Parallel(g9,g4)
    c: PointOnObject(g8,g1)
    c: PointOnObject(g9,g2)
    c: Coincident(g10,g-4)
    c: Parallel(g10,g-4)
    c: PointOnObject(g10,g-3)
    c: Tangent(g6,g-3) = 1.5708
    c: Distance(g4,g10) = 2
    c: PointOnObject(g12,g1)
    c: Tangent(g1,g11) = 1.5708
    c: Tangent(g0,g11) = -1.5708
    c: PointOnObject(g14,g3)
    c: PointOnObject(g14,g0)
    c: Tangent(g3,g13) = -1.5708
    c: Tangent(g0,g13) = -1.5708
    c: Equal(g11,g13)
    c: Coincident(g11,g4)
    c: Parallel(g3,g1)
FEATURE [Part::Extrusion] Extrude082  label="Extrude082 - fermi_rele"
  Base = -> Sketch142
  Dir = (0,-1,2e-16)
  DirMode = 2
  FaceMakerClass = Part::FaceMakerBullseye
  FaceMakerMode = 3
  LengthFwd = 25.2
  LengthRev = 0
  Solid = true
  Symmetric = true
FEATURE [Part::MultiFuse] Fusion003
  Refine = true
  Shapes = -> [Cut046,Extrude082]
FEATURE [Part::Cut] Cut047
  Base = -> Fusion003
  Refine = true
  Tool = -> Extrude076
FEATURE [Sketcher::SketchObject] Sketch143  label="foro_passaggio_cavi_led_batteria"
  ArcFitTolerance = 1e-06
  AttachmentSupport = -> [XZ_Plane]
  ExternalGeometry = -> [Sketch,Sketch042,Sketch036]
  FullyConstrained = true
  MakeInternals = false
  MapMode = 5
  Placement = pos=(0,0,0) rot=(1,0,0;1.5708rad)
  sketch-geometry (4):
    g0: LineSegment StartX=-207.775 StartY=-41.3701 StartZ=0 EndX=-213.607 EndY=-53.8767 EndZ=0
    g1: LineSegment StartX=-213.607 StartY=-53.8767 StartZ=0 EndX=-211.843 EndY=-59.5559 EndZ=0
    g2: LineSegment StartX=-207.775 StartY=-41.3701 StartZ=0 EndX=-207.775 EndY=-50.8316 EndZ=0
    g3: LineSegment StartX=-207.775 StartY=-50.8316 StartZ=0 EndX=-211.843 EndY=-59.5559 EndZ=0
  constraints (9):
    c: Coincident(g0,g-3)
    c: PointOnObject(g1,g-6)
    c: Coincident(g1,g0)
    c: Coincident(g2,g0)
    c: Coincident(g2,g-7)
    c: Coincident(g3,g2)
    c: Parallel(g3,g0)
    c: Coincident(g3,g1)
    c: Coincident(g0,g-5)
FEATURE [Part::Extrusion] Extrude083  label="Extrude083 - foro_passaggio_cavi_led_batteria"
  Base = -> Sketch143
  Dir = (0,-1,2e-16)
  DirMode = 2
  FaceMakerClass = Part::FaceMakerBullseye
  FaceMakerMode = 3
  LengthFwd = 6
  LengthRev = 0
  Solid = true
  Symmetric = true
FEATURE [Part::Cut] Cut048
  Base = -> Cut047
  Refine = true
  Tool = -> Extrude083
FEATURE [Sketcher::SketchObject] Sketch144  label="foro_areazione_alimentatore"
  ArcFitTolerance = 1e-06
  AttachmentSupport = -> [XZ_Plane]
  ExternalGeometry = -> [Sketch036]
  FullyConstrained = true
  MakeInternals = false
  MapMode = 5
  Placement = pos=(0,0,0) rot=(1,0,0;1.5708rad)
  sketch-geometry (4):
    g0: LineSegment StartX=-211.843 StartY=-60.3701 StartZ=0 EndX=-207.775 EndY=-60.3701 EndZ=0
    g1: LineSegment StartX=-207.775 StartY=-60.3701 StartZ=0 EndX=-207.775 EndY=-70.3701 EndZ=0
    g2: LineSegment StartX=-211.843 StartY=-60.3701 StartZ=0 EndX=-211.843 EndY=-70.3701 EndZ=0
    g3: LineSegment StartX=-207.775 StartY=-70.3701 StartZ=0 EndX=-211.843 EndY=-70.3701 EndZ=0
  constraints (11):
    c: Horizontal(g0)
    c: Distance(g1) = 10
    c: Coincident(g1,g0)
    c: Tangent(g1,g-3)
    c: PointOnObject(g0,g-4)
    c: Coincident(g2,g0)
    c: PointOnObject(g2,g-4)
    c: Coincident(g3,g1)
    c: Horizontal(g3)
    c: Coincident(g3,g2)
    c: DistanceY(g0,g-3) = 19
FEATURE [Part::Extrusion] Extrude084  label="Extrude084 - foro_areazione_alimentatore"
  Base = -> Sketch144
  Dir = (0,-1,2e-16)
  DirMode = 2
  FaceMakerClass = Part::FaceMakerBullseye
  FaceMakerMode = 3
  LengthFwd = 10
  LengthRev = 0
  Solid = true
  Symmetric = true
FEATURE [Part::Cut] Cut049
  Base = -> Cut048
  Refine = true
  Tool = -> Extrude084
FEATURE [Sketcher::SketchObject] Sketch145  label="foro_per_condesatore"
  ArcFitTolerance = 1e-06
  AttachmentSupport = -> [XZ_Plane]
  ExternalGeometry = -> [Sketch,Sketch139]
  FullyConstrained = true
  MakeInternals = false
  MapMode = 5
  Placement = pos=(0,0,0) rot=(1,0,0;1.5708rad)
  sketch-geometry (1):
    g0: Circle CenterX=-182.345 CenterY=7.02342 CenterZ=0 NormalX=0 NormalY=0 NormalZ=1 AngleXU=0 Radius=5.2
  constraints (3):
    c: Diameter(g0) = 10.4
    c: Tangent(g0,g-3)
    c: Tangent(g0,g-4)
FEATURE [Part::Extrusion] Extrude085  label="Extrude085 - foro_per_condesatore"
  Base = -> Sketch145
  Dir = (0,-1,2e-16)
  DirMode = 2
  FaceMakerClass = Part::FaceMakerBullseye
  FaceMakerMode = 3
  LengthFwd = 25.2
  LengthRev = 0
  Solid = true
  Symmetric = true
FEATURE [Part::Cut] Cut050
  Base = -> Cut049
  Refine = true
  Tool = -> Extrude085
FEATURE [Sketcher::SketchObject] Sketch146  label="scavo_pulsante_6x6_per_led_batteria"
  ArcFitTolerance = 1e-06
  AttachmentSupport = -> [XZ_Plane]
  ExternalGeometry = -> [Sketch016]
  FullyConstrained = true
  MakeInternals = false
  MapMode = 5
  Placement = pos=(0,0,0) rot=(1,0,0;1.5708rad)
  sketch-geometry (5):
    g0: LineSegment StartX=-216.643 StartY=-65.8316 StartZ=0 EndX=-216.643 EndY=-72.8316 EndZ=0
    g1: LineSegment StartX=-216.643 StartY=-72.8316 StartZ=0 EndX=-210.243 EndY=-72.8316 EndZ=0
    g2: LineSegment StartX=-210.243 StartY=-72.8316 StartZ=0 EndX=-210.243 EndY=-65.8316 EndZ=0
    g3: LineSegment StartX=-210.243 StartY=-65.8316 StartZ=0 EndX=-216.643 EndY=-65.8316 EndZ=0
    g4: GeomPoint [constr] X=-213.443 Y=-69.3316 Z=0
  constraints (13):
    c: Coincident(g0,g1)
    c: Coincident(g1,g2)
    c: Coincident(g2,g3)
    c: Coincident(g3,g0)
    c: Vertical(g0)
    c: Vertical(g2)
    c: Horizontal(g1)
    c: Horizontal(g3)
    c: Distance(g0,g2) = 6.4
    c: Distance(g1,g3) = 7
    c: Tangent(g1,g-3)
    c: Symmetric(g0,g2,g4)
    c: Vertical(g-3,g4)
FEATURE [Part::Extrusion] Extrude086  label="Extrude086 - scavo_pulsante_6x6_per_led_batteria"
  Base = -> Sketch146
  Dir = (0,-1,2e-16)
  DirMode = 2
  FaceMakerClass = Part::FaceMakerBullseye
  FaceMakerMode = 3
  LengthFwd = 4
  LengthRev = 0
  Placement = pos=(0,12.6,0) rot=(0,0,1;0rad)
  Solid = true
  Symmetric = false
FEATURE [Sketcher::SketchObject] Sketch147  label="scavo_led_stato_batteria"
  ArcFitTolerance = 1e-06
  AttachmentSupport = -> [XZ_Plane]
  ExternalGeometry = -> [Sketch016]
  FullyConstrained = true
  MakeInternals = false
  MapMode = 5
  Placement = pos=(0,0,0) rot=(1,0,0;1.5708rad)
  sketch-geometry (5):
    g0: LineSegment StartX=-215.843 StartY=-56.2316 StartZ=0 EndX=-215.843 EndY=-65.4316 EndZ=0
    g1: LineSegment StartX=-215.843 StartY=-65.4316 StartZ=0 EndX=-211.043 EndY=-65.4316 EndZ=0
    g2: LineSegment StartX=-211.043 StartY=-65.4316 StartZ=0 EndX=-211.043 EndY=-56.2316 EndZ=0
    g3: LineSegment StartX=-211.043 StartY=-56.2316 StartZ=0 EndX=-215.843 EndY=-56.2316 EndZ=0
    g4: GeomPoint [constr] X=-213.443 Y=-60.8316 Z=0
  constraints (13):
    c: Coincident(g0,g1)
    c: Coincident(g1,g2)
    c: Coincident(g2,g3)
    c: Coincident(g3,g0)
    c: Distance(g0,g2) = 4.8
    c: Distance(g1,g3) = 9.2
    c: Equal(g0,g2)
    c: Equal(g1,g3)
    c: Perpendicular(g3,g0)
    c: DistanceY(g-3,g0) = 11.4
    c: Vertical(g2)
    c: Symmetric(g0,g2,g4)
    c: Vertical(g4,g-3)
FEATURE [Part::Extrusion] Extrude087  label="Extrude087 - scavo_led_stato_batteria"
  Base = -> Sketch147
  Dir = (0,-1,2e-16)
  DirMode = 2
  FaceMakerClass = Part::FaceMakerBullseye
  FaceMakerMode = 3
  LengthFwd = 2.2
  LengthRev = 0
  Placement = pos=(0,12.6,0) rot=(0,0,1;0rad)
  Solid = true
  Symmetric = false
FEATURE [Sketcher::SketchObject] Sketch148
  ArcFitTolerance = 1e-06
  AttachmentSupport = -> [Pad016]
  ExternalGeometry = -> [Pad016]
  FullyConstrained = true
  MakeInternals = false
  MapMode = 5
  Placement = pos=(0,0,-80.4316) rot=(1,0,0;3.14159rad)
  sketch-geometry (8):
    g0: LineSegment StartX=-176.685 StartY=3.6 StartZ=0 EndX=-186.685 EndY=3.6 EndZ=0
    g1: LineSegment StartX=-176.685 StartY=3.6 StartZ=0 EndX=-176.685 EndY=-9e-16 EndZ=0
    g2: LineSegment [constr] StartX=-186.685 StartY=3.6 StartZ=0 EndX=-186.685 EndY=-9e-16 EndZ=0
    g3: ArcOfEllipse CenterX=-186.685 CenterY=-1e-15 CenterZ=0 NormalX=0 NormalY=0 NormalZ=1 MajorRadius=10 MinorRadius=3.6 AngleXU=0 StartAngle=0 EndAngle=1.5708
    g4: LineSegment [constr] StartX=-176.685 StartY=-1e-15 StartZ=0 EndX=-196.685 EndY=-1e-15 EndZ=0
    g5: LineSegment [constr] StartX=-186.685 StartY=3.6 StartZ=0 EndX=-186.685 EndY=-3.6 EndZ=0
    g6: GeomPoint [constr] X=-177.356 Y=-1e-15 Z=0
    g7: GeomPoint [constr] X=-196.015 Y=-1e-15 Z=0
  constraints (13):
    c: Distance(g0) = 10
    c: Coincident(g0,g-5)
    c: PointOnObject(g0,g-3)
    c: Coincident(g1,g0)
    c: Coincident(g1,g-5)
    c: Coincident(g2,g0)
    c: Vertical(g2)
    c: PointOnObject(g2,g-4)
    c: InternalAlignment(g4-g7 -> g3) x4
    c: Coincident(g3,g2)
    c: Coincident(g3,g0)
    c: Coincident(g3,g1)
    c: Horizontal(g4)
FEATURE [PartDesign::SubtractivePipe] SubtractivePipe004
  AuxilleryCurvelinear = true
  AuxillerySpineTangent = false
  BaseFeature = -> Pad016
  Binormal = (0,0,0)
  Mode = 0
  Profile = -> Sketch148
  Refine = true
  Spine = -> Pad016 [Edge254]
  SpineTangent = false
  Suppressed = false
  Transformation = 0
  Transition = 0
FEATURE [Sketcher::SketchObject] Sketch149
  ArcFitTolerance = 1e-06
  AttachmentSupport = -> [Pad016]
  ExternalGeometry = -> [Pad016]
  FullyConstrained = true
  MakeInternals = false
  MapMode = 5
  Placement = pos=(0,0,-80.4316) rot=(1,0,0;3.14159rad)
  sketch-geometry (8):
    g0: LineSegment StartX=-215.932 StartY=3.6 StartZ=0 EndX=-205.932 EndY=3.6 EndZ=0
    g1: LineSegment StartX=-215.932 StartY=3.6 StartZ=0 EndX=-215.932 EndY=-4e-16 EndZ=0
    g2: LineSegment [constr] StartX=-205.932 StartY=3.6 StartZ=0 EndX=-205.932 EndY=-9e-16 EndZ=0
    g3: ArcOfEllipse CenterX=-205.932 CenterY=-1e-15 CenterZ=0 NormalX=0 NormalY=0 NormalZ=1 MajorRadius=10 MinorRadius=3.6 AngleXU=-3.14159 StartAngle=4.71239 EndAngle=6.28319
    g4: LineSegment [constr] StartX=-215.932 StartY=-1e-15 StartZ=0 EndX=-195.932 EndY=-1e-15 EndZ=0
    g5: LineSegment [constr] StartX=-205.932 StartY=-3.6 StartZ=0 EndX=-205.932 EndY=3.6 EndZ=0
    g6: GeomPoint [constr] X=-215.262 Y=-1.1e-15 Z=0
    g7: GeomPoint [constr] X=-196.602 Y=-9e-16 Z=0
  constraints (13):
    c: Distance(g0) = 10
    c: Coincident(g0,g-5)
    c: PointOnObject(g0,g-5)
    c: Coincident(g1,g0)
    c: Coincident(g1,g-4)
    c: Coincident(g2,g0)
    c: Vertical(g2)
    c: PointOnObject(g2,g-3)
    c: InternalAlignment(g4-g7 -> g3) x4
    c: Coincident(g3,g2)
    c: Coincident(g3,g0)
    c: Coincident(g3,g1)
    c: Horizontal(g4)
FEATURE [PartDesign::SubtractivePipe] SubtractivePipe005
  AuxilleryCurvelinear = true
  AuxillerySpineTangent = false
  BaseFeature = -> SubtractivePipe004
  Binormal = (0,0,0)
  Mode = 0
  Profile = -> Sketch149
  Refine = true
  Spine = -> Pad016 [Edge256,Edge251,Edge252]
  SpineTangent = false
  Suppressed = false
  Transformation = 0
  Transition = 0
FEATURE [PartDesign::SubtractiveLoft] SubtractiveLoft002
  BaseFeature = -> SubtractivePipe005
  Closed = false
  Profile = -> Sketch129
  Refine = true
  Ruled = false
  Sections = -> [Sketch130]
  Suppressed = false
FEATURE [PartDesign::SubtractiveLoft] SubtractiveLoft003
  BaseFeature = -> SubtractiveLoft002
  Closed = false
  Profile = -> Clone2D001
  Refine = true
  Ruled = false
  Sections = -> [Sketch131]
  Suppressed = false
FEATURE [PartDesign::Chamfer] Chamfer010
  Angle = 45
  Base = -> SubtractiveLoft003 [Edge203,Edge204,Edge202,Edge201,Edge195]
  BaseFeature = -> SubtractiveLoft003
  ChamferType = 0
  FlipDirection = false
  Refine = true
  Size = 1.5
  Size2 = 1
  SupportTransform = false
  Suppressed = false
  UseAllEdges = false
FEATURE [PartDesign::Chamfer] Chamfer011
  Angle = 45
  Base = -> Chamfer010 [Edge15]
  BaseFeature = -> Chamfer010
  ChamferType = 0
  FlipDirection = false
  Refine = true
  Size = 1.6
  Size2 = 1
  SupportTransform = false
  Suppressed = false
  UseAllEdges = false
FEATURE [PartDesign::Chamfer] Chamfer012
  Angle = 45
  Base = -> Chamfer011 [Edge10]
  BaseFeature = -> Chamfer011
  ChamferType = 0
  FlipDirection = false
  Refine = true
  Size = 3.5
  Size2 = 1
  SupportTransform = false
  Suppressed = false
  UseAllEdges = false
FEATURE [PartDesign::Chamfer] Chamfer013
  Angle = 45
  Base = -> Chamfer012 [Edge94]
  BaseFeature = -> Chamfer012
  ChamferType = 0
  FlipDirection = false
  Refine = true
  Size = 1.9
  Size2 = 1
  SupportTransform = false
  Suppressed = false
  UseAllEdges = false
FEATURE [PartDesign::Fillet] Fillet007
  Base = -> Chamfer013 [Edge83]
  BaseFeature = -> Chamfer013
  Radius = 1.1
  Refine = true
  SupportTransform = false
  Suppressed = false
  UseAllEdges = false
FEATURE [PartDesign::Fillet] Fillet008
  Base = -> Fillet007 [Edge75]
  BaseFeature = -> Fillet007
  Radius = 1.9
  Refine = true
  SupportTransform = false
  Suppressed = false
  UseAllEdges = false
FEATURE [PartDesign::Pocket] Pocket011
  BaseFeature = -> Fillet008
  Direction = (0,1,-2e-16)
  Length = 0.8
  Length2 = 5
  Profile = -> Sketch132
  ReferenceAxis = -> Sketch132 [N_Axis]
  Refine = true
  Suppressed = false
  Type = 0
FEATURE [PartDesign::Pocket] Pocket012
  BaseFeature = -> Pocket011
  Direction = (0,1,0)
  Length = 1
  Length2 = 5
  Profile = -> ShapeString
  ReferenceAxis = -> ShapeString [N_Axis]
  Refine = true
  Suppressed = false
  Type = 0
FEATURE [PartDesign::Body] Body007  label="lato DX"
  AllowCompound = false
  Group = -> [Binder001,Sketch114,Pad011,Chamfer014,Sketch115,Pocket006,Sketch116,Pad012,Sketch117,Pocket007,Sketch118,Pad013,Sketch119,Pocket008,Pad017,Chamfer009,Pocket009,Sketch123,Sketch120,Pad014,Pad018,Chamfer008,Pocket010,Sketch121,Pad015,Sketch122,Pad016,SubtractivePipe004,SubtractivePipe005,Sketch149,Sketch148,Sketch124,Sketch125,Sketch126,Sketch129,Sketch130,Clone2D001,Sketch131,SubtractiveLoft002,+11 more]
  Origin = -> Origin007
  Tip = -> Pocket012
FEATURE [Sketcher::SketchObject] Sketch150
  ArcFitTolerance = 1e-06
  AttachmentSupport = -> [Pad008]
  ExternalGeometry = -> [Pad008]
  FullyConstrained = true
  MakeInternals = false
  MapMode = 5
  Placement = pos=(0,3.6,0) rot=(0,0.707107,0.707107;3.14159rad)
  sketch-geometry (7):
    g0: LineSegment [constr] StartX=210.343 StartY=-66.0316 StartZ=0 EndX=210.343 EndY=-72.8316 EndZ=0
    g1: LineSegment [constr] StartX=210.343 StartY=-72.8316 StartZ=0 EndX=216.543 EndY=-72.8316 EndZ=0
    g2: LineSegment [constr] StartX=216.543 StartY=-72.8316 StartZ=0 EndX=216.543 EndY=-66.0316 EndZ=0
    g3: LineSegment [constr] StartX=216.543 StartY=-66.0316 StartZ=0 EndX=210.343 EndY=-66.0316 EndZ=0
    g4: LineSegment [constr] StartX=210.343 StartY=-72.8316 StartZ=0 EndX=216.543 EndY=-66.0316 EndZ=0
    g5: LineSegment [constr] StartX=210.343 StartY=-66.0316 StartZ=0 EndX=213.443 EndY=-69.4316 EndZ=0
    g6: Circle CenterX=213.443 CenterY=-69.4316 CenterZ=0 NormalX=0 NormalY=0 NormalZ=1 AngleXU=0 Radius=2
  constraints (18):
    c: Coincident(g0,g1)
    c: Coincident(g1,g2)
    c: Coincident(g2,g3)
    c: Coincident(g3,g0)
    c: Vertical(g0)
    c: Vertical(g2)
    c: Horizontal(g1)
    c: Horizontal(g3)
    c: Distance(g0,g2) = 6.2
    c: Distance(g1,g3) = 6.8
    c: DistanceY(g-3,g1) = 4
    c: Coincident(g4,g0)
    c: Coincident(g4,g2)
    c: Coincident(g5,g0)
    c: Symmetric(g0,g2,g5)
    c: Diameter(g6) = 4
    c: Coincident(g6,g5)
    c: Vertical(g5,g-3)
FEATURE [Sketcher::SketchObject] Sketch151
  ArcFitTolerance = 1e-06
  AttachmentSupport = -> [Pad008]
  ExternalGeometry = -> [Pad008]
  FullyConstrained = true
  MakeInternals = false
  MapMode = 5
  Placement = pos=(0,3.6,0) rot=(0,0.707107,0.707107;3.14159rad)
  sketch-geometry (10):
    g0: LineSegment [constr] StartX=211.143 StartY=-56.2316 StartZ=0 EndX=211.143 EndY=-65.4316 EndZ=0
    g1: LineSegment [constr] StartX=211.143 StartY=-65.4316 StartZ=0 EndX=215.743 EndY=-65.4316 EndZ=0
    g2: LineSegment [constr] StartX=215.743 StartY=-65.4316 StartZ=0 EndX=215.743 EndY=-56.2316 EndZ=0
    g3: LineSegment [constr] StartX=215.743 StartY=-56.2316 StartZ=0 EndX=211.143 EndY=-56.2316 EndZ=0
    g4: LineSegment StartX=212.243 StartY=-63.8316 StartZ=0 EndX=214.643 EndY=-63.8316 EndZ=0
    g5: LineSegment StartX=214.643 StartY=-63.8316 StartZ=0 EndX=214.643 EndY=-57.0316 EndZ=0
    g6: LineSegment StartX=214.643 StartY=-57.0316 StartZ=0 EndX=212.243 EndY=-57.0316 EndZ=0
    g7: LineSegment StartX=212.243 StartY=-57.0316 StartZ=0 EndX=212.243 EndY=-63.8316 EndZ=0
    g8: GeomPoint [constr] X=213.443 Y=-60.4316 Z=0
    g9: GeomPoint [constr] X=213.443 Y=-60.8316 Z=0
  constraints (26):
    c: Coincident(g0,g1)
    c: Coincident(g1,g2)
    c: Coincident(g2,g3)
    c: Coincident(g3,g0)
    c: Vertical(g0)
    c: Vertical(g2)
    c: Horizontal(g1)
    c: Horizontal(g3)
    c: Distance(g0,g2) = 4.6
    c: Distance(g1,g3) = 9.2
    c: DistanceY(g-3,g1) = 11.4
    c: Coincident(g4,g5)
    c: Coincident(g5,g6)
    c: Coincident(g6,g7)
    c: Coincident(g7,g4)
    c: Horizontal(g4)
    c: Horizontal(g6)
    c: Vertical(g5)
    c: Vertical(g7)
    c: Symmetric(g6,g4,g8)
    c: Distance(g5,g7) = 2.4
    c: Distance(g4,g6) = 6.8
    c: Symmetric(g2,g0,g9)
    c: Vertical(g8,g9)
    c: DistanceY(g1,g4) = 1.6
    c: Vertical(g9,g-3)
FEATURE [PartDesign::Pocket] Pocket019
  BaseFeature = -> Pocket013
  Direction = (0,-1,2e-16)
  Length = 3.6
  Length2 = 5
  Profile = -> Sketch151
  ReferenceAxis = -> Sketch151 [N_Axis]
  Refine = true
  Suppressed = false
  Type = 0
FEATURE [PartDesign::Pocket] Pocket018
  BaseFeature = -> Pocket019
  Direction = (0,-1,2e-16)
  Length = 3.6
  Length2 = 5
  Profile = -> Sketch150
  ReferenceAxis = -> Sketch150 [N_Axis]
  Refine = true
  Suppressed = false
  Type = 0
FEATURE [PartDesign::Point] DatumPoint
  AttacherType = Attacher::AttachEnginePoint
  AttachmentSupport = -> [Sketch150]
  MapMode = 36
  Placement = pos=(-213.443,3.6,-69.4316) rot=(0,1,0;3.14159rad)
FEATURE [PartDesign::Plane] DatumPlane002
  AttachmentSupport = -> [DatumPoint]
  Length = 260.281
  MapMode = 1
  Placement = pos=(-213.443,3.6,-69.4316) rot=(0,0,1;0rad)
  ResizeMode = 0
  Width = 71.8377
FEATURE [Sketcher::SketchObject] Sketch152
  ArcFitTolerance = 1e-06
  AttachmentSupport = -> [DatumPlane002]
  ExternalGeometry = -> [Sketch150]
  FullyConstrained = true
  MakeInternals = false
  MapMode = 5
  Placement = pos=(-213.443,3.6,-69.4316) rot=(0,0,1;0rad)
  sketch-geometry (7):
    g0: LineSegment StartX=0 StartY=0 StartZ=0 EndX=-4 EndY=3.8e-15 EndZ=0
    g1: ArcOfEllipse CenterX=0 CenterY=0 CenterZ=0 NormalX=0 NormalY=0 NormalZ=1 MajorRadius=4 MinorRadius=3.6 AngleXU=3.14159 StartAngle=2e-16 EndAngle=1.5708
    g2: LineSegment [constr] StartX=-4 StartY=9e-16 StartZ=0 EndX=4 EndY=-9e-16 EndZ=0
    g3: LineSegment [constr] StartX=0 StartY=-3.6 StartZ=0 EndX=0 EndY=3.6 EndZ=0
    g4: GeomPoint [constr] X=-1.74356 Y=2e-15 Z=0
    g5: GeomPoint [constr] X=1.74356 Y=-2e-15 Z=0
    g6: LineSegment StartX=0 StartY=0 StartZ=0 EndX=-4.4e-15 EndY=-3.6 EndZ=0
  constraints (11):
    c: PointOnObject(g1,g-2)
    c: Distance(g0) = 4
    c: PointOnObject(g0,g-1)
    c: InternalAlignment(g2-g5 -> g1) x4
    c: Coincident(g1,g0)
    c: Vertical(g3)
    c: Coincident(g1,g-1)
    c: Distance(g6) = 3.6
    c: Coincident(g6,g1)
    c: Coincident(g1,g6)
    c: Coincident(g0,g1)
FEATURE [PartDesign::Groove] Groove
  Angle = 360
  Angle2 = 60
  Axis = (0,1,0)
  Base = (-213.443,3.6,-69.4316)
  BaseFeature = -> Pocket018
  Profile = -> Sketch152
  ReferenceAxis = -> Sketch152 [V_Axis]
  Refine = true
  Reversed = true
  Suppressed = false
  Type = 0
FEATURE [PartDesign::Body] Body006  label="lato SX"
  AllowCompound = false
  Group = -> [Binder,Pad019,Chamfer015,Pocket002,Sketch133,Sketch091,Pad005,Sketch092,Pocket001,Sketch093,Sketch094,Pad006,Sketch095,Pad007,Sketch096,Pad008,Sketch097,Pad009,Chamfer005,Pocket004,Sketch098,Pad010,Chamfer006,Pocket003,SubtractivePipe,SubtractivePipe001,Sketch099,Sketch106,Sketch107,Sketch108,Clone2D,Sketch109,SubtractiveLoft,SubtractiveLoft001,Sketch110,Sketch111,Sketch112,Chamfer016,Chamfer017,+15 more]
  Origin = -> Origin006
  Tip = -> Groove
FEATURE [Sketcher::SketchObject] Sketch153  label="ripieno_per_sostegno_led_batteria"
  ArcFitTolerance = 1e-06
  AttachmentSupport = -> [XZ_Plane]
  ExternalGeometry = -> [Sketch036]
  FullyConstrained = true
  MakeInternals = false
  MapMode = 5
  Placement = pos=(0,0,0) rot=(1,0,0;1.5708rad)
  sketch-geometry (4):
    g0: LineSegment StartX=-217.343 StartY=-54.5944 StartZ=0 EndX=-217.343 EndY=-63.1944 EndZ=0
    g1: LineSegment StartX=-217.343 StartY=-63.1944 StartZ=0 EndX=-211.843 EndY=-63.1944 EndZ=0
    g2: LineSegment StartX=-211.843 StartY=-63.1944 StartZ=0 EndX=-211.843 EndY=-54.5944 EndZ=0
    g3: LineSegment StartX=-211.843 StartY=-54.5944 StartZ=0 EndX=-217.343 EndY=-54.5944 EndZ=0
  constraints (11):
    c: Coincident(g0,g1)
    c: Coincident(g1,g2)
    c: Coincident(g2,g3)
    c: Coincident(g3,g0)
    c: Vertical(g0)
    c: Horizontal(g1)
    c: Horizontal(g3)
    c: Tangent(g2,g-3)
    c: DistanceY(g2,g-3) = 4.5
    c: DistanceX(g3,g3) = 5.5
    c: DistanceY(g0,g0) = 8.6
FEATURE [PartDesign::Body] Body  label="Struttura pistola"
  AllowCompound = false
  Group = -> [Sketch,Sketch002,Sketch004,DatumPlane,Sketch005,DatumPlane001,CopyCut,Sketch008,Sketch009,Sketch010,Sketch011,Sketch012,Sketch013,Sketch014,Sketch015,Sketch016,Sketch017,Sketch018,Sketch019,Sketch020,Sketch022,Sketch023,Sketch024,Sketch025,Sketch026,Sketch027,Sketch029,Sketch030,Sketch031,Sketch032,Sketch033,Sketch034,Sketch035,Sketch036,Sketch037,Sketch038,Sketch039,Sketch040,Sketch041,Sketch042,+28 more]
  Origin = -> Origin
FEATURE [Part::Extrusion] Extrude088  label="Extrude088 - ripieno_per_sostegno_led_batteria"
  Base = -> Sketch153
  Dir = (0,-1,2e-16)
  DirMode = 2
  FaceMakerClass = Part::FaceMakerBullseye
  FaceMakerMode = 3
  LengthFwd = 4
  LengthRev = 0
  Placement = pos=(0,12.6,0) rot=(0,0,1;0rad)
  Solid = true
  Symmetric = false
FEATURE [Part::MultiFuse] Fusion004
  Refine = true
  Shapes = -> [Cut050,Extrude088]
FEATURE [Part::Cut] Cut051
  Base = -> Fusion004
  Refine = true
  Tool = -> Extrude087
FEATURE [Part::Cut] Cut052
  Base = -> Cut051
  Refine = true
  Tool = -> Extrude086
note: 2 file-system paths scrubbed to <path> (originals preserved in the JSON sidecar)
